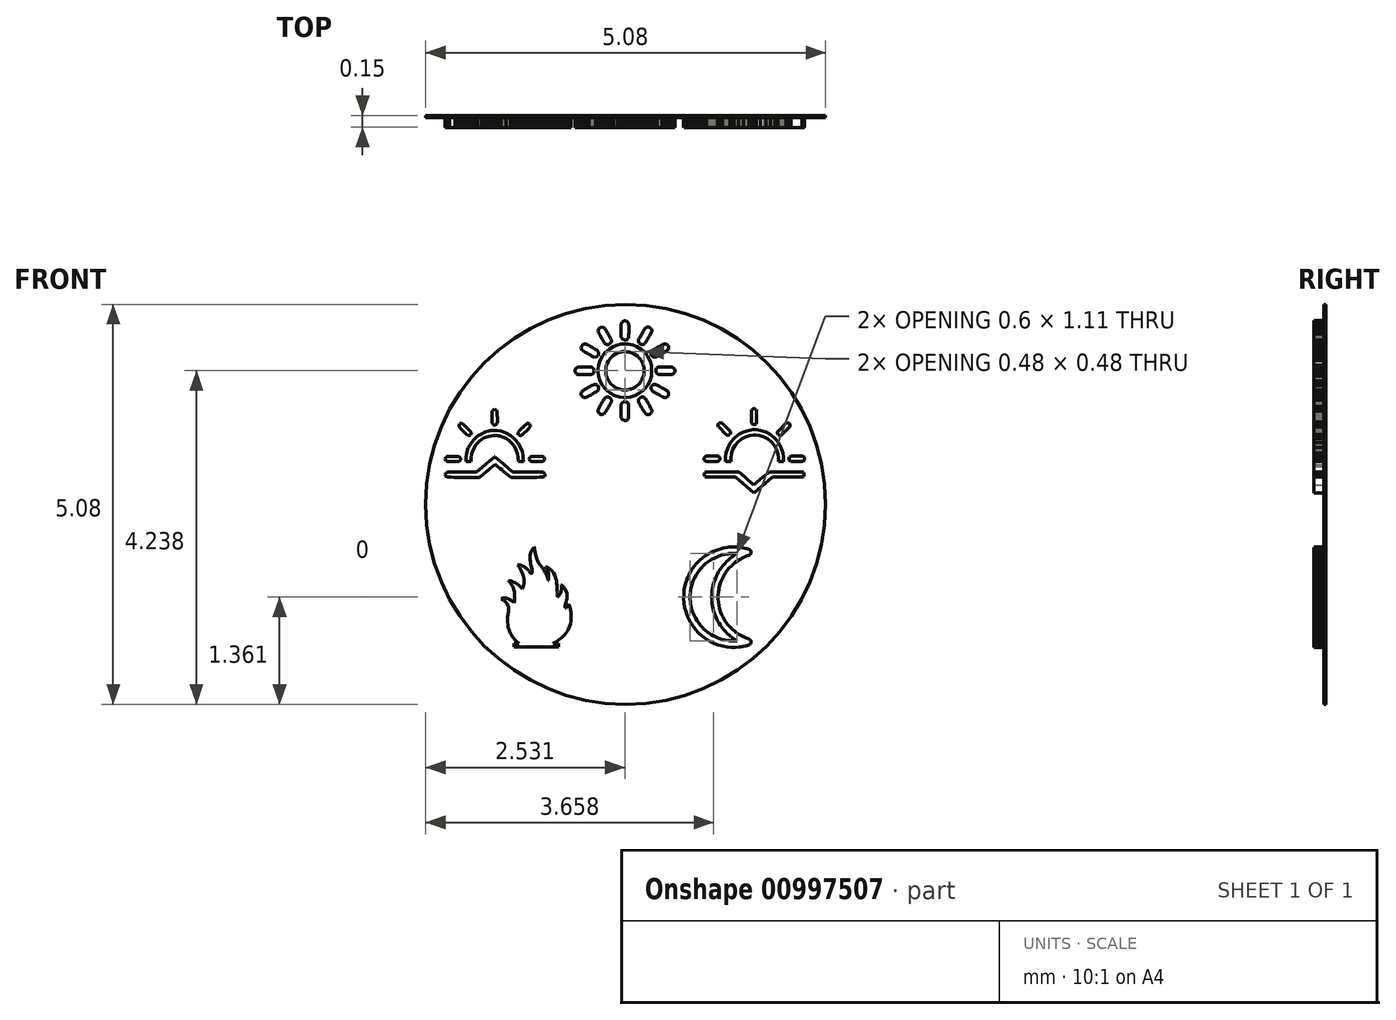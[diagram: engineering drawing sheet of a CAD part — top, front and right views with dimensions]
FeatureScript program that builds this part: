
annotation { "Feature Type Name" : "Feature", "Feature Type Description" : "" }
export const myFeature = defineFeature(function(context is Context, id is Id, definition is map)
    precondition{}
    {
        {
            var Q0;
            Q0=qCreatedBy(makeId("Front.planeOp"),FACE);
            var sketch = newSketch(context, id + "F0", { "sketchPlane" : qUnion([Q0])});
            skCircle(sketch, "E0", {"center": v(0, 0) * mm, "radius": 2.54 * mm});
            skSolve(sketch);
        }
        {
            var Q0;
            Q0=makeQuery(id+"F0.imprint","IMPRINT",FACE,{"disambiguationData":[TD([[makeQuery(id+"F0.imprint","IMPRINT",EDGE,{"derivedFrom":sQuery(id+"F0.wireOp",EDGE,"E0")}),1.0]])]});
            extrude(context, id + "F1", {"entities" : qUnion([Q0]), "depth" : 0.03 * mm, "offsetDistance" : 25.4 * mm});
        }
        {
            var Q0;
            Q0=makeQuery(id+"F1.opExtrude","CAP_FACE",FACE,{"disambiguationData":[OSD([sQuery(id+"F0.wireOp",EDGE,"E0"),sQuery(id+"F0.wireOp",EDGE,"ANRrlyus-TsXj-KHkA-7Rkr-odwGKdxKpd92")])],"isStart":false});
            var sketch = newSketch(context, id + "F2", { "sketchPlane" : qUnion([Q0])});
            skLineSegment(sketch, "E1", {"start": v(1.99, 0.89) * mm, "end": v(2.08, 0.98) * mm});
            skLineSegment(sketch, "E2", {"start": v(2.08, 0.98) * mm, "end": v(2.08, 0.98) * mm});
            skLineSegment(sketch, "E3", {"start": v(2.08, 0.98) * mm, "end": v(2.09, 1) * mm});
            skLineSegment(sketch, "E4", {"start": v(2.09, 1) * mm, "end": v(2.09, 1) * mm});
            skLineSegment(sketch, "E5", {"start": v(2.09, 1) * mm, "end": v(2.09, 1.02) * mm});
            skLineSegment(sketch, "E6", {"start": v(2.09, 1.02) * mm, "end": v(2.08, 1.03) * mm});
            skLineSegment(sketch, "E7", {"start": v(2.08, 1.03) * mm, "end": v(2.08, 1.03) * mm});
            skLineSegment(sketch, "E8", {"start": v(2.08, 1.03) * mm, "end": v(2.07, 1.04) * mm});
            skLineSegment(sketch, "E9", {"start": v(2.07, 1.04) * mm, "end": v(2.06, 1.04) * mm});
            skLineSegment(sketch, "E10", {"start": v(2.06, 1.04) * mm, "end": v(2.04, 1.04) * mm});
            skLineSegment(sketch, "E11", {"start": v(2.04, 1.04) * mm, "end": v(2.03, 1.03) * mm});
            skLineSegment(sketch, "E12", {"start": v(2.03, 1.03) * mm, "end": v(2.03, 1.03) * mm});
            skLineSegment(sketch, "E13", {"start": v(2.03, 1.03) * mm, "end": v(1.94, 0.93) * mm});
            skLineSegment(sketch, "E14", {"start": v(1.94, 0.93) * mm, "end": v(1.94, 0.93) * mm});
            skLineSegment(sketch, "E15", {"start": v(1.94, 0.93) * mm, "end": v(1.93, 0.92) * mm});
            skLineSegment(sketch, "E16", {"start": v(1.93, 0.92) * mm, "end": v(1.93, 0.91) * mm});
            skLineSegment(sketch, "E17", {"start": v(1.93, 0.91) * mm, "end": v(1.93, 0.9) * mm});
            skLineSegment(sketch, "E18", {"start": v(1.93, 0.9) * mm, "end": v(1.94, 0.9) * mm});
            skLineSegment(sketch, "E19", {"start": v(1.94, 0.9) * mm, "end": v(1.94, 0.89) * mm});
            skLineSegment(sketch, "E20", {"start": v(1.94, 0.89) * mm, "end": v(1.94, 0.89) * mm});
            skLineSegment(sketch, "E21", {"start": v(1.94, 0.89) * mm, "end": v(1.95, 0.88) * mm});
            skLineSegment(sketch, "E22", {"start": v(1.95, 0.88) * mm, "end": v(1.96, 0.88) * mm});
            skLineSegment(sketch, "E23", {"start": v(1.96, 0.88) * mm, "end": v(1.98, 0.88) * mm});
            skLineSegment(sketch, "E24", {"start": v(1.98, 0.88) * mm, "end": v(1.98, 0.89) * mm});
            skLineSegment(sketch, "E25", {"start": v(1.98, 0.89) * mm, "end": v(1.99, 0.89) * mm});
            skLineSegment(sketch, "E26", {"start": v(1.63, 1.01) * mm, "end": v(1.63, 1.01) * mm});
            skLineSegment(sketch, "E27", {"start": v(1.63, 1.01) * mm, "end": v(1.65, 1.02) * mm});
            skLineSegment(sketch, "E28", {"start": v(1.65, 1.02) * mm, "end": v(1.66, 1.02) * mm});
            skLineSegment(sketch, "E29", {"start": v(1.66, 1.02) * mm, "end": v(1.66, 1.03) * mm});
            skLineSegment(sketch, "E30", {"start": v(1.66, 1.03) * mm, "end": v(1.66, 1.04) * mm});
            skLineSegment(sketch, "E31", {"start": v(1.66, 1.04) * mm, "end": v(1.66, 1.05) * mm});
            skLineSegment(sketch, "E32", {"start": v(1.66, 1.05) * mm, "end": v(1.66, 1.18) * mm});
            skLineSegment(sketch, "E33", {"start": v(1.66, 1.18) * mm, "end": v(1.66, 1.19) * mm});
            skLineSegment(sketch, "E34", {"start": v(1.66, 1.19) * mm, "end": v(1.66, 1.2) * mm});
            skLineSegment(sketch, "E35", {"start": v(1.66, 1.2) * mm, "end": v(1.66, 1.2) * mm});
            skLineSegment(sketch, "E36", {"start": v(1.66, 1.2) * mm, "end": v(1.65, 1.21) * mm});
            skLineSegment(sketch, "E37", {"start": v(1.65, 1.21) * mm, "end": v(1.63, 1.22) * mm});
            skLineSegment(sketch, "E38", {"start": v(1.63, 1.22) * mm, "end": v(1.63, 1.22) * mm});
            skLineSegment(sketch, "E39", {"start": v(1.63, 1.22) * mm, "end": v(1.62, 1.21) * mm});
            skLineSegment(sketch, "E40", {"start": v(1.62, 1.21) * mm, "end": v(1.6, 1.2) * mm});
            skLineSegment(sketch, "E41", {"start": v(1.6, 1.2) * mm, "end": v(1.6, 1.2) * mm});
            skLineSegment(sketch, "E42", {"start": v(1.6, 1.2) * mm, "end": v(1.6, 1.19) * mm});
            skLineSegment(sketch, "E43", {"start": v(1.6, 1.19) * mm, "end": v(1.6, 1.18) * mm});
            skLineSegment(sketch, "E44", {"start": v(1.6, 1.18) * mm, "end": v(1.6, 1.05) * mm});
            skLineSegment(sketch, "E45", {"start": v(1.6, 1.05) * mm, "end": v(1.6, 1.04) * mm});
            skLineSegment(sketch, "E46", {"start": v(1.6, 1.04) * mm, "end": v(1.6, 1.03) * mm});
            skLineSegment(sketch, "E47", {"start": v(1.6, 1.03) * mm, "end": v(1.6, 1.02) * mm});
            skLineSegment(sketch, "E48", {"start": v(1.6, 1.02) * mm, "end": v(1.62, 1.02) * mm});
            skLineSegment(sketch, "E49", {"start": v(1.62, 1.02) * mm, "end": v(1.63, 1.01) * mm});
            skLineSegment(sketch, "E50", {"start": v(2.07, 0.58) * mm, "end": v(2.07, 0.58) * mm});
            skLineSegment(sketch, "E51", {"start": v(2.07, 0.58) * mm, "end": v(2.07, 0.57) * mm});
            skLineSegment(sketch, "E52", {"start": v(2.07, 0.57) * mm, "end": v(2.08, 0.56) * mm});
            skLineSegment(sketch, "E53", {"start": v(2.08, 0.56) * mm, "end": v(2.1, 0.55) * mm});
            skLineSegment(sketch, "E54", {"start": v(2.1, 0.55) * mm, "end": v(2.1, 0.55) * mm});
            skLineSegment(sketch, "E55", {"start": v(2.1, 0.55) * mm, "end": v(2.24, 0.55) * mm});
            skLineSegment(sketch, "E56", {"start": v(2.24, 0.55) * mm, "end": v(2.24, 0.55) * mm});
            skLineSegment(sketch, "E57", {"start": v(2.24, 0.55) * mm, "end": v(2.25, 0.55) * mm});
            skLineSegment(sketch, "E58", {"start": v(2.25, 0.55) * mm, "end": v(2.26, 0.56) * mm});
            skLineSegment(sketch, "E59", {"start": v(2.26, 0.56) * mm, "end": v(2.27, 0.57) * mm});
            skLineSegment(sketch, "E60", {"start": v(2.27, 0.57) * mm, "end": v(2.27, 0.58) * mm});
            skLineSegment(sketch, "E61", {"start": v(2.27, 0.58) * mm, "end": v(2.27, 0.58) * mm});
            skLineSegment(sketch, "E62", {"start": v(2.27, 0.58) * mm, "end": v(2.27, 0.6) * mm});
            skLineSegment(sketch, "E63", {"start": v(2.27, 0.6) * mm, "end": v(2.26, 0.6) * mm});
            skLineSegment(sketch, "E64", {"start": v(2.26, 0.6) * mm, "end": v(2.25, 0.61) * mm});
            skLineSegment(sketch, "E65", {"start": v(2.25, 0.61) * mm, "end": v(2.24, 0.61) * mm});
            skLineSegment(sketch, "E66", {"start": v(2.24, 0.61) * mm, "end": v(2.24, 0.61) * mm});
            skLineSegment(sketch, "E67", {"start": v(2.24, 0.61) * mm, "end": v(2.1, 0.61) * mm});
            skLineSegment(sketch, "E68", {"start": v(2.1, 0.61) * mm, "end": v(2.1, 0.61) * mm});
            skLineSegment(sketch, "E69", {"start": v(2.1, 0.61) * mm, "end": v(2.08, 0.6) * mm});
            skLineSegment(sketch, "E70", {"start": v(2.08, 0.6) * mm, "end": v(2.07, 0.6) * mm});
            skLineSegment(sketch, "E71", {"start": v(2.07, 0.6) * mm, "end": v(2.07, 0.58) * mm});
            skLineSegment(sketch, "E72", {"start": v(1.28, 0.89) * mm, "end": v(1.28, 0.89) * mm});
            skLineSegment(sketch, "E73", {"start": v(1.28, 0.89) * mm, "end": v(1.29, 0.88) * mm});
            skLineSegment(sketch, "E74", {"start": v(1.29, 0.88) * mm, "end": v(1.3, 0.88) * mm});
            skLineSegment(sketch, "E75", {"start": v(1.3, 0.88) * mm, "end": v(1.31, 0.88) * mm});
            skLineSegment(sketch, "E76", {"start": v(1.31, 0.88) * mm, "end": v(1.32, 0.89) * mm});
            skLineSegment(sketch, "E77", {"start": v(1.32, 0.89) * mm, "end": v(1.32, 0.89) * mm});
            skLineSegment(sketch, "E78", {"start": v(1.32, 0.89) * mm, "end": v(1.33, 0.9) * mm});
            skLineSegment(sketch, "E79", {"start": v(1.33, 0.9) * mm, "end": v(1.33, 0.9) * mm});
            skLineSegment(sketch, "E80", {"start": v(1.33, 0.9) * mm, "end": v(1.33, 0.91) * mm});
            skLineSegment(sketch, "E81", {"start": v(1.33, 0.91) * mm, "end": v(1.33, 0.92) * mm});
            skLineSegment(sketch, "E82", {"start": v(1.33, 0.92) * mm, "end": v(1.33, 0.93) * mm});
            skLineSegment(sketch, "E83", {"start": v(1.33, 0.93) * mm, "end": v(1.32, 0.93) * mm});
            skLineSegment(sketch, "E84", {"start": v(1.32, 0.93) * mm, "end": v(1.23, 1.03) * mm});
            skLineSegment(sketch, "E85", {"start": v(1.23, 1.03) * mm, "end": v(1.23, 1.03) * mm});
            skLineSegment(sketch, "E86", {"start": v(1.23, 1.03) * mm, "end": v(1.22, 1.04) * mm});
            skLineSegment(sketch, "E87", {"start": v(1.22, 1.04) * mm, "end": v(1.2, 1.04) * mm});
            skLineSegment(sketch, "E88", {"start": v(1.2, 1.04) * mm, "end": v(1.2, 1.04) * mm});
            skLineSegment(sketch, "E89", {"start": v(1.2, 1.04) * mm, "end": v(1.19, 1.03) * mm});
            skLineSegment(sketch, "E90", {"start": v(1.19, 1.03) * mm, "end": v(1.18, 1.03) * mm});
            skLineSegment(sketch, "E91", {"start": v(1.18, 1.03) * mm, "end": v(1.18, 1.03) * mm});
            skLineSegment(sketch, "E92", {"start": v(1.18, 1.03) * mm, "end": v(1.18, 1.02) * mm});
            skLineSegment(sketch, "E93", {"start": v(1.18, 1.02) * mm, "end": v(1.17, 1) * mm});
            skLineSegment(sketch, "E94", {"start": v(1.17, 1) * mm, "end": v(1.18, 1) * mm});
            skLineSegment(sketch, "E95", {"start": v(1.18, 1) * mm, "end": v(1.18, 0.98) * mm});
            skLineSegment(sketch, "E96", {"start": v(1.18, 0.98) * mm, "end": v(1.18, 0.98) * mm});
            skLineSegment(sketch, "E97", {"start": v(1.18, 0.98) * mm, "end": v(1.28, 0.89) * mm});
            skLineSegment(sketch, "E98", {"start": v(1.03, 0.55) * mm, "end": v(1.16, 0.55) * mm});
            skLineSegment(sketch, "E99", {"start": v(1.16, 0.55) * mm, "end": v(1.17, 0.55) * mm});
            skLineSegment(sketch, "E100", {"start": v(1.17, 0.55) * mm, "end": v(1.18, 0.55) * mm});
            skLineSegment(sketch, "E101", {"start": v(1.18, 0.55) * mm, "end": v(1.19, 0.56) * mm});
            skLineSegment(sketch, "E102", {"start": v(1.19, 0.56) * mm, "end": v(1.2, 0.57) * mm});
            skLineSegment(sketch, "E103", {"start": v(1.2, 0.57) * mm, "end": v(1.2, 0.58) * mm});
            skLineSegment(sketch, "E104", {"start": v(1.2, 0.58) * mm, "end": v(1.2, 0.58) * mm});
            skLineSegment(sketch, "E105", {"start": v(1.2, 0.58) * mm, "end": v(1.2, 0.6) * mm});
            skLineSegment(sketch, "E106", {"start": v(1.2, 0.6) * mm, "end": v(1.19, 0.6) * mm});
            skLineSegment(sketch, "E107", {"start": v(1.19, 0.6) * mm, "end": v(1.18, 0.61) * mm});
            skLineSegment(sketch, "E108", {"start": v(1.18, 0.61) * mm, "end": v(1.17, 0.61) * mm});
            skLineSegment(sketch, "E109", {"start": v(1.17, 0.61) * mm, "end": v(1.16, 0.61) * mm});
            skLineSegment(sketch, "E110", {"start": v(1.16, 0.61) * mm, "end": v(1.03, 0.61) * mm});
            skLineSegment(sketch, "E111", {"start": v(1.03, 0.61) * mm, "end": v(1.03, 0.61) * mm});
            skLineSegment(sketch, "E112", {"start": v(1.03, 0.61) * mm, "end": v(1.02, 0.61) * mm});
            skLineSegment(sketch, "E113", {"start": v(1.02, 0.61) * mm, "end": v(1, 0.6) * mm});
            skLineSegment(sketch, "E114", {"start": v(1, 0.6) * mm, "end": v(1, 0.6) * mm});
            skLineSegment(sketch, "E115", {"start": v(1, 0.6) * mm, "end": v(1, 0.58) * mm});
            skLineSegment(sketch, "E116", {"start": v(1, 0.58) * mm, "end": v(1, 0.58) * mm});
            skLineSegment(sketch, "E117", {"start": v(1, 0.58) * mm, "end": v(1, 0.57) * mm});
            skLineSegment(sketch, "E118", {"start": v(1, 0.57) * mm, "end": v(1, 0.56) * mm});
            skLineSegment(sketch, "E119", {"start": v(1, 0.56) * mm, "end": v(1.02, 0.55) * mm});
            skLineSegment(sketch, "E120", {"start": v(1.02, 0.55) * mm, "end": v(1.03, 0.55) * mm});
            skLineSegment(sketch, "E121", {"start": v(1.03, 0.55) * mm, "end": v(1.03, 0.55) * mm});
            skLineSegment(sketch, "E122", {"start": v(2.23, 0.41) * mm, "end": v(1.82, 0.41) * mm});
            skLineSegment(sketch, "E123", {"start": v(1.82, 0.41) * mm, "end": v(1.74, 0.35) * mm});
            skLineSegment(sketch, "E124", {"start": v(1.74, 0.35) * mm, "end": v(1.62, 0.25) * mm});
            skLineSegment(sketch, "E125", {"start": v(1.62, 0.25) * mm, "end": v(1.52, 0.35) * mm});
            skLineSegment(sketch, "E126", {"start": v(1.52, 0.35) * mm, "end": v(1.44, 0.41) * mm});
            skLineSegment(sketch, "E127", {"start": v(1.44, 0.41) * mm, "end": v(1.03, 0.41) * mm});
            skLineSegment(sketch, "E128", {"start": v(1.03, 0.41) * mm, "end": v(1.03, 0.41) * mm});
            skLineSegment(sketch, "E129", {"start": v(1.03, 0.41) * mm, "end": v(1.02, 0.41) * mm});
            skLineSegment(sketch, "E130", {"start": v(1.02, 0.41) * mm, "end": v(1, 0.4) * mm});
            skLineSegment(sketch, "E131", {"start": v(1, 0.4) * mm, "end": v(1, 0.4) * mm});
            skLineSegment(sketch, "E132", {"start": v(1, 0.4) * mm, "end": v(1, 0.38) * mm});
            skLineSegment(sketch, "E133", {"start": v(1, 0.38) * mm, "end": v(1, 0.38) * mm});
            skLineSegment(sketch, "E134", {"start": v(1, 0.38) * mm, "end": v(1, 0.37) * mm});
            skLineSegment(sketch, "E135", {"start": v(1, 0.37) * mm, "end": v(1, 0.36) * mm});
            skLineSegment(sketch, "E136", {"start": v(1, 0.36) * mm, "end": v(1.02, 0.35) * mm});
            skLineSegment(sketch, "E137", {"start": v(1.02, 0.35) * mm, "end": v(1.03, 0.35) * mm});
            skLineSegment(sketch, "E138", {"start": v(1.03, 0.35) * mm, "end": v(1.03, 0.35) * mm});
            skLineSegment(sketch, "E139", {"start": v(1.03, 0.35) * mm, "end": v(1.4, 0.35) * mm});
            skLineSegment(sketch, "E140", {"start": v(1.4, 0.35) * mm, "end": v(1.63, 0.15) * mm});
            skLineSegment(sketch, "E141", {"start": v(1.63, 0.15) * mm, "end": v(1.86, 0.35) * mm});
            skLineSegment(sketch, "E142", {"start": v(1.86, 0.35) * mm, "end": v(2.23, 0.35) * mm});
            skLineSegment(sketch, "E143", {"start": v(2.23, 0.35) * mm, "end": v(2.24, 0.35) * mm});
            skLineSegment(sketch, "E144", {"start": v(2.24, 0.35) * mm, "end": v(2.25, 0.35) * mm});
            skLineSegment(sketch, "E145", {"start": v(2.25, 0.35) * mm, "end": v(2.26, 0.36) * mm});
            skLineSegment(sketch, "E146", {"start": v(2.26, 0.36) * mm, "end": v(2.26, 0.37) * mm});
            skLineSegment(sketch, "E147", {"start": v(2.26, 0.37) * mm, "end": v(2.27, 0.38) * mm});
            skLineSegment(sketch, "E148", {"start": v(2.27, 0.38) * mm, "end": v(2.27, 0.38) * mm});
            skLineSegment(sketch, "E149", {"start": v(2.27, 0.38) * mm, "end": v(2.26, 0.4) * mm});
            skLineSegment(sketch, "E150", {"start": v(2.26, 0.4) * mm, "end": v(2.26, 0.4) * mm});
            skLineSegment(sketch, "E151", {"start": v(2.26, 0.4) * mm, "end": v(2.25, 0.41) * mm});
            skLineSegment(sketch, "E152", {"start": v(2.25, 0.41) * mm, "end": v(2.24, 0.41) * mm});
            skLineSegment(sketch, "E153", {"start": v(2.24, 0.41) * mm, "end": v(2.23, 0.41) * mm});
            skLineSegment(sketch, "E154", {"start": v(1.27, 0.55) * mm, "end": v(1.34, 0.55) * mm});
            skLineSegment(sketch, "E155", {"start": v(1.34, 0.55) * mm, "end": v(1.34, 0.55) * mm});
            skLineSegment(sketch, "E156", {"start": v(1.34, 0.55) * mm, "end": v(1.34, 0.56) * mm});
            skLineSegment(sketch, "E157", {"start": v(1.34, 0.56) * mm, "end": v(1.34, 0.58) * mm});
            skLineSegment(sketch, "E158", {"start": v(1.34, 0.58) * mm, "end": v(1.34, 0.58) * mm});
            skLineSegment(sketch, "E159", {"start": v(1.34, 0.58) * mm, "end": v(1.34, 0.6) * mm});
            skLineSegment(sketch, "E160", {"start": v(1.34, 0.6) * mm, "end": v(1.34, 0.64) * mm});
            skLineSegment(sketch, "E161", {"start": v(1.34, 0.64) * mm, "end": v(1.36, 0.7) * mm});
            skLineSegment(sketch, "E162", {"start": v(1.36, 0.7) * mm, "end": v(1.39, 0.75) * mm});
            skLineSegment(sketch, "E163", {"start": v(1.39, 0.75) * mm, "end": v(1.42, 0.8) * mm});
            skLineSegment(sketch, "E164", {"start": v(1.42, 0.8) * mm, "end": v(1.47, 0.83) * mm});
            skLineSegment(sketch, "E165", {"start": v(1.47, 0.83) * mm, "end": v(1.52, 0.86) * mm});
            skLineSegment(sketch, "E166", {"start": v(1.52, 0.86) * mm, "end": v(1.58, 0.88) * mm});
            skLineSegment(sketch, "E167", {"start": v(1.58, 0.88) * mm, "end": v(1.62, 0.88) * mm});
            skLineSegment(sketch, "E168", {"start": v(1.62, 0.88) * mm, "end": v(1.64, 0.88) * mm});
            skLineSegment(sketch, "E169", {"start": v(1.64, 0.88) * mm, "end": v(1.65, 0.88) * mm});
            skLineSegment(sketch, "E170", {"start": v(1.65, 0.88) * mm, "end": v(1.7, 0.88) * mm});
            skLineSegment(sketch, "E171", {"start": v(1.7, 0.88) * mm, "end": v(1.76, 0.86) * mm});
            skLineSegment(sketch, "E172", {"start": v(1.76, 0.86) * mm, "end": v(1.8, 0.83) * mm});
            skLineSegment(sketch, "E173", {"start": v(1.8, 0.83) * mm, "end": v(1.85, 0.8) * mm});
            skLineSegment(sketch, "E174", {"start": v(1.85, 0.8) * mm, "end": v(1.89, 0.75) * mm});
            skLineSegment(sketch, "E175", {"start": v(1.89, 0.75) * mm, "end": v(1.92, 0.7) * mm});
            skLineSegment(sketch, "E176", {"start": v(1.92, 0.7) * mm, "end": v(1.93, 0.64) * mm});
            skLineSegment(sketch, "E177", {"start": v(1.93, 0.64) * mm, "end": v(1.94, 0.6) * mm});
            skLineSegment(sketch, "E178", {"start": v(1.94, 0.6) * mm, "end": v(1.94, 0.58) * mm});
            skLineSegment(sketch, "E179", {"start": v(1.94, 0.58) * mm, "end": v(1.94, 0.58) * mm});
            skLineSegment(sketch, "E180", {"start": v(1.94, 0.58) * mm, "end": v(1.94, 0.56) * mm});
            skLineSegment(sketch, "E181", {"start": v(1.94, 0.56) * mm, "end": v(1.94, 0.55) * mm});
            skLineSegment(sketch, "E182", {"start": v(1.94, 0.55) * mm, "end": v(1.94, 0.55) * mm});
            skLineSegment(sketch, "E183", {"start": v(1.94, 0.55) * mm, "end": v(2, 0.55) * mm});
            skLineSegment(sketch, "E184", {"start": v(2, 0.55) * mm, "end": v(2, 0.55) * mm});
            skLineSegment(sketch, "E185", {"start": v(2, 0.55) * mm, "end": v(2, 0.56) * mm});
            skLineSegment(sketch, "E186", {"start": v(2, 0.56) * mm, "end": v(2, 0.58) * mm});
            skLineSegment(sketch, "E187", {"start": v(2, 0.58) * mm, "end": v(2, 0.58) * mm});
            skLineSegment(sketch, "E188", {"start": v(2, 0.58) * mm, "end": v(2, 0.6) * mm});
            skLineSegment(sketch, "E189", {"start": v(2, 0.6) * mm, "end": v(2, 0.65) * mm});
            skLineSegment(sketch, "E190", {"start": v(2, 0.65) * mm, "end": v(1.98, 0.72) * mm});
            skLineSegment(sketch, "E191", {"start": v(1.98, 0.72) * mm, "end": v(1.94, 0.79) * mm});
            skLineSegment(sketch, "E192", {"start": v(1.94, 0.79) * mm, "end": v(1.9, 0.84) * mm});
            skLineSegment(sketch, "E193", {"start": v(1.9, 0.84) * mm, "end": v(1.84, 0.88) * mm});
            skLineSegment(sketch, "E194", {"start": v(1.84, 0.88) * mm, "end": v(1.78, 0.92) * mm});
            skLineSegment(sketch, "E195", {"start": v(1.78, 0.92) * mm, "end": v(1.71, 0.94) * mm});
            skLineSegment(sketch, "E196", {"start": v(1.71, 0.94) * mm, "end": v(1.66, 0.95) * mm});
            skLineSegment(sketch, "E197", {"start": v(1.66, 0.95) * mm, "end": v(1.64, 0.95) * mm});
            skLineSegment(sketch, "E198", {"start": v(1.64, 0.95) * mm, "end": v(1.62, 0.95) * mm});
            skLineSegment(sketch, "E199", {"start": v(1.62, 0.95) * mm, "end": v(1.56, 0.94) * mm});
            skLineSegment(sketch, "E200", {"start": v(1.56, 0.94) * mm, "end": v(1.5, 0.92) * mm});
            skLineSegment(sketch, "E201", {"start": v(1.5, 0.92) * mm, "end": v(1.43, 0.88) * mm});
            skLineSegment(sketch, "E202", {"start": v(1.43, 0.88) * mm, "end": v(1.38, 0.84) * mm});
            skLineSegment(sketch, "E203", {"start": v(1.38, 0.84) * mm, "end": v(1.33, 0.79) * mm});
            skLineSegment(sketch, "E204", {"start": v(1.33, 0.79) * mm, "end": v(1.3, 0.72) * mm});
            skLineSegment(sketch, "E205", {"start": v(1.3, 0.72) * mm, "end": v(1.28, 0.65) * mm});
            skLineSegment(sketch, "E206", {"start": v(1.28, 0.65) * mm, "end": v(1.27, 0.6) * mm});
            skLineSegment(sketch, "E207", {"start": v(1.27, 0.6) * mm, "end": v(1.27, 0.58) * mm});
            skLineSegment(sketch, "E208", {"start": v(1.27, 0.58) * mm, "end": v(1.27, 0.58) * mm});
            skLineSegment(sketch, "E209", {"start": v(1.27, 0.58) * mm, "end": v(1.27, 0.57) * mm});
            skLineSegment(sketch, "E210", {"start": v(1.27, 0.57) * mm, "end": v(1.27, 0.56) * mm});
            skLineSegment(sketch, "E211", {"start": v(1.27, 0.56) * mm, "end": v(1.27, 0.56) * mm});
            skLineSegment(sketch, "E212", {"start": v(1.27, 0.56) * mm, "end": v(1.27, 0.55) * mm});
            skLineSegment(sketch, "E213", {"start": v(1.27, 0.55) * mm, "end": v(1.27, 0.55) * mm});
            skSolve(sketch);
        }
        {
            var Q0;
            Q0=makeQuery(id+"F1.opExtrude","CAP_FACE",FACE,{"disambiguationData":[OSD([sQuery(id+"F0.wireOp",EDGE,"E0"),sQuery(id+"F0.wireOp",EDGE,"ANRrlyus-TsXj-KHkA-7Rkr-odwGKdxKpd92")])],"isStart":false});
            var sketch = newSketch(context, id + "F3", { "sketchPlane" : qUnion([Q0])});
            skLineSegment(sketch, "E214", {"start": v(-1.69, 1.2) * mm, "end": v(-1.69, 1.2) * mm});
            skLineSegment(sketch, "E215", {"start": v(-1.69, 1.2) * mm, "end": v(-1.7, 1.19) * mm});
            skLineSegment(sketch, "E216", {"start": v(-1.7, 1.19) * mm, "end": v(-1.7, 1.18) * mm});
            skLineSegment(sketch, "E217", {"start": v(-1.7, 1.18) * mm, "end": v(-1.7, 1.17) * mm});
            skLineSegment(sketch, "E218", {"start": v(-1.7, 1.17) * mm, "end": v(-1.7, 1.16) * mm});
            skLineSegment(sketch, "E219", {"start": v(-1.7, 1.16) * mm, "end": v(-1.7, 1.15) * mm});
            skLineSegment(sketch, "E220", {"start": v(-1.7, 1.15) * mm, "end": v(-1.7, 1.13) * mm});
            skLineSegment(sketch, "E221", {"start": v(-1.7, 1.13) * mm, "end": v(-1.7, 1.11) * mm});
            skLineSegment(sketch, "E222", {"start": v(-1.7, 1.11) * mm, "end": v(-1.7, 1.1) * mm});
            skLineSegment(sketch, "E223", {"start": v(-1.7, 1.1) * mm, "end": v(-1.7, 1.1) * mm});
            skLineSegment(sketch, "E224", {"start": v(-1.7, 1.1) * mm, "end": v(-1.7, 1.08) * mm});
            skLineSegment(sketch, "E225", {"start": v(-1.7, 1.08) * mm, "end": v(-1.7, 1.07) * mm});
            skLineSegment(sketch, "E226", {"start": v(-1.7, 1.07) * mm, "end": v(-1.7, 1.05) * mm});
            skLineSegment(sketch, "E227", {"start": v(-1.7, 1.05) * mm, "end": v(-1.7, 1.04) * mm});
            skLineSegment(sketch, "E228", {"start": v(-1.7, 1.04) * mm, "end": v(-1.7, 1.03) * mm});
            skLineSegment(sketch, "E229", {"start": v(-1.7, 1.03) * mm, "end": v(-1.7, 1.03) * mm});
            skLineSegment(sketch, "E230", {"start": v(-1.7, 1.03) * mm, "end": v(-1.69, 1.02) * mm});
            skLineSegment(sketch, "E231", {"start": v(-1.69, 1.02) * mm, "end": v(-1.69, 1.02) * mm});
            skLineSegment(sketch, "E232", {"start": v(-1.69, 1.02) * mm, "end": v(-1.68, 1.02) * mm});
            skLineSegment(sketch, "E233", {"start": v(-1.68, 1.02) * mm, "end": v(-1.67, 1.01) * mm});
            skLineSegment(sketch, "E234", {"start": v(-1.67, 1.01) * mm, "end": v(-1.66, 1) * mm});
            skLineSegment(sketch, "E235", {"start": v(-1.66, 1) * mm, "end": v(-1.65, 1.01) * mm});
            skLineSegment(sketch, "E236", {"start": v(-1.65, 1.01) * mm, "end": v(-1.64, 1.02) * mm});
            skLineSegment(sketch, "E237", {"start": v(-1.64, 1.02) * mm, "end": v(-1.64, 1.02) * mm});
            skLineSegment(sketch, "E238", {"start": v(-1.64, 1.02) * mm, "end": v(-1.63, 1.03) * mm});
            skLineSegment(sketch, "E239", {"start": v(-1.63, 1.03) * mm, "end": v(-1.63, 1.05) * mm});
            skLineSegment(sketch, "E240", {"start": v(-1.63, 1.05) * mm, "end": v(-1.63, 1.07) * mm});
            skLineSegment(sketch, "E241", {"start": v(-1.63, 1.07) * mm, "end": v(-1.63, 1.1) * mm});
            skLineSegment(sketch, "E242", {"start": v(-1.63, 1.1) * mm, "end": v(-1.63, 1.11) * mm});
            skLineSegment(sketch, "E243", {"start": v(-1.63, 1.11) * mm, "end": v(-1.63, 1.12) * mm});
            skLineSegment(sketch, "E244", {"start": v(-1.63, 1.12) * mm, "end": v(-1.63, 1.14) * mm});
            skLineSegment(sketch, "E245", {"start": v(-1.63, 1.14) * mm, "end": v(-1.63, 1.15) * mm});
            skLineSegment(sketch, "E246", {"start": v(-1.63, 1.15) * mm, "end": v(-1.63, 1.17) * mm});
            skLineSegment(sketch, "E247", {"start": v(-1.63, 1.17) * mm, "end": v(-1.63, 1.18) * mm});
            skLineSegment(sketch, "E248", {"start": v(-1.63, 1.18) * mm, "end": v(-1.63, 1.19) * mm});
            skLineSegment(sketch, "E249", {"start": v(-1.63, 1.19) * mm, "end": v(-1.64, 1.2) * mm});
            skLineSegment(sketch, "E250", {"start": v(-1.64, 1.2) * mm, "end": v(-1.64, 1.2) * mm});
            skLineSegment(sketch, "E251", {"start": v(-1.64, 1.2) * mm, "end": v(-1.65, 1.2) * mm});
            skLineSegment(sketch, "E252", {"start": v(-1.65, 1.2) * mm, "end": v(-1.66, 1.2) * mm});
            skLineSegment(sketch, "E253", {"start": v(-1.66, 1.2) * mm, "end": v(-1.68, 1.2) * mm});
            skLineSegment(sketch, "E254", {"start": v(-1.68, 1.2) * mm, "end": v(-1.69, 1.2) * mm});
            skLineSegment(sketch, "E255", {"start": v(-2.1, 1.02) * mm, "end": v(-2.1, 1.02) * mm});
            skLineSegment(sketch, "E256", {"start": v(-2.1, 1.02) * mm, "end": v(-2.11, 1) * mm});
            skLineSegment(sketch, "E257", {"start": v(-2.11, 1) * mm, "end": v(-2.12, 1) * mm});
            skLineSegment(sketch, "E258", {"start": v(-2.12, 1) * mm, "end": v(-2.12, 1) * mm});
            skLineSegment(sketch, "E259", {"start": v(-2.12, 1) * mm, "end": v(-2.11, 0.99) * mm});
            skLineSegment(sketch, "E260", {"start": v(-2.11, 0.99) * mm, "end": v(-2.1, 0.97) * mm});
            skLineSegment(sketch, "E261", {"start": v(-2.1, 0.97) * mm, "end": v(-2.08, 0.95) * mm});
            skLineSegment(sketch, "E262", {"start": v(-2.08, 0.95) * mm, "end": v(-2.06, 0.93) * mm});
            skLineSegment(sketch, "E263", {"start": v(-2.06, 0.93) * mm, "end": v(-2.04, 0.9) * mm});
            skLineSegment(sketch, "E264", {"start": v(-2.04, 0.9) * mm, "end": v(-2.02, 0.89) * mm});
            skLineSegment(sketch, "E265", {"start": v(-2.02, 0.89) * mm, "end": v(-2, 0.88) * mm});
            skLineSegment(sketch, "E266", {"start": v(-2, 0.88) * mm, "end": v(-2, 0.87) * mm});
            skLineSegment(sketch, "E267", {"start": v(-2, 0.87) * mm, "end": v(-2, 0.87) * mm});
            skLineSegment(sketch, "E268", {"start": v(-2, 0.87) * mm, "end": v(-1.98, 0.88) * mm});
            skLineSegment(sketch, "E269", {"start": v(-1.98, 0.88) * mm, "end": v(-1.97, 0.88) * mm});
            skLineSegment(sketch, "E270", {"start": v(-1.97, 0.88) * mm, "end": v(-1.96, 0.9) * mm});
            skLineSegment(sketch, "E271", {"start": v(-1.96, 0.9) * mm, "end": v(-1.96, 0.9) * mm});
            skLineSegment(sketch, "E272", {"start": v(-1.96, 0.9) * mm, "end": v(-1.96, 0.91) * mm});
            skLineSegment(sketch, "E273", {"start": v(-1.96, 0.91) * mm, "end": v(-1.98, 0.93) * mm});
            skLineSegment(sketch, "E274", {"start": v(-1.98, 0.93) * mm, "end": v(-2, 0.95) * mm});
            skLineSegment(sketch, "E275", {"start": v(-2, 0.95) * mm, "end": v(-2.02, 0.97) * mm});
            skLineSegment(sketch, "E276", {"start": v(-2.02, 0.97) * mm, "end": v(-2.04, 1) * mm});
            skLineSegment(sketch, "E277", {"start": v(-2.04, 1) * mm, "end": v(-2.06, 1.01) * mm});
            skLineSegment(sketch, "E278", {"start": v(-2.06, 1.01) * mm, "end": v(-2.08, 1.03) * mm});
            skLineSegment(sketch, "E279", {"start": v(-2.08, 1.03) * mm, "end": v(-2.08, 1.03) * mm});
            skLineSegment(sketch, "E280", {"start": v(-2.08, 1.03) * mm, "end": v(-2.09, 1.03) * mm});
            skLineSegment(sketch, "E281", {"start": v(-2.09, 1.03) * mm, "end": v(-2.1, 1.03) * mm});
            skLineSegment(sketch, "E282", {"start": v(-2.1, 1.03) * mm, "end": v(-2.1, 1.02) * mm});
            skLineSegment(sketch, "E283", {"start": v(-1.31, 0.97) * mm, "end": v(-1.32, 0.96) * mm});
            skLineSegment(sketch, "E284", {"start": v(-1.32, 0.96) * mm, "end": v(-1.35, 0.94) * mm});
            skLineSegment(sketch, "E285", {"start": v(-1.35, 0.94) * mm, "end": v(-1.36, 0.91) * mm});
            skLineSegment(sketch, "E286", {"start": v(-1.36, 0.91) * mm, "end": v(-1.37, 0.9) * mm});
            skLineSegment(sketch, "E287", {"start": v(-1.37, 0.9) * mm, "end": v(-1.36, 0.88) * mm});
            skLineSegment(sketch, "E288", {"start": v(-1.36, 0.88) * mm, "end": v(-1.35, 0.88) * mm});
            skLineSegment(sketch, "E289", {"start": v(-1.35, 0.88) * mm, "end": v(-1.35, 0.88) * mm});
            skLineSegment(sketch, "E290", {"start": v(-1.35, 0.88) * mm, "end": v(-1.34, 0.87) * mm});
            skLineSegment(sketch, "E291", {"start": v(-1.34, 0.87) * mm, "end": v(-1.33, 0.87) * mm});
            skLineSegment(sketch, "E292", {"start": v(-1.33, 0.87) * mm, "end": v(-1.33, 0.87) * mm});
            skLineSegment(sketch, "E293", {"start": v(-1.33, 0.87) * mm, "end": v(-1.32, 0.88) * mm});
            skLineSegment(sketch, "E294", {"start": v(-1.32, 0.88) * mm, "end": v(-1.32, 0.88) * mm});
            skLineSegment(sketch, "E295", {"start": v(-1.32, 0.88) * mm, "end": v(-1.3, 0.9) * mm});
            skLineSegment(sketch, "E296", {"start": v(-1.3, 0.9) * mm, "end": v(-1.28, 0.91) * mm});
            skLineSegment(sketch, "E297", {"start": v(-1.28, 0.91) * mm, "end": v(-1.26, 0.93) * mm});
            skLineSegment(sketch, "E298", {"start": v(-1.26, 0.93) * mm, "end": v(-1.24, 0.95) * mm});
            skLineSegment(sketch, "E299", {"start": v(-1.24, 0.95) * mm, "end": v(-1.22, 0.97) * mm});
            skLineSegment(sketch, "E300", {"start": v(-1.22, 0.97) * mm, "end": v(-1.21, 0.99) * mm});
            skLineSegment(sketch, "E301", {"start": v(-1.21, 0.99) * mm, "end": v(-1.2, 1) * mm});
            skLineSegment(sketch, "E302", {"start": v(-1.2, 1) * mm, "end": v(-1.2, 1) * mm});
            skLineSegment(sketch, "E303", {"start": v(-1.2, 1) * mm, "end": v(-1.21, 1) * mm});
            skLineSegment(sketch, "E304", {"start": v(-1.21, 1) * mm, "end": v(-1.22, 1.02) * mm});
            skLineSegment(sketch, "E305", {"start": v(-1.22, 1.02) * mm, "end": v(-1.23, 1.03) * mm});
            skLineSegment(sketch, "E306", {"start": v(-1.23, 1.03) * mm, "end": v(-1.24, 1.03) * mm});
            skLineSegment(sketch, "E307", {"start": v(-1.24, 1.03) * mm, "end": v(-1.24, 1.03) * mm});
            skLineSegment(sketch, "E308", {"start": v(-1.24, 1.03) * mm, "end": v(-1.25, 1.03) * mm});
            skLineSegment(sketch, "E309", {"start": v(-1.25, 1.03) * mm, "end": v(-1.25, 1.03) * mm});
            skLineSegment(sketch, "E310", {"start": v(-1.25, 1.03) * mm, "end": v(-1.27, 1.01) * mm});
            skLineSegment(sketch, "E311", {"start": v(-1.27, 1.01) * mm, "end": v(-1.29, 1) * mm});
            skLineSegment(sketch, "E312", {"start": v(-1.29, 1) * mm, "end": v(-1.3, 0.98) * mm});
            skLineSegment(sketch, "E313", {"start": v(-1.3, 0.98) * mm, "end": v(-1.31, 0.97) * mm});
            skLineSegment(sketch, "E314", {"start": v(-1.73, 0.93) * mm, "end": v(-1.74, 0.93) * mm});
            skLineSegment(sketch, "E315", {"start": v(-1.74, 0.93) * mm, "end": v(-1.78, 0.92) * mm});
            skLineSegment(sketch, "E316", {"start": v(-1.78, 0.92) * mm, "end": v(-1.83, 0.9) * mm});
            skLineSegment(sketch, "E317", {"start": v(-1.83, 0.9) * mm, "end": v(-1.88, 0.87) * mm});
            skLineSegment(sketch, "E318", {"start": v(-1.88, 0.87) * mm, "end": v(-1.91, 0.84) * mm});
            skLineSegment(sketch, "E319", {"start": v(-1.91, 0.84) * mm, "end": v(-1.92, 0.83) * mm});
            skLineSegment(sketch, "E320", {"start": v(-1.92, 0.83) * mm, "end": v(-1.93, 0.82) * mm});
            skLineSegment(sketch, "E321", {"start": v(-1.93, 0.82) * mm, "end": v(-1.97, 0.77) * mm});
            skLineSegment(sketch, "E322", {"start": v(-1.97, 0.77) * mm, "end": v(-2, 0.71) * mm});
            skLineSegment(sketch, "E323", {"start": v(-2, 0.71) * mm, "end": v(-2.02, 0.65) * mm});
            skLineSegment(sketch, "E324", {"start": v(-2.02, 0.65) * mm, "end": v(-2.03, 0.6) * mm});
            skLineSegment(sketch, "E325", {"start": v(-2.03, 0.6) * mm, "end": v(-2.03, 0.58) * mm});
            skLineSegment(sketch, "E326", {"start": v(-2.03, 0.58) * mm, "end": v(-2.03, 0.54) * mm});
            skLineSegment(sketch, "E327", {"start": v(-2.03, 0.54) * mm, "end": v(-1.96, 0.54) * mm});
            skLineSegment(sketch, "E328", {"start": v(-1.96, 0.54) * mm, "end": v(-1.96, 0.57) * mm});
            skLineSegment(sketch, "E329", {"start": v(-1.96, 0.57) * mm, "end": v(-1.96, 0.59) * mm});
            skLineSegment(sketch, "E330", {"start": v(-1.96, 0.59) * mm, "end": v(-1.96, 0.64) * mm});
            skLineSegment(sketch, "E331", {"start": v(-1.96, 0.64) * mm, "end": v(-1.93, 0.7) * mm});
            skLineSegment(sketch, "E332", {"start": v(-1.93, 0.7) * mm, "end": v(-1.9, 0.76) * mm});
            skLineSegment(sketch, "E333", {"start": v(-1.9, 0.76) * mm, "end": v(-1.86, 0.8) * mm});
            skLineSegment(sketch, "E334", {"start": v(-1.86, 0.8) * mm, "end": v(-1.8, 0.84) * mm});
            skLineSegment(sketch, "E335", {"start": v(-1.8, 0.84) * mm, "end": v(-1.74, 0.86) * mm});
            skLineSegment(sketch, "E336", {"start": v(-1.74, 0.86) * mm, "end": v(-1.68, 0.87) * mm});
            skLineSegment(sketch, "E337", {"start": v(-1.68, 0.87) * mm, "end": v(-1.63, 0.87) * mm});
            skLineSegment(sketch, "E338", {"start": v(-1.63, 0.87) * mm, "end": v(-1.61, 0.87) * mm});
            skLineSegment(sketch, "E339", {"start": v(-1.61, 0.87) * mm, "end": v(-1.6, 0.87) * mm});
            skLineSegment(sketch, "E340", {"start": v(-1.6, 0.87) * mm, "end": v(-1.56, 0.86) * mm});
            skLineSegment(sketch, "E341", {"start": v(-1.56, 0.86) * mm, "end": v(-1.51, 0.84) * mm});
            skLineSegment(sketch, "E342", {"start": v(-1.51, 0.84) * mm, "end": v(-1.47, 0.8) * mm});
            skLineSegment(sketch, "E343", {"start": v(-1.47, 0.8) * mm, "end": v(-1.44, 0.77) * mm});
            skLineSegment(sketch, "E344", {"start": v(-1.44, 0.77) * mm, "end": v(-1.41, 0.74) * mm});
            skLineSegment(sketch, "E345", {"start": v(-1.41, 0.74) * mm, "end": v(-1.39, 0.7) * mm});
            skLineSegment(sketch, "E346", {"start": v(-1.39, 0.7) * mm, "end": v(-1.37, 0.64) * mm});
            skLineSegment(sketch, "E347", {"start": v(-1.37, 0.64) * mm, "end": v(-1.37, 0.6) * mm});
            skLineSegment(sketch, "E348", {"start": v(-1.37, 0.6) * mm, "end": v(-1.37, 0.6) * mm});
            skLineSegment(sketch, "E349", {"start": v(-1.37, 0.6) * mm, "end": v(-1.36, 0.54) * mm});
            skLineSegment(sketch, "E350", {"start": v(-1.36, 0.54) * mm, "end": v(-1.3, 0.54) * mm});
            skLineSegment(sketch, "E351", {"start": v(-1.3, 0.54) * mm, "end": v(-1.3, 0.6) * mm});
            skLineSegment(sketch, "E352", {"start": v(-1.3, 0.6) * mm, "end": v(-1.3, 0.61) * mm});
            skLineSegment(sketch, "E353", {"start": v(-1.3, 0.61) * mm, "end": v(-1.31, 0.66) * mm});
            skLineSegment(sketch, "E354", {"start": v(-1.31, 0.66) * mm, "end": v(-1.33, 0.72) * mm});
            skLineSegment(sketch, "E355", {"start": v(-1.33, 0.72) * mm, "end": v(-1.36, 0.78) * mm});
            skLineSegment(sketch, "E356", {"start": v(-1.36, 0.78) * mm, "end": v(-1.4, 0.82) * mm});
            skLineSegment(sketch, "E357", {"start": v(-1.4, 0.82) * mm, "end": v(-1.4, 0.83) * mm});
            skLineSegment(sketch, "E358", {"start": v(-1.4, 0.83) * mm, "end": v(-1.42, 0.84) * mm});
            skLineSegment(sketch, "E359", {"start": v(-1.42, 0.84) * mm, "end": v(-1.46, 0.88) * mm});
            skLineSegment(sketch, "E360", {"start": v(-1.46, 0.88) * mm, "end": v(-1.52, 0.9) * mm});
            skLineSegment(sketch, "E361", {"start": v(-1.52, 0.9) * mm, "end": v(-1.58, 0.93) * mm});
            skLineSegment(sketch, "E362", {"start": v(-1.58, 0.93) * mm, "end": v(-1.63, 0.94) * mm});
            skLineSegment(sketch, "E363", {"start": v(-1.63, 0.94) * mm, "end": v(-1.65, 0.94) * mm});
            skLineSegment(sketch, "E364", {"start": v(-1.65, 0.94) * mm, "end": v(-1.65, 0.94) * mm});
            skLineSegment(sketch, "E365", {"start": v(-1.65, 0.94) * mm, "end": v(-1.67, 0.94) * mm});
            skLineSegment(sketch, "E366", {"start": v(-1.67, 0.94) * mm, "end": v(-1.7, 0.94) * mm});
            skLineSegment(sketch, "E367", {"start": v(-1.7, 0.94) * mm, "end": v(-1.72, 0.94) * mm});
            skLineSegment(sketch, "E368", {"start": v(-1.72, 0.94) * mm, "end": v(-1.73, 0.94) * mm});
            skLineSegment(sketch, "E369", {"start": v(-1.73, 0.94) * mm, "end": v(-1.73, 0.93) * mm});
            skLineSegment(sketch, "E370", {"start": v(-2.28, 0.6) * mm, "end": v(-2.28, 0.6) * mm});
            skLineSegment(sketch, "E371", {"start": v(-2.28, 0.6) * mm, "end": v(-2.29, 0.59) * mm});
            skLineSegment(sketch, "E372", {"start": v(-2.29, 0.59) * mm, "end": v(-2.3, 0.58) * mm});
            skLineSegment(sketch, "E373", {"start": v(-2.3, 0.58) * mm, "end": v(-2.3, 0.57) * mm});
            skLineSegment(sketch, "E374", {"start": v(-2.3, 0.57) * mm, "end": v(-2.28, 0.56) * mm});
            skLineSegment(sketch, "E375", {"start": v(-2.28, 0.56) * mm, "end": v(-2.28, 0.55) * mm});
            skLineSegment(sketch, "E376", {"start": v(-2.28, 0.55) * mm, "end": v(-2.28, 0.55) * mm});
            skLineSegment(sketch, "E377", {"start": v(-2.28, 0.55) * mm, "end": v(-2.27, 0.55) * mm});
            skLineSegment(sketch, "E378", {"start": v(-2.27, 0.55) * mm, "end": v(-2.27, 0.55) * mm});
            skLineSegment(sketch, "E379", {"start": v(-2.27, 0.55) * mm, "end": v(-2.26, 0.54) * mm});
            skLineSegment(sketch, "E380", {"start": v(-2.26, 0.54) * mm, "end": v(-2.25, 0.54) * mm});
            skLineSegment(sketch, "E381", {"start": v(-2.25, 0.54) * mm, "end": v(-2.24, 0.54) * mm});
            skLineSegment(sketch, "E382", {"start": v(-2.24, 0.54) * mm, "end": v(-2.22, 0.54) * mm});
            skLineSegment(sketch, "E383", {"start": v(-2.22, 0.54) * mm, "end": v(-2.2, 0.54) * mm});
            skLineSegment(sketch, "E384", {"start": v(-2.2, 0.54) * mm, "end": v(-2.2, 0.54) * mm});
            skLineSegment(sketch, "E385", {"start": v(-2.2, 0.54) * mm, "end": v(-2.19, 0.54) * mm});
            skLineSegment(sketch, "E386", {"start": v(-2.19, 0.54) * mm, "end": v(-2.17, 0.54) * mm});
            skLineSegment(sketch, "E387", {"start": v(-2.17, 0.54) * mm, "end": v(-2.15, 0.54) * mm});
            skLineSegment(sketch, "E388", {"start": v(-2.15, 0.54) * mm, "end": v(-2.14, 0.54) * mm});
            skLineSegment(sketch, "E389", {"start": v(-2.14, 0.54) * mm, "end": v(-2.13, 0.54) * mm});
            skLineSegment(sketch, "E390", {"start": v(-2.13, 0.54) * mm, "end": v(-2.12, 0.55) * mm});
            skLineSegment(sketch, "E391", {"start": v(-2.12, 0.55) * mm, "end": v(-2.11, 0.55) * mm});
            skLineSegment(sketch, "E392", {"start": v(-2.11, 0.55) * mm, "end": v(-2.1, 0.55) * mm});
            skLineSegment(sketch, "E393", {"start": v(-2.1, 0.55) * mm, "end": v(-2.1, 0.55) * mm});
            skLineSegment(sketch, "E394", {"start": v(-2.1, 0.55) * mm, "end": v(-2.1, 0.56) * mm});
            skLineSegment(sketch, "E395", {"start": v(-2.1, 0.56) * mm, "end": v(-2.1, 0.57) * mm});
            skLineSegment(sketch, "E396", {"start": v(-2.1, 0.57) * mm, "end": v(-2.1, 0.58) * mm});
            skLineSegment(sketch, "E397", {"start": v(-2.1, 0.58) * mm, "end": v(-2.1, 0.59) * mm});
            skLineSegment(sketch, "E398", {"start": v(-2.1, 0.59) * mm, "end": v(-2.1, 0.6) * mm});
            skLineSegment(sketch, "E399", {"start": v(-2.1, 0.6) * mm, "end": v(-2.1, 0.6) * mm});
            skLineSegment(sketch, "E400", {"start": v(-2.1, 0.6) * mm, "end": v(-2.11, 0.6) * mm});
            skLineSegment(sketch, "E401", {"start": v(-2.11, 0.6) * mm, "end": v(-2.12, 0.6) * mm});
            skLineSegment(sketch, "E402", {"start": v(-2.12, 0.6) * mm, "end": v(-2.13, 0.6) * mm});
            skLineSegment(sketch, "E403", {"start": v(-2.13, 0.6) * mm, "end": v(-2.14, 0.61) * mm});
            skLineSegment(sketch, "E404", {"start": v(-2.14, 0.61) * mm, "end": v(-2.15, 0.61) * mm});
            skLineSegment(sketch, "E405", {"start": v(-2.15, 0.61) * mm, "end": v(-2.17, 0.61) * mm});
            skLineSegment(sketch, "E406", {"start": v(-2.17, 0.61) * mm, "end": v(-2.19, 0.61) * mm});
            skLineSegment(sketch, "E407", {"start": v(-2.19, 0.61) * mm, "end": v(-2.2, 0.61) * mm});
            skLineSegment(sketch, "E408", {"start": v(-2.2, 0.61) * mm, "end": v(-2.2, 0.61) * mm});
            skLineSegment(sketch, "E409", {"start": v(-2.2, 0.61) * mm, "end": v(-2.22, 0.61) * mm});
            skLineSegment(sketch, "E410", {"start": v(-2.22, 0.61) * mm, "end": v(-2.24, 0.61) * mm});
            skLineSegment(sketch, "E411", {"start": v(-2.24, 0.61) * mm, "end": v(-2.25, 0.61) * mm});
            skLineSegment(sketch, "E412", {"start": v(-2.25, 0.61) * mm, "end": v(-2.26, 0.6) * mm});
            skLineSegment(sketch, "E413", {"start": v(-2.26, 0.6) * mm, "end": v(-2.27, 0.6) * mm});
            skLineSegment(sketch, "E414", {"start": v(-2.27, 0.6) * mm, "end": v(-2.27, 0.6) * mm});
            skLineSegment(sketch, "E415", {"start": v(-2.27, 0.6) * mm, "end": v(-2.28, 0.6) * mm});
            skLineSegment(sketch, "E416", {"start": v(-1.21, 0.6) * mm, "end": v(-1.21, 0.6) * mm});
            skLineSegment(sketch, "E417", {"start": v(-1.21, 0.6) * mm, "end": v(-1.22, 0.59) * mm});
            skLineSegment(sketch, "E418", {"start": v(-1.22, 0.59) * mm, "end": v(-1.23, 0.58) * mm});
            skLineSegment(sketch, "E419", {"start": v(-1.23, 0.58) * mm, "end": v(-1.22, 0.57) * mm});
            skLineSegment(sketch, "E420", {"start": v(-1.22, 0.57) * mm, "end": v(-1.22, 0.56) * mm});
            skLineSegment(sketch, "E421", {"start": v(-1.22, 0.56) * mm, "end": v(-1.21, 0.55) * mm});
            skLineSegment(sketch, "E422", {"start": v(-1.21, 0.55) * mm, "end": v(-1.21, 0.55) * mm});
            skLineSegment(sketch, "E423", {"start": v(-1.21, 0.55) * mm, "end": v(-1.2, 0.55) * mm});
            skLineSegment(sketch, "E424", {"start": v(-1.2, 0.55) * mm, "end": v(-1.2, 0.55) * mm});
            skLineSegment(sketch, "E425", {"start": v(-1.2, 0.55) * mm, "end": v(-1.2, 0.54) * mm});
            skLineSegment(sketch, "E426", {"start": v(-1.2, 0.54) * mm, "end": v(-1.18, 0.54) * mm});
            skLineSegment(sketch, "E427", {"start": v(-1.18, 0.54) * mm, "end": v(-1.17, 0.54) * mm});
            skLineSegment(sketch, "E428", {"start": v(-1.17, 0.54) * mm, "end": v(-1.15, 0.54) * mm});
            skLineSegment(sketch, "E429", {"start": v(-1.15, 0.54) * mm, "end": v(-1.13, 0.54) * mm});
            skLineSegment(sketch, "E430", {"start": v(-1.13, 0.54) * mm, "end": v(-1.13, 0.54) * mm});
            skLineSegment(sketch, "E431", {"start": v(-1.13, 0.54) * mm, "end": v(-1.12, 0.54) * mm});
            skLineSegment(sketch, "E432", {"start": v(-1.12, 0.54) * mm, "end": v(-1.1, 0.54) * mm});
            skLineSegment(sketch, "E433", {"start": v(-1.1, 0.54) * mm, "end": v(-1.09, 0.54) * mm});
            skLineSegment(sketch, "E434", {"start": v(-1.09, 0.54) * mm, "end": v(-1.07, 0.54) * mm});
            skLineSegment(sketch, "E435", {"start": v(-1.07, 0.54) * mm, "end": v(-1.06, 0.54) * mm});
            skLineSegment(sketch, "E436", {"start": v(-1.06, 0.54) * mm, "end": v(-1.05, 0.55) * mm});
            skLineSegment(sketch, "E437", {"start": v(-1.05, 0.55) * mm, "end": v(-1.05, 0.55) * mm});
            skLineSegment(sketch, "E438", {"start": v(-1.05, 0.55) * mm, "end": v(-1.04, 0.55) * mm});
            skLineSegment(sketch, "E439", {"start": v(-1.04, 0.55) * mm, "end": v(-1.04, 0.55) * mm});
            skLineSegment(sketch, "E440", {"start": v(-1.04, 0.55) * mm, "end": v(-1.04, 0.56) * mm});
            skLineSegment(sketch, "E441", {"start": v(-1.04, 0.56) * mm, "end": v(-1.03, 0.57) * mm});
            skLineSegment(sketch, "E442", {"start": v(-1.03, 0.57) * mm, "end": v(-1.03, 0.57) * mm});
            skLineSegment(sketch, "E443", {"start": v(-1.03, 0.57) * mm, "end": v(-1.03, 0.58) * mm});
            skLineSegment(sketch, "E444", {"start": v(-1.03, 0.58) * mm, "end": v(-1.03, 0.58) * mm});
            skLineSegment(sketch, "E445", {"start": v(-1.03, 0.58) * mm, "end": v(-1.03, 0.59) * mm});
            skLineSegment(sketch, "E446", {"start": v(-1.03, 0.59) * mm, "end": v(-1.04, 0.6) * mm});
            skLineSegment(sketch, "E447", {"start": v(-1.04, 0.6) * mm, "end": v(-1.04, 0.6) * mm});
            skLineSegment(sketch, "E448", {"start": v(-1.04, 0.6) * mm, "end": v(-1.05, 0.6) * mm});
            skLineSegment(sketch, "E449", {"start": v(-1.05, 0.6) * mm, "end": v(-1.05, 0.6) * mm});
            skLineSegment(sketch, "E450", {"start": v(-1.05, 0.6) * mm, "end": v(-1.06, 0.6) * mm});
            skLineSegment(sketch, "E451", {"start": v(-1.06, 0.6) * mm, "end": v(-1.07, 0.61) * mm});
            skLineSegment(sketch, "E452", {"start": v(-1.07, 0.61) * mm, "end": v(-1.08, 0.61) * mm});
            skLineSegment(sketch, "E453", {"start": v(-1.08, 0.61) * mm, "end": v(-1.1, 0.61) * mm});
            skLineSegment(sketch, "E454", {"start": v(-1.1, 0.61) * mm, "end": v(-1.12, 0.61) * mm});
            skLineSegment(sketch, "E455", {"start": v(-1.12, 0.61) * mm, "end": v(-1.12, 0.61) * mm});
            skLineSegment(sketch, "E456", {"start": v(-1.12, 0.61) * mm, "end": v(-1.13, 0.61) * mm});
            skLineSegment(sketch, "E457", {"start": v(-1.13, 0.61) * mm, "end": v(-1.15, 0.61) * mm});
            skLineSegment(sketch, "E458", {"start": v(-1.15, 0.61) * mm, "end": v(-1.16, 0.61) * mm});
            skLineSegment(sketch, "E459", {"start": v(-1.16, 0.61) * mm, "end": v(-1.18, 0.61) * mm});
            skLineSegment(sketch, "E460", {"start": v(-1.18, 0.61) * mm, "end": v(-1.19, 0.6) * mm});
            skLineSegment(sketch, "E461", {"start": v(-1.19, 0.6) * mm, "end": v(-1.2, 0.6) * mm});
            skLineSegment(sketch, "E462", {"start": v(-1.2, 0.6) * mm, "end": v(-1.2, 0.6) * mm});
            skLineSegment(sketch, "E463", {"start": v(-1.2, 0.6) * mm, "end": v(-1.21, 0.6) * mm});
            skLineSegment(sketch, "E464", {"start": v(-1.78, 0.5) * mm, "end": v(-1.9, 0.41) * mm});
            skLineSegment(sketch, "E465", {"start": v(-1.9, 0.41) * mm, "end": v(-2.08, 0.41) * mm});
            skLineSegment(sketch, "E466", {"start": v(-2.08, 0.41) * mm, "end": v(-2.1, 0.41) * mm});
            skLineSegment(sketch, "E467", {"start": v(-2.1, 0.41) * mm, "end": v(-2.14, 0.41) * mm});
            skLineSegment(sketch, "E468", {"start": v(-2.14, 0.41) * mm, "end": v(-2.18, 0.41) * mm});
            skLineSegment(sketch, "E469", {"start": v(-2.18, 0.41) * mm, "end": v(-2.22, 0.41) * mm});
            skLineSegment(sketch, "E470", {"start": v(-2.22, 0.41) * mm, "end": v(-2.24, 0.41) * mm});
            skLineSegment(sketch, "E471", {"start": v(-2.24, 0.41) * mm, "end": v(-2.26, 0.4) * mm});
            skLineSegment(sketch, "E472", {"start": v(-2.26, 0.4) * mm, "end": v(-2.27, 0.4) * mm});
            skLineSegment(sketch, "E473", {"start": v(-2.27, 0.4) * mm, "end": v(-2.27, 0.4) * mm});
            skLineSegment(sketch, "E474", {"start": v(-2.27, 0.4) * mm, "end": v(-2.28, 0.4) * mm});
            skLineSegment(sketch, "E475", {"start": v(-2.28, 0.4) * mm, "end": v(-2.28, 0.4) * mm});
            skLineSegment(sketch, "E476", {"start": v(-2.28, 0.4) * mm, "end": v(-2.29, 0.39) * mm});
            skLineSegment(sketch, "E477", {"start": v(-2.29, 0.39) * mm, "end": v(-2.3, 0.38) * mm});
            skLineSegment(sketch, "E478", {"start": v(-2.3, 0.38) * mm, "end": v(-2.3, 0.37) * mm});
            skLineSegment(sketch, "E479", {"start": v(-2.3, 0.37) * mm, "end": v(-2.28, 0.36) * mm});
            skLineSegment(sketch, "E480", {"start": v(-2.28, 0.36) * mm, "end": v(-2.28, 0.36) * mm});
            skLineSegment(sketch, "E481", {"start": v(-2.28, 0.36) * mm, "end": v(-2.28, 0.35) * mm});
            skLineSegment(sketch, "E482", {"start": v(-2.28, 0.35) * mm, "end": v(-2.28, 0.35) * mm});
            skLineSegment(sketch, "E483", {"start": v(-2.28, 0.35) * mm, "end": v(-2.27, 0.35) * mm});
            skLineSegment(sketch, "E484", {"start": v(-2.27, 0.35) * mm, "end": v(-2.26, 0.35) * mm});
            skLineSegment(sketch, "E485", {"start": v(-2.26, 0.35) * mm, "end": v(-2.24, 0.35) * mm});
            skLineSegment(sketch, "E486", {"start": v(-2.24, 0.35) * mm, "end": v(-2.22, 0.35) * mm});
            skLineSegment(sketch, "E487", {"start": v(-2.22, 0.35) * mm, "end": v(-2.18, 0.34) * mm});
            skLineSegment(sketch, "E488", {"start": v(-2.18, 0.34) * mm, "end": v(-2.13, 0.34) * mm});
            skLineSegment(sketch, "E489", {"start": v(-2.13, 0.34) * mm, "end": v(-2.08, 0.34) * mm});
            skLineSegment(sketch, "E490", {"start": v(-2.08, 0.34) * mm, "end": v(-2.06, 0.34) * mm});
            skLineSegment(sketch, "E491", {"start": v(-2.06, 0.34) * mm, "end": v(-1.86, 0.34) * mm});
            skLineSegment(sketch, "E492", {"start": v(-1.86, 0.34) * mm, "end": v(-1.76, 0.43) * mm});
            skLineSegment(sketch, "E493", {"start": v(-1.76, 0.43) * mm, "end": v(-1.75, 0.43) * mm});
            skLineSegment(sketch, "E494", {"start": v(-1.75, 0.43) * mm, "end": v(-1.72, 0.46) * mm});
            skLineSegment(sketch, "E495", {"start": v(-1.72, 0.46) * mm, "end": v(-1.69, 0.48) * mm});
            skLineSegment(sketch, "E496", {"start": v(-1.69, 0.48) * mm, "end": v(-1.67, 0.5) * mm});
            skLineSegment(sketch, "E497", {"start": v(-1.67, 0.5) * mm, "end": v(-1.66, 0.5) * mm});
            skLineSegment(sketch, "E498", {"start": v(-1.66, 0.5) * mm, "end": v(-1.66, 0.5) * mm});
            skLineSegment(sketch, "E499", {"start": v(-1.66, 0.5) * mm, "end": v(-1.65, 0.5) * mm});
            skLineSegment(sketch, "E500", {"start": v(-1.65, 0.5) * mm, "end": v(-1.63, 0.48) * mm});
            skLineSegment(sketch, "E501", {"start": v(-1.63, 0.48) * mm, "end": v(-1.6, 0.46) * mm});
            skLineSegment(sketch, "E502", {"start": v(-1.6, 0.46) * mm, "end": v(-1.57, 0.43) * mm});
            skLineSegment(sketch, "E503", {"start": v(-1.57, 0.43) * mm, "end": v(-1.56, 0.43) * mm});
            skLineSegment(sketch, "E504", {"start": v(-1.56, 0.43) * mm, "end": v(-1.46, 0.34) * mm});
            skLineSegment(sketch, "E505", {"start": v(-1.46, 0.34) * mm, "end": v(-1.25, 0.34) * mm});
            skLineSegment(sketch, "E506", {"start": v(-1.25, 0.34) * mm, "end": v(-1.23, 0.34) * mm});
            skLineSegment(sketch, "E507", {"start": v(-1.23, 0.34) * mm, "end": v(-1.18, 0.34) * mm});
            skLineSegment(sketch, "E508", {"start": v(-1.18, 0.34) * mm, "end": v(-1.13, 0.34) * mm});
            skLineSegment(sketch, "E509", {"start": v(-1.13, 0.34) * mm, "end": v(-1.1, 0.34) * mm});
            skLineSegment(sketch, "E510", {"start": v(-1.1, 0.34) * mm, "end": v(-1.07, 0.35) * mm});
            skLineSegment(sketch, "E511", {"start": v(-1.07, 0.35) * mm, "end": v(-1.05, 0.35) * mm});
            skLineSegment(sketch, "E512", {"start": v(-1.05, 0.35) * mm, "end": v(-1.04, 0.35) * mm});
            skLineSegment(sketch, "E513", {"start": v(-1.04, 0.35) * mm, "end": v(-1.04, 0.35) * mm});
            skLineSegment(sketch, "E514", {"start": v(-1.04, 0.35) * mm, "end": v(-1.03, 0.35) * mm});
            skLineSegment(sketch, "E515", {"start": v(-1.03, 0.35) * mm, "end": v(-1.03, 0.35) * mm});
            skLineSegment(sketch, "E516", {"start": v(-1.03, 0.35) * mm, "end": v(-1.03, 0.36) * mm});
            skLineSegment(sketch, "E517", {"start": v(-1.03, 0.36) * mm, "end": v(-1.02, 0.36) * mm});
            skLineSegment(sketch, "E518", {"start": v(-1.02, 0.36) * mm, "end": v(-1.02, 0.37) * mm});
            skLineSegment(sketch, "E519", {"start": v(-1.02, 0.37) * mm, "end": v(-1.03, 0.38) * mm});
            skLineSegment(sketch, "E520", {"start": v(-1.03, 0.38) * mm, "end": v(-1.03, 0.4) * mm});
            skLineSegment(sketch, "E521", {"start": v(-1.03, 0.4) * mm, "end": v(-1.04, 0.4) * mm});
            skLineSegment(sketch, "E522", {"start": v(-1.04, 0.4) * mm, "end": v(-1.05, 0.4) * mm});
            skLineSegment(sketch, "E523", {"start": v(-1.05, 0.4) * mm, "end": v(-1.43, 0.41) * mm});
            skLineSegment(sketch, "E524", {"start": v(-1.43, 0.41) * mm, "end": v(-1.55, 0.5) * mm});
            skLineSegment(sketch, "E525", {"start": v(-1.55, 0.5) * mm, "end": v(-1.56, 0.52) * mm});
            skLineSegment(sketch, "E526", {"start": v(-1.56, 0.52) * mm, "end": v(-1.6, 0.55) * mm});
            skLineSegment(sketch, "E527", {"start": v(-1.6, 0.55) * mm, "end": v(-1.63, 0.58) * mm});
            skLineSegment(sketch, "E528", {"start": v(-1.63, 0.58) * mm, "end": v(-1.65, 0.6) * mm});
            skLineSegment(sketch, "E529", {"start": v(-1.65, 0.6) * mm, "end": v(-1.66, 0.6) * mm});
            skLineSegment(sketch, "E530", {"start": v(-1.66, 0.6) * mm, "end": v(-1.66, 0.6) * mm});
            skLineSegment(sketch, "E531", {"start": v(-1.66, 0.6) * mm, "end": v(-1.67, 0.6) * mm});
            skLineSegment(sketch, "E532", {"start": v(-1.67, 0.6) * mm, "end": v(-1.67, 0.6) * mm});
            skLineSegment(sketch, "E533", {"start": v(-1.67, 0.6) * mm, "end": v(-1.7, 0.58) * mm});
            skLineSegment(sketch, "E534", {"start": v(-1.7, 0.58) * mm, "end": v(-1.74, 0.55) * mm});
            skLineSegment(sketch, "E535", {"start": v(-1.74, 0.55) * mm, "end": v(-1.77, 0.52) * mm});
            skLineSegment(sketch, "E536", {"start": v(-1.77, 0.52) * mm, "end": v(-1.78, 0.5) * mm});
            skSolve(sketch);
        }
        {
            var Q0;
            Q0=makeQuery(id+"F2.imprint","IMPRINT",FACE,{"disambiguationData":[TD([[makeQuery(id+"F2.imprint","IMPRINT",EDGE,{"derivedFrom":sQuery(id+"F2.wireOp",EDGE,"E1")}),-1.0]])]});
            var sketch = newSketch(context, id + "F4", { "sketchPlane" : qUnion([Q0])});
            skLineSegment(sketch, "E537", {"start": v(-0.03, 2.33) * mm, "end": v(-0.03, 2.33) * mm});
            skLineSegment(sketch, "E538", {"start": v(-0.03, 2.33) * mm, "end": v(-0.04, 2.32) * mm});
            skLineSegment(sketch, "E539", {"start": v(-0.04, 2.32) * mm, "end": v(-0.04, 2.31) * mm});
            skLineSegment(sketch, "E540", {"start": v(-0.04, 2.31) * mm, "end": v(-0.05, 2.3) * mm});
            skLineSegment(sketch, "E541", {"start": v(-0.05, 2.3) * mm, "end": v(-0.05, 2.3) * mm});
            skLineSegment(sketch, "E542", {"start": v(-0.05, 2.3) * mm, "end": v(-0.06, 2.3) * mm});
            skLineSegment(sketch, "E543", {"start": v(-0.06, 2.3) * mm, "end": v(-0.06, 2.3) * mm});
            skLineSegment(sketch, "E544", {"start": v(-0.06, 2.3) * mm, "end": v(-0.06, 2.29) * mm});
            skLineSegment(sketch, "E545", {"start": v(-0.06, 2.29) * mm, "end": v(-0.06, 2.27) * mm});
            skLineSegment(sketch, "E546", {"start": v(-0.06, 2.27) * mm, "end": v(-0.06, 2.24) * mm});
            skLineSegment(sketch, "E547", {"start": v(-0.06, 2.24) * mm, "end": v(-0.06, 2.22) * mm});
            skLineSegment(sketch, "E548", {"start": v(-0.06, 2.22) * mm, "end": v(-0.06, 2.2) * mm});
            skLineSegment(sketch, "E549", {"start": v(-0.06, 2.2) * mm, "end": v(-0.06, 2.2) * mm});
            skLineSegment(sketch, "E550", {"start": v(-0.06, 2.2) * mm, "end": v(-0.06, 2.18) * mm});
            skLineSegment(sketch, "E551", {"start": v(-0.06, 2.18) * mm, "end": v(-0.06, 2.16) * mm});
            skLineSegment(sketch, "E552", {"start": v(-0.06, 2.16) * mm, "end": v(-0.06, 2.15) * mm});
            skLineSegment(sketch, "E553", {"start": v(-0.06, 2.15) * mm, "end": v(-0.06, 2.13) * mm});
            skLineSegment(sketch, "E554", {"start": v(-0.06, 2.13) * mm, "end": v(-0.06, 2.13) * mm});
            skLineSegment(sketch, "E555", {"start": v(-0.06, 2.13) * mm, "end": v(-0.05, 2.12) * mm});
            skLineSegment(sketch, "E556", {"start": v(-0.05, 2.12) * mm, "end": v(-0.05, 2.12) * mm});
            skLineSegment(sketch, "E557", {"start": v(-0.05, 2.12) * mm, "end": v(-0.05, 2.11) * mm});
            skLineSegment(sketch, "E558", {"start": v(-0.05, 2.11) * mm, "end": v(-0.05, 2.11) * mm});
            skLineSegment(sketch, "E559", {"start": v(-0.05, 2.11) * mm, "end": v(-0.04, 2.1) * mm});
            skLineSegment(sketch, "E560", {"start": v(-0.04, 2.1) * mm, "end": v(-0.02, 2.1) * mm});
            skLineSegment(sketch, "E561", {"start": v(-0.02, 2.1) * mm, "end": v(0, 2.1) * mm});
            skLineSegment(sketch, "E562", {"start": v(0, 2.1) * mm, "end": v(0.02, 2.1) * mm});
            skLineSegment(sketch, "E563", {"start": v(0.02, 2.1) * mm, "end": v(0.02, 2.1) * mm});
            skLineSegment(sketch, "E564", {"start": v(0.02, 2.1) * mm, "end": v(0.03, 2.1) * mm});
            skLineSegment(sketch, "E565", {"start": v(0.03, 2.1) * mm, "end": v(0.03, 2.1) * mm});
            skLineSegment(sketch, "E566", {"start": v(0.03, 2.1) * mm, "end": v(0.03, 2.11) * mm});
            skLineSegment(sketch, "E567", {"start": v(0.03, 2.11) * mm, "end": v(0.03, 2.11) * mm});
            skLineSegment(sketch, "E568", {"start": v(0.03, 2.11) * mm, "end": v(0.03, 2.12) * mm});
            skLineSegment(sketch, "E569", {"start": v(0.03, 2.12) * mm, "end": v(0.04, 2.12) * mm});
            skLineSegment(sketch, "E570", {"start": v(0.04, 2.12) * mm, "end": v(0.04, 2.12) * mm});
            skLineSegment(sketch, "E571", {"start": v(0.04, 2.12) * mm, "end": v(0.04, 2.13) * mm});
            skLineSegment(sketch, "E572", {"start": v(0.04, 2.13) * mm, "end": v(0.04, 2.13) * mm});
            skLineSegment(sketch, "E573", {"start": v(0.04, 2.13) * mm, "end": v(0.04, 2.14) * mm});
            skLineSegment(sketch, "E574", {"start": v(0.04, 2.14) * mm, "end": v(0.04, 2.16) * mm});
            skLineSegment(sketch, "E575", {"start": v(0.04, 2.16) * mm, "end": v(0.04, 2.17) * mm});
            skLineSegment(sketch, "E576", {"start": v(0.04, 2.17) * mm, "end": v(0.04, 2.2) * mm});
            skLineSegment(sketch, "E577", {"start": v(0.04, 2.2) * mm, "end": v(0.04, 2.2) * mm});
            skLineSegment(sketch, "E578", {"start": v(0.04, 2.2) * mm, "end": v(0.04, 2.23) * mm});
            skLineSegment(sketch, "E579", {"start": v(0.04, 2.23) * mm, "end": v(0.04, 2.25) * mm});
            skLineSegment(sketch, "E580", {"start": v(0.04, 2.25) * mm, "end": v(0.04, 2.27) * mm});
            skLineSegment(sketch, "E581", {"start": v(0.04, 2.27) * mm, "end": v(0.04, 2.28) * mm});
            skLineSegment(sketch, "E582", {"start": v(0.04, 2.28) * mm, "end": v(0.04, 2.3) * mm});
            skLineSegment(sketch, "E583", {"start": v(0.04, 2.3) * mm, "end": v(0.04, 2.3) * mm});
            skLineSegment(sketch, "E584", {"start": v(0.04, 2.3) * mm, "end": v(0.03, 2.3) * mm});
            skLineSegment(sketch, "E585", {"start": v(0.03, 2.3) * mm, "end": v(0.03, 2.3) * mm});
            skLineSegment(sketch, "E586", {"start": v(0.03, 2.3) * mm, "end": v(0.03, 2.31) * mm});
            skLineSegment(sketch, "E587", {"start": v(0.03, 2.31) * mm, "end": v(0.03, 2.31) * mm});
            skLineSegment(sketch, "E588", {"start": v(0.03, 2.31) * mm, "end": v(0.02, 2.32) * mm});
            skLineSegment(sketch, "E589", {"start": v(0.02, 2.32) * mm, "end": v(0.01, 2.33) * mm});
            skLineSegment(sketch, "E590", {"start": v(0.01, 2.33) * mm, "end": v(0, 2.33) * mm});
            skLineSegment(sketch, "E591", {"start": v(0, 2.33) * mm, "end": v(0, 2.33) * mm});
            skLineSegment(sketch, "E592", {"start": v(0, 2.33) * mm, "end": v(-0.01, 2.33) * mm});
            skLineSegment(sketch, "E593", {"start": v(-0.01, 2.33) * mm, "end": v(-0.02, 2.33) * mm});
            skLineSegment(sketch, "E594", {"start": v(-0.02, 2.33) * mm, "end": v(-0.03, 2.33) * mm});
            skLineSegment(sketch, "E595", {"start": v(-0.32, 2.25) * mm, "end": v(-0.33, 2.25) * mm});
            skLineSegment(sketch, "E596", {"start": v(-0.33, 2.25) * mm, "end": v(-0.34, 2.24) * mm});
            skLineSegment(sketch, "E597", {"start": v(-0.34, 2.24) * mm, "end": v(-0.35, 2.22) * mm});
            skLineSegment(sketch, "E598", {"start": v(-0.35, 2.22) * mm, "end": v(-0.35, 2.2) * mm});
            skLineSegment(sketch, "E599", {"start": v(-0.35, 2.2) * mm, "end": v(-0.35, 2.19) * mm});
            skLineSegment(sketch, "E600", {"start": v(-0.35, 2.19) * mm, "end": v(-0.34, 2.18) * mm});
            skLineSegment(sketch, "E601", {"start": v(-0.34, 2.18) * mm, "end": v(-0.34, 2.18) * mm});
            skLineSegment(sketch, "E602", {"start": v(-0.34, 2.18) * mm, "end": v(-0.34, 2.17) * mm});
            skLineSegment(sketch, "E603", {"start": v(-0.34, 2.17) * mm, "end": v(-0.33, 2.15) * mm});
            skLineSegment(sketch, "E604", {"start": v(-0.33, 2.15) * mm, "end": v(-0.31, 2.13) * mm});
            skLineSegment(sketch, "E605", {"start": v(-0.31, 2.13) * mm, "end": v(-0.3, 2.1) * mm});
            skLineSegment(sketch, "E606", {"start": v(-0.3, 2.1) * mm, "end": v(-0.29, 2.08) * mm});
            skLineSegment(sketch, "E607", {"start": v(-0.29, 2.08) * mm, "end": v(-0.27, 2.06) * mm});
            skLineSegment(sketch, "E608", {"start": v(-0.27, 2.06) * mm, "end": v(-0.27, 2.05) * mm});
            skLineSegment(sketch, "E609", {"start": v(-0.27, 2.05) * mm, "end": v(-0.26, 2.04) * mm});
            skLineSegment(sketch, "E610", {"start": v(-0.26, 2.04) * mm, "end": v(-0.26, 2.04) * mm});
            skLineSegment(sketch, "E611", {"start": v(-0.26, 2.04) * mm, "end": v(-0.25, 2.03) * mm});
            skLineSegment(sketch, "E612", {"start": v(-0.25, 2.03) * mm, "end": v(-0.23, 2.03) * mm});
            skLineSegment(sketch, "E613", {"start": v(-0.23, 2.03) * mm, "end": v(-0.22, 2.03) * mm});
            skLineSegment(sketch, "E614", {"start": v(-0.22, 2.03) * mm, "end": v(-0.2, 2.04) * mm});
            skLineSegment(sketch, "E615", {"start": v(-0.2, 2.04) * mm, "end": v(-0.2, 2.04) * mm});
            skLineSegment(sketch, "E616", {"start": v(-0.2, 2.04) * mm, "end": v(-0.19, 2.06) * mm});
            skLineSegment(sketch, "E617", {"start": v(-0.19, 2.06) * mm, "end": v(-0.18, 2.07) * mm});
            skLineSegment(sketch, "E618", {"start": v(-0.18, 2.07) * mm, "end": v(-0.18, 2.08) * mm});
            skLineSegment(sketch, "E619", {"start": v(-0.18, 2.08) * mm, "end": v(-0.18, 2.08) * mm});
            skLineSegment(sketch, "E620", {"start": v(-0.18, 2.08) * mm, "end": v(-0.18, 2.09) * mm});
            skLineSegment(sketch, "E621", {"start": v(-0.18, 2.09) * mm, "end": v(-0.18, 2.1) * mm});
            skLineSegment(sketch, "E622", {"start": v(-0.18, 2.1) * mm, "end": v(-0.19, 2.1) * mm});
            skLineSegment(sketch, "E623", {"start": v(-0.19, 2.1) * mm, "end": v(-0.19, 2.1) * mm});
            skLineSegment(sketch, "E624", {"start": v(-0.19, 2.1) * mm, "end": v(-0.2, 2.12) * mm});
            skLineSegment(sketch, "E625", {"start": v(-0.2, 2.12) * mm, "end": v(-0.2, 2.13) * mm});
            skLineSegment(sketch, "E626", {"start": v(-0.2, 2.13) * mm, "end": v(-0.21, 2.15) * mm});
            skLineSegment(sketch, "E627", {"start": v(-0.21, 2.15) * mm, "end": v(-0.21, 2.15) * mm});
            skLineSegment(sketch, "E628", {"start": v(-0.21, 2.15) * mm, "end": v(-0.22, 2.16) * mm});
            skLineSegment(sketch, "E629", {"start": v(-0.22, 2.16) * mm, "end": v(-0.23, 2.18) * mm});
            skLineSegment(sketch, "E630", {"start": v(-0.23, 2.18) * mm, "end": v(-0.24, 2.2) * mm});
            skLineSegment(sketch, "E631", {"start": v(-0.24, 2.2) * mm, "end": v(-0.25, 2.22) * mm});
            skLineSegment(sketch, "E632", {"start": v(-0.25, 2.22) * mm, "end": v(-0.26, 2.23) * mm});
            skLineSegment(sketch, "E633", {"start": v(-0.26, 2.23) * mm, "end": v(-0.27, 2.24) * mm});
            skLineSegment(sketch, "E634", {"start": v(-0.27, 2.24) * mm, "end": v(-0.27, 2.24) * mm});
            skLineSegment(sketch, "E635", {"start": v(-0.27, 2.24) * mm, "end": v(-0.28, 2.24) * mm});
            skLineSegment(sketch, "E636", {"start": v(-0.28, 2.24) * mm, "end": v(-0.28, 2.25) * mm});
            skLineSegment(sketch, "E637", {"start": v(-0.28, 2.25) * mm, "end": v(-0.28, 2.25) * mm});
            skLineSegment(sketch, "E638", {"start": v(-0.28, 2.25) * mm, "end": v(-0.3, 2.25) * mm});
            skLineSegment(sketch, "E639", {"start": v(-0.3, 2.25) * mm, "end": v(-0.32, 2.25) * mm});
            skLineSegment(sketch, "E640", {"start": v(-0.32, 2.25) * mm, "end": v(-0.32, 2.25) * mm});
            skLineSegment(sketch, "E641", {"start": v(0.27, 2.25) * mm, "end": v(0.27, 2.25) * mm});
            skLineSegment(sketch, "E642", {"start": v(0.27, 2.25) * mm, "end": v(0.26, 2.25) * mm});
            skLineSegment(sketch, "E643", {"start": v(0.26, 2.25) * mm, "end": v(0.26, 2.25) * mm});
            skLineSegment(sketch, "E644", {"start": v(0.26, 2.25) * mm, "end": v(0.25, 2.24) * mm});
            skLineSegment(sketch, "E645", {"start": v(0.25, 2.24) * mm, "end": v(0.25, 2.24) * mm});
            skLineSegment(sketch, "E646", {"start": v(0.25, 2.24) * mm, "end": v(0.25, 2.23) * mm});
            skLineSegment(sketch, "E647", {"start": v(0.25, 2.23) * mm, "end": v(0.24, 2.22) * mm});
            skLineSegment(sketch, "E648", {"start": v(0.24, 2.22) * mm, "end": v(0.22, 2.2) * mm});
            skLineSegment(sketch, "E649", {"start": v(0.22, 2.2) * mm, "end": v(0.2, 2.17) * mm});
            skLineSegment(sketch, "E650", {"start": v(0.2, 2.17) * mm, "end": v(0.2, 2.15) * mm});
            skLineSegment(sketch, "E651", {"start": v(0.2, 2.15) * mm, "end": v(0.18, 2.12) * mm});
            skLineSegment(sketch, "E652", {"start": v(0.18, 2.12) * mm, "end": v(0.17, 2.1) * mm});
            skLineSegment(sketch, "E653", {"start": v(0.17, 2.1) * mm, "end": v(0.17, 2.1) * mm});
            skLineSegment(sketch, "E654", {"start": v(0.17, 2.1) * mm, "end": v(0.16, 2.1) * mm});
            skLineSegment(sketch, "E655", {"start": v(0.16, 2.1) * mm, "end": v(0.16, 2.09) * mm});
            skLineSegment(sketch, "E656", {"start": v(0.16, 2.09) * mm, "end": v(0.16, 2.08) * mm});
            skLineSegment(sketch, "E657", {"start": v(0.16, 2.08) * mm, "end": v(0.16, 2.07) * mm});
            skLineSegment(sketch, "E658", {"start": v(0.16, 2.07) * mm, "end": v(0.17, 2.06) * mm});
            skLineSegment(sketch, "E659", {"start": v(0.17, 2.06) * mm, "end": v(0.17, 2.06) * mm});
            skLineSegment(sketch, "E660", {"start": v(0.17, 2.06) * mm, "end": v(0.17, 2.05) * mm});
            skLineSegment(sketch, "E661", {"start": v(0.17, 2.05) * mm, "end": v(0.18, 2.04) * mm});
            skLineSegment(sketch, "E662", {"start": v(0.18, 2.04) * mm, "end": v(0.2, 2.03) * mm});
            skLineSegment(sketch, "E663", {"start": v(0.2, 2.03) * mm, "end": v(0.2, 2.03) * mm});
            skLineSegment(sketch, "E664", {"start": v(0.2, 2.03) * mm, "end": v(0.21, 2.03) * mm});
            skLineSegment(sketch, "E665", {"start": v(0.21, 2.03) * mm, "end": v(0.22, 2.03) * mm});
            skLineSegment(sketch, "E666", {"start": v(0.22, 2.03) * mm, "end": v(0.23, 2.04) * mm});
            skLineSegment(sketch, "E667", {"start": v(0.23, 2.04) * mm, "end": v(0.24, 2.04) * mm});
            skLineSegment(sketch, "E668", {"start": v(0.24, 2.04) * mm, "end": v(0.24, 2.04) * mm});
            skLineSegment(sketch, "E669", {"start": v(0.24, 2.04) * mm, "end": v(0.25, 2.05) * mm});
            skLineSegment(sketch, "E670", {"start": v(0.25, 2.05) * mm, "end": v(0.26, 2.06) * mm});
            skLineSegment(sketch, "E671", {"start": v(0.26, 2.06) * mm, "end": v(0.27, 2.09) * mm});
            skLineSegment(sketch, "E672", {"start": v(0.27, 2.09) * mm, "end": v(0.28, 2.1) * mm});
            skLineSegment(sketch, "E673", {"start": v(0.28, 2.1) * mm, "end": v(0.29, 2.11) * mm});
            skLineSegment(sketch, "E674", {"start": v(0.29, 2.11) * mm, "end": v(0.3, 2.12) * mm});
            skLineSegment(sketch, "E675", {"start": v(0.3, 2.12) * mm, "end": v(0.3, 2.14) * mm});
            skLineSegment(sketch, "E676", {"start": v(0.3, 2.14) * mm, "end": v(0.32, 2.16) * mm});
            skLineSegment(sketch, "E677", {"start": v(0.32, 2.16) * mm, "end": v(0.32, 2.18) * mm});
            skLineSegment(sketch, "E678", {"start": v(0.32, 2.18) * mm, "end": v(0.33, 2.2) * mm});
            skLineSegment(sketch, "E679", {"start": v(0.33, 2.2) * mm, "end": v(0.33, 2.2) * mm});
            skLineSegment(sketch, "E680", {"start": v(0.33, 2.2) * mm, "end": v(0.33, 2.21) * mm});
            skLineSegment(sketch, "E681", {"start": v(0.33, 2.21) * mm, "end": v(0.33, 2.22) * mm});
            skLineSegment(sketch, "E682", {"start": v(0.33, 2.22) * mm, "end": v(0.33, 2.22) * mm});
            skLineSegment(sketch, "E683", {"start": v(0.33, 2.22) * mm, "end": v(0.32, 2.24) * mm});
            skLineSegment(sketch, "E684", {"start": v(0.32, 2.24) * mm, "end": v(0.3, 2.25) * mm});
            skLineSegment(sketch, "E685", {"start": v(0.3, 2.25) * mm, "end": v(0.29, 2.25) * mm});
            skLineSegment(sketch, "E686", {"start": v(0.29, 2.25) * mm, "end": v(0.27, 2.25) * mm});
            skLineSegment(sketch, "E687", {"start": v(-0.53, 2.04) * mm, "end": v(-0.54, 2.03) * mm});
            skLineSegment(sketch, "E688", {"start": v(-0.54, 2.03) * mm, "end": v(-0.55, 2.02) * mm});
            skLineSegment(sketch, "E689", {"start": v(-0.55, 2.02) * mm, "end": v(-0.56, 2) * mm});
            skLineSegment(sketch, "E690", {"start": v(-0.56, 2) * mm, "end": v(-0.56, 1.99) * mm});
            skLineSegment(sketch, "E691", {"start": v(-0.56, 1.99) * mm, "end": v(-0.56, 1.97) * mm});
            skLineSegment(sketch, "E692", {"start": v(-0.56, 1.97) * mm, "end": v(-0.56, 1.96) * mm});
            skLineSegment(sketch, "E693", {"start": v(-0.56, 1.96) * mm, "end": v(-0.56, 1.96) * mm});
            skLineSegment(sketch, "E694", {"start": v(-0.56, 1.96) * mm, "end": v(-0.55, 1.96) * mm});
            skLineSegment(sketch, "E695", {"start": v(-0.55, 1.96) * mm, "end": v(-0.55, 1.96) * mm});
            skLineSegment(sketch, "E696", {"start": v(-0.55, 1.96) * mm, "end": v(-0.55, 1.95) * mm});
            skLineSegment(sketch, "E697", {"start": v(-0.55, 1.95) * mm, "end": v(-0.54, 1.95) * mm});
            skLineSegment(sketch, "E698", {"start": v(-0.54, 1.95) * mm, "end": v(-0.53, 1.94) * mm});
            skLineSegment(sketch, "E699", {"start": v(-0.53, 1.94) * mm, "end": v(-0.51, 1.93) * mm});
            skLineSegment(sketch, "E700", {"start": v(-0.51, 1.93) * mm, "end": v(-0.5, 1.92) * mm});
            skLineSegment(sketch, "E701", {"start": v(-0.5, 1.92) * mm, "end": v(-0.47, 1.9) * mm});
            skLineSegment(sketch, "E702", {"start": v(-0.47, 1.9) * mm, "end": v(-0.47, 1.9) * mm});
            skLineSegment(sketch, "E703", {"start": v(-0.47, 1.9) * mm, "end": v(-0.46, 1.9) * mm});
            skLineSegment(sketch, "E704", {"start": v(-0.46, 1.9) * mm, "end": v(-0.45, 1.9) * mm});
            skLineSegment(sketch, "E705", {"start": v(-0.45, 1.9) * mm, "end": v(-0.43, 1.89) * mm});
            skLineSegment(sketch, "E706", {"start": v(-0.43, 1.89) * mm, "end": v(-0.42, 1.88) * mm});
            skLineSegment(sketch, "E707", {"start": v(-0.42, 1.88) * mm, "end": v(-0.41, 1.87) * mm});
            skLineSegment(sketch, "E708", {"start": v(-0.41, 1.87) * mm, "end": v(-0.4, 1.87) * mm});
            skLineSegment(sketch, "E709", {"start": v(-0.4, 1.87) * mm, "end": v(-0.4, 1.87) * mm});
            skLineSegment(sketch, "E710", {"start": v(-0.4, 1.87) * mm, "end": v(-0.39, 1.87) * mm});
            skLineSegment(sketch, "E711", {"start": v(-0.39, 1.87) * mm, "end": v(-0.39, 1.87) * mm});
            skLineSegment(sketch, "E712", {"start": v(-0.39, 1.87) * mm, "end": v(-0.38, 1.87) * mm});
            skLineSegment(sketch, "E713", {"start": v(-0.38, 1.87) * mm, "end": v(-0.37, 1.87) * mm});
            skLineSegment(sketch, "E714", {"start": v(-0.37, 1.87) * mm, "end": v(-0.36, 1.88) * mm});
            skLineSegment(sketch, "E715", {"start": v(-0.36, 1.88) * mm, "end": v(-0.36, 1.88) * mm});
            skLineSegment(sketch, "E716", {"start": v(-0.36, 1.88) * mm, "end": v(-0.35, 1.88) * mm});
            skLineSegment(sketch, "E717", {"start": v(-0.35, 1.88) * mm, "end": v(-0.35, 1.89) * mm});
            skLineSegment(sketch, "E718", {"start": v(-0.35, 1.89) * mm, "end": v(-0.34, 1.9) * mm});
            skLineSegment(sketch, "E719", {"start": v(-0.34, 1.9) * mm, "end": v(-0.34, 1.92) * mm});
            skLineSegment(sketch, "E720", {"start": v(-0.34, 1.92) * mm, "end": v(-0.35, 1.94) * mm});
            skLineSegment(sketch, "E721", {"start": v(-0.35, 1.94) * mm, "end": v(-0.35, 1.95) * mm});
            skLineSegment(sketch, "E722", {"start": v(-0.35, 1.95) * mm, "end": v(-0.36, 1.95) * mm});
            skLineSegment(sketch, "E723", {"start": v(-0.36, 1.95) * mm, "end": v(-0.36, 1.95) * mm});
            skLineSegment(sketch, "E724", {"start": v(-0.36, 1.95) * mm, "end": v(-0.36, 1.96) * mm});
            skLineSegment(sketch, "E725", {"start": v(-0.36, 1.96) * mm, "end": v(-0.38, 1.97) * mm});
            skLineSegment(sketch, "E726", {"start": v(-0.38, 1.97) * mm, "end": v(-0.4, 1.98) * mm});
            skLineSegment(sketch, "E727", {"start": v(-0.4, 1.98) * mm, "end": v(-0.42, 2) * mm});
            skLineSegment(sketch, "E728", {"start": v(-0.42, 2) * mm, "end": v(-0.45, 2) * mm});
            skLineSegment(sketch, "E729", {"start": v(-0.45, 2) * mm, "end": v(-0.47, 2.02) * mm});
            skLineSegment(sketch, "E730", {"start": v(-0.47, 2.02) * mm, "end": v(-0.48, 2.03) * mm});
            skLineSegment(sketch, "E731", {"start": v(-0.48, 2.03) * mm, "end": v(-0.5, 2.03) * mm});
            skLineSegment(sketch, "E732", {"start": v(-0.5, 2.03) * mm, "end": v(-0.5, 2.03) * mm});
            skLineSegment(sketch, "E733", {"start": v(-0.5, 2.03) * mm, "end": v(-0.5, 2.04) * mm});
            skLineSegment(sketch, "E734", {"start": v(-0.5, 2.04) * mm, "end": v(-0.51, 2.04) * mm});
            skLineSegment(sketch, "E735", {"start": v(-0.51, 2.04) * mm, "end": v(-0.52, 2.04) * mm});
            skLineSegment(sketch, "E736", {"start": v(-0.52, 2.04) * mm, "end": v(-0.53, 2.04) * mm});
            skLineSegment(sketch, "E737", {"start": v(-0.53, 2.04) * mm, "end": v(-0.53, 2.04) * mm});
            skLineSegment(sketch, "E738", {"start": v(-0.04, 2.04) * mm, "end": v(-0.06, 2.04) * mm});
            skLineSegment(sketch, "E739", {"start": v(-0.06, 2.04) * mm, "end": v(-0.1, 2.03) * mm});
            skLineSegment(sketch, "E740", {"start": v(-0.1, 2.03) * mm, "end": v(-0.16, 2) * mm});
            skLineSegment(sketch, "E741", {"start": v(-0.16, 2) * mm, "end": v(-0.2, 1.98) * mm});
            skLineSegment(sketch, "E742", {"start": v(-0.2, 1.98) * mm, "end": v(-0.24, 1.95) * mm});
            skLineSegment(sketch, "E743", {"start": v(-0.24, 1.95) * mm, "end": v(-0.25, 1.94) * mm});
            skLineSegment(sketch, "E744", {"start": v(-0.25, 1.94) * mm, "end": v(-0.26, 1.93) * mm});
            skLineSegment(sketch, "E745", {"start": v(-0.26, 1.93) * mm, "end": v(-0.3, 1.89) * mm});
            skLineSegment(sketch, "E746", {"start": v(-0.3, 1.89) * mm, "end": v(-0.32, 1.83) * mm});
            skLineSegment(sketch, "E747", {"start": v(-0.32, 1.83) * mm, "end": v(-0.34, 1.77) * mm});
            skLineSegment(sketch, "E748", {"start": v(-0.34, 1.77) * mm, "end": v(-0.35, 1.71) * mm});
            skLineSegment(sketch, "E749", {"start": v(-0.35, 1.71) * mm, "end": v(-0.35, 1.7) * mm});
            skLineSegment(sketch, "E750", {"start": v(-0.35, 1.7) * mm, "end": v(-0.35, 1.68) * mm});
            skLineSegment(sketch, "E751", {"start": v(-0.35, 1.68) * mm, "end": v(-0.34, 1.63) * mm});
            skLineSegment(sketch, "E752", {"start": v(-0.34, 1.63) * mm, "end": v(-0.32, 1.57) * mm});
            skLineSegment(sketch, "E753", {"start": v(-0.32, 1.57) * mm, "end": v(-0.3, 1.5) * mm});
            skLineSegment(sketch, "E754", {"start": v(-0.3, 1.5) * mm, "end": v(-0.26, 1.47) * mm});
            skLineSegment(sketch, "E755", {"start": v(-0.26, 1.47) * mm, "end": v(-0.25, 1.46) * mm});
            skLineSegment(sketch, "E756", {"start": v(-0.25, 1.46) * mm, "end": v(-0.24, 1.44) * mm});
            skLineSegment(sketch, "E757", {"start": v(-0.24, 1.44) * mm, "end": v(-0.2, 1.41) * mm});
            skLineSegment(sketch, "E758", {"start": v(-0.2, 1.41) * mm, "end": v(-0.14, 1.38) * mm});
            skLineSegment(sketch, "E759", {"start": v(-0.14, 1.38) * mm, "end": v(-0.08, 1.36) * mm});
            skLineSegment(sketch, "E760", {"start": v(-0.08, 1.36) * mm, "end": v(-0.03, 1.36) * mm});
            skLineSegment(sketch, "E761", {"start": v(-0.03, 1.36) * mm, "end": v(0, 1.36) * mm});
            skLineSegment(sketch, "E762", {"start": v(0, 1.36) * mm, "end": v(0, 1.36) * mm});
            skLineSegment(sketch, "E763", {"start": v(0, 1.36) * mm, "end": v(0.06, 1.36) * mm});
            skLineSegment(sketch, "E764", {"start": v(0.06, 1.36) * mm, "end": v(0.12, 1.38) * mm});
            skLineSegment(sketch, "E765", {"start": v(0.12, 1.38) * mm, "end": v(0.18, 1.41) * mm});
            skLineSegment(sketch, "E766", {"start": v(0.18, 1.41) * mm, "end": v(0.22, 1.44) * mm});
            skLineSegment(sketch, "E767", {"start": v(0.22, 1.44) * mm, "end": v(0.23, 1.46) * mm});
            skLineSegment(sketch, "E768", {"start": v(0.23, 1.46) * mm, "end": v(0.24, 1.47) * mm});
            skLineSegment(sketch, "E769", {"start": v(0.24, 1.47) * mm, "end": v(0.28, 1.5) * mm});
            skLineSegment(sketch, "E770", {"start": v(0.28, 1.5) * mm, "end": v(0.3, 1.57) * mm});
            skLineSegment(sketch, "E771", {"start": v(0.3, 1.57) * mm, "end": v(0.33, 1.63) * mm});
            skLineSegment(sketch, "E772", {"start": v(0.33, 1.63) * mm, "end": v(0.33, 1.68) * mm});
            skLineSegment(sketch, "E773", {"start": v(0.33, 1.68) * mm, "end": v(0.33, 1.7) * mm});
            skLineSegment(sketch, "E774", {"start": v(0.33, 1.7) * mm, "end": v(0.33, 1.71) * mm});
            skLineSegment(sketch, "E775", {"start": v(0.33, 1.71) * mm, "end": v(0.33, 1.77) * mm});
            skLineSegment(sketch, "E776", {"start": v(0.33, 1.77) * mm, "end": v(0.3, 1.83) * mm});
            skLineSegment(sketch, "E777", {"start": v(0.3, 1.83) * mm, "end": v(0.28, 1.89) * mm});
            skLineSegment(sketch, "E778", {"start": v(0.28, 1.89) * mm, "end": v(0.24, 1.93) * mm});
            skLineSegment(sketch, "E779", {"start": v(0.24, 1.93) * mm, "end": v(0.23, 1.94) * mm});
            skLineSegment(sketch, "E780", {"start": v(0.23, 1.94) * mm, "end": v(0.22, 1.95) * mm});
            skLineSegment(sketch, "E781", {"start": v(0.22, 1.95) * mm, "end": v(0.2, 1.97) * mm});
            skLineSegment(sketch, "E782", {"start": v(0.2, 1.97) * mm, "end": v(0.17, 1.99) * mm});
            skLineSegment(sketch, "E783", {"start": v(0.17, 1.99) * mm, "end": v(0.14, 2) * mm});
            skLineSegment(sketch, "E784", {"start": v(0.14, 2) * mm, "end": v(0.1, 2.02) * mm});
            skLineSegment(sketch, "E785", {"start": v(0.1, 2.02) * mm, "end": v(0.1, 2.02) * mm});
            skLineSegment(sketch, "E786", {"start": v(0.1, 2.02) * mm, "end": v(0.06, 2.03) * mm});
            skLineSegment(sketch, "E787", {"start": v(0.06, 2.03) * mm, "end": v(0.03, 2.04) * mm});
            skLineSegment(sketch, "E788", {"start": v(0.03, 2.04) * mm, "end": v(0, 2.04) * mm});
            skLineSegment(sketch, "E789", {"start": v(0, 2.04) * mm, "end": v(-0.04, 2.04) * mm});
            skLineSegment(sketch, "E790", {"start": v(-0.04, 2.04) * mm, "end": v(-0.04, 2.04) * mm});
            skLineSegment(sketch, "E791", {"start": v(0.05, 1.93) * mm, "end": v(0.06, 1.93) * mm});
            skLineSegment(sketch, "E792", {"start": v(0.06, 1.93) * mm, "end": v(0.09, 1.92) * mm});
            skLineSegment(sketch, "E793", {"start": v(0.09, 1.92) * mm, "end": v(0.12, 1.9) * mm});
            skLineSegment(sketch, "E794", {"start": v(0.12, 1.9) * mm, "end": v(0.15, 1.88) * mm});
            skLineSegment(sketch, "E795", {"start": v(0.15, 1.88) * mm, "end": v(0.17, 1.86) * mm});
            skLineSegment(sketch, "E796", {"start": v(0.17, 1.86) * mm, "end": v(0.18, 1.86) * mm});
            skLineSegment(sketch, "E797", {"start": v(0.18, 1.86) * mm, "end": v(0.18, 1.85) * mm});
            skLineSegment(sketch, "E798", {"start": v(0.18, 1.85) * mm, "end": v(0.2, 1.83) * mm});
            skLineSegment(sketch, "E799", {"start": v(0.2, 1.83) * mm, "end": v(0.2, 1.81) * mm});
            skLineSegment(sketch, "E800", {"start": v(0.2, 1.81) * mm, "end": v(0.22, 1.79) * mm});
            skLineSegment(sketch, "E801", {"start": v(0.22, 1.79) * mm, "end": v(0.23, 1.76) * mm});
            skLineSegment(sketch, "E802", {"start": v(0.23, 1.76) * mm, "end": v(0.23, 1.76) * mm});
            skLineSegment(sketch, "E803", {"start": v(0.23, 1.76) * mm, "end": v(0.23, 1.75) * mm});
            skLineSegment(sketch, "E804", {"start": v(0.23, 1.75) * mm, "end": v(0.23, 1.75) * mm});
            skLineSegment(sketch, "E805", {"start": v(0.23, 1.75) * mm, "end": v(0.23, 1.74) * mm});
            skLineSegment(sketch, "E806", {"start": v(0.23, 1.74) * mm, "end": v(0.23, 1.72) * mm});
            skLineSegment(sketch, "E807", {"start": v(0.23, 1.72) * mm, "end": v(0.23, 1.7) * mm});
            skLineSegment(sketch, "E808", {"start": v(0.23, 1.7) * mm, "end": v(0.23, 1.7) * mm});
            skLineSegment(sketch, "E809", {"start": v(0.23, 1.7) * mm, "end": v(0.23, 1.67) * mm});
            skLineSegment(sketch, "E810", {"start": v(0.23, 1.67) * mm, "end": v(0.23, 1.65) * mm});
            skLineSegment(sketch, "E811", {"start": v(0.23, 1.65) * mm, "end": v(0.23, 1.63) * mm});
            skLineSegment(sketch, "E812", {"start": v(0.23, 1.63) * mm, "end": v(0.22, 1.61) * mm});
            skLineSegment(sketch, "E813", {"start": v(0.22, 1.61) * mm, "end": v(0.22, 1.6) * mm});
            skLineSegment(sketch, "E814", {"start": v(0.22, 1.6) * mm, "end": v(0.22, 1.6) * mm});
            skLineSegment(sketch, "E815", {"start": v(0.22, 1.6) * mm, "end": v(0.2, 1.59) * mm});
            skLineSegment(sketch, "E816", {"start": v(0.2, 1.59) * mm, "end": v(0.2, 1.56) * mm});
            skLineSegment(sketch, "E817", {"start": v(0.2, 1.56) * mm, "end": v(0.18, 1.54) * mm});
            skLineSegment(sketch, "E818", {"start": v(0.18, 1.54) * mm, "end": v(0.16, 1.53) * mm});
            skLineSegment(sketch, "E819", {"start": v(0.16, 1.53) * mm, "end": v(0.14, 1.5) * mm});
            skLineSegment(sketch, "E820", {"start": v(0.14, 1.5) * mm, "end": v(0.12, 1.5) * mm});
            skLineSegment(sketch, "E821", {"start": v(0.12, 1.5) * mm, "end": v(0.1, 1.48) * mm});
            skLineSegment(sketch, "E822", {"start": v(0.1, 1.48) * mm, "end": v(0.09, 1.47) * mm});
            skLineSegment(sketch, "E823", {"start": v(0.09, 1.47) * mm, "end": v(0.08, 1.47) * mm});
            skLineSegment(sketch, "E824", {"start": v(0.08, 1.47) * mm, "end": v(0.07, 1.47) * mm});
            skLineSegment(sketch, "E825", {"start": v(0.07, 1.47) * mm, "end": v(0.06, 1.46) * mm});
            skLineSegment(sketch, "E826", {"start": v(0.06, 1.46) * mm, "end": v(0.04, 1.46) * mm});
            skLineSegment(sketch, "E827", {"start": v(0.04, 1.46) * mm, "end": v(0.02, 1.46) * mm});
            skLineSegment(sketch, "E828", {"start": v(0.02, 1.46) * mm, "end": v(0, 1.46) * mm});
            skLineSegment(sketch, "E829", {"start": v(0, 1.46) * mm, "end": v(0, 1.46) * mm});
            skLineSegment(sketch, "E830", {"start": v(0, 1.46) * mm, "end": v(-0.02, 1.46) * mm});
            skLineSegment(sketch, "E831", {"start": v(-0.02, 1.46) * mm, "end": v(-0.04, 1.46) * mm});
            skLineSegment(sketch, "E832", {"start": v(-0.04, 1.46) * mm, "end": v(-0.06, 1.46) * mm});
            skLineSegment(sketch, "E833", {"start": v(-0.06, 1.46) * mm, "end": v(-0.07, 1.46) * mm});
            skLineSegment(sketch, "E834", {"start": v(-0.07, 1.46) * mm, "end": v(-0.1, 1.47) * mm});
            skLineSegment(sketch, "E835", {"start": v(-0.1, 1.47) * mm, "end": v(-0.1, 1.47) * mm});
            skLineSegment(sketch, "E836", {"start": v(-0.1, 1.47) * mm, "end": v(-0.12, 1.48) * mm});
            skLineSegment(sketch, "E837", {"start": v(-0.12, 1.48) * mm, "end": v(-0.14, 1.5) * mm});
            skLineSegment(sketch, "E838", {"start": v(-0.14, 1.5) * mm, "end": v(-0.16, 1.5) * mm});
            skLineSegment(sketch, "E839", {"start": v(-0.16, 1.5) * mm, "end": v(-0.18, 1.53) * mm});
            skLineSegment(sketch, "E840", {"start": v(-0.18, 1.53) * mm, "end": v(-0.2, 1.54) * mm});
            skLineSegment(sketch, "E841", {"start": v(-0.2, 1.54) * mm, "end": v(-0.21, 1.56) * mm});
            skLineSegment(sketch, "E842", {"start": v(-0.21, 1.56) * mm, "end": v(-0.23, 1.59) * mm});
            skLineSegment(sketch, "E843", {"start": v(-0.23, 1.59) * mm, "end": v(-0.23, 1.6) * mm});
            skLineSegment(sketch, "E844", {"start": v(-0.23, 1.6) * mm, "end": v(-0.24, 1.6) * mm});
            skLineSegment(sketch, "E845", {"start": v(-0.24, 1.6) * mm, "end": v(-0.24, 1.61) * mm});
            skLineSegment(sketch, "E846", {"start": v(-0.24, 1.61) * mm, "end": v(-0.24, 1.63) * mm});
            skLineSegment(sketch, "E847", {"start": v(-0.24, 1.63) * mm, "end": v(-0.25, 1.65) * mm});
            skLineSegment(sketch, "E848", {"start": v(-0.25, 1.65) * mm, "end": v(-0.25, 1.66) * mm});
            skLineSegment(sketch, "E849", {"start": v(-0.25, 1.66) * mm, "end": v(-0.25, 1.68) * mm});
            skLineSegment(sketch, "E850", {"start": v(-0.25, 1.68) * mm, "end": v(-0.25, 1.68) * mm});
            skLineSegment(sketch, "E851", {"start": v(-0.25, 1.68) * mm, "end": v(-0.25, 1.7) * mm});
            skLineSegment(sketch, "E852", {"start": v(-0.25, 1.7) * mm, "end": v(-0.25, 1.71) * mm});
            skLineSegment(sketch, "E853", {"start": v(-0.25, 1.71) * mm, "end": v(-0.25, 1.73) * mm});
            skLineSegment(sketch, "E854", {"start": v(-0.25, 1.73) * mm, "end": v(-0.25, 1.75) * mm});
            skLineSegment(sketch, "E855", {"start": v(-0.25, 1.75) * mm, "end": v(-0.24, 1.77) * mm});
            skLineSegment(sketch, "E856", {"start": v(-0.24, 1.77) * mm, "end": v(-0.24, 1.78) * mm});
            skLineSegment(sketch, "E857", {"start": v(-0.24, 1.78) * mm, "end": v(-0.24, 1.79) * mm});
            skLineSegment(sketch, "E858", {"start": v(-0.24, 1.79) * mm, "end": v(-0.22, 1.82) * mm});
            skLineSegment(sketch, "E859", {"start": v(-0.22, 1.82) * mm, "end": v(-0.2, 1.86) * mm});
            skLineSegment(sketch, "E860", {"start": v(-0.2, 1.86) * mm, "end": v(-0.16, 1.9) * mm});
            skLineSegment(sketch, "E861", {"start": v(-0.16, 1.9) * mm, "end": v(-0.13, 1.91) * mm});
            skLineSegment(sketch, "E862", {"start": v(-0.13, 1.91) * mm, "end": v(-0.12, 1.92) * mm});
            skLineSegment(sketch, "E863", {"start": v(-0.12, 1.92) * mm, "end": v(-0.11, 1.92) * mm});
            skLineSegment(sketch, "E864", {"start": v(-0.11, 1.92) * mm, "end": v(-0.1, 1.92) * mm});
            skLineSegment(sketch, "E865", {"start": v(-0.1, 1.92) * mm, "end": v(-0.08, 1.93) * mm});
            skLineSegment(sketch, "E866", {"start": v(-0.08, 1.93) * mm, "end": v(-0.07, 1.93) * mm});
            skLineSegment(sketch, "E867", {"start": v(-0.07, 1.93) * mm, "end": v(-0.06, 1.94) * mm});
            skLineSegment(sketch, "E868", {"start": v(-0.06, 1.94) * mm, "end": v(-0.05, 1.94) * mm});
            skLineSegment(sketch, "E869", {"start": v(-0.05, 1.94) * mm, "end": v(-0.05, 1.94) * mm});
            skLineSegment(sketch, "E870", {"start": v(-0.05, 1.94) * mm, "end": v(-0.04, 1.94) * mm});
            skLineSegment(sketch, "E871", {"start": v(-0.04, 1.94) * mm, "end": v(-0.03, 1.94) * mm});
            skLineSegment(sketch, "E872", {"start": v(-0.03, 1.94) * mm, "end": v(-0.01, 1.94) * mm});
            skLineSegment(sketch, "E873", {"start": v(-0.01, 1.94) * mm, "end": v(0, 1.94) * mm});
            skLineSegment(sketch, "E874", {"start": v(0, 1.94) * mm, "end": v(0.02, 1.94) * mm});
            skLineSegment(sketch, "E875", {"start": v(0.02, 1.94) * mm, "end": v(0.03, 1.94) * mm});
            skLineSegment(sketch, "E876", {"start": v(0.03, 1.94) * mm, "end": v(0.04, 1.94) * mm});
            skLineSegment(sketch, "E877", {"start": v(0.04, 1.94) * mm, "end": v(0.05, 1.93) * mm});
            skLineSegment(sketch, "E878", {"start": v(0.05, 1.93) * mm, "end": v(0.05, 1.93) * mm});
            skLineSegment(sketch, "E879", {"start": v(0.49, 2.04) * mm, "end": v(0.49, 2.04) * mm});
            skLineSegment(sketch, "E880", {"start": v(0.49, 2.04) * mm, "end": v(0.48, 2.04) * mm});
            skLineSegment(sketch, "E881", {"start": v(0.48, 2.04) * mm, "end": v(0.48, 2.03) * mm});
            skLineSegment(sketch, "E882", {"start": v(0.48, 2.03) * mm, "end": v(0.47, 2.03) * mm});
            skLineSegment(sketch, "E883", {"start": v(0.47, 2.03) * mm, "end": v(0.46, 2.02) * mm});
            skLineSegment(sketch, "E884", {"start": v(0.46, 2.02) * mm, "end": v(0.45, 2.02) * mm});
            skLineSegment(sketch, "E885", {"start": v(0.45, 2.02) * mm, "end": v(0.43, 2) * mm});
            skLineSegment(sketch, "E886", {"start": v(0.43, 2) * mm, "end": v(0.41, 2) * mm});
            skLineSegment(sketch, "E887", {"start": v(0.41, 2) * mm, "end": v(0.4, 2) * mm});
            skLineSegment(sketch, "E888", {"start": v(0.4, 2) * mm, "end": v(0.4, 1.99) * mm});
            skLineSegment(sketch, "E889", {"start": v(0.4, 1.99) * mm, "end": v(0.38, 1.98) * mm});
            skLineSegment(sketch, "E890", {"start": v(0.38, 1.98) * mm, "end": v(0.36, 1.97) * mm});
            skLineSegment(sketch, "E891", {"start": v(0.36, 1.97) * mm, "end": v(0.35, 1.96) * mm});
            skLineSegment(sketch, "E892", {"start": v(0.35, 1.96) * mm, "end": v(0.34, 1.95) * mm});
            skLineSegment(sketch, "E893", {"start": v(0.34, 1.95) * mm, "end": v(0.34, 1.95) * mm});
            skLineSegment(sketch, "E894", {"start": v(0.34, 1.95) * mm, "end": v(0.33, 1.93) * mm});
            skLineSegment(sketch, "E895", {"start": v(0.33, 1.93) * mm, "end": v(0.32, 1.91) * mm});
            skLineSegment(sketch, "E896", {"start": v(0.32, 1.91) * mm, "end": v(0.33, 1.9) * mm});
            skLineSegment(sketch, "E897", {"start": v(0.33, 1.9) * mm, "end": v(0.34, 1.88) * mm});
            skLineSegment(sketch, "E898", {"start": v(0.34, 1.88) * mm, "end": v(0.35, 1.88) * mm});
            skLineSegment(sketch, "E899", {"start": v(0.35, 1.88) * mm, "end": v(0.35, 1.87) * mm});
            skLineSegment(sketch, "E900", {"start": v(0.35, 1.87) * mm, "end": v(0.35, 1.87) * mm});
            skLineSegment(sketch, "E901", {"start": v(0.35, 1.87) * mm, "end": v(0.36, 1.87) * mm});
            skLineSegment(sketch, "E902", {"start": v(0.36, 1.87) * mm, "end": v(0.36, 1.87) * mm});
            skLineSegment(sketch, "E903", {"start": v(0.36, 1.87) * mm, "end": v(0.37, 1.87) * mm});
            skLineSegment(sketch, "E904", {"start": v(0.37, 1.87) * mm, "end": v(0.37, 1.87) * mm});
            skLineSegment(sketch, "E905", {"start": v(0.37, 1.87) * mm, "end": v(0.38, 1.87) * mm});
            skLineSegment(sketch, "E906", {"start": v(0.38, 1.87) * mm, "end": v(0.38, 1.87) * mm});
            skLineSegment(sketch, "E907", {"start": v(0.38, 1.87) * mm, "end": v(0.39, 1.87) * mm});
            skLineSegment(sketch, "E908", {"start": v(0.39, 1.87) * mm, "end": v(0.4, 1.87) * mm});
            skLineSegment(sketch, "E909", {"start": v(0.4, 1.87) * mm, "end": v(0.4, 1.88) * mm});
            skLineSegment(sketch, "E910", {"start": v(0.4, 1.88) * mm, "end": v(0.41, 1.88) * mm});
            skLineSegment(sketch, "E911", {"start": v(0.41, 1.88) * mm, "end": v(0.43, 1.9) * mm});
            skLineSegment(sketch, "E912", {"start": v(0.43, 1.9) * mm, "end": v(0.44, 1.9) * mm});
            skLineSegment(sketch, "E913", {"start": v(0.44, 1.9) * mm, "end": v(0.45, 1.9) * mm});
            skLineSegment(sketch, "E914", {"start": v(0.45, 1.9) * mm, "end": v(0.45, 1.9) * mm});
            skLineSegment(sketch, "E915", {"start": v(0.45, 1.9) * mm, "end": v(0.47, 1.92) * mm});
            skLineSegment(sketch, "E916", {"start": v(0.47, 1.92) * mm, "end": v(0.5, 1.93) * mm});
            skLineSegment(sketch, "E917", {"start": v(0.5, 1.93) * mm, "end": v(0.5, 1.94) * mm});
            skLineSegment(sketch, "E918", {"start": v(0.5, 1.94) * mm, "end": v(0.52, 1.95) * mm});
            skLineSegment(sketch, "E919", {"start": v(0.52, 1.95) * mm, "end": v(0.53, 1.95) * mm});
            skLineSegment(sketch, "E920", {"start": v(0.53, 1.95) * mm, "end": v(0.54, 1.96) * mm});
            skLineSegment(sketch, "E921", {"start": v(0.54, 1.96) * mm, "end": v(0.54, 1.96) * mm});
            skLineSegment(sketch, "E922", {"start": v(0.54, 1.96) * mm, "end": v(0.54, 1.97) * mm});
            skLineSegment(sketch, "E923", {"start": v(0.54, 1.97) * mm, "end": v(0.54, 1.97) * mm});
            skLineSegment(sketch, "E924", {"start": v(0.54, 1.97) * mm, "end": v(0.55, 1.98) * mm});
            skLineSegment(sketch, "E925", {"start": v(0.55, 1.98) * mm, "end": v(0.55, 2) * mm});
            skLineSegment(sketch, "E926", {"start": v(0.55, 2) * mm, "end": v(0.54, 2) * mm});
            skLineSegment(sketch, "E927", {"start": v(0.54, 2) * mm, "end": v(0.54, 2.02) * mm});
            skLineSegment(sketch, "E928", {"start": v(0.54, 2.02) * mm, "end": v(0.53, 2.03) * mm});
            skLineSegment(sketch, "E929", {"start": v(0.53, 2.03) * mm, "end": v(0.52, 2.04) * mm});
            skLineSegment(sketch, "E930", {"start": v(0.52, 2.04) * mm, "end": v(0.5, 2.04) * mm});
            skLineSegment(sketch, "E931", {"start": v(0.5, 2.04) * mm, "end": v(0.5, 2.04) * mm});
            skLineSegment(sketch, "E932", {"start": v(0.5, 2.04) * mm, "end": v(0.49, 2.04) * mm});
            skLineSegment(sketch, "E933", {"start": v(-0.6, 1.74) * mm, "end": v(-0.6, 1.74) * mm});
            skLineSegment(sketch, "E934", {"start": v(-0.6, 1.74) * mm, "end": v(-0.62, 1.74) * mm});
            skLineSegment(sketch, "E935", {"start": v(-0.62, 1.74) * mm, "end": v(-0.63, 1.73) * mm});
            skLineSegment(sketch, "E936", {"start": v(-0.63, 1.73) * mm, "end": v(-0.64, 1.71) * mm});
            skLineSegment(sketch, "E937", {"start": v(-0.64, 1.71) * mm, "end": v(-0.64, 1.7) * mm});
            skLineSegment(sketch, "E938", {"start": v(-0.64, 1.7) * mm, "end": v(-0.64, 1.7) * mm});
            skLineSegment(sketch, "E939", {"start": v(-0.64, 1.7) * mm, "end": v(-0.64, 1.68) * mm});
            skLineSegment(sketch, "E940", {"start": v(-0.64, 1.68) * mm, "end": v(-0.63, 1.67) * mm});
            skLineSegment(sketch, "E941", {"start": v(-0.63, 1.67) * mm, "end": v(-0.62, 1.66) * mm});
            skLineSegment(sketch, "E942", {"start": v(-0.62, 1.66) * mm, "end": v(-0.61, 1.65) * mm});
            skLineSegment(sketch, "E943", {"start": v(-0.61, 1.65) * mm, "end": v(-0.6, 1.65) * mm});
            skLineSegment(sketch, "E944", {"start": v(-0.6, 1.65) * mm, "end": v(-0.6, 1.65) * mm});
            skLineSegment(sketch, "E945", {"start": v(-0.6, 1.65) * mm, "end": v(-0.58, 1.65) * mm});
            skLineSegment(sketch, "E946", {"start": v(-0.58, 1.65) * mm, "end": v(-0.55, 1.65) * mm});
            skLineSegment(sketch, "E947", {"start": v(-0.55, 1.65) * mm, "end": v(-0.53, 1.65) * mm});
            skLineSegment(sketch, "E948", {"start": v(-0.53, 1.65) * mm, "end": v(-0.52, 1.65) * mm});
            skLineSegment(sketch, "E949", {"start": v(-0.52, 1.65) * mm, "end": v(-0.51, 1.65) * mm});
            skLineSegment(sketch, "E950", {"start": v(-0.51, 1.65) * mm, "end": v(-0.5, 1.65) * mm});
            skLineSegment(sketch, "E951", {"start": v(-0.5, 1.65) * mm, "end": v(-0.47, 1.65) * mm});
            skLineSegment(sketch, "E952", {"start": v(-0.47, 1.65) * mm, "end": v(-0.46, 1.65) * mm});
            skLineSegment(sketch, "E953", {"start": v(-0.46, 1.65) * mm, "end": v(-0.45, 1.65) * mm});
            skLineSegment(sketch, "E954", {"start": v(-0.45, 1.65) * mm, "end": v(-0.44, 1.65) * mm});
            skLineSegment(sketch, "E955", {"start": v(-0.44, 1.65) * mm, "end": v(-0.43, 1.65) * mm});
            skLineSegment(sketch, "E956", {"start": v(-0.43, 1.65) * mm, "end": v(-0.43, 1.65) * mm});
            skLineSegment(sketch, "E957", {"start": v(-0.43, 1.65) * mm, "end": v(-0.42, 1.66) * mm});
            skLineSegment(sketch, "E958", {"start": v(-0.42, 1.66) * mm, "end": v(-0.41, 1.67) * mm});
            skLineSegment(sketch, "E959", {"start": v(-0.41, 1.67) * mm, "end": v(-0.4, 1.69) * mm});
            skLineSegment(sketch, "E960", {"start": v(-0.4, 1.69) * mm, "end": v(-0.4, 1.7) * mm});
            skLineSegment(sketch, "E961", {"start": v(-0.4, 1.7) * mm, "end": v(-0.4, 1.72) * mm});
            skLineSegment(sketch, "E962", {"start": v(-0.4, 1.72) * mm, "end": v(-0.41, 1.73) * mm});
            skLineSegment(sketch, "E963", {"start": v(-0.41, 1.73) * mm, "end": v(-0.41, 1.73) * mm});
            skLineSegment(sketch, "E964", {"start": v(-0.41, 1.73) * mm, "end": v(-0.42, 1.73) * mm});
            skLineSegment(sketch, "E965", {"start": v(-0.42, 1.73) * mm, "end": v(-0.42, 1.74) * mm});
            skLineSegment(sketch, "E966", {"start": v(-0.42, 1.74) * mm, "end": v(-0.43, 1.74) * mm});
            skLineSegment(sketch, "E967", {"start": v(-0.43, 1.74) * mm, "end": v(-0.43, 1.74) * mm});
            skLineSegment(sketch, "E968", {"start": v(-0.43, 1.74) * mm, "end": v(-0.44, 1.74) * mm});
            skLineSegment(sketch, "E969", {"start": v(-0.44, 1.74) * mm, "end": v(-0.45, 1.74) * mm});
            skLineSegment(sketch, "E970", {"start": v(-0.45, 1.74) * mm, "end": v(-0.46, 1.75) * mm});
            skLineSegment(sketch, "E971", {"start": v(-0.46, 1.75) * mm, "end": v(-0.47, 1.75) * mm});
            skLineSegment(sketch, "E972", {"start": v(-0.47, 1.75) * mm, "end": v(-0.5, 1.75) * mm});
            skLineSegment(sketch, "E973", {"start": v(-0.5, 1.75) * mm, "end": v(-0.5, 1.75) * mm});
            skLineSegment(sketch, "E974", {"start": v(-0.5, 1.75) * mm, "end": v(-0.52, 1.75) * mm});
            skLineSegment(sketch, "E975", {"start": v(-0.52, 1.75) * mm, "end": v(-0.52, 1.75) * mm});
            skLineSegment(sketch, "E976", {"start": v(-0.52, 1.75) * mm, "end": v(-0.55, 1.75) * mm});
            skLineSegment(sketch, "E977", {"start": v(-0.55, 1.75) * mm, "end": v(-0.57, 1.75) * mm});
            skLineSegment(sketch, "E978", {"start": v(-0.57, 1.75) * mm, "end": v(-0.6, 1.75) * mm});
            skLineSegment(sketch, "E979", {"start": v(-0.6, 1.75) * mm, "end": v(-0.6, 1.74) * mm});
            skLineSegment(sketch, "E980", {"start": v(0.42, 1.74) * mm, "end": v(0.42, 1.74) * mm});
            skLineSegment(sketch, "E981", {"start": v(0.42, 1.74) * mm, "end": v(0.4, 1.74) * mm});
            skLineSegment(sketch, "E982", {"start": v(0.4, 1.74) * mm, "end": v(0.4, 1.73) * mm});
            skLineSegment(sketch, "E983", {"start": v(0.4, 1.73) * mm, "end": v(0.39, 1.72) * mm});
            skLineSegment(sketch, "E984", {"start": v(0.39, 1.72) * mm, "end": v(0.38, 1.7) * mm});
            skLineSegment(sketch, "E985", {"start": v(0.38, 1.7) * mm, "end": v(0.38, 1.7) * mm});
            skLineSegment(sketch, "E986", {"start": v(0.38, 1.7) * mm, "end": v(0.38, 1.69) * mm});
            skLineSegment(sketch, "E987", {"start": v(0.38, 1.69) * mm, "end": v(0.39, 1.67) * mm});
            skLineSegment(sketch, "E988", {"start": v(0.39, 1.67) * mm, "end": v(0.4, 1.66) * mm});
            skLineSegment(sketch, "E989", {"start": v(0.4, 1.66) * mm, "end": v(0.4, 1.66) * mm});
            skLineSegment(sketch, "E990", {"start": v(0.4, 1.66) * mm, "end": v(0.4, 1.65) * mm});
            skLineSegment(sketch, "E991", {"start": v(0.4, 1.65) * mm, "end": v(0.4, 1.65) * mm});
            skLineSegment(sketch, "E992", {"start": v(0.4, 1.65) * mm, "end": v(0.41, 1.65) * mm});
            skLineSegment(sketch, "E993", {"start": v(0.41, 1.65) * mm, "end": v(0.42, 1.65) * mm});
            skLineSegment(sketch, "E994", {"start": v(0.42, 1.65) * mm, "end": v(0.42, 1.65) * mm});
            skLineSegment(sketch, "E995", {"start": v(0.42, 1.65) * mm, "end": v(0.43, 1.65) * mm});
            skLineSegment(sketch, "E996", {"start": v(0.43, 1.65) * mm, "end": v(0.44, 1.65) * mm});
            skLineSegment(sketch, "E997", {"start": v(0.44, 1.65) * mm, "end": v(0.45, 1.65) * mm});
            skLineSegment(sketch, "E998", {"start": v(0.45, 1.65) * mm, "end": v(0.47, 1.65) * mm});
            skLineSegment(sketch, "E999", {"start": v(0.47, 1.65) * mm, "end": v(0.49, 1.65) * mm});
            skLineSegment(sketch, "E1000", {"start": v(0.49, 1.65) * mm, "end": v(0.5, 1.65) * mm});
            skLineSegment(sketch, "E1001", {"start": v(0.5, 1.65) * mm, "end": v(0.5, 1.65) * mm});
            skLineSegment(sketch, "E1002", {"start": v(0.5, 1.65) * mm, "end": v(0.52, 1.65) * mm});
            skLineSegment(sketch, "E1003", {"start": v(0.52, 1.65) * mm, "end": v(0.54, 1.65) * mm});
            skLineSegment(sketch, "E1004", {"start": v(0.54, 1.65) * mm, "end": v(0.56, 1.65) * mm});
            skLineSegment(sketch, "E1005", {"start": v(0.56, 1.65) * mm, "end": v(0.58, 1.65) * mm});
            skLineSegment(sketch, "E1006", {"start": v(0.58, 1.65) * mm, "end": v(0.59, 1.65) * mm});
            skLineSegment(sketch, "E1007", {"start": v(0.59, 1.65) * mm, "end": v(0.6, 1.65) * mm});
            skLineSegment(sketch, "E1008", {"start": v(0.6, 1.65) * mm, "end": v(0.6, 1.65) * mm});
            skLineSegment(sketch, "E1009", {"start": v(0.6, 1.65) * mm, "end": v(0.6, 1.66) * mm});
            skLineSegment(sketch, "E1010", {"start": v(0.6, 1.66) * mm, "end": v(0.6, 1.66) * mm});
            skLineSegment(sketch, "E1011", {"start": v(0.6, 1.66) * mm, "end": v(0.61, 1.67) * mm});
            skLineSegment(sketch, "E1012", {"start": v(0.61, 1.67) * mm, "end": v(0.62, 1.68) * mm});
            skLineSegment(sketch, "E1013", {"start": v(0.62, 1.68) * mm, "end": v(0.62, 1.69) * mm});
            skLineSegment(sketch, "E1014", {"start": v(0.62, 1.69) * mm, "end": v(0.63, 1.7) * mm});
            skLineSegment(sketch, "E1015", {"start": v(0.63, 1.7) * mm, "end": v(0.63, 1.7) * mm});
            skLineSegment(sketch, "E1016", {"start": v(0.63, 1.7) * mm, "end": v(0.62, 1.7) * mm});
            skLineSegment(sketch, "E1017", {"start": v(0.62, 1.7) * mm, "end": v(0.62, 1.72) * mm});
            skLineSegment(sketch, "E1018", {"start": v(0.62, 1.72) * mm, "end": v(0.6, 1.73) * mm});
            skLineSegment(sketch, "E1019", {"start": v(0.6, 1.73) * mm, "end": v(0.6, 1.74) * mm});
            skLineSegment(sketch, "E1020", {"start": v(0.6, 1.74) * mm, "end": v(0.6, 1.74) * mm});
            skLineSegment(sketch, "E1021", {"start": v(0.6, 1.74) * mm, "end": v(0.59, 1.74) * mm});
            skLineSegment(sketch, "E1022", {"start": v(0.59, 1.74) * mm, "end": v(0.58, 1.75) * mm});
            skLineSegment(sketch, "E1023", {"start": v(0.58, 1.75) * mm, "end": v(0.57, 1.75) * mm});
            skLineSegment(sketch, "E1024", {"start": v(0.57, 1.75) * mm, "end": v(0.55, 1.75) * mm});
            skLineSegment(sketch, "E1025", {"start": v(0.55, 1.75) * mm, "end": v(0.53, 1.75) * mm});
            skLineSegment(sketch, "E1026", {"start": v(0.53, 1.75) * mm, "end": v(0.52, 1.75) * mm});
            skLineSegment(sketch, "E1027", {"start": v(0.52, 1.75) * mm, "end": v(0.5, 1.75) * mm});
            skLineSegment(sketch, "E1028", {"start": v(0.5, 1.75) * mm, "end": v(0.5, 1.75) * mm});
            skLineSegment(sketch, "E1029", {"start": v(0.5, 1.75) * mm, "end": v(0.48, 1.75) * mm});
            skLineSegment(sketch, "E1030", {"start": v(0.48, 1.75) * mm, "end": v(0.45, 1.75) * mm});
            skLineSegment(sketch, "E1031", {"start": v(0.45, 1.75) * mm, "end": v(0.43, 1.75) * mm});
            skLineSegment(sketch, "E1032", {"start": v(0.43, 1.75) * mm, "end": v(0.42, 1.74) * mm});
            skLineSegment(sketch, "E1033", {"start": v(-0.4, 1.52) * mm, "end": v(-0.4, 1.52) * mm});
            skLineSegment(sketch, "E1034", {"start": v(-0.4, 1.52) * mm, "end": v(-0.42, 1.52) * mm});
            skLineSegment(sketch, "E1035", {"start": v(-0.42, 1.52) * mm, "end": v(-0.43, 1.5) * mm});
            skLineSegment(sketch, "E1036", {"start": v(-0.43, 1.5) * mm, "end": v(-0.45, 1.5) * mm});
            skLineSegment(sketch, "E1037", {"start": v(-0.45, 1.5) * mm, "end": v(-0.48, 1.48) * mm});
            skLineSegment(sketch, "E1038", {"start": v(-0.48, 1.48) * mm, "end": v(-0.5, 1.47) * mm});
            skLineSegment(sketch, "E1039", {"start": v(-0.5, 1.47) * mm, "end": v(-0.52, 1.46) * mm});
            skLineSegment(sketch, "E1040", {"start": v(-0.52, 1.46) * mm, "end": v(-0.53, 1.45) * mm});
            skLineSegment(sketch, "E1041", {"start": v(-0.53, 1.45) * mm, "end": v(-0.54, 1.45) * mm});
            skLineSegment(sketch, "E1042", {"start": v(-0.54, 1.45) * mm, "end": v(-0.54, 1.44) * mm});
            skLineSegment(sketch, "E1043", {"start": v(-0.54, 1.44) * mm, "end": v(-0.55, 1.44) * mm});
            skLineSegment(sketch, "E1044", {"start": v(-0.55, 1.44) * mm, "end": v(-0.55, 1.43) * mm});
            skLineSegment(sketch, "E1045", {"start": v(-0.55, 1.43) * mm, "end": v(-0.56, 1.42) * mm});
            skLineSegment(sketch, "E1046", {"start": v(-0.56, 1.42) * mm, "end": v(-0.56, 1.4) * mm});
            skLineSegment(sketch, "E1047", {"start": v(-0.56, 1.4) * mm, "end": v(-0.56, 1.4) * mm});
            skLineSegment(sketch, "E1048", {"start": v(-0.56, 1.4) * mm, "end": v(-0.56, 1.38) * mm});
            skLineSegment(sketch, "E1049", {"start": v(-0.56, 1.38) * mm, "end": v(-0.55, 1.37) * mm});
            skLineSegment(sketch, "E1050", {"start": v(-0.55, 1.37) * mm, "end": v(-0.54, 1.36) * mm});
            skLineSegment(sketch, "E1051", {"start": v(-0.54, 1.36) * mm, "end": v(-0.53, 1.36) * mm});
            skLineSegment(sketch, "E1052", {"start": v(-0.53, 1.36) * mm, "end": v(-0.53, 1.36) * mm});
            skLineSegment(sketch, "E1053", {"start": v(-0.53, 1.36) * mm, "end": v(-0.52, 1.36) * mm});
            skLineSegment(sketch, "E1054", {"start": v(-0.52, 1.36) * mm, "end": v(-0.51, 1.36) * mm});
            skLineSegment(sketch, "E1055", {"start": v(-0.51, 1.36) * mm, "end": v(-0.5, 1.36) * mm});
            skLineSegment(sketch, "E1056", {"start": v(-0.5, 1.36) * mm, "end": v(-0.5, 1.36) * mm});
            skLineSegment(sketch, "E1057", {"start": v(-0.5, 1.36) * mm, "end": v(-0.49, 1.36) * mm});
            skLineSegment(sketch, "E1058", {"start": v(-0.49, 1.36) * mm, "end": v(-0.48, 1.37) * mm});
            skLineSegment(sketch, "E1059", {"start": v(-0.48, 1.37) * mm, "end": v(-0.46, 1.38) * mm});
            skLineSegment(sketch, "E1060", {"start": v(-0.46, 1.38) * mm, "end": v(-0.44, 1.4) * mm});
            skLineSegment(sketch, "E1061", {"start": v(-0.44, 1.4) * mm, "end": v(-0.42, 1.4) * mm});
            skLineSegment(sketch, "E1062", {"start": v(-0.42, 1.4) * mm, "end": v(-0.4, 1.42) * mm});
            skLineSegment(sketch, "E1063", {"start": v(-0.4, 1.42) * mm, "end": v(-0.38, 1.43) * mm});
            skLineSegment(sketch, "E1064", {"start": v(-0.38, 1.43) * mm, "end": v(-0.36, 1.44) * mm});
            skLineSegment(sketch, "E1065", {"start": v(-0.36, 1.44) * mm, "end": v(-0.36, 1.44) * mm});
            skLineSegment(sketch, "E1066", {"start": v(-0.36, 1.44) * mm, "end": v(-0.35, 1.45) * mm});
            skLineSegment(sketch, "E1067", {"start": v(-0.35, 1.45) * mm, "end": v(-0.34, 1.46) * mm});
            skLineSegment(sketch, "E1068", {"start": v(-0.34, 1.46) * mm, "end": v(-0.34, 1.48) * mm});
            skLineSegment(sketch, "E1069", {"start": v(-0.34, 1.48) * mm, "end": v(-0.35, 1.5) * mm});
            skLineSegment(sketch, "E1070", {"start": v(-0.35, 1.5) * mm, "end": v(-0.36, 1.51) * mm});
            skLineSegment(sketch, "E1071", {"start": v(-0.36, 1.51) * mm, "end": v(-0.36, 1.52) * mm});
            skLineSegment(sketch, "E1072", {"start": v(-0.36, 1.52) * mm, "end": v(-0.37, 1.52) * mm});
            skLineSegment(sketch, "E1073", {"start": v(-0.37, 1.52) * mm, "end": v(-0.37, 1.52) * mm});
            skLineSegment(sketch, "E1074", {"start": v(-0.37, 1.52) * mm, "end": v(-0.39, 1.53) * mm});
            skLineSegment(sketch, "E1075", {"start": v(-0.39, 1.53) * mm, "end": v(-0.4, 1.53) * mm});
            skLineSegment(sketch, "E1076", {"start": v(-0.4, 1.53) * mm, "end": v(-0.4, 1.52) * mm});
            skLineSegment(sketch, "E1077", {"start": v(0.35, 1.52) * mm, "end": v(0.35, 1.52) * mm});
            skLineSegment(sketch, "E1078", {"start": v(0.35, 1.52) * mm, "end": v(0.34, 1.51) * mm});
            skLineSegment(sketch, "E1079", {"start": v(0.34, 1.51) * mm, "end": v(0.33, 1.5) * mm});
            skLineSegment(sketch, "E1080", {"start": v(0.33, 1.5) * mm, "end": v(0.33, 1.5) * mm});
            skLineSegment(sketch, "E1081", {"start": v(0.33, 1.5) * mm, "end": v(0.32, 1.48) * mm});
            skLineSegment(sketch, "E1082", {"start": v(0.32, 1.48) * mm, "end": v(0.32, 1.47) * mm});
            skLineSegment(sketch, "E1083", {"start": v(0.32, 1.47) * mm, "end": v(0.33, 1.46) * mm});
            skLineSegment(sketch, "E1084", {"start": v(0.33, 1.46) * mm, "end": v(0.33, 1.45) * mm});
            skLineSegment(sketch, "E1085", {"start": v(0.33, 1.45) * mm, "end": v(0.34, 1.44) * mm});
            skLineSegment(sketch, "E1086", {"start": v(0.34, 1.44) * mm, "end": v(0.34, 1.44) * mm});
            skLineSegment(sketch, "E1087", {"start": v(0.34, 1.44) * mm, "end": v(0.35, 1.44) * mm});
            skLineSegment(sketch, "E1088", {"start": v(0.35, 1.44) * mm, "end": v(0.36, 1.43) * mm});
            skLineSegment(sketch, "E1089", {"start": v(0.36, 1.43) * mm, "end": v(0.38, 1.42) * mm});
            skLineSegment(sketch, "E1090", {"start": v(0.38, 1.42) * mm, "end": v(0.4, 1.4) * mm});
            skLineSegment(sketch, "E1091", {"start": v(0.4, 1.4) * mm, "end": v(0.43, 1.39) * mm});
            skLineSegment(sketch, "E1092", {"start": v(0.43, 1.39) * mm, "end": v(0.45, 1.38) * mm});
            skLineSegment(sketch, "E1093", {"start": v(0.45, 1.38) * mm, "end": v(0.47, 1.37) * mm});
            skLineSegment(sketch, "E1094", {"start": v(0.47, 1.37) * mm, "end": v(0.48, 1.36) * mm});
            skLineSegment(sketch, "E1095", {"start": v(0.48, 1.36) * mm, "end": v(0.48, 1.36) * mm});
            skLineSegment(sketch, "E1096", {"start": v(0.48, 1.36) * mm, "end": v(0.49, 1.36) * mm});
            skLineSegment(sketch, "E1097", {"start": v(0.49, 1.36) * mm, "end": v(0.5, 1.36) * mm});
            skLineSegment(sketch, "E1098", {"start": v(0.5, 1.36) * mm, "end": v(0.5, 1.36) * mm});
            skLineSegment(sketch, "E1099", {"start": v(0.5, 1.36) * mm, "end": v(0.51, 1.36) * mm});
            skLineSegment(sketch, "E1100", {"start": v(0.51, 1.36) * mm, "end": v(0.51, 1.36) * mm});
            skLineSegment(sketch, "E1101", {"start": v(0.51, 1.36) * mm, "end": v(0.52, 1.36) * mm});
            skLineSegment(sketch, "E1102", {"start": v(0.52, 1.36) * mm, "end": v(0.53, 1.37) * mm});
            skLineSegment(sketch, "E1103", {"start": v(0.53, 1.37) * mm, "end": v(0.54, 1.38) * mm});
            skLineSegment(sketch, "E1104", {"start": v(0.54, 1.38) * mm, "end": v(0.55, 1.4) * mm});
            skLineSegment(sketch, "E1105", {"start": v(0.55, 1.4) * mm, "end": v(0.55, 1.4) * mm});
            skLineSegment(sketch, "E1106", {"start": v(0.55, 1.4) * mm, "end": v(0.55, 1.41) * mm});
            skLineSegment(sketch, "E1107", {"start": v(0.55, 1.41) * mm, "end": v(0.54, 1.42) * mm});
            skLineSegment(sketch, "E1108", {"start": v(0.54, 1.42) * mm, "end": v(0.54, 1.43) * mm});
            skLineSegment(sketch, "E1109", {"start": v(0.54, 1.43) * mm, "end": v(0.53, 1.44) * mm});
            skLineSegment(sketch, "E1110", {"start": v(0.53, 1.44) * mm, "end": v(0.52, 1.45) * mm});
            skLineSegment(sketch, "E1111", {"start": v(0.52, 1.45) * mm, "end": v(0.52, 1.45) * mm});
            skLineSegment(sketch, "E1112", {"start": v(0.52, 1.45) * mm, "end": v(0.51, 1.45) * mm});
            skLineSegment(sketch, "E1113", {"start": v(0.51, 1.45) * mm, "end": v(0.5, 1.46) * mm});
            skLineSegment(sketch, "E1114", {"start": v(0.5, 1.46) * mm, "end": v(0.48, 1.47) * mm});
            skLineSegment(sketch, "E1115", {"start": v(0.48, 1.47) * mm, "end": v(0.46, 1.48) * mm});
            skLineSegment(sketch, "E1116", {"start": v(0.46, 1.48) * mm, "end": v(0.44, 1.5) * mm});
            skLineSegment(sketch, "E1117", {"start": v(0.44, 1.5) * mm, "end": v(0.43, 1.5) * mm});
            skLineSegment(sketch, "E1118", {"start": v(0.43, 1.5) * mm, "end": v(0.4, 1.51) * mm});
            skLineSegment(sketch, "E1119", {"start": v(0.4, 1.51) * mm, "end": v(0.4, 1.52) * mm});
            skLineSegment(sketch, "E1120", {"start": v(0.4, 1.52) * mm, "end": v(0.4, 1.52) * mm});
            skLineSegment(sketch, "E1121", {"start": v(0.4, 1.52) * mm, "end": v(0.39, 1.52) * mm});
            skLineSegment(sketch, "E1122", {"start": v(0.39, 1.52) * mm, "end": v(0.39, 1.52) * mm});
            skLineSegment(sketch, "E1123", {"start": v(0.39, 1.52) * mm, "end": v(0.37, 1.53) * mm});
            skLineSegment(sketch, "E1124", {"start": v(0.37, 1.53) * mm, "end": v(0.36, 1.52) * mm});
            skLineSegment(sketch, "E1125", {"start": v(0.36, 1.52) * mm, "end": v(0.35, 1.52) * mm});
            skLineSegment(sketch, "E1126", {"start": v(-0.25, 1.36) * mm, "end": v(-0.25, 1.36) * mm});
            skLineSegment(sketch, "E1127", {"start": v(-0.25, 1.36) * mm, "end": v(-0.26, 1.35) * mm});
            skLineSegment(sketch, "E1128", {"start": v(-0.26, 1.35) * mm, "end": v(-0.26, 1.35) * mm});
            skLineSegment(sketch, "E1129", {"start": v(-0.26, 1.35) * mm, "end": v(-0.27, 1.35) * mm});
            skLineSegment(sketch, "E1130", {"start": v(-0.27, 1.35) * mm, "end": v(-0.27, 1.34) * mm});
            skLineSegment(sketch, "E1131", {"start": v(-0.27, 1.34) * mm, "end": v(-0.28, 1.33) * mm});
            skLineSegment(sketch, "E1132", {"start": v(-0.28, 1.33) * mm, "end": v(-0.3, 1.3) * mm});
            skLineSegment(sketch, "E1133", {"start": v(-0.3, 1.3) * mm, "end": v(-0.3, 1.28) * mm});
            skLineSegment(sketch, "E1134", {"start": v(-0.3, 1.28) * mm, "end": v(-0.32, 1.26) * mm});
            skLineSegment(sketch, "E1135", {"start": v(-0.32, 1.26) * mm, "end": v(-0.33, 1.24) * mm});
            skLineSegment(sketch, "E1136", {"start": v(-0.33, 1.24) * mm, "end": v(-0.34, 1.22) * mm});
            skLineSegment(sketch, "E1137", {"start": v(-0.34, 1.22) * mm, "end": v(-0.34, 1.21) * mm});
            skLineSegment(sketch, "E1138", {"start": v(-0.34, 1.21) * mm, "end": v(-0.35, 1.2) * mm});
            skLineSegment(sketch, "E1139", {"start": v(-0.35, 1.2) * mm, "end": v(-0.35, 1.2) * mm});
            skLineSegment(sketch, "E1140", {"start": v(-0.35, 1.2) * mm, "end": v(-0.35, 1.18) * mm});
            skLineSegment(sketch, "E1141", {"start": v(-0.35, 1.18) * mm, "end": v(-0.35, 1.18) * mm});
            skLineSegment(sketch, "E1142", {"start": v(-0.35, 1.18) * mm, "end": v(-0.35, 1.17) * mm});
            skLineSegment(sketch, "E1143", {"start": v(-0.35, 1.17) * mm, "end": v(-0.34, 1.16) * mm});
            skLineSegment(sketch, "E1144", {"start": v(-0.34, 1.16) * mm, "end": v(-0.33, 1.15) * mm});
            skLineSegment(sketch, "E1145", {"start": v(-0.33, 1.15) * mm, "end": v(-0.31, 1.14) * mm});
            skLineSegment(sketch, "E1146", {"start": v(-0.31, 1.14) * mm, "end": v(-0.3, 1.14) * mm});
            skLineSegment(sketch, "E1147", {"start": v(-0.3, 1.14) * mm, "end": v(-0.3, 1.14) * mm});
            skLineSegment(sketch, "E1148", {"start": v(-0.3, 1.14) * mm, "end": v(-0.28, 1.14) * mm});
            skLineSegment(sketch, "E1149", {"start": v(-0.28, 1.14) * mm, "end": v(-0.27, 1.15) * mm});
            skLineSegment(sketch, "E1150", {"start": v(-0.27, 1.15) * mm, "end": v(-0.27, 1.16) * mm});
            skLineSegment(sketch, "E1151", {"start": v(-0.27, 1.16) * mm, "end": v(-0.26, 1.17) * mm});
            skLineSegment(sketch, "E1152", {"start": v(-0.26, 1.17) * mm, "end": v(-0.26, 1.17) * mm});
            skLineSegment(sketch, "E1153", {"start": v(-0.26, 1.17) * mm, "end": v(-0.25, 1.18) * mm});
            skLineSegment(sketch, "E1154", {"start": v(-0.25, 1.18) * mm, "end": v(-0.25, 1.19) * mm});
            skLineSegment(sketch, "E1155", {"start": v(-0.25, 1.19) * mm, "end": v(-0.24, 1.2) * mm});
            skLineSegment(sketch, "E1156", {"start": v(-0.24, 1.2) * mm, "end": v(-0.23, 1.22) * mm});
            skLineSegment(sketch, "E1157", {"start": v(-0.23, 1.22) * mm, "end": v(-0.21, 1.24) * mm});
            skLineSegment(sketch, "E1158", {"start": v(-0.21, 1.24) * mm, "end": v(-0.2, 1.26) * mm});
            skLineSegment(sketch, "E1159", {"start": v(-0.2, 1.26) * mm, "end": v(-0.2, 1.28) * mm});
            skLineSegment(sketch, "E1160", {"start": v(-0.2, 1.28) * mm, "end": v(-0.19, 1.3) * mm});
            skLineSegment(sketch, "E1161", {"start": v(-0.19, 1.3) * mm, "end": v(-0.18, 1.3) * mm});
            skLineSegment(sketch, "E1162", {"start": v(-0.18, 1.3) * mm, "end": v(-0.18, 1.3) * mm});
            skLineSegment(sketch, "E1163", {"start": v(-0.18, 1.3) * mm, "end": v(-0.18, 1.32) * mm});
            skLineSegment(sketch, "E1164", {"start": v(-0.18, 1.32) * mm, "end": v(-0.18, 1.33) * mm});
            skLineSegment(sketch, "E1165", {"start": v(-0.18, 1.33) * mm, "end": v(-0.18, 1.33) * mm});
            skLineSegment(sketch, "E1166", {"start": v(-0.18, 1.33) * mm, "end": v(-0.18, 1.34) * mm});
            skLineSegment(sketch, "E1167", {"start": v(-0.18, 1.34) * mm, "end": v(-0.19, 1.34) * mm});
            skLineSegment(sketch, "E1168", {"start": v(-0.19, 1.34) * mm, "end": v(-0.2, 1.35) * mm});
            skLineSegment(sketch, "E1169", {"start": v(-0.2, 1.35) * mm, "end": v(-0.21, 1.36) * mm});
            skLineSegment(sketch, "E1170", {"start": v(-0.21, 1.36) * mm, "end": v(-0.23, 1.36) * mm});
            skLineSegment(sketch, "E1171", {"start": v(-0.23, 1.36) * mm, "end": v(-0.24, 1.36) * mm});
            skLineSegment(sketch, "E1172", {"start": v(-0.24, 1.36) * mm, "end": v(-0.25, 1.36) * mm});
            skLineSegment(sketch, "E1173", {"start": v(0.2, 1.36) * mm, "end": v(0.2, 1.36) * mm});
            skLineSegment(sketch, "E1174", {"start": v(0.2, 1.36) * mm, "end": v(0.19, 1.36) * mm});
            skLineSegment(sketch, "E1175", {"start": v(0.19, 1.36) * mm, "end": v(0.18, 1.35) * mm});
            skLineSegment(sketch, "E1176", {"start": v(0.18, 1.35) * mm, "end": v(0.18, 1.35) * mm});
            skLineSegment(sketch, "E1177", {"start": v(0.18, 1.35) * mm, "end": v(0.17, 1.35) * mm});
            skLineSegment(sketch, "E1178", {"start": v(0.17, 1.35) * mm, "end": v(0.17, 1.34) * mm});
            skLineSegment(sketch, "E1179", {"start": v(0.17, 1.34) * mm, "end": v(0.16, 1.33) * mm});
            skLineSegment(sketch, "E1180", {"start": v(0.16, 1.33) * mm, "end": v(0.16, 1.31) * mm});
            skLineSegment(sketch, "E1181", {"start": v(0.16, 1.31) * mm, "end": v(0.16, 1.3) * mm});
            skLineSegment(sketch, "E1182", {"start": v(0.16, 1.3) * mm, "end": v(0.17, 1.3) * mm});
            skLineSegment(sketch, "E1183", {"start": v(0.17, 1.3) * mm, "end": v(0.17, 1.3) * mm});
            skLineSegment(sketch, "E1184", {"start": v(0.17, 1.3) * mm, "end": v(0.18, 1.28) * mm});
            skLineSegment(sketch, "E1185", {"start": v(0.18, 1.28) * mm, "end": v(0.2, 1.25) * mm});
            skLineSegment(sketch, "E1186", {"start": v(0.2, 1.25) * mm, "end": v(0.2, 1.23) * mm});
            skLineSegment(sketch, "E1187", {"start": v(0.2, 1.23) * mm, "end": v(0.22, 1.2) * mm});
            skLineSegment(sketch, "E1188", {"start": v(0.22, 1.2) * mm, "end": v(0.23, 1.19) * mm});
            skLineSegment(sketch, "E1189", {"start": v(0.23, 1.19) * mm, "end": v(0.24, 1.17) * mm});
            skLineSegment(sketch, "E1190", {"start": v(0.24, 1.17) * mm, "end": v(0.24, 1.16) * mm});
            skLineSegment(sketch, "E1191", {"start": v(0.24, 1.16) * mm, "end": v(0.24, 1.16) * mm});
            skLineSegment(sketch, "E1192", {"start": v(0.24, 1.16) * mm, "end": v(0.25, 1.16) * mm});
            skLineSegment(sketch, "E1193", {"start": v(0.25, 1.16) * mm, "end": v(0.26, 1.15) * mm});
            skLineSegment(sketch, "E1194", {"start": v(0.26, 1.15) * mm, "end": v(0.27, 1.14) * mm});
            skLineSegment(sketch, "E1195", {"start": v(0.27, 1.14) * mm, "end": v(0.28, 1.14) * mm});
            skLineSegment(sketch, "E1196", {"start": v(0.28, 1.14) * mm, "end": v(0.3, 1.14) * mm});
            skLineSegment(sketch, "E1197", {"start": v(0.3, 1.14) * mm, "end": v(0.31, 1.15) * mm});
            skLineSegment(sketch, "E1198", {"start": v(0.31, 1.15) * mm, "end": v(0.32, 1.16) * mm});
            skLineSegment(sketch, "E1199", {"start": v(0.32, 1.16) * mm, "end": v(0.33, 1.17) * mm});
            skLineSegment(sketch, "E1200", {"start": v(0.33, 1.17) * mm, "end": v(0.33, 1.19) * mm});
            skLineSegment(sketch, "E1201", {"start": v(0.33, 1.19) * mm, "end": v(0.33, 1.2) * mm});
            skLineSegment(sketch, "E1202", {"start": v(0.33, 1.2) * mm, "end": v(0.33, 1.2) * mm});
            skLineSegment(sketch, "E1203", {"start": v(0.33, 1.2) * mm, "end": v(0.33, 1.21) * mm});
            skLineSegment(sketch, "E1204", {"start": v(0.33, 1.21) * mm, "end": v(0.33, 1.21) * mm});
            skLineSegment(sketch, "E1205", {"start": v(0.33, 1.21) * mm, "end": v(0.32, 1.22) * mm});
            skLineSegment(sketch, "E1206", {"start": v(0.32, 1.22) * mm, "end": v(0.32, 1.23) * mm});
            skLineSegment(sketch, "E1207", {"start": v(0.32, 1.23) * mm, "end": v(0.3, 1.24) * mm});
            skLineSegment(sketch, "E1208", {"start": v(0.3, 1.24) * mm, "end": v(0.3, 1.27) * mm});
            skLineSegment(sketch, "E1209", {"start": v(0.3, 1.27) * mm, "end": v(0.28, 1.29) * mm});
            skLineSegment(sketch, "E1210", {"start": v(0.28, 1.29) * mm, "end": v(0.27, 1.3) * mm});
            skLineSegment(sketch, "E1211", {"start": v(0.27, 1.3) * mm, "end": v(0.26, 1.33) * mm});
            skLineSegment(sketch, "E1212", {"start": v(0.26, 1.33) * mm, "end": v(0.25, 1.34) * mm});
            skLineSegment(sketch, "E1213", {"start": v(0.25, 1.34) * mm, "end": v(0.25, 1.35) * mm});
            skLineSegment(sketch, "E1214", {"start": v(0.25, 1.35) * mm, "end": v(0.25, 1.35) * mm});
            skLineSegment(sketch, "E1215", {"start": v(0.25, 1.35) * mm, "end": v(0.24, 1.35) * mm});
            skLineSegment(sketch, "E1216", {"start": v(0.24, 1.35) * mm, "end": v(0.24, 1.36) * mm});
            skLineSegment(sketch, "E1217", {"start": v(0.24, 1.36) * mm, "end": v(0.22, 1.36) * mm});
            skLineSegment(sketch, "E1218", {"start": v(0.22, 1.36) * mm, "end": v(0.2, 1.36) * mm});
            skLineSegment(sketch, "E1219", {"start": v(-0.03, 1.3) * mm, "end": v(-0.03, 1.3) * mm});
            skLineSegment(sketch, "E1220", {"start": v(-0.03, 1.3) * mm, "end": v(-0.04, 1.3) * mm});
            skLineSegment(sketch, "E1221", {"start": v(-0.04, 1.3) * mm, "end": v(-0.04, 1.3) * mm});
            skLineSegment(sketch, "E1222", {"start": v(-0.04, 1.3) * mm, "end": v(-0.05, 1.29) * mm});
            skLineSegment(sketch, "E1223", {"start": v(-0.05, 1.29) * mm, "end": v(-0.05, 1.28) * mm});
            skLineSegment(sketch, "E1224", {"start": v(-0.05, 1.28) * mm, "end": v(-0.05, 1.28) * mm});
            skLineSegment(sketch, "E1225", {"start": v(-0.05, 1.28) * mm, "end": v(-0.05, 1.27) * mm});
            skLineSegment(sketch, "E1226", {"start": v(-0.05, 1.27) * mm, "end": v(-0.06, 1.27) * mm});
            skLineSegment(sketch, "E1227", {"start": v(-0.06, 1.27) * mm, "end": v(-0.06, 1.26) * mm});
            skLineSegment(sketch, "E1228", {"start": v(-0.06, 1.26) * mm, "end": v(-0.06, 1.25) * mm});
            skLineSegment(sketch, "E1229", {"start": v(-0.06, 1.25) * mm, "end": v(-0.06, 1.24) * mm});
            skLineSegment(sketch, "E1230", {"start": v(-0.06, 1.24) * mm, "end": v(-0.06, 1.22) * mm});
            skLineSegment(sketch, "E1231", {"start": v(-0.06, 1.22) * mm, "end": v(-0.06, 1.2) * mm});
            skLineSegment(sketch, "E1232", {"start": v(-0.06, 1.2) * mm, "end": v(-0.06, 1.2) * mm});
            skLineSegment(sketch, "E1233", {"start": v(-0.06, 1.2) * mm, "end": v(-0.06, 1.17) * mm});
            skLineSegment(sketch, "E1234", {"start": v(-0.06, 1.17) * mm, "end": v(-0.06, 1.14) * mm});
            skLineSegment(sketch, "E1235", {"start": v(-0.06, 1.14) * mm, "end": v(-0.06, 1.13) * mm});
            skLineSegment(sketch, "E1236", {"start": v(-0.06, 1.13) * mm, "end": v(-0.06, 1.11) * mm});
            skLineSegment(sketch, "E1237", {"start": v(-0.06, 1.11) * mm, "end": v(-0.06, 1.1) * mm});
            skLineSegment(sketch, "E1238", {"start": v(-0.06, 1.1) * mm, "end": v(-0.05, 1.1) * mm});
            skLineSegment(sketch, "E1239", {"start": v(-0.05, 1.1) * mm, "end": v(-0.05, 1.09) * mm});
            skLineSegment(sketch, "E1240", {"start": v(-0.05, 1.09) * mm, "end": v(-0.05, 1.09) * mm});
            skLineSegment(sketch, "E1241", {"start": v(-0.05, 1.09) * mm, "end": v(-0.05, 1.08) * mm});
            skLineSegment(sketch, "E1242", {"start": v(-0.05, 1.08) * mm, "end": v(-0.05, 1.08) * mm});
            skLineSegment(sketch, "E1243", {"start": v(-0.05, 1.08) * mm, "end": v(-0.04, 1.08) * mm});
            skLineSegment(sketch, "E1244", {"start": v(-0.04, 1.08) * mm, "end": v(-0.03, 1.07) * mm});
            skLineSegment(sketch, "E1245", {"start": v(-0.03, 1.07) * mm, "end": v(-0.02, 1.06) * mm});
            skLineSegment(sketch, "E1246", {"start": v(-0.02, 1.06) * mm, "end": v(-0.01, 1.06) * mm});
            skLineSegment(sketch, "E1247", {"start": v(-0.01, 1.06) * mm, "end": v(0, 1.06) * mm});
            skLineSegment(sketch, "E1248", {"start": v(0, 1.06) * mm, "end": v(0, 1.06) * mm});
            skLineSegment(sketch, "E1249", {"start": v(0, 1.06) * mm, "end": v(0, 1.07) * mm});
            skLineSegment(sketch, "E1250", {"start": v(0, 1.07) * mm, "end": v(0.02, 1.07) * mm});
            skLineSegment(sketch, "E1251", {"start": v(0.02, 1.07) * mm, "end": v(0.03, 1.08) * mm});
            skLineSegment(sketch, "E1252", {"start": v(0.03, 1.08) * mm, "end": v(0.04, 1.1) * mm});
            skLineSegment(sketch, "E1253", {"start": v(0.04, 1.1) * mm, "end": v(0.04, 1.1) * mm});
            skLineSegment(sketch, "E1254", {"start": v(0.04, 1.1) * mm, "end": v(0.04, 1.13) * mm});
            skLineSegment(sketch, "E1255", {"start": v(0.04, 1.13) * mm, "end": v(0.04, 1.15) * mm});
            skLineSegment(sketch, "E1256", {"start": v(0.04, 1.15) * mm, "end": v(0.04, 1.18) * mm});
            skLineSegment(sketch, "E1257", {"start": v(0.04, 1.18) * mm, "end": v(0.04, 1.19) * mm});
            skLineSegment(sketch, "E1258", {"start": v(0.04, 1.19) * mm, "end": v(0.04, 1.2) * mm});
            skLineSegment(sketch, "E1259", {"start": v(0.04, 1.2) * mm, "end": v(0.04, 1.21) * mm});
            skLineSegment(sketch, "E1260", {"start": v(0.04, 1.21) * mm, "end": v(0.04, 1.23) * mm});
            skLineSegment(sketch, "E1261", {"start": v(0.04, 1.23) * mm, "end": v(0.04, 1.25) * mm});
            skLineSegment(sketch, "E1262", {"start": v(0.04, 1.25) * mm, "end": v(0.04, 1.26) * mm});
            skLineSegment(sketch, "E1263", {"start": v(0.04, 1.26) * mm, "end": v(0.04, 1.27) * mm});
            skLineSegment(sketch, "E1264", {"start": v(0.04, 1.27) * mm, "end": v(0.04, 1.27) * mm});
            skLineSegment(sketch, "E1265", {"start": v(0.04, 1.27) * mm, "end": v(0.04, 1.28) * mm});
            skLineSegment(sketch, "E1266", {"start": v(0.04, 1.28) * mm, "end": v(0.03, 1.28) * mm});
            skLineSegment(sketch, "E1267", {"start": v(0.03, 1.28) * mm, "end": v(0.03, 1.28) * mm});
            skLineSegment(sketch, "E1268", {"start": v(0.03, 1.28) * mm, "end": v(0.02, 1.3) * mm});
            skLineSegment(sketch, "E1269", {"start": v(0.02, 1.3) * mm, "end": v(0, 1.3) * mm});
            skLineSegment(sketch, "E1270", {"start": v(0, 1.3) * mm, "end": v(-0.01, 1.3) * mm});
            skLineSegment(sketch, "E1271", {"start": v(-0.01, 1.3) * mm, "end": v(-0.02, 1.3) * mm});
            skLineSegment(sketch, "E1272", {"start": v(-0.02, 1.3) * mm, "end": v(-0.03, 1.3) * mm});
            skSolve(sketch);
        }
        {
            var Q0;
            Q0=makeQuery(id+"F2.imprint","IMPRINT",FACE,{"disambiguationData":[TD([[makeQuery(id+"F2.imprint","IMPRINT",EDGE,{"derivedFrom":sQuery(id+"F2.wireOp",EDGE,"E1")}),-1.0]])]});
            var sketch = newSketch(context, id + "F5", { "sketchPlane" : qUnion([Q0])});
            skLineSegment(sketch, "E1273", {"start": v(1.33, -0.54) * mm, "end": v(1.32, -0.54) * mm});
            skLineSegment(sketch, "E1274", {"start": v(1.32, -0.54) * mm, "end": v(1.28, -0.55) * mm});
            skLineSegment(sketch, "E1275", {"start": v(1.28, -0.55) * mm, "end": v(1.24, -0.55) * mm});
            skLineSegment(sketch, "E1276", {"start": v(1.24, -0.55) * mm, "end": v(1.2, -0.56) * mm});
            skLineSegment(sketch, "E1277", {"start": v(1.2, -0.56) * mm, "end": v(1.17, -0.58) * mm});
            skLineSegment(sketch, "E1278", {"start": v(1.17, -0.58) * mm, "end": v(1.13, -0.6) * mm});
            skLineSegment(sketch, "E1279", {"start": v(1.13, -0.6) * mm, "end": v(1.1, -0.6) * mm});
            skLineSegment(sketch, "E1280", {"start": v(1.1, -0.6) * mm, "end": v(1.06, -0.63) * mm});
            skLineSegment(sketch, "E1281", {"start": v(1.06, -0.63) * mm, "end": v(1.03, -0.64) * mm});
            skLineSegment(sketch, "E1282", {"start": v(1.03, -0.64) * mm, "end": v(1.02, -0.65) * mm});
            skLineSegment(sketch, "E1283", {"start": v(1.02, -0.65) * mm, "end": v(1, -0.66) * mm});
            skLineSegment(sketch, "E1284", {"start": v(1, -0.66) * mm, "end": v(0.98, -0.68) * mm});
            skLineSegment(sketch, "E1285", {"start": v(0.98, -0.68) * mm, "end": v(0.94, -0.71) * mm});
            skLineSegment(sketch, "E1286", {"start": v(0.94, -0.71) * mm, "end": v(0.9, -0.75) * mm});
            skLineSegment(sketch, "E1287", {"start": v(0.9, -0.75) * mm, "end": v(0.87, -0.8) * mm});
            skLineSegment(sketch, "E1288", {"start": v(0.87, -0.8) * mm, "end": v(0.84, -0.83) * mm});
            skLineSegment(sketch, "E1289", {"start": v(0.84, -0.83) * mm, "end": v(0.81, -0.88) * mm});
            skLineSegment(sketch, "E1290", {"start": v(0.81, -0.88) * mm, "end": v(0.79, -0.93) * mm});
            skLineSegment(sketch, "E1291", {"start": v(0.79, -0.93) * mm, "end": v(0.78, -0.96) * mm});
            skLineSegment(sketch, "E1292", {"start": v(0.78, -0.96) * mm, "end": v(0.77, -0.98) * mm});
            skLineSegment(sketch, "E1293", {"start": v(0.77, -0.98) * mm, "end": v(0.77, -0.99) * mm});
            skLineSegment(sketch, "E1294", {"start": v(0.77, -0.99) * mm, "end": v(0.76, -1.03) * mm});
            skLineSegment(sketch, "E1295", {"start": v(0.76, -1.03) * mm, "end": v(0.74, -1.08) * mm});
            skLineSegment(sketch, "E1296", {"start": v(0.74, -1.08) * mm, "end": v(0.74, -1.14) * mm});
            skLineSegment(sketch, "E1297", {"start": v(0.74, -1.14) * mm, "end": v(0.74, -1.2) * mm});
            skLineSegment(sketch, "E1298", {"start": v(0.74, -1.2) * mm, "end": v(0.74, -1.25) * mm});
            skLineSegment(sketch, "E1299", {"start": v(0.74, -1.25) * mm, "end": v(0.75, -1.3) * mm});
            skLineSegment(sketch, "E1300", {"start": v(0.75, -1.3) * mm, "end": v(0.76, -1.36) * mm});
            skLineSegment(sketch, "E1301", {"start": v(0.76, -1.36) * mm, "end": v(0.78, -1.4) * mm});
            skLineSegment(sketch, "E1302", {"start": v(0.78, -1.4) * mm, "end": v(0.78, -1.42) * mm});
            skLineSegment(sketch, "E1303", {"start": v(0.78, -1.42) * mm, "end": v(0.78, -1.42) * mm});
            skLineSegment(sketch, "E1304", {"start": v(0.78, -1.42) * mm, "end": v(0.79, -1.43) * mm});
            skLineSegment(sketch, "E1305", {"start": v(0.79, -1.43) * mm, "end": v(0.8, -1.44) * mm});
            skLineSegment(sketch, "E1306", {"start": v(0.8, -1.44) * mm, "end": v(0.8, -1.45) * mm});
            skLineSegment(sketch, "E1307", {"start": v(0.8, -1.45) * mm, "end": v(0.8, -1.46) * mm});
            skLineSegment(sketch, "E1308", {"start": v(0.8, -1.46) * mm, "end": v(0.81, -1.47) * mm});
            skLineSegment(sketch, "E1309", {"start": v(0.81, -1.47) * mm, "end": v(0.82, -1.49) * mm});
            skLineSegment(sketch, "E1310", {"start": v(0.82, -1.49) * mm, "end": v(0.82, -1.5) * mm});
            skLineSegment(sketch, "E1311", {"start": v(0.82, -1.5) * mm, "end": v(0.83, -1.5) * mm});
            skLineSegment(sketch, "E1312", {"start": v(0.83, -1.5) * mm, "end": v(0.83, -1.5) * mm});
            skLineSegment(sketch, "E1313", {"start": v(0.83, -1.5) * mm, "end": v(0.83, -1.52) * mm});
            skLineSegment(sketch, "E1314", {"start": v(0.83, -1.52) * mm, "end": v(0.85, -1.54) * mm});
            skLineSegment(sketch, "E1315", {"start": v(0.85, -1.54) * mm, "end": v(0.87, -1.57) * mm});
            skLineSegment(sketch, "E1316", {"start": v(0.87, -1.57) * mm, "end": v(0.9, -1.6) * mm});
            skLineSegment(sketch, "E1317", {"start": v(0.9, -1.6) * mm, "end": v(0.91, -1.62) * mm});
            skLineSegment(sketch, "E1318", {"start": v(0.91, -1.62) * mm, "end": v(0.94, -1.64) * mm});
            skLineSegment(sketch, "E1319", {"start": v(0.94, -1.64) * mm, "end": v(0.97, -1.67) * mm});
            skLineSegment(sketch, "E1320", {"start": v(0.97, -1.67) * mm, "end": v(1, -1.69) * mm});
            skLineSegment(sketch, "E1321", {"start": v(1, -1.69) * mm, "end": v(1.01, -1.7) * mm});
            skLineSegment(sketch, "E1322", {"start": v(1.01, -1.7) * mm, "end": v(1.02, -1.7) * mm});
            skLineSegment(sketch, "E1323", {"start": v(1.02, -1.7) * mm, "end": v(1.03, -1.72) * mm});
            skLineSegment(sketch, "E1324", {"start": v(1.03, -1.72) * mm, "end": v(1.07, -1.74) * mm});
            skLineSegment(sketch, "E1325", {"start": v(1.07, -1.74) * mm, "end": v(1.12, -1.76) * mm});
            skLineSegment(sketch, "E1326", {"start": v(1.12, -1.76) * mm, "end": v(1.17, -1.78) * mm});
            skLineSegment(sketch, "E1327", {"start": v(1.17, -1.78) * mm, "end": v(1.23, -1.8) * mm});
            skLineSegment(sketch, "E1328", {"start": v(1.23, -1.8) * mm, "end": v(1.28, -1.8) * mm});
            skLineSegment(sketch, "E1329", {"start": v(1.28, -1.8) * mm, "end": v(1.34, -1.82) * mm});
            skLineSegment(sketch, "E1330", {"start": v(1.34, -1.82) * mm, "end": v(1.4, -1.82) * mm});
            skLineSegment(sketch, "E1331", {"start": v(1.4, -1.82) * mm, "end": v(1.44, -1.81) * mm});
            skLineSegment(sketch, "E1332", {"start": v(1.44, -1.81) * mm, "end": v(1.46, -1.81) * mm});
            skLineSegment(sketch, "E1333", {"start": v(1.46, -1.81) * mm, "end": v(1.46, -1.81) * mm});
            skLineSegment(sketch, "E1334", {"start": v(1.46, -1.81) * mm, "end": v(1.5, -1.8) * mm});
            skLineSegment(sketch, "E1335", {"start": v(1.5, -1.8) * mm, "end": v(1.52, -1.8) * mm});
            skLineSegment(sketch, "E1336", {"start": v(1.52, -1.8) * mm, "end": v(1.53, -1.8) * mm});
            skLineSegment(sketch, "E1337", {"start": v(1.53, -1.8) * mm, "end": v(1.53, -1.8) * mm});
            skLineSegment(sketch, "E1338", {"start": v(1.53, -1.8) * mm, "end": v(1.54, -1.8) * mm});
            skLineSegment(sketch, "E1339", {"start": v(1.54, -1.8) * mm, "end": v(1.55, -1.8) * mm});
            skLineSegment(sketch, "E1340", {"start": v(1.55, -1.8) * mm, "end": v(1.56, -1.79) * mm});
            skLineSegment(sketch, "E1341", {"start": v(1.56, -1.79) * mm, "end": v(1.57, -1.79) * mm});
            skLineSegment(sketch, "E1342", {"start": v(1.57, -1.79) * mm, "end": v(1.58, -1.78) * mm});
            skLineSegment(sketch, "E1343", {"start": v(1.58, -1.78) * mm, "end": v(1.58, -1.78) * mm});
            skLineSegment(sketch, "E1344", {"start": v(1.58, -1.78) * mm, "end": v(1.59, -1.77) * mm});
            skLineSegment(sketch, "E1345", {"start": v(1.59, -1.77) * mm, "end": v(1.59, -1.77) * mm});
            skLineSegment(sketch, "E1346", {"start": v(1.59, -1.77) * mm, "end": v(1.6, -1.77) * mm});
            skLineSegment(sketch, "E1347", {"start": v(1.6, -1.77) * mm, "end": v(1.6, -1.76) * mm});
            skLineSegment(sketch, "E1348", {"start": v(1.6, -1.76) * mm, "end": v(1.6, -1.75) * mm});
            skLineSegment(sketch, "E1349", {"start": v(1.6, -1.75) * mm, "end": v(1.6, -1.75) * mm});
            skLineSegment(sketch, "E1350", {"start": v(1.6, -1.75) * mm, "end": v(1.6, -1.74) * mm});
            skLineSegment(sketch, "E1351", {"start": v(1.6, -1.74) * mm, "end": v(1.6, -1.74) * mm});
            skLineSegment(sketch, "E1352", {"start": v(1.6, -1.74) * mm, "end": v(1.6, -1.73) * mm});
            skLineSegment(sketch, "E1353", {"start": v(1.6, -1.73) * mm, "end": v(1.59, -1.73) * mm});
            skLineSegment(sketch, "E1354", {"start": v(1.59, -1.73) * mm, "end": v(1.58, -1.72) * mm});
            skLineSegment(sketch, "E1355", {"start": v(1.58, -1.72) * mm, "end": v(1.58, -1.72) * mm});
            skLineSegment(sketch, "E1356", {"start": v(1.58, -1.72) * mm, "end": v(1.57, -1.71) * mm});
            skLineSegment(sketch, "E1357", {"start": v(1.57, -1.71) * mm, "end": v(1.57, -1.7) * mm});
            skLineSegment(sketch, "E1358", {"start": v(1.57, -1.7) * mm, "end": v(1.56, -1.7) * mm});
            skLineSegment(sketch, "E1359", {"start": v(1.56, -1.7) * mm, "end": v(1.56, -1.7) * mm});
            skLineSegment(sketch, "E1360", {"start": v(1.56, -1.7) * mm, "end": v(1.55, -1.7) * mm});
            skLineSegment(sketch, "E1361", {"start": v(1.55, -1.7) * mm, "end": v(1.53, -1.7) * mm});
            skLineSegment(sketch, "E1362", {"start": v(1.53, -1.7) * mm, "end": v(1.5, -1.69) * mm});
            skLineSegment(sketch, "E1363", {"start": v(1.5, -1.69) * mm, "end": v(1.48, -1.67) * mm});
            skLineSegment(sketch, "E1364", {"start": v(1.48, -1.67) * mm, "end": v(1.45, -1.66) * mm});
            skLineSegment(sketch, "E1365", {"start": v(1.45, -1.66) * mm, "end": v(1.43, -1.64) * mm});
            skLineSegment(sketch, "E1366", {"start": v(1.43, -1.64) * mm, "end": v(1.4, -1.63) * mm});
            skLineSegment(sketch, "E1367", {"start": v(1.4, -1.63) * mm, "end": v(1.38, -1.61) * mm});
            skLineSegment(sketch, "E1368", {"start": v(1.38, -1.61) * mm, "end": v(1.36, -1.6) * mm});
            skLineSegment(sketch, "E1369", {"start": v(1.36, -1.6) * mm, "end": v(1.34, -1.57) * mm});
            skLineSegment(sketch, "E1370", {"start": v(1.34, -1.57) * mm, "end": v(1.32, -1.55) * mm});
            skLineSegment(sketch, "E1371", {"start": v(1.32, -1.55) * mm, "end": v(1.3, -1.53) * mm});
            skLineSegment(sketch, "E1372", {"start": v(1.3, -1.53) * mm, "end": v(1.28, -1.5) * mm});
            skLineSegment(sketch, "E1373", {"start": v(1.28, -1.5) * mm, "end": v(1.27, -1.48) * mm});
            skLineSegment(sketch, "E1374", {"start": v(1.27, -1.48) * mm, "end": v(1.25, -1.46) * mm});
            skLineSegment(sketch, "E1375", {"start": v(1.25, -1.46) * mm, "end": v(1.24, -1.43) * mm});
            skLineSegment(sketch, "E1376", {"start": v(1.24, -1.43) * mm, "end": v(1.23, -1.41) * mm});
            skLineSegment(sketch, "E1377", {"start": v(1.23, -1.41) * mm, "end": v(1.22, -1.4) * mm});
            skLineSegment(sketch, "E1378", {"start": v(1.22, -1.4) * mm, "end": v(1.22, -1.4) * mm});
            skLineSegment(sketch, "E1379", {"start": v(1.22, -1.4) * mm, "end": v(1.2, -1.37) * mm});
            skLineSegment(sketch, "E1380", {"start": v(1.2, -1.37) * mm, "end": v(1.2, -1.33) * mm});
            skLineSegment(sketch, "E1381", {"start": v(1.2, -1.33) * mm, "end": v(1.19, -1.28) * mm});
            skLineSegment(sketch, "E1382", {"start": v(1.19, -1.28) * mm, "end": v(1.18, -1.24) * mm});
            skLineSegment(sketch, "E1383", {"start": v(1.18, -1.24) * mm, "end": v(1.18, -1.2) * mm});
            skLineSegment(sketch, "E1384", {"start": v(1.18, -1.2) * mm, "end": v(1.18, -1.16) * mm});
            skLineSegment(sketch, "E1385", {"start": v(1.18, -1.16) * mm, "end": v(1.18, -1.12) * mm});
            skLineSegment(sketch, "E1386", {"start": v(1.18, -1.12) * mm, "end": v(1.18, -1.08) * mm});
            skLineSegment(sketch, "E1387", {"start": v(1.18, -1.08) * mm, "end": v(1.19, -1.07) * mm});
            skLineSegment(sketch, "E1388", {"start": v(1.19, -1.07) * mm, "end": v(1.19, -1.06) * mm});
            skLineSegment(sketch, "E1389", {"start": v(1.19, -1.06) * mm, "end": v(1.2, -1.03) * mm});
            skLineSegment(sketch, "E1390", {"start": v(1.2, -1.03) * mm, "end": v(1.2, -1) * mm});
            skLineSegment(sketch, "E1391", {"start": v(1.2, -1) * mm, "end": v(1.22, -0.95) * mm});
            skLineSegment(sketch, "E1392", {"start": v(1.22, -0.95) * mm, "end": v(1.24, -0.91) * mm});
            skLineSegment(sketch, "E1393", {"start": v(1.24, -0.91) * mm, "end": v(1.26, -0.88) * mm});
            skLineSegment(sketch, "E1394", {"start": v(1.26, -0.88) * mm, "end": v(1.29, -0.84) * mm});
            skLineSegment(sketch, "E1395", {"start": v(1.29, -0.84) * mm, "end": v(1.31, -0.8) * mm});
            skLineSegment(sketch, "E1396", {"start": v(1.31, -0.8) * mm, "end": v(1.34, -0.79) * mm});
            skLineSegment(sketch, "E1397", {"start": v(1.34, -0.79) * mm, "end": v(1.34, -0.78) * mm});
            skLineSegment(sketch, "E1398", {"start": v(1.34, -0.78) * mm, "end": v(1.36, -0.77) * mm});
            skLineSegment(sketch, "E1399", {"start": v(1.36, -0.77) * mm, "end": v(1.4, -0.74) * mm});
            skLineSegment(sketch, "E1400", {"start": v(1.4, -0.74) * mm, "end": v(1.44, -0.7) * mm});
            skLineSegment(sketch, "E1401", {"start": v(1.44, -0.7) * mm, "end": v(1.5, -0.67) * mm});
            skLineSegment(sketch, "E1402", {"start": v(1.5, -0.67) * mm, "end": v(1.54, -0.66) * mm});
            skLineSegment(sketch, "E1403", {"start": v(1.54, -0.66) * mm, "end": v(1.55, -0.65) * mm});
            skLineSegment(sketch, "E1404", {"start": v(1.55, -0.65) * mm, "end": v(1.56, -0.65) * mm});
            skLineSegment(sketch, "E1405", {"start": v(1.56, -0.65) * mm, "end": v(1.56, -0.65) * mm});
            skLineSegment(sketch, "E1406", {"start": v(1.56, -0.65) * mm, "end": v(1.57, -0.64) * mm});
            skLineSegment(sketch, "E1407", {"start": v(1.57, -0.64) * mm, "end": v(1.58, -0.64) * mm});
            skLineSegment(sketch, "E1408", {"start": v(1.58, -0.64) * mm, "end": v(1.58, -0.64) * mm});
            skLineSegment(sketch, "E1409", {"start": v(1.58, -0.64) * mm, "end": v(1.59, -0.63) * mm});
            skLineSegment(sketch, "E1410", {"start": v(1.59, -0.63) * mm, "end": v(1.6, -0.62) * mm});
            skLineSegment(sketch, "E1411", {"start": v(1.6, -0.62) * mm, "end": v(1.6, -0.62) * mm});
            skLineSegment(sketch, "E1412", {"start": v(1.6, -0.62) * mm, "end": v(1.6, -0.61) * mm});
            skLineSegment(sketch, "E1413", {"start": v(1.6, -0.61) * mm, "end": v(1.6, -0.6) * mm});
            skLineSegment(sketch, "E1414", {"start": v(1.6, -0.6) * mm, "end": v(1.6, -0.6) * mm});
            skLineSegment(sketch, "E1415", {"start": v(1.6, -0.6) * mm, "end": v(1.59, -0.59) * mm});
            skLineSegment(sketch, "E1416", {"start": v(1.59, -0.59) * mm, "end": v(1.58, -0.58) * mm});
            skLineSegment(sketch, "E1417", {"start": v(1.58, -0.58) * mm, "end": v(1.58, -0.58) * mm});
            skLineSegment(sketch, "E1418", {"start": v(1.58, -0.58) * mm, "end": v(1.57, -0.57) * mm});
            skLineSegment(sketch, "E1419", {"start": v(1.57, -0.57) * mm, "end": v(1.56, -0.57) * mm});
            skLineSegment(sketch, "E1420", {"start": v(1.56, -0.57) * mm, "end": v(1.55, -0.56) * mm});
            skLineSegment(sketch, "E1421", {"start": v(1.55, -0.56) * mm, "end": v(1.55, -0.56) * mm});
            skLineSegment(sketch, "E1422", {"start": v(1.55, -0.56) * mm, "end": v(1.54, -0.56) * mm});
            skLineSegment(sketch, "E1423", {"start": v(1.54, -0.56) * mm, "end": v(1.52, -0.56) * mm});
            skLineSegment(sketch, "E1424", {"start": v(1.52, -0.56) * mm, "end": v(1.5, -0.55) * mm});
            skLineSegment(sketch, "E1425", {"start": v(1.5, -0.55) * mm, "end": v(1.47, -0.55) * mm});
            skLineSegment(sketch, "E1426", {"start": v(1.47, -0.55) * mm, "end": v(1.45, -0.54) * mm});
            skLineSegment(sketch, "E1427", {"start": v(1.45, -0.54) * mm, "end": v(1.44, -0.54) * mm});
            skLineSegment(sketch, "E1428", {"start": v(1.44, -0.54) * mm, "end": v(1.44, -0.54) * mm});
            skLineSegment(sketch, "E1429", {"start": v(1.44, -0.54) * mm, "end": v(1.43, -0.54) * mm});
            skLineSegment(sketch, "E1430", {"start": v(1.43, -0.54) * mm, "end": v(1.42, -0.54) * mm});
            skLineSegment(sketch, "E1431", {"start": v(1.42, -0.54) * mm, "end": v(1.4, -0.54) * mm});
            skLineSegment(sketch, "E1432", {"start": v(1.4, -0.54) * mm, "end": v(1.39, -0.54) * mm});
            skLineSegment(sketch, "E1433", {"start": v(1.39, -0.54) * mm, "end": v(1.37, -0.54) * mm});
            skLineSegment(sketch, "E1434", {"start": v(1.37, -0.54) * mm, "end": v(1.35, -0.54) * mm});
            skLineSegment(sketch, "E1435", {"start": v(1.35, -0.54) * mm, "end": v(1.34, -0.54) * mm});
            skLineSegment(sketch, "E1436", {"start": v(1.34, -0.54) * mm, "end": v(1.33, -0.54) * mm});
            skLineSegment(sketch, "E1437", {"start": v(1.33, -0.54) * mm, "end": v(1.33, -0.54) * mm});
            skLineSegment(sketch, "E1438", {"start": v(1.4, -0.62) * mm, "end": v(1.42, -0.62) * mm});
            skLineSegment(sketch, "E1439", {"start": v(1.42, -0.62) * mm, "end": v(1.4, -0.63) * mm});
            skLineSegment(sketch, "E1440", {"start": v(1.4, -0.63) * mm, "end": v(1.4, -0.63) * mm});
            skLineSegment(sketch, "E1441", {"start": v(1.4, -0.63) * mm, "end": v(1.4, -0.64) * mm});
            skLineSegment(sketch, "E1442", {"start": v(1.4, -0.64) * mm, "end": v(1.38, -0.65) * mm});
            skLineSegment(sketch, "E1443", {"start": v(1.38, -0.65) * mm, "end": v(1.37, -0.65) * mm});
            skLineSegment(sketch, "E1444", {"start": v(1.37, -0.65) * mm, "end": v(1.36, -0.66) * mm});
            skLineSegment(sketch, "E1445", {"start": v(1.36, -0.66) * mm, "end": v(1.35, -0.67) * mm});
            skLineSegment(sketch, "E1446", {"start": v(1.35, -0.67) * mm, "end": v(1.34, -0.67) * mm});
            skLineSegment(sketch, "E1447", {"start": v(1.34, -0.67) * mm, "end": v(1.33, -0.68) * mm});
            skLineSegment(sketch, "E1448", {"start": v(1.33, -0.68) * mm, "end": v(1.33, -0.68) * mm});
            skLineSegment(sketch, "E1449", {"start": v(1.33, -0.68) * mm, "end": v(1.32, -0.69) * mm});
            skLineSegment(sketch, "E1450", {"start": v(1.32, -0.69) * mm, "end": v(1.3, -0.7) * mm});
            skLineSegment(sketch, "E1451", {"start": v(1.3, -0.7) * mm, "end": v(1.28, -0.73) * mm});
            skLineSegment(sketch, "E1452", {"start": v(1.28, -0.73) * mm, "end": v(1.26, -0.75) * mm});
            skLineSegment(sketch, "E1453", {"start": v(1.26, -0.75) * mm, "end": v(1.24, -0.77) * mm});
            skLineSegment(sketch, "E1454", {"start": v(1.24, -0.77) * mm, "end": v(1.22, -0.8) * mm});
            skLineSegment(sketch, "E1455", {"start": v(1.22, -0.8) * mm, "end": v(1.2, -0.83) * mm});
            skLineSegment(sketch, "E1456", {"start": v(1.2, -0.83) * mm, "end": v(1.18, -0.85) * mm});
            skLineSegment(sketch, "E1457", {"start": v(1.18, -0.85) * mm, "end": v(1.17, -0.88) * mm});
            skLineSegment(sketch, "E1458", {"start": v(1.17, -0.88) * mm, "end": v(1.15, -0.91) * mm});
            skLineSegment(sketch, "E1459", {"start": v(1.15, -0.91) * mm, "end": v(1.14, -0.94) * mm});
            skLineSegment(sketch, "E1460", {"start": v(1.14, -0.94) * mm, "end": v(1.13, -0.97) * mm});
            skLineSegment(sketch, "E1461", {"start": v(1.13, -0.97) * mm, "end": v(1.12, -1) * mm});
            skLineSegment(sketch, "E1462", {"start": v(1.12, -1) * mm, "end": v(1.11, -1.04) * mm});
            skLineSegment(sketch, "E1463", {"start": v(1.11, -1.04) * mm, "end": v(1.1, -1.07) * mm});
            skLineSegment(sketch, "E1464", {"start": v(1.1, -1.07) * mm, "end": v(1.1, -1.1) * mm});
            skLineSegment(sketch, "E1465", {"start": v(1.1, -1.1) * mm, "end": v(1.1, -1.13) * mm});
            skLineSegment(sketch, "E1466", {"start": v(1.1, -1.13) * mm, "end": v(1.1, -1.13) * mm});
            skLineSegment(sketch, "E1467", {"start": v(1.1, -1.13) * mm, "end": v(1.1, -1.14) * mm});
            skLineSegment(sketch, "E1468", {"start": v(1.1, -1.14) * mm, "end": v(1.1, -1.15) * mm});
            skLineSegment(sketch, "E1469", {"start": v(1.1, -1.15) * mm, "end": v(1.1, -1.18) * mm});
            skLineSegment(sketch, "E1470", {"start": v(1.1, -1.18) * mm, "end": v(1.1, -1.2) * mm});
            skLineSegment(sketch, "E1471", {"start": v(1.1, -1.2) * mm, "end": v(1.1, -1.22) * mm});
            skLineSegment(sketch, "E1472", {"start": v(1.1, -1.22) * mm, "end": v(1.1, -1.22) * mm});
            skLineSegment(sketch, "E1473", {"start": v(1.1, -1.22) * mm, "end": v(1.1, -1.23) * mm});
            skLineSegment(sketch, "E1474", {"start": v(1.1, -1.23) * mm, "end": v(1.1, -1.26) * mm});
            skLineSegment(sketch, "E1475", {"start": v(1.1, -1.26) * mm, "end": v(1.1, -1.3) * mm});
            skLineSegment(sketch, "E1476", {"start": v(1.1, -1.3) * mm, "end": v(1.11, -1.32) * mm});
            skLineSegment(sketch, "E1477", {"start": v(1.11, -1.32) * mm, "end": v(1.12, -1.36) * mm});
            skLineSegment(sketch, "E1478", {"start": v(1.12, -1.36) * mm, "end": v(1.13, -1.39) * mm});
            skLineSegment(sketch, "E1479", {"start": v(1.13, -1.39) * mm, "end": v(1.14, -1.42) * mm});
            skLineSegment(sketch, "E1480", {"start": v(1.14, -1.42) * mm, "end": v(1.15, -1.45) * mm});
            skLineSegment(sketch, "E1481", {"start": v(1.15, -1.45) * mm, "end": v(1.17, -1.48) * mm});
            skLineSegment(sketch, "E1482", {"start": v(1.17, -1.48) * mm, "end": v(1.19, -1.5) * mm});
            skLineSegment(sketch, "E1483", {"start": v(1.19, -1.5) * mm, "end": v(1.2, -1.54) * mm});
            skLineSegment(sketch, "E1484", {"start": v(1.2, -1.54) * mm, "end": v(1.22, -1.56) * mm});
            skLineSegment(sketch, "E1485", {"start": v(1.22, -1.56) * mm, "end": v(1.24, -1.59) * mm});
            skLineSegment(sketch, "E1486", {"start": v(1.24, -1.59) * mm, "end": v(1.27, -1.61) * mm});
            skLineSegment(sketch, "E1487", {"start": v(1.27, -1.61) * mm, "end": v(1.29, -1.64) * mm});
            skLineSegment(sketch, "E1488", {"start": v(1.29, -1.64) * mm, "end": v(1.31, -1.66) * mm});
            skLineSegment(sketch, "E1489", {"start": v(1.31, -1.66) * mm, "end": v(1.33, -1.68) * mm});
            skLineSegment(sketch, "E1490", {"start": v(1.33, -1.68) * mm, "end": v(1.34, -1.68) * mm});
            skLineSegment(sketch, "E1491", {"start": v(1.34, -1.68) * mm, "end": v(1.34, -1.68) * mm});
            skLineSegment(sketch, "E1492", {"start": v(1.34, -1.68) * mm, "end": v(1.35, -1.69) * mm});
            skLineSegment(sketch, "E1493", {"start": v(1.35, -1.69) * mm, "end": v(1.36, -1.7) * mm});
            skLineSegment(sketch, "E1494", {"start": v(1.36, -1.7) * mm, "end": v(1.37, -1.7) * mm});
            skLineSegment(sketch, "E1495", {"start": v(1.37, -1.7) * mm, "end": v(1.38, -1.7) * mm});
            skLineSegment(sketch, "E1496", {"start": v(1.38, -1.7) * mm, "end": v(1.39, -1.71) * mm});
            skLineSegment(sketch, "E1497", {"start": v(1.39, -1.71) * mm, "end": v(1.4, -1.72) * mm});
            skLineSegment(sketch, "E1498", {"start": v(1.4, -1.72) * mm, "end": v(1.4, -1.73) * mm});
            skLineSegment(sketch, "E1499", {"start": v(1.4, -1.73) * mm, "end": v(1.4, -1.73) * mm});
            skLineSegment(sketch, "E1500", {"start": v(1.4, -1.73) * mm, "end": v(1.42, -1.73) * mm});
            skLineSegment(sketch, "E1501", {"start": v(1.42, -1.73) * mm, "end": v(1.4, -1.73) * mm});
            skLineSegment(sketch, "E1502", {"start": v(1.4, -1.73) * mm, "end": v(1.39, -1.73) * mm});
            skLineSegment(sketch, "E1503", {"start": v(1.39, -1.73) * mm, "end": v(1.38, -1.73) * mm});
            skLineSegment(sketch, "E1504", {"start": v(1.38, -1.73) * mm, "end": v(1.37, -1.73) * mm});
            skLineSegment(sketch, "E1505", {"start": v(1.37, -1.73) * mm, "end": v(1.35, -1.73) * mm});
            skLineSegment(sketch, "E1506", {"start": v(1.35, -1.73) * mm, "end": v(1.34, -1.73) * mm});
            skLineSegment(sketch, "E1507", {"start": v(1.34, -1.73) * mm, "end": v(1.33, -1.73) * mm});
            skLineSegment(sketch, "E1508", {"start": v(1.33, -1.73) * mm, "end": v(1.33, -1.73) * mm});
            skLineSegment(sketch, "E1509", {"start": v(1.33, -1.73) * mm, "end": v(1.32, -1.73) * mm});
            skLineSegment(sketch, "E1510", {"start": v(1.32, -1.73) * mm, "end": v(1.3, -1.73) * mm});
            skLineSegment(sketch, "E1511", {"start": v(1.3, -1.73) * mm, "end": v(1.27, -1.72) * mm});
            skLineSegment(sketch, "E1512", {"start": v(1.27, -1.72) * mm, "end": v(1.22, -1.71) * mm});
            skLineSegment(sketch, "E1513", {"start": v(1.22, -1.71) * mm, "end": v(1.17, -1.7) * mm});
            skLineSegment(sketch, "E1514", {"start": v(1.17, -1.7) * mm, "end": v(1.14, -1.68) * mm});
            skLineSegment(sketch, "E1515", {"start": v(1.14, -1.68) * mm, "end": v(1.12, -1.68) * mm});
            skLineSegment(sketch, "E1516", {"start": v(1.12, -1.68) * mm, "end": v(1.11, -1.67) * mm});
            skLineSegment(sketch, "E1517", {"start": v(1.11, -1.67) * mm, "end": v(1.09, -1.65) * mm});
            skLineSegment(sketch, "E1518", {"start": v(1.09, -1.65) * mm, "end": v(1.05, -1.63) * mm});
            skLineSegment(sketch, "E1519", {"start": v(1.05, -1.63) * mm, "end": v(1.02, -1.6) * mm});
            skLineSegment(sketch, "E1520", {"start": v(1.02, -1.6) * mm, "end": v(1, -1.58) * mm});
            skLineSegment(sketch, "E1521", {"start": v(1, -1.58) * mm, "end": v(0.98, -1.57) * mm});
            skLineSegment(sketch, "E1522", {"start": v(0.98, -1.57) * mm, "end": v(0.98, -1.56) * mm});
            skLineSegment(sketch, "E1523", {"start": v(0.98, -1.56) * mm, "end": v(0.95, -1.54) * mm});
            skLineSegment(sketch, "E1524", {"start": v(0.95, -1.54) * mm, "end": v(0.93, -1.51) * mm});
            skLineSegment(sketch, "E1525", {"start": v(0.93, -1.51) * mm, "end": v(0.9, -1.48) * mm});
            skLineSegment(sketch, "E1526", {"start": v(0.9, -1.48) * mm, "end": v(0.89, -1.44) * mm});
            skLineSegment(sketch, "E1527", {"start": v(0.89, -1.44) * mm, "end": v(0.87, -1.4) * mm});
            skLineSegment(sketch, "E1528", {"start": v(0.87, -1.4) * mm, "end": v(0.85, -1.37) * mm});
            skLineSegment(sketch, "E1529", {"start": v(0.85, -1.37) * mm, "end": v(0.84, -1.33) * mm});
            skLineSegment(sketch, "E1530", {"start": v(0.84, -1.33) * mm, "end": v(0.83, -1.3) * mm});
            skLineSegment(sketch, "E1531", {"start": v(0.83, -1.3) * mm, "end": v(0.83, -1.29) * mm});
            skLineSegment(sketch, "E1532", {"start": v(0.83, -1.29) * mm, "end": v(0.83, -1.28) * mm});
            skLineSegment(sketch, "E1533", {"start": v(0.83, -1.28) * mm, "end": v(0.83, -1.27) * mm});
            skLineSegment(sketch, "E1534", {"start": v(0.83, -1.27) * mm, "end": v(0.82, -1.26) * mm});
            skLineSegment(sketch, "E1535", {"start": v(0.82, -1.26) * mm, "end": v(0.82, -1.25) * mm});
            skLineSegment(sketch, "E1536", {"start": v(0.82, -1.25) * mm, "end": v(0.82, -1.24) * mm});
            skLineSegment(sketch, "E1537", {"start": v(0.82, -1.24) * mm, "end": v(0.82, -1.23) * mm});
            skLineSegment(sketch, "E1538", {"start": v(0.82, -1.23) * mm, "end": v(0.82, -1.21) * mm});
            skLineSegment(sketch, "E1539", {"start": v(0.82, -1.21) * mm, "end": v(0.82, -1.2) * mm});
            skLineSegment(sketch, "E1540", {"start": v(0.82, -1.2) * mm, "end": v(0.82, -1.18) * mm});
            skLineSegment(sketch, "E1541", {"start": v(0.82, -1.18) * mm, "end": v(0.82, -1.18) * mm});
            skLineSegment(sketch, "E1542", {"start": v(0.82, -1.18) * mm, "end": v(0.82, -1.17) * mm});
            skLineSegment(sketch, "E1543", {"start": v(0.82, -1.17) * mm, "end": v(0.82, -1.16) * mm});
            skLineSegment(sketch, "E1544", {"start": v(0.82, -1.16) * mm, "end": v(0.82, -1.15) * mm});
            skLineSegment(sketch, "E1545", {"start": v(0.82, -1.15) * mm, "end": v(0.82, -1.14) * mm});
            skLineSegment(sketch, "E1546", {"start": v(0.82, -1.14) * mm, "end": v(0.82, -1.14) * mm});
            skLineSegment(sketch, "E1547", {"start": v(0.82, -1.14) * mm, "end": v(0.82, -1.13) * mm});
            skLineSegment(sketch, "E1548", {"start": v(0.82, -1.13) * mm, "end": v(0.82, -1.12) * mm});
            skLineSegment(sketch, "E1549", {"start": v(0.82, -1.12) * mm, "end": v(0.82, -1.12) * mm});
            skLineSegment(sketch, "E1550", {"start": v(0.82, -1.12) * mm, "end": v(0.82, -1.11) * mm});
            skLineSegment(sketch, "E1551", {"start": v(0.82, -1.11) * mm, "end": v(0.82, -1.1) * mm});
            skLineSegment(sketch, "E1552", {"start": v(0.82, -1.1) * mm, "end": v(0.82, -1.1) * mm});
            skLineSegment(sketch, "E1553", {"start": v(0.82, -1.1) * mm, "end": v(0.83, -1.06) * mm});
            skLineSegment(sketch, "E1554", {"start": v(0.83, -1.06) * mm, "end": v(0.84, -1.02) * mm});
            skLineSegment(sketch, "E1555", {"start": v(0.84, -1.02) * mm, "end": v(0.86, -0.97) * mm});
            skLineSegment(sketch, "E1556", {"start": v(0.86, -0.97) * mm, "end": v(0.88, -0.93) * mm});
            skLineSegment(sketch, "E1557", {"start": v(0.88, -0.93) * mm, "end": v(0.9, -0.9) * mm});
            skLineSegment(sketch, "E1558", {"start": v(0.9, -0.9) * mm, "end": v(0.92, -0.85) * mm});
            skLineSegment(sketch, "E1559", {"start": v(0.92, -0.85) * mm, "end": v(0.95, -0.82) * mm});
            skLineSegment(sketch, "E1560", {"start": v(0.95, -0.82) * mm, "end": v(0.97, -0.8) * mm});
            skLineSegment(sketch, "E1561", {"start": v(0.97, -0.8) * mm, "end": v(0.98, -0.78) * mm});
            skLineSegment(sketch, "E1562", {"start": v(0.98, -0.78) * mm, "end": v(1, -0.78) * mm});
            skLineSegment(sketch, "E1563", {"start": v(1, -0.78) * mm, "end": v(1.02, -0.75) * mm});
            skLineSegment(sketch, "E1564", {"start": v(1.02, -0.75) * mm, "end": v(1.05, -0.72) * mm});
            skLineSegment(sketch, "E1565", {"start": v(1.05, -0.72) * mm, "end": v(1.1, -0.7) * mm});
            skLineSegment(sketch, "E1566", {"start": v(1.1, -0.7) * mm, "end": v(1.13, -0.68) * mm});
            skLineSegment(sketch, "E1567", {"start": v(1.13, -0.68) * mm, "end": v(1.17, -0.66) * mm});
            skLineSegment(sketch, "E1568", {"start": v(1.17, -0.66) * mm, "end": v(1.22, -0.64) * mm});
            skLineSegment(sketch, "E1569", {"start": v(1.22, -0.64) * mm, "end": v(1.26, -0.63) * mm});
            skLineSegment(sketch, "E1570", {"start": v(1.26, -0.63) * mm, "end": v(1.3, -0.63) * mm});
            skLineSegment(sketch, "E1571", {"start": v(1.3, -0.63) * mm, "end": v(1.31, -0.63) * mm});
            skLineSegment(sketch, "E1572", {"start": v(1.31, -0.63) * mm, "end": v(1.32, -0.63) * mm});
            skLineSegment(sketch, "E1573", {"start": v(1.32, -0.63) * mm, "end": v(1.33, -0.62) * mm});
            skLineSegment(sketch, "E1574", {"start": v(1.33, -0.62) * mm, "end": v(1.36, -0.62) * mm});
            skLineSegment(sketch, "E1575", {"start": v(1.36, -0.62) * mm, "end": v(1.39, -0.62) * mm});
            skLineSegment(sketch, "E1576", {"start": v(1.39, -0.62) * mm, "end": v(1.4, -0.62) * mm});
            skLineSegment(sketch, "E1577", {"start": v(1.4, -0.62) * mm, "end": v(1.4, -0.62) * mm});
            skSolve(sketch);
        }
        {
            var Q0;
            Q0=makeQuery(id+"F2.imprint","IMPRINT",FACE,{"disambiguationData":[TD([[makeQuery(id+"F2.imprint","IMPRINT",EDGE,{"derivedFrom":sQuery(id+"F2.wireOp",EDGE,"E1")}),-1.0]])]});
            var sketch = newSketch(context, id + "F6", { "sketchPlane" : qUnion([Q0])});
            skLineSegment(sketch, "E1578", {"start": v(-1.16, -0.54) * mm, "end": v(-1.17, -0.55) * mm});
            skLineSegment(sketch, "E1579", {"start": v(-1.17, -0.55) * mm, "end": v(-1.18, -0.57) * mm});
            skLineSegment(sketch, "E1580", {"start": v(-1.18, -0.57) * mm, "end": v(-1.2, -0.6) * mm});
            skLineSegment(sketch, "E1581", {"start": v(-1.2, -0.6) * mm, "end": v(-1.2, -0.62) * mm});
            skLineSegment(sketch, "E1582", {"start": v(-1.2, -0.62) * mm, "end": v(-1.21, -0.65) * mm});
            skLineSegment(sketch, "E1583", {"start": v(-1.21, -0.65) * mm, "end": v(-1.21, -0.67) * mm});
            skLineSegment(sketch, "E1584", {"start": v(-1.21, -0.67) * mm, "end": v(-1.21, -0.7) * mm});
            skLineSegment(sketch, "E1585", {"start": v(-1.21, -0.7) * mm, "end": v(-1.21, -0.73) * mm});
            skLineSegment(sketch, "E1586", {"start": v(-1.21, -0.73) * mm, "end": v(-1.2, -0.75) * mm});
            skLineSegment(sketch, "E1587", {"start": v(-1.2, -0.75) * mm, "end": v(-1.2, -0.78) * mm});
            skLineSegment(sketch, "E1588", {"start": v(-1.2, -0.78) * mm, "end": v(-1.2, -0.8) * mm});
            skLineSegment(sketch, "E1589", {"start": v(-1.2, -0.8) * mm, "end": v(-1.2, -0.82) * mm});
            skLineSegment(sketch, "E1590", {"start": v(-1.2, -0.82) * mm, "end": v(-1.19, -0.84) * mm});
            skLineSegment(sketch, "E1591", {"start": v(-1.19, -0.84) * mm, "end": v(-1.19, -0.86) * mm});
            skLineSegment(sketch, "E1592", {"start": v(-1.19, -0.86) * mm, "end": v(-1.19, -0.87) * mm});
            skLineSegment(sketch, "E1593", {"start": v(-1.19, -0.87) * mm, "end": v(-1.2, -0.88) * mm});
            skLineSegment(sketch, "E1594", {"start": v(-1.2, -0.88) * mm, "end": v(-1.2, -0.88) * mm});
            skLineSegment(sketch, "E1595", {"start": v(-1.2, -0.88) * mm, "end": v(-1.21, -0.87) * mm});
            skLineSegment(sketch, "E1596", {"start": v(-1.21, -0.87) * mm, "end": v(-1.22, -0.86) * mm});
            skLineSegment(sketch, "E1597", {"start": v(-1.22, -0.86) * mm, "end": v(-1.22, -0.85) * mm});
            skLineSegment(sketch, "E1598", {"start": v(-1.22, -0.85) * mm, "end": v(-1.23, -0.84) * mm});
            skLineSegment(sketch, "E1599", {"start": v(-1.23, -0.84) * mm, "end": v(-1.24, -0.83) * mm});
            skLineSegment(sketch, "E1600", {"start": v(-1.24, -0.83) * mm, "end": v(-1.25, -0.82) * mm});
            skLineSegment(sketch, "E1601", {"start": v(-1.25, -0.82) * mm, "end": v(-1.27, -0.8) * mm});
            skLineSegment(sketch, "E1602", {"start": v(-1.27, -0.8) * mm, "end": v(-1.28, -0.8) * mm});
            skLineSegment(sketch, "E1603", {"start": v(-1.28, -0.8) * mm, "end": v(-1.3, -0.8) * mm});
            skLineSegment(sketch, "E1604", {"start": v(-1.3, -0.8) * mm, "end": v(-1.3, -0.78) * mm});
            skLineSegment(sketch, "E1605", {"start": v(-1.3, -0.78) * mm, "end": v(-1.32, -0.78) * mm});
            skLineSegment(sketch, "E1606", {"start": v(-1.32, -0.78) * mm, "end": v(-1.34, -0.77) * mm});
            skLineSegment(sketch, "E1607", {"start": v(-1.34, -0.77) * mm, "end": v(-1.35, -0.77) * mm});
            skLineSegment(sketch, "E1608", {"start": v(-1.35, -0.77) * mm, "end": v(-1.37, -0.77) * mm});
            skLineSegment(sketch, "E1609", {"start": v(-1.37, -0.77) * mm, "end": v(-1.37, -0.77) * mm});
            skLineSegment(sketch, "E1610", {"start": v(-1.37, -0.77) * mm, "end": v(-1.36, -0.78) * mm});
            skLineSegment(sketch, "E1611", {"start": v(-1.36, -0.78) * mm, "end": v(-1.35, -0.8) * mm});
            skLineSegment(sketch, "E1612", {"start": v(-1.35, -0.8) * mm, "end": v(-1.33, -0.84) * mm});
            skLineSegment(sketch, "E1613", {"start": v(-1.33, -0.84) * mm, "end": v(-1.31, -0.87) * mm});
            skLineSegment(sketch, "E1614", {"start": v(-1.31, -0.87) * mm, "end": v(-1.3, -0.9) * mm});
            skLineSegment(sketch, "E1615", {"start": v(-1.3, -0.9) * mm, "end": v(-1.3, -0.92) * mm});
            skLineSegment(sketch, "E1616", {"start": v(-1.3, -0.92) * mm, "end": v(-1.3, -0.95) * mm});
            skLineSegment(sketch, "E1617", {"start": v(-1.3, -0.95) * mm, "end": v(-1.29, -0.97) * mm});
            skLineSegment(sketch, "E1618", {"start": v(-1.29, -0.97) * mm, "end": v(-1.29, -1) * mm});
            skLineSegment(sketch, "E1619", {"start": v(-1.29, -1) * mm, "end": v(-1.3, -1.01) * mm});
            skLineSegment(sketch, "E1620", {"start": v(-1.3, -1.01) * mm, "end": v(-1.3, -1.03) * mm});
            skLineSegment(sketch, "E1621", {"start": v(-1.3, -1.03) * mm, "end": v(-1.3, -1.04) * mm});
            skLineSegment(sketch, "E1622", {"start": v(-1.3, -1.04) * mm, "end": v(-1.3, -1.05) * mm});
            skLineSegment(sketch, "E1623", {"start": v(-1.3, -1.05) * mm, "end": v(-1.3, -1.06) * mm});
            skLineSegment(sketch, "E1624", {"start": v(-1.3, -1.06) * mm, "end": v(-1.3, -1.07) * mm});
            skLineSegment(sketch, "E1625", {"start": v(-1.3, -1.07) * mm, "end": v(-1.31, -1.07) * mm});
            skLineSegment(sketch, "E1626", {"start": v(-1.31, -1.07) * mm, "end": v(-1.31, -1.07) * mm});
            skLineSegment(sketch, "E1627", {"start": v(-1.31, -1.07) * mm, "end": v(-1.32, -1.07) * mm});
            skLineSegment(sketch, "E1628", {"start": v(-1.32, -1.07) * mm, "end": v(-1.33, -1.05) * mm});
            skLineSegment(sketch, "E1629", {"start": v(-1.33, -1.05) * mm, "end": v(-1.35, -1.04) * mm});
            skLineSegment(sketch, "E1630", {"start": v(-1.35, -1.04) * mm, "end": v(-1.36, -1.02) * mm});
            skLineSegment(sketch, "E1631", {"start": v(-1.36, -1.02) * mm, "end": v(-1.38, -1) * mm});
            skLineSegment(sketch, "E1632", {"start": v(-1.38, -1) * mm, "end": v(-1.4, -1) * mm});
            skLineSegment(sketch, "E1633", {"start": v(-1.4, -1) * mm, "end": v(-1.41, -0.99) * mm});
            skLineSegment(sketch, "E1634", {"start": v(-1.41, -0.99) * mm, "end": v(-1.43, -0.98) * mm});
            skLineSegment(sketch, "E1635", {"start": v(-1.43, -0.98) * mm, "end": v(-1.44, -0.98) * mm});
            skLineSegment(sketch, "E1636", {"start": v(-1.44, -0.98) * mm, "end": v(-1.45, -0.97) * mm});
            skLineSegment(sketch, "E1637", {"start": v(-1.45, -0.97) * mm, "end": v(-1.47, -0.97) * mm});
            skLineSegment(sketch, "E1638", {"start": v(-1.47, -0.97) * mm, "end": v(-1.48, -0.97) * mm});
            skLineSegment(sketch, "E1639", {"start": v(-1.48, -0.97) * mm, "end": v(-1.48, -0.97) * mm});
            skLineSegment(sketch, "E1640", {"start": v(-1.48, -0.97) * mm, "end": v(-1.49, -0.97) * mm});
            skLineSegment(sketch, "E1641", {"start": v(-1.49, -0.97) * mm, "end": v(-1.5, -0.97) * mm});
            skLineSegment(sketch, "E1642", {"start": v(-1.5, -0.97) * mm, "end": v(-1.5, -0.97) * mm});
            skLineSegment(sketch, "E1643", {"start": v(-1.5, -0.97) * mm, "end": v(-1.49, -0.98) * mm});
            skLineSegment(sketch, "E1644", {"start": v(-1.49, -0.98) * mm, "end": v(-1.49, -0.98) * mm});
            skLineSegment(sketch, "E1645", {"start": v(-1.49, -0.98) * mm, "end": v(-1.48, -0.98) * mm});
            skLineSegment(sketch, "E1646", {"start": v(-1.48, -0.98) * mm, "end": v(-1.47, -1) * mm});
            skLineSegment(sketch, "E1647", {"start": v(-1.47, -1) * mm, "end": v(-1.45, -1.01) * mm});
            skLineSegment(sketch, "E1648", {"start": v(-1.45, -1.01) * mm, "end": v(-1.44, -1.03) * mm});
            skLineSegment(sketch, "E1649", {"start": v(-1.44, -1.03) * mm, "end": v(-1.43, -1.05) * mm});
            skLineSegment(sketch, "E1650", {"start": v(-1.43, -1.05) * mm, "end": v(-1.42, -1.07) * mm});
            skLineSegment(sketch, "E1651", {"start": v(-1.42, -1.07) * mm, "end": v(-1.42, -1.1) * mm});
            skLineSegment(sketch, "E1652", {"start": v(-1.42, -1.1) * mm, "end": v(-1.41, -1.12) * mm});
            skLineSegment(sketch, "E1653", {"start": v(-1.41, -1.12) * mm, "end": v(-1.41, -1.14) * mm});
            skLineSegment(sketch, "E1654", {"start": v(-1.41, -1.14) * mm, "end": v(-1.41, -1.16) * mm});
            skLineSegment(sketch, "E1655", {"start": v(-1.41, -1.16) * mm, "end": v(-1.4, -1.18) * mm});
            skLineSegment(sketch, "E1656", {"start": v(-1.4, -1.18) * mm, "end": v(-1.41, -1.2) * mm});
            skLineSegment(sketch, "E1657", {"start": v(-1.41, -1.2) * mm, "end": v(-1.41, -1.22) * mm});
            skLineSegment(sketch, "E1658", {"start": v(-1.41, -1.22) * mm, "end": v(-1.41, -1.23) * mm});
            skLineSegment(sketch, "E1659", {"start": v(-1.41, -1.23) * mm, "end": v(-1.41, -1.24) * mm});
            skLineSegment(sketch, "E1660", {"start": v(-1.41, -1.24) * mm, "end": v(-1.41, -1.25) * mm});
            skLineSegment(sketch, "E1661", {"start": v(-1.41, -1.25) * mm, "end": v(-1.41, -1.25) * mm});
            skLineSegment(sketch, "E1662", {"start": v(-1.41, -1.25) * mm, "end": v(-1.42, -1.25) * mm});
            skLineSegment(sketch, "E1663", {"start": v(-1.42, -1.25) * mm, "end": v(-1.42, -1.25) * mm});
            skLineSegment(sketch, "E1664", {"start": v(-1.42, -1.25) * mm, "end": v(-1.43, -1.24) * mm});
            skLineSegment(sketch, "E1665", {"start": v(-1.43, -1.24) * mm, "end": v(-1.43, -1.24) * mm});
            skLineSegment(sketch, "E1666", {"start": v(-1.43, -1.24) * mm, "end": v(-1.44, -1.23) * mm});
            skLineSegment(sketch, "E1667", {"start": v(-1.44, -1.23) * mm, "end": v(-1.45, -1.22) * mm});
            skLineSegment(sketch, "E1668", {"start": v(-1.45, -1.22) * mm, "end": v(-1.46, -1.21) * mm});
            skLineSegment(sketch, "E1669", {"start": v(-1.46, -1.21) * mm, "end": v(-1.48, -1.2) * mm});
            skLineSegment(sketch, "E1670", {"start": v(-1.48, -1.2) * mm, "end": v(-1.5, -1.2) * mm});
            skLineSegment(sketch, "E1671", {"start": v(-1.5, -1.2) * mm, "end": v(-1.5, -1.2) * mm});
            skLineSegment(sketch, "E1672", {"start": v(-1.5, -1.2) * mm, "end": v(-1.52, -1.2) * mm});
            skLineSegment(sketch, "E1673", {"start": v(-1.52, -1.2) * mm, "end": v(-1.53, -1.19) * mm});
            skLineSegment(sketch, "E1674", {"start": v(-1.53, -1.19) * mm, "end": v(-1.54, -1.19) * mm});
            skLineSegment(sketch, "E1675", {"start": v(-1.54, -1.19) * mm, "end": v(-1.56, -1.2) * mm});
            skLineSegment(sketch, "E1676", {"start": v(-1.56, -1.2) * mm, "end": v(-1.57, -1.2) * mm});
            skLineSegment(sketch, "E1677", {"start": v(-1.57, -1.2) * mm, "end": v(-1.58, -1.2) * mm});
            skLineSegment(sketch, "E1678", {"start": v(-1.58, -1.2) * mm, "end": v(-1.58, -1.2) * mm});
            skLineSegment(sketch, "E1679", {"start": v(-1.58, -1.2) * mm, "end": v(-1.57, -1.2) * mm});
            skLineSegment(sketch, "E1680", {"start": v(-1.57, -1.2) * mm, "end": v(-1.55, -1.22) * mm});
            skLineSegment(sketch, "E1681", {"start": v(-1.55, -1.22) * mm, "end": v(-1.53, -1.23) * mm});
            skLineSegment(sketch, "E1682", {"start": v(-1.53, -1.23) * mm, "end": v(-1.52, -1.25) * mm});
            skLineSegment(sketch, "E1683", {"start": v(-1.52, -1.25) * mm, "end": v(-1.5, -1.26) * mm});
            skLineSegment(sketch, "E1684", {"start": v(-1.5, -1.26) * mm, "end": v(-1.5, -1.27) * mm});
            skLineSegment(sketch, "E1685", {"start": v(-1.5, -1.27) * mm, "end": v(-1.5, -1.29) * mm});
            skLineSegment(sketch, "E1686", {"start": v(-1.5, -1.29) * mm, "end": v(-1.49, -1.3) * mm});
            skLineSegment(sketch, "E1687", {"start": v(-1.49, -1.3) * mm, "end": v(-1.49, -1.32) * mm});
            skLineSegment(sketch, "E1688", {"start": v(-1.49, -1.32) * mm, "end": v(-1.49, -1.34) * mm});
            skLineSegment(sketch, "E1689", {"start": v(-1.49, -1.34) * mm, "end": v(-1.49, -1.35) * mm});
            skLineSegment(sketch, "E1690", {"start": v(-1.49, -1.35) * mm, "end": v(-1.49, -1.37) * mm});
            skLineSegment(sketch, "E1691", {"start": v(-1.49, -1.37) * mm, "end": v(-1.5, -1.39) * mm});
            skLineSegment(sketch, "E1692", {"start": v(-1.5, -1.39) * mm, "end": v(-1.5, -1.4) * mm});
            skLineSegment(sketch, "E1693", {"start": v(-1.5, -1.4) * mm, "end": v(-1.5, -1.42) * mm});
            skLineSegment(sketch, "E1694", {"start": v(-1.5, -1.42) * mm, "end": v(-1.5, -1.44) * mm});
            skLineSegment(sketch, "E1695", {"start": v(-1.5, -1.44) * mm, "end": v(-1.5, -1.46) * mm});
            skLineSegment(sketch, "E1696", {"start": v(-1.5, -1.46) * mm, "end": v(-1.5, -1.46) * mm});
            skLineSegment(sketch, "E1697", {"start": v(-1.5, -1.46) * mm, "end": v(-1.5, -1.47) * mm});
            skLineSegment(sketch, "E1698", {"start": v(-1.5, -1.47) * mm, "end": v(-1.5, -1.5) * mm});
            skLineSegment(sketch, "E1699", {"start": v(-1.5, -1.5) * mm, "end": v(-1.5, -1.53) * mm});
            skLineSegment(sketch, "E1700", {"start": v(-1.5, -1.53) * mm, "end": v(-1.5, -1.56) * mm});
            skLineSegment(sketch, "E1701", {"start": v(-1.5, -1.56) * mm, "end": v(-1.48, -1.59) * mm});
            skLineSegment(sketch, "E1702", {"start": v(-1.48, -1.59) * mm, "end": v(-1.47, -1.62) * mm});
            skLineSegment(sketch, "E1703", {"start": v(-1.47, -1.62) * mm, "end": v(-1.46, -1.64) * mm});
            skLineSegment(sketch, "E1704", {"start": v(-1.46, -1.64) * mm, "end": v(-1.45, -1.66) * mm});
            skLineSegment(sketch, "E1705", {"start": v(-1.45, -1.66) * mm, "end": v(-1.44, -1.68) * mm});
            skLineSegment(sketch, "E1706", {"start": v(-1.44, -1.68) * mm, "end": v(-1.43, -1.7) * mm});
            skLineSegment(sketch, "E1707", {"start": v(-1.43, -1.7) * mm, "end": v(-1.41, -1.71) * mm});
            skLineSegment(sketch, "E1708", {"start": v(-1.41, -1.71) * mm, "end": v(-1.4, -1.73) * mm});
            skLineSegment(sketch, "E1709", {"start": v(-1.4, -1.73) * mm, "end": v(-1.39, -1.74) * mm});
            skLineSegment(sketch, "E1710", {"start": v(-1.39, -1.74) * mm, "end": v(-1.38, -1.75) * mm});
            skLineSegment(sketch, "E1711", {"start": v(-1.38, -1.75) * mm, "end": v(-1.37, -1.76) * mm});
            skLineSegment(sketch, "E1712", {"start": v(-1.37, -1.76) * mm, "end": v(-1.36, -1.76) * mm});
            skLineSegment(sketch, "E1713", {"start": v(-1.36, -1.76) * mm, "end": v(-1.36, -1.76) * mm});
            skLineSegment(sketch, "E1714", {"start": v(-1.36, -1.76) * mm, "end": v(-1.42, -1.76) * mm});
            skLineSegment(sketch, "E1715", {"start": v(-1.42, -1.76) * mm, "end": v(-1.42, -1.81) * mm});
            skLineSegment(sketch, "E1716", {"start": v(-1.42, -1.81) * mm, "end": v(-0.85, -1.81) * mm});
            skLineSegment(sketch, "E1717", {"start": v(-0.85, -1.81) * mm, "end": v(-0.85, -1.76) * mm});
            skLineSegment(sketch, "E1718", {"start": v(-0.85, -1.76) * mm, "end": v(-0.92, -1.76) * mm});
            skLineSegment(sketch, "E1719", {"start": v(-0.92, -1.76) * mm, "end": v(-0.92, -1.76) * mm});
            skLineSegment(sketch, "E1720", {"start": v(-0.92, -1.76) * mm, "end": v(-0.91, -1.76) * mm});
            skLineSegment(sketch, "E1721", {"start": v(-0.91, -1.76) * mm, "end": v(-0.9, -1.75) * mm});
            skLineSegment(sketch, "E1722", {"start": v(-0.9, -1.75) * mm, "end": v(-0.88, -1.75) * mm});
            skLineSegment(sketch, "E1723", {"start": v(-0.88, -1.75) * mm, "end": v(-0.87, -1.74) * mm});
            skLineSegment(sketch, "E1724", {"start": v(-0.87, -1.74) * mm, "end": v(-0.85, -1.72) * mm});
            skLineSegment(sketch, "E1725", {"start": v(-0.85, -1.72) * mm, "end": v(-0.83, -1.71) * mm});
            skLineSegment(sketch, "E1726", {"start": v(-0.83, -1.71) * mm, "end": v(-0.81, -1.7) * mm});
            skLineSegment(sketch, "E1727", {"start": v(-0.81, -1.7) * mm, "end": v(-0.8, -1.68) * mm});
            skLineSegment(sketch, "E1728", {"start": v(-0.8, -1.68) * mm, "end": v(-0.78, -1.66) * mm});
            skLineSegment(sketch, "E1729", {"start": v(-0.78, -1.66) * mm, "end": v(-0.76, -1.63) * mm});
            skLineSegment(sketch, "E1730", {"start": v(-0.76, -1.63) * mm, "end": v(-0.74, -1.6) * mm});
            skLineSegment(sketch, "E1731", {"start": v(-0.74, -1.6) * mm, "end": v(-0.73, -1.58) * mm});
            skLineSegment(sketch, "E1732", {"start": v(-0.73, -1.58) * mm, "end": v(-0.71, -1.55) * mm});
            skLineSegment(sketch, "E1733", {"start": v(-0.71, -1.55) * mm, "end": v(-0.7, -1.52) * mm});
            skLineSegment(sketch, "E1734", {"start": v(-0.7, -1.52) * mm, "end": v(-0.7, -1.48) * mm});
            skLineSegment(sketch, "E1735", {"start": v(-0.7, -1.48) * mm, "end": v(-0.7, -1.45) * mm});
            skLineSegment(sketch, "E1736", {"start": v(-0.7, -1.45) * mm, "end": v(-0.7, -1.44) * mm});
            skLineSegment(sketch, "E1737", {"start": v(-0.7, -1.44) * mm, "end": v(-0.7, -1.44) * mm});
            skLineSegment(sketch, "E1738", {"start": v(-0.7, -1.44) * mm, "end": v(-0.7, -1.43) * mm});
            skLineSegment(sketch, "E1739", {"start": v(-0.7, -1.43) * mm, "end": v(-0.7, -1.42) * mm});
            skLineSegment(sketch, "E1740", {"start": v(-0.7, -1.42) * mm, "end": v(-0.7, -1.41) * mm});
            skLineSegment(sketch, "E1741", {"start": v(-0.7, -1.41) * mm, "end": v(-0.7, -1.4) * mm});
            skLineSegment(sketch, "E1742", {"start": v(-0.7, -1.4) * mm, "end": v(-0.7, -1.39) * mm});
            skLineSegment(sketch, "E1743", {"start": v(-0.7, -1.39) * mm, "end": v(-0.7, -1.37) * mm});
            skLineSegment(sketch, "E1744", {"start": v(-0.7, -1.37) * mm, "end": v(-0.7, -1.36) * mm});
            skLineSegment(sketch, "E1745", {"start": v(-0.7, -1.36) * mm, "end": v(-0.7, -1.34) * mm});
            skLineSegment(sketch, "E1746", {"start": v(-0.7, -1.34) * mm, "end": v(-0.7, -1.33) * mm});
            skLineSegment(sketch, "E1747", {"start": v(-0.7, -1.33) * mm, "end": v(-0.7, -1.32) * mm});
            skLineSegment(sketch, "E1748", {"start": v(-0.7, -1.32) * mm, "end": v(-0.7, -1.3) * mm});
            skLineSegment(sketch, "E1749", {"start": v(-0.7, -1.3) * mm, "end": v(-0.71, -1.29) * mm});
            skLineSegment(sketch, "E1750", {"start": v(-0.71, -1.29) * mm, "end": v(-0.72, -1.28) * mm});
            skLineSegment(sketch, "E1751", {"start": v(-0.72, -1.28) * mm, "end": v(-0.73, -1.27) * mm});
            skLineSegment(sketch, "E1752", {"start": v(-0.73, -1.27) * mm, "end": v(-0.73, -1.27) * mm});
            skLineSegment(sketch, "E1753", {"start": v(-0.73, -1.27) * mm, "end": v(-0.73, -1.28) * mm});
            skLineSegment(sketch, "E1754", {"start": v(-0.73, -1.28) * mm, "end": v(-0.74, -1.3) * mm});
            skLineSegment(sketch, "E1755", {"start": v(-0.74, -1.3) * mm, "end": v(-0.75, -1.3) * mm});
            skLineSegment(sketch, "E1756", {"start": v(-0.75, -1.3) * mm, "end": v(-0.75, -1.3) * mm});
            skLineSegment(sketch, "E1757", {"start": v(-0.75, -1.3) * mm, "end": v(-0.76, -1.31) * mm});
            skLineSegment(sketch, "E1758", {"start": v(-0.76, -1.31) * mm, "end": v(-0.76, -1.32) * mm});
            skLineSegment(sketch, "E1759", {"start": v(-0.76, -1.32) * mm, "end": v(-0.77, -1.32) * mm});
            skLineSegment(sketch, "E1760", {"start": v(-0.77, -1.32) * mm, "end": v(-0.77, -1.32) * mm});
            skLineSegment(sketch, "E1761", {"start": v(-0.77, -1.32) * mm, "end": v(-0.77, -1.31) * mm});
            skLineSegment(sketch, "E1762", {"start": v(-0.77, -1.31) * mm, "end": v(-0.77, -1.3) * mm});
            skLineSegment(sketch, "E1763", {"start": v(-0.77, -1.3) * mm, "end": v(-0.77, -1.3) * mm});
            skLineSegment(sketch, "E1764", {"start": v(-0.77, -1.3) * mm, "end": v(-0.77, -1.28) * mm});
            skLineSegment(sketch, "E1765", {"start": v(-0.77, -1.28) * mm, "end": v(-0.76, -1.27) * mm});
            skLineSegment(sketch, "E1766", {"start": v(-0.76, -1.27) * mm, "end": v(-0.76, -1.26) * mm});
            skLineSegment(sketch, "E1767", {"start": v(-0.76, -1.26) * mm, "end": v(-0.76, -1.25) * mm});
            skLineSegment(sketch, "E1768", {"start": v(-0.76, -1.25) * mm, "end": v(-0.76, -1.24) * mm});
            skLineSegment(sketch, "E1769", {"start": v(-0.76, -1.24) * mm, "end": v(-0.75, -1.22) * mm});
            skLineSegment(sketch, "E1770", {"start": v(-0.75, -1.22) * mm, "end": v(-0.75, -1.21) * mm});
            skLineSegment(sketch, "E1771", {"start": v(-0.75, -1.21) * mm, "end": v(-0.75, -1.2) * mm});
            skLineSegment(sketch, "E1772", {"start": v(-0.75, -1.2) * mm, "end": v(-0.74, -1.19) * mm});
            skLineSegment(sketch, "E1773", {"start": v(-0.74, -1.19) * mm, "end": v(-0.74, -1.18) * mm});
            skLineSegment(sketch, "E1774", {"start": v(-0.74, -1.18) * mm, "end": v(-0.74, -1.17) * mm});
            skLineSegment(sketch, "E1775", {"start": v(-0.74, -1.17) * mm, "end": v(-0.74, -1.17) * mm});
            skLineSegment(sketch, "E1776", {"start": v(-0.74, -1.17) * mm, "end": v(-0.74, -1.16) * mm});
            skLineSegment(sketch, "E1777", {"start": v(-0.74, -1.16) * mm, "end": v(-0.75, -1.13) * mm});
            skLineSegment(sketch, "E1778", {"start": v(-0.75, -1.13) * mm, "end": v(-0.75, -1.1) * mm});
            skLineSegment(sketch, "E1779", {"start": v(-0.75, -1.1) * mm, "end": v(-0.77, -1.08) * mm});
            skLineSegment(sketch, "E1780", {"start": v(-0.77, -1.08) * mm, "end": v(-0.78, -1.06) * mm});
            skLineSegment(sketch, "E1781", {"start": v(-0.78, -1.06) * mm, "end": v(-0.8, -1.04) * mm});
            skLineSegment(sketch, "E1782", {"start": v(-0.8, -1.04) * mm, "end": v(-0.8, -1.03) * mm});
            skLineSegment(sketch, "E1783", {"start": v(-0.8, -1.03) * mm, "end": v(-0.81, -1.03) * mm});
            skLineSegment(sketch, "E1784", {"start": v(-0.81, -1.03) * mm, "end": v(-0.82, -1.02) * mm});
            skLineSegment(sketch, "E1785", {"start": v(-0.82, -1.02) * mm, "end": v(-0.82, -1.03) * mm});
            skLineSegment(sketch, "E1786", {"start": v(-0.82, -1.03) * mm, "end": v(-0.82, -1.03) * mm});
            skLineSegment(sketch, "E1787", {"start": v(-0.82, -1.03) * mm, "end": v(-0.82, -1.04) * mm});
            skLineSegment(sketch, "E1788", {"start": v(-0.82, -1.04) * mm, "end": v(-0.82, -1.05) * mm});
            skLineSegment(sketch, "E1789", {"start": v(-0.82, -1.05) * mm, "end": v(-0.82, -1.06) * mm});
            skLineSegment(sketch, "E1790", {"start": v(-0.82, -1.06) * mm, "end": v(-0.82, -1.07) * mm});
            skLineSegment(sketch, "E1791", {"start": v(-0.82, -1.07) * mm, "end": v(-0.82, -1.09) * mm});
            skLineSegment(sketch, "E1792", {"start": v(-0.82, -1.09) * mm, "end": v(-0.82, -1.1) * mm});
            skLineSegment(sketch, "E1793", {"start": v(-0.82, -1.1) * mm, "end": v(-0.82, -1.11) * mm});
            skLineSegment(sketch, "E1794", {"start": v(-0.82, -1.11) * mm, "end": v(-0.83, -1.13) * mm});
            skLineSegment(sketch, "E1795", {"start": v(-0.83, -1.13) * mm, "end": v(-0.83, -1.14) * mm});
            skLineSegment(sketch, "E1796", {"start": v(-0.83, -1.14) * mm, "end": v(-0.84, -1.15) * mm});
            skLineSegment(sketch, "E1797", {"start": v(-0.84, -1.15) * mm, "end": v(-0.84, -1.16) * mm});
            skLineSegment(sketch, "E1798", {"start": v(-0.84, -1.16) * mm, "end": v(-0.85, -1.17) * mm});
            skLineSegment(sketch, "E1799", {"start": v(-0.85, -1.17) * mm, "end": v(-0.86, -1.18) * mm});
            skLineSegment(sketch, "E1800", {"start": v(-0.86, -1.18) * mm, "end": v(-0.87, -1.18) * mm});
            skLineSegment(sketch, "E1801", {"start": v(-0.87, -1.18) * mm, "end": v(-0.87, -1.18) * mm});
            skLineSegment(sketch, "E1802", {"start": v(-0.87, -1.18) * mm, "end": v(-0.87, -1.17) * mm});
            skLineSegment(sketch, "E1803", {"start": v(-0.87, -1.17) * mm, "end": v(-0.87, -1.16) * mm});
            skLineSegment(sketch, "E1804", {"start": v(-0.87, -1.16) * mm, "end": v(-0.87, -1.14) * mm});
            skLineSegment(sketch, "E1805", {"start": v(-0.87, -1.14) * mm, "end": v(-0.87, -1.11) * mm});
            skLineSegment(sketch, "E1806", {"start": v(-0.87, -1.11) * mm, "end": v(-0.87, -1.09) * mm});
            skLineSegment(sketch, "E1807", {"start": v(-0.87, -1.09) * mm, "end": v(-0.87, -1.06) * mm});
            skLineSegment(sketch, "E1808", {"start": v(-0.87, -1.06) * mm, "end": v(-0.87, -1.03) * mm});
            skLineSegment(sketch, "E1809", {"start": v(-0.87, -1.03) * mm, "end": v(-0.87, -1) * mm});
            skLineSegment(sketch, "E1810", {"start": v(-0.87, -1) * mm, "end": v(-0.88, -0.96) * mm});
            skLineSegment(sketch, "E1811", {"start": v(-0.88, -0.96) * mm, "end": v(-0.89, -0.93) * mm});
            skLineSegment(sketch, "E1812", {"start": v(-0.89, -0.93) * mm, "end": v(-0.9, -0.9) * mm});
            skLineSegment(sketch, "E1813", {"start": v(-0.9, -0.9) * mm, "end": v(-0.91, -0.87) * mm});
            skLineSegment(sketch, "E1814", {"start": v(-0.91, -0.87) * mm, "end": v(-0.93, -0.85) * mm});
            skLineSegment(sketch, "E1815", {"start": v(-0.93, -0.85) * mm, "end": v(-0.95, -0.82) * mm});
            skLineSegment(sketch, "E1816", {"start": v(-0.95, -0.82) * mm, "end": v(-0.98, -0.8) * mm});
            skLineSegment(sketch, "E1817", {"start": v(-0.98, -0.8) * mm, "end": v(-1, -0.8) * mm});
            skLineSegment(sketch, "E1818", {"start": v(-1, -0.8) * mm, "end": v(-1.01, -0.8) * mm});
            skLineSegment(sketch, "E1819", {"start": v(-1.01, -0.8) * mm, "end": v(-1.01, -0.8) * mm});
            skLineSegment(sketch, "E1820", {"start": v(-1.01, -0.8) * mm, "end": v(-1, -0.83) * mm});
            skLineSegment(sketch, "E1821", {"start": v(-1, -0.83) * mm, "end": v(-0.99, -0.85) * mm});
            skLineSegment(sketch, "E1822", {"start": v(-0.99, -0.85) * mm, "end": v(-0.98, -0.88) * mm});
            skLineSegment(sketch, "E1823", {"start": v(-0.98, -0.88) * mm, "end": v(-0.98, -0.9) * mm});
            skLineSegment(sketch, "E1824", {"start": v(-0.98, -0.9) * mm, "end": v(-0.98, -0.91) * mm});
            skLineSegment(sketch, "E1825", {"start": v(-0.98, -0.91) * mm, "end": v(-0.98, -0.92) * mm});
            skLineSegment(sketch, "E1826", {"start": v(-0.98, -0.92) * mm, "end": v(-0.98, -0.93) * mm});
            skLineSegment(sketch, "E1827", {"start": v(-0.98, -0.93) * mm, "end": v(-0.98, -0.93) * mm});
            skLineSegment(sketch, "E1828", {"start": v(-0.98, -0.93) * mm, "end": v(-0.98, -0.94) * mm});
            skLineSegment(sketch, "E1829", {"start": v(-0.98, -0.94) * mm, "end": v(-0.98, -0.94) * mm});
            skLineSegment(sketch, "E1830", {"start": v(-0.98, -0.94) * mm, "end": v(-0.98, -0.95) * mm});
            skLineSegment(sketch, "E1831", {"start": v(-0.98, -0.95) * mm, "end": v(-0.98, -0.96) * mm});
            skLineSegment(sketch, "E1832", {"start": v(-0.98, -0.96) * mm, "end": v(-0.98, -0.96) * mm});
            skLineSegment(sketch, "E1833", {"start": v(-0.98, -0.96) * mm, "end": v(-0.98, -0.97) * mm});
            skLineSegment(sketch, "E1834", {"start": v(-0.98, -0.97) * mm, "end": v(-0.98, -0.97) * mm});
            skLineSegment(sketch, "E1835", {"start": v(-0.98, -0.97) * mm, "end": v(-0.98, -0.96) * mm});
            skLineSegment(sketch, "E1836", {"start": v(-0.98, -0.96) * mm, "end": v(-0.99, -0.95) * mm});
            skLineSegment(sketch, "E1837", {"start": v(-0.99, -0.95) * mm, "end": v(-1, -0.93) * mm});
            skLineSegment(sketch, "E1838", {"start": v(-1, -0.93) * mm, "end": v(-1, -0.91) * mm});
            skLineSegment(sketch, "E1839", {"start": v(-1, -0.91) * mm, "end": v(-1, -0.9) * mm});
            skLineSegment(sketch, "E1840", {"start": v(-1, -0.9) * mm, "end": v(-1.01, -0.88) * mm});
            skLineSegment(sketch, "E1841", {"start": v(-1.01, -0.88) * mm, "end": v(-1.02, -0.86) * mm});
            skLineSegment(sketch, "E1842", {"start": v(-1.02, -0.86) * mm, "end": v(-1.03, -0.85) * mm});
            skLineSegment(sketch, "E1843", {"start": v(-1.03, -0.85) * mm, "end": v(-1.04, -0.83) * mm});
            skLineSegment(sketch, "E1844", {"start": v(-1.04, -0.83) * mm, "end": v(-1.05, -0.82) * mm});
            skLineSegment(sketch, "E1845", {"start": v(-1.05, -0.82) * mm, "end": v(-1.06, -0.8) * mm});
            skLineSegment(sketch, "E1846", {"start": v(-1.06, -0.8) * mm, "end": v(-1.06, -0.8) * mm});
            skLineSegment(sketch, "E1847", {"start": v(-1.06, -0.8) * mm, "end": v(-1.07, -0.8) * mm});
            skLineSegment(sketch, "E1848", {"start": v(-1.07, -0.8) * mm, "end": v(-1.08, -0.78) * mm});
            skLineSegment(sketch, "E1849", {"start": v(-1.08, -0.78) * mm, "end": v(-1.08, -0.78) * mm});
            skLineSegment(sketch, "E1850", {"start": v(-1.08, -0.78) * mm, "end": v(-1.08, -0.77) * mm});
            skLineSegment(sketch, "E1851", {"start": v(-1.08, -0.77) * mm, "end": v(-1.08, -0.77) * mm});
            skLineSegment(sketch, "E1852", {"start": v(-1.08, -0.77) * mm, "end": v(-1.09, -0.77) * mm});
            skLineSegment(sketch, "E1853", {"start": v(-1.09, -0.77) * mm, "end": v(-1.09, -0.77) * mm});
            skLineSegment(sketch, "E1854", {"start": v(-1.09, -0.77) * mm, "end": v(-1.1, -0.76) * mm});
            skLineSegment(sketch, "E1855", {"start": v(-1.1, -0.76) * mm, "end": v(-1.1, -0.76) * mm});
            skLineSegment(sketch, "E1856", {"start": v(-1.1, -0.76) * mm, "end": v(-1.1, -0.75) * mm});
            skLineSegment(sketch, "E1857", {"start": v(-1.1, -0.75) * mm, "end": v(-1.1, -0.74) * mm});
            skLineSegment(sketch, "E1858", {"start": v(-1.1, -0.74) * mm, "end": v(-1.11, -0.73) * mm});
            skLineSegment(sketch, "E1859", {"start": v(-1.11, -0.73) * mm, "end": v(-1.12, -0.72) * mm});
            skLineSegment(sketch, "E1860", {"start": v(-1.12, -0.72) * mm, "end": v(-1.12, -0.7) * mm});
            skLineSegment(sketch, "E1861", {"start": v(-1.12, -0.7) * mm, "end": v(-1.13, -0.68) * mm});
            skLineSegment(sketch, "E1862", {"start": v(-1.13, -0.68) * mm, "end": v(-1.14, -0.66) * mm});
            skLineSegment(sketch, "E1863", {"start": v(-1.14, -0.66) * mm, "end": v(-1.14, -0.63) * mm});
            skLineSegment(sketch, "E1864", {"start": v(-1.14, -0.63) * mm, "end": v(-1.15, -0.6) * mm});
            skLineSegment(sketch, "E1865", {"start": v(-1.15, -0.6) * mm, "end": v(-1.16, -0.57) * mm});
            skLineSegment(sketch, "E1866", {"start": v(-1.16, -0.57) * mm, "end": v(-1.16, -0.55) * mm});
            skLineSegment(sketch, "E1867", {"start": v(-1.16, -0.55) * mm, "end": v(-1.16, -0.54) * mm});
            skSolve(sketch);
        }
        {
            var Q0;
            Q0=makeQuery(id+"F2.imprint","IMPRINT",FACE,{"disambiguationData":[TD([[makeQuery(id+"F2.imprint","IMPRINT",EDGE,{"derivedFrom":sQuery(id+"F2.wireOp",EDGE,"E154")}),1.0]])]});
            var Q1;
            Q1=makeQuery(id+"F2.imprint","IMPRINT",FACE,{"disambiguationData":[TD([[makeQuery(id+"F2.imprint","IMPRINT",EDGE,{"derivedFrom":sQuery(id+"F2.wireOp",EDGE,"E72")}),1.0]])]});
            var Q2;
            Q2=makeQuery(id+"F2.imprint","IMPRINT",FACE,{"disambiguationData":[TD([[makeQuery(id+"F2.imprint","IMPRINT",EDGE,{"derivedFrom":sQuery(id+"F2.wireOp",EDGE,"E98")}),1.0]])]});
            var Q3;
            Q3=makeQuery(id+"F2.imprint","IMPRINT",FACE,{"disambiguationData":[TD([[makeQuery(id+"F2.imprint","IMPRINT",EDGE,{"derivedFrom":sQuery(id+"F2.wireOp",EDGE,"E122")}),1.0]])]});
            var Q4;
            Q4=makeQuery(id+"F2.imprint","IMPRINT",FACE,{"disambiguationData":[TD([[makeQuery(id+"F2.imprint","IMPRINT",EDGE,{"derivedFrom":sQuery(id+"F2.wireOp",EDGE,"E50")}),1.0]])]});
            var Q5;
            Q5=makeQuery(id+"F2.imprint","IMPRINT",FACE,{"disambiguationData":[TD([[makeQuery(id+"F2.imprint","IMPRINT",EDGE,{"derivedFrom":sQuery(id+"F2.wireOp",EDGE,"E1")}),1.0]])]});
            var Q6;
            Q6=makeQuery(id+"F2.imprint","IMPRINT",FACE,{"disambiguationData":[TD([[makeQuery(id+"F2.imprint","IMPRINT",EDGE,{"derivedFrom":sQuery(id+"F2.wireOp",EDGE,"E26")}),1.0]])]});
            extrude(context, id + "F7", {"entities" : qUnion([Q0, Q1, Q2, Q3, Q4, Q5, Q6]), "depth" : 0.13 * mm, "offsetDistance" : 25.4 * mm});
        }
        {
            var Q0;
            Q0=makeQuery(id+"F3.imprint","IMPRINT",FACE,{"disambiguationData":[TD([[makeQuery(id+"F3.imprint","IMPRINT",EDGE,{"derivedFrom":sQuery(id+"F3.wireOp",EDGE,"E464")}),1.0]])]});
            var Q1;
            Q1=makeQuery(id+"F3.imprint","IMPRINT",FACE,{"disambiguationData":[TD([[makeQuery(id+"F3.imprint","IMPRINT",EDGE,{"derivedFrom":sQuery(id+"F3.wireOp",EDGE,"E416")}),1.0]])]});
            var Q2;
            Q2=makeQuery(id+"F3.imprint","IMPRINT",FACE,{"disambiguationData":[TD([[makeQuery(id+"F3.imprint","IMPRINT",EDGE,{"derivedFrom":sQuery(id+"F3.wireOp",EDGE,"E283")}),1.0]])]});
            var Q3;
            Q3=makeQuery(id+"F3.imprint","IMPRINT",FACE,{"disambiguationData":[TD([[makeQuery(id+"F3.imprint","IMPRINT",EDGE,{"derivedFrom":sQuery(id+"F3.wireOp",EDGE,"E214")}),1.0]])]});
            var Q4;
            Q4=makeQuery(id+"F3.imprint","IMPRINT",FACE,{"disambiguationData":[TD([[makeQuery(id+"F3.imprint","IMPRINT",EDGE,{"derivedFrom":sQuery(id+"F3.wireOp",EDGE,"E255")}),1.0]])]});
            var Q5;
            Q5=makeQuery(id+"F3.imprint","IMPRINT",FACE,{"disambiguationData":[TD([[makeQuery(id+"F3.imprint","IMPRINT",EDGE,{"derivedFrom":sQuery(id+"F3.wireOp",EDGE,"E370")}),1.0]])]});
            var Q6;
            Q6=makeQuery(id+"F3.imprint","IMPRINT",FACE,{"disambiguationData":[TD([[makeQuery(id+"F3.imprint","IMPRINT",EDGE,{"derivedFrom":sQuery(id+"F3.wireOp",EDGE,"E314")}),1.0]])]});
            extrude(context, id + "F8", {"entities" : qUnion([Q0, Q1, Q2, Q3, Q4, Q5, Q6]), "depth" : 0.13 * mm, "offsetDistance" : 25.4 * mm});
        }
        {
            var Q0;
            Q0=makeQuery(id+"F4.imprint","IMPRINT",FACE,{"disambiguationData":[TD([[makeQuery(id+"F4.imprint","IMPRINT",EDGE,{"derivedFrom":sQuery(id+"F4.wireOp",EDGE,"E1033")}),1.0]])]});
            var Q1;
            Q1=makeQuery(id+"F4.imprint","IMPRINT",FACE,{"disambiguationData":[TD([[makeQuery(id+"F4.imprint","IMPRINT",EDGE,{"derivedFrom":sQuery(id+"F4.wireOp",EDGE,"E933")}),1.0]])]});
            var Q2;
            Q2=makeQuery(id+"F4.imprint","IMPRINT",FACE,{"disambiguationData":[TD([[makeQuery(id+"F4.imprint","IMPRINT",EDGE,{"derivedFrom":sQuery(id+"F4.wireOp",EDGE,"E687")}),1.0]])]});
            var Q3;
            Q3=makeQuery(id+"F4.imprint","IMPRINT",FACE,{"disambiguationData":[TD([[makeQuery(id+"F4.imprint","IMPRINT",EDGE,{"derivedFrom":sQuery(id+"F4.wireOp",EDGE,"E595")}),1.0]])]});
            var Q4;
            Q4=makeQuery(id+"F4.imprint","IMPRINT",FACE,{"disambiguationData":[TD([[makeQuery(id+"F4.imprint","IMPRINT",EDGE,{"derivedFrom":sQuery(id+"F4.wireOp",EDGE,"E738")}),1.0]])]});
            var Q5;
            Q5=makeQuery(id+"F4.imprint","IMPRINT",FACE,{"disambiguationData":[TD([[makeQuery(id+"F4.imprint","IMPRINT",EDGE,{"derivedFrom":sQuery(id+"F4.wireOp",EDGE,"E1077")}),1.0]])]});
            var Q6;
            Q6=makeQuery(id+"F4.imprint","IMPRINT",FACE,{"disambiguationData":[TD([[makeQuery(id+"F4.imprint","IMPRINT",EDGE,{"derivedFrom":sQuery(id+"F4.wireOp",EDGE,"E641")}),1.0]])]});
            var Q7;
            Q7=makeQuery(id+"F4.imprint","IMPRINT",FACE,{"disambiguationData":[TD([[makeQuery(id+"F4.imprint","IMPRINT",EDGE,{"derivedFrom":sQuery(id+"F4.wireOp",EDGE,"E537")}),1.0]])]});
            var Q8;
            Q8=makeQuery(id+"F4.imprint","IMPRINT",FACE,{"disambiguationData":[TD([[makeQuery(id+"F4.imprint","IMPRINT",EDGE,{"derivedFrom":sQuery(id+"F4.wireOp",EDGE,"E879")}),1.0]])]});
            var Q9;
            Q9=makeQuery(id+"F4.imprint","IMPRINT",FACE,{"disambiguationData":[TD([[makeQuery(id+"F4.imprint","IMPRINT",EDGE,{"derivedFrom":sQuery(id+"F4.wireOp",EDGE,"E980")}),1.0]])]});
            var Q10;
            Q10=makeQuery(id+"F4.imprint","IMPRINT",FACE,{"disambiguationData":[TD([[makeQuery(id+"F4.imprint","IMPRINT",EDGE,{"derivedFrom":sQuery(id+"F4.wireOp",EDGE,"E1219")}),1.0]])]});
            var Q11;
            Q11=makeQuery(id+"F4.imprint","IMPRINT",FACE,{"disambiguationData":[TD([[makeQuery(id+"F4.imprint","IMPRINT",EDGE,{"derivedFrom":sQuery(id+"F4.wireOp",EDGE,"E1173")}),1.0]])]});
            var Q12;
            Q12=makeQuery(id+"F4.imprint","IMPRINT",FACE,{"disambiguationData":[TD([[makeQuery(id+"F4.imprint","IMPRINT",EDGE,{"derivedFrom":sQuery(id+"F4.wireOp",EDGE,"E1126")}),1.0]])]});
            extrude(context, id + "F9", {"entities" : qUnion([Q0, Q1, Q2, Q3, Q4, Q5, Q6, Q7, Q8, Q9, Q10, Q11, Q12]), "depth" : 0.13 * mm, "offsetDistance" : 25.4 * mm});
        }
        {
            var Q0;
            Q0 = qSketchRegion(id + "F5", true);
            extrude(context, id + "F10", {"entities" : qUnion([Q0]), "depth" : 0.13 * mm, "offsetDistance" : 25.4 * mm});
        }
        {
            var Q0;
            Q0 = qSketchRegion(id + "F6", true);
            extrude(context, id + "F11", {"entities" : qUnion([Q0]), "depth" : 0.13 * mm, "offsetDistance" : 25.4 * mm});
        }
        {
            var Q0;
            Q0=makeQuery(id+"F1.opExtrude","SWEPT_BODY",BODY,{"disambiguationData":[OSD([sQuery(id+"F0.wireOp",EDGE,"E0"),sQuery(id+"F0.wireOp",EDGE,"ANRrlyus-TsXj-KHkA-7Rkr-odwGKdxKpd92")])]});
            var Q1;
            Q1=makeQuery(id+"FiHdyjKTytLpfGa_1.opExtrude","SWEPT_BODY",BODY,{"disambiguationData":[OSD([sQuery(id+"F0.wireOp",EDGE,"ANRrlyus-TsXj-KHkA-7Rkr-odwGKdxKpd92")])]});
            var Q2;
            Q2=makeQuery(id+"F7.opExtrude","SWEPT_BODY",BODY,{"disambiguationData":[OSD([sQuery(id+"F2.wireOp",EDGE,"E1"),sQuery(id+"F2.wireOp",EDGE,"E2"),sQuery(id+"F2.wireOp",EDGE,"E3"),sQuery(id+"F2.wireOp",EDGE,"E4"),sQuery(id+"F2.wireOp",EDGE,"E5"),sQuery(id+"F2.wireOp",EDGE,"E6"),sQuery(id+"F2.wireOp",EDGE,"E7"),sQuery(id+"F2.wireOp",EDGE,"E7"),sQuery(id+"F2.wireOp",EDGE,"E8"),sQuery(id+"F2.wireOp",EDGE,"E9"),sQuery(id+"F2.wireOp",EDGE,"E10"),sQuery(id+"F2.wireOp",EDGE,"E11"),sQuery(id+"F2.wireOp",EDGE,"E12"),sQuery(id+"F2.wireOp",EDGE,"E13"),sQuery(id+"F2.wireOp",EDGE,"E14"),sQuery(id+"F2.wireOp",EDGE,"E15"),sQuery(id+"F2.wireOp",EDGE,"E16"),sQuery(id+"F2.wireOp",EDGE,"E17"),sQuery(id+"F2.wireOp",EDGE,"E18"),sQuery(id+"F2.wireOp",EDGE,"E19"),sQuery(id+"F2.wireOp",EDGE,"E20"),sQuery(id+"F2.wireOp",EDGE,"E21"),sQuery(id+"F2.wireOp",EDGE,"E22"),sQuery(id+"F2.wireOp",EDGE,"E23"),sQuery(id+"F2.wireOp",EDGE,"E24"),sQuery(id+"F2.wireOp",EDGE,"E25")])]});
            var Q3;
            Q3=makeQuery(id+"F7.opExtrude","SWEPT_BODY",BODY,{"disambiguationData":[OSD([sQuery(id+"F2.wireOp",EDGE,"E26"),sQuery(id+"F2.wireOp",EDGE,"E27"),sQuery(id+"F2.wireOp",EDGE,"E28"),sQuery(id+"F2.wireOp",EDGE,"E29"),sQuery(id+"F2.wireOp",EDGE,"E30"),sQuery(id+"F2.wireOp",EDGE,"E31"),sQuery(id+"F2.wireOp",EDGE,"E32"),sQuery(id+"F2.wireOp",EDGE,"E33"),sQuery(id+"F2.wireOp",EDGE,"E34"),sQuery(id+"F2.wireOp",EDGE,"E35"),sQuery(id+"F2.wireOp",EDGE,"E36"),sQuery(id+"F2.wireOp",EDGE,"E37"),sQuery(id+"F2.wireOp",EDGE,"E38"),sQuery(id+"F2.wireOp",EDGE,"E38"),sQuery(id+"F2.wireOp",EDGE,"E39"),sQuery(id+"F2.wireOp",EDGE,"E40"),sQuery(id+"F2.wireOp",EDGE,"E41"),sQuery(id+"F2.wireOp",EDGE,"E42"),sQuery(id+"F2.wireOp",EDGE,"E43"),sQuery(id+"F2.wireOp",EDGE,"E44"),sQuery(id+"F2.wireOp",EDGE,"E45"),sQuery(id+"F2.wireOp",EDGE,"E46"),sQuery(id+"F2.wireOp",EDGE,"E47"),sQuery(id+"F2.wireOp",EDGE,"E48"),sQuery(id+"F2.wireOp",EDGE,"E49"),sQuery(id+"F2.wireOp",EDGE,"E26")])]});
            var Q4;
            Q4=makeQuery(id+"F7.opExtrude","SWEPT_BODY",BODY,{"disambiguationData":[OSD([sQuery(id+"F2.wireOp",EDGE,"E50"),sQuery(id+"F2.wireOp",EDGE,"E51"),sQuery(id+"F2.wireOp",EDGE,"E52"),sQuery(id+"F2.wireOp",EDGE,"E53"),sQuery(id+"F2.wireOp",EDGE,"E54"),sQuery(id+"F2.wireOp",EDGE,"E54"),sQuery(id+"F2.wireOp",EDGE,"E55"),sQuery(id+"F2.wireOp",EDGE,"E56"),sQuery(id+"F2.wireOp",EDGE,"E57"),sQuery(id+"F2.wireOp",EDGE,"E58"),sQuery(id+"F2.wireOp",EDGE,"E59"),sQuery(id+"F2.wireOp",EDGE,"E60"),sQuery(id+"F2.wireOp",EDGE,"E61"),sQuery(id+"F2.wireOp",EDGE,"E61"),sQuery(id+"F2.wireOp",EDGE,"E62"),sQuery(id+"F2.wireOp",EDGE,"E63"),sQuery(id+"F2.wireOp",EDGE,"E64"),sQuery(id+"F2.wireOp",EDGE,"E65"),sQuery(id+"F2.wireOp",EDGE,"E66"),sQuery(id+"F2.wireOp",EDGE,"E67"),sQuery(id+"F2.wireOp",EDGE,"E68"),sQuery(id+"F2.wireOp",EDGE,"E68"),sQuery(id+"F2.wireOp",EDGE,"E69"),sQuery(id+"F2.wireOp",EDGE,"E70"),sQuery(id+"F2.wireOp",EDGE,"E71"),sQuery(id+"F2.wireOp",EDGE,"E50")])]});
            var Q5;
            Q5=makeQuery(id+"F7.opExtrude","SWEPT_BODY",BODY,{"disambiguationData":[OSD([sQuery(id+"F2.wireOp",EDGE,"E72"),sQuery(id+"F2.wireOp",EDGE,"E73"),sQuery(id+"F2.wireOp",EDGE,"E74"),sQuery(id+"F2.wireOp",EDGE,"E75"),sQuery(id+"F2.wireOp",EDGE,"E76"),sQuery(id+"F2.wireOp",EDGE,"E77"),sQuery(id+"F2.wireOp",EDGE,"E78"),sQuery(id+"F2.wireOp",EDGE,"E79"),sQuery(id+"F2.wireOp",EDGE,"E80"),sQuery(id+"F2.wireOp",EDGE,"E81"),sQuery(id+"F2.wireOp",EDGE,"E82"),sQuery(id+"F2.wireOp",EDGE,"E83"),sQuery(id+"F2.wireOp",EDGE,"E84"),sQuery(id+"F2.wireOp",EDGE,"E85"),sQuery(id+"F2.wireOp",EDGE,"E86"),sQuery(id+"F2.wireOp",EDGE,"E87"),sQuery(id+"F2.wireOp",EDGE,"E88"),sQuery(id+"F2.wireOp",EDGE,"E89"),sQuery(id+"F2.wireOp",EDGE,"E90"),sQuery(id+"F2.wireOp",EDGE,"E91"),sQuery(id+"F2.wireOp",EDGE,"E92"),sQuery(id+"F2.wireOp",EDGE,"E93"),sQuery(id+"F2.wireOp",EDGE,"E94"),sQuery(id+"F2.wireOp",EDGE,"E95"),sQuery(id+"F2.wireOp",EDGE,"E96"),sQuery(id+"F2.wireOp",EDGE,"E97")])]});
            var Q6;
            Q6=makeQuery(id+"F7.opExtrude","SWEPT_BODY",BODY,{"disambiguationData":[OSD([sQuery(id+"F2.wireOp",EDGE,"E98"),sQuery(id+"F2.wireOp",EDGE,"E99"),sQuery(id+"F2.wireOp",EDGE,"E100"),sQuery(id+"F2.wireOp",EDGE,"E101"),sQuery(id+"F2.wireOp",EDGE,"E102"),sQuery(id+"F2.wireOp",EDGE,"E103"),sQuery(id+"F2.wireOp",EDGE,"E104"),sQuery(id+"F2.wireOp",EDGE,"E104"),sQuery(id+"F2.wireOp",EDGE,"E105"),sQuery(id+"F2.wireOp",EDGE,"E106"),sQuery(id+"F2.wireOp",EDGE,"E107"),sQuery(id+"F2.wireOp",EDGE,"E108"),sQuery(id+"F2.wireOp",EDGE,"E109"),sQuery(id+"F2.wireOp",EDGE,"E110"),sQuery(id+"F2.wireOp",EDGE,"E111"),sQuery(id+"F2.wireOp",EDGE,"E112"),sQuery(id+"F2.wireOp",EDGE,"E113"),sQuery(id+"F2.wireOp",EDGE,"E114"),sQuery(id+"F2.wireOp",EDGE,"E115"),sQuery(id+"F2.wireOp",EDGE,"E116"),sQuery(id+"F2.wireOp",EDGE,"E116"),sQuery(id+"F2.wireOp",EDGE,"E117"),sQuery(id+"F2.wireOp",EDGE,"E118"),sQuery(id+"F2.wireOp",EDGE,"E119"),sQuery(id+"F2.wireOp",EDGE,"E120"),sQuery(id+"F2.wireOp",EDGE,"E121")])]});
            var Q7;
            Q7=makeQuery(id+"F7.opExtrude","SWEPT_BODY",BODY,{"disambiguationData":[OSD([sQuery(id+"F2.wireOp",EDGE,"E122"),sQuery(id+"F2.wireOp",EDGE,"E123"),sQuery(id+"F2.wireOp",EDGE,"E124"),sQuery(id+"F2.wireOp",EDGE,"E125"),sQuery(id+"F2.wireOp",EDGE,"E126"),sQuery(id+"F2.wireOp",EDGE,"E127"),sQuery(id+"F2.wireOp",EDGE,"E128"),sQuery(id+"F2.wireOp",EDGE,"E129"),sQuery(id+"F2.wireOp",EDGE,"E130"),sQuery(id+"F2.wireOp",EDGE,"E131"),sQuery(id+"F2.wireOp",EDGE,"E132"),sQuery(id+"F2.wireOp",EDGE,"E133"),sQuery(id+"F2.wireOp",EDGE,"E133"),sQuery(id+"F2.wireOp",EDGE,"E134"),sQuery(id+"F2.wireOp",EDGE,"E135"),sQuery(id+"F2.wireOp",EDGE,"E136"),sQuery(id+"F2.wireOp",EDGE,"E137"),sQuery(id+"F2.wireOp",EDGE,"E138"),sQuery(id+"F2.wireOp",EDGE,"E139"),sQuery(id+"F2.wireOp",EDGE,"E140"),sQuery(id+"F2.wireOp",EDGE,"E141"),sQuery(id+"F2.wireOp",EDGE,"E142"),sQuery(id+"F2.wireOp",EDGE,"E143"),sQuery(id+"F2.wireOp",EDGE,"E144"),sQuery(id+"F2.wireOp",EDGE,"E145"),sQuery(id+"F2.wireOp",EDGE,"E146"),sQuery(id+"F2.wireOp",EDGE,"E147"),sQuery(id+"F2.wireOp",EDGE,"E148"),sQuery(id+"F2.wireOp",EDGE,"E148"),sQuery(id+"F2.wireOp",EDGE,"E149"),sQuery(id+"F2.wireOp",EDGE,"E150"),sQuery(id+"F2.wireOp",EDGE,"E151"),sQuery(id+"F2.wireOp",EDGE,"E152"),sQuery(id+"F2.wireOp",EDGE,"E153")])]});
            var Q8;
            Q8=makeQuery(id+"F7.opExtrude","SWEPT_BODY",BODY,{"disambiguationData":[OSD([sQuery(id+"F2.wireOp",EDGE,"E154"),sQuery(id+"F2.wireOp",EDGE,"E155"),sQuery(id+"F2.wireOp",EDGE,"E156"),sQuery(id+"F2.wireOp",EDGE,"E157"),sQuery(id+"F2.wireOp",EDGE,"E158"),sQuery(id+"F2.wireOp",EDGE,"E159"),sQuery(id+"F2.wireOp",EDGE,"E160"),sQuery(id+"F2.wireOp",EDGE,"E161"),sQuery(id+"F2.wireOp",EDGE,"E162"),sQuery(id+"F2.wireOp",EDGE,"E163"),sQuery(id+"F2.wireOp",EDGE,"E164"),sQuery(id+"F2.wireOp",EDGE,"E165"),sQuery(id+"F2.wireOp",EDGE,"E166"),sQuery(id+"F2.wireOp",EDGE,"E167"),sQuery(id+"F2.wireOp",EDGE,"E168"),sQuery(id+"F2.wireOp",EDGE,"E169"),sQuery(id+"F2.wireOp",EDGE,"E170"),sQuery(id+"F2.wireOp",EDGE,"E171"),sQuery(id+"F2.wireOp",EDGE,"E172"),sQuery(id+"F2.wireOp",EDGE,"E173"),sQuery(id+"F2.wireOp",EDGE,"E174"),sQuery(id+"F2.wireOp",EDGE,"E175"),sQuery(id+"F2.wireOp",EDGE,"E176"),sQuery(id+"F2.wireOp",EDGE,"E177"),sQuery(id+"F2.wireOp",EDGE,"E178"),sQuery(id+"F2.wireOp",EDGE,"E179"),sQuery(id+"F2.wireOp",EDGE,"E180"),sQuery(id+"F2.wireOp",EDGE,"E181"),sQuery(id+"F2.wireOp",EDGE,"E182"),sQuery(id+"F2.wireOp",EDGE,"E183"),sQuery(id+"F2.wireOp",EDGE,"E184"),sQuery(id+"F2.wireOp",EDGE,"E185"),sQuery(id+"F2.wireOp",EDGE,"E186"),sQuery(id+"F2.wireOp",EDGE,"E187"),sQuery(id+"F2.wireOp",EDGE,"E188"),sQuery(id+"F2.wireOp",EDGE,"E189"),sQuery(id+"F2.wireOp",EDGE,"E190"),sQuery(id+"F2.wireOp",EDGE,"E191"),sQuery(id+"F2.wireOp",EDGE,"E192"),sQuery(id+"F2.wireOp",EDGE,"E193"),sQuery(id+"F2.wireOp",EDGE,"E194"),sQuery(id+"F2.wireOp",EDGE,"E195"),sQuery(id+"F2.wireOp",EDGE,"E196"),sQuery(id+"F2.wireOp",EDGE,"E197"),sQuery(id+"F2.wireOp",EDGE,"E198"),sQuery(id+"F2.wireOp",EDGE,"E199"),sQuery(id+"F2.wireOp",EDGE,"E200"),sQuery(id+"F2.wireOp",EDGE,"E201"),sQuery(id+"F2.wireOp",EDGE,"E202"),sQuery(id+"F2.wireOp",EDGE,"E203"),sQuery(id+"F2.wireOp",EDGE,"E204"),sQuery(id+"F2.wireOp",EDGE,"E205"),sQuery(id+"F2.wireOp",EDGE,"E206"),sQuery(id+"F2.wireOp",EDGE,"E207"),sQuery(id+"F2.wireOp",EDGE,"E208"),sQuery(id+"F2.wireOp",EDGE,"E209"),sQuery(id+"F2.wireOp",EDGE,"E210"),sQuery(id+"F2.wireOp",EDGE,"E211"),sQuery(id+"F2.wireOp",EDGE,"E212"),sQuery(id+"F2.wireOp",EDGE,"E213")])]});
            var Q9;
            Q9=makeQuery(id+"F8.opExtrude","SWEPT_BODY",BODY,{"disambiguationData":[OSD([sQuery(id+"F3.wireOp",EDGE,"E214"),sQuery(id+"F3.wireOp",EDGE,"E214"),sQuery(id+"F3.wireOp",EDGE,"E215"),sQuery(id+"F3.wireOp",EDGE,"E216"),sQuery(id+"F3.wireOp",EDGE,"E217"),sQuery(id+"F3.wireOp",EDGE,"E218"),sQuery(id+"F3.wireOp",EDGE,"E219"),sQuery(id+"F3.wireOp",EDGE,"E220"),sQuery(id+"F3.wireOp",EDGE,"E221"),sQuery(id+"F3.wireOp",EDGE,"E222"),sQuery(id+"F3.wireOp",EDGE,"E223"),sQuery(id+"F3.wireOp",EDGE,"E224"),sQuery(id+"F3.wireOp",EDGE,"E225"),sQuery(id+"F3.wireOp",EDGE,"E226"),sQuery(id+"F3.wireOp",EDGE,"E227"),sQuery(id+"F3.wireOp",EDGE,"E228"),sQuery(id+"F3.wireOp",EDGE,"E229"),sQuery(id+"F3.wireOp",EDGE,"E230"),sQuery(id+"F3.wireOp",EDGE,"E231"),sQuery(id+"F3.wireOp",EDGE,"E231"),sQuery(id+"F3.wireOp",EDGE,"E232"),sQuery(id+"F3.wireOp",EDGE,"E233"),sQuery(id+"F3.wireOp",EDGE,"E234"),sQuery(id+"F3.wireOp",EDGE,"E235"),sQuery(id+"F3.wireOp",EDGE,"E236"),sQuery(id+"F3.wireOp",EDGE,"E237"),sQuery(id+"F3.wireOp",EDGE,"E237"),sQuery(id+"F3.wireOp",EDGE,"E238"),sQuery(id+"F3.wireOp",EDGE,"E239"),sQuery(id+"F3.wireOp",EDGE,"E240"),sQuery(id+"F3.wireOp",EDGE,"E241"),sQuery(id+"F3.wireOp",EDGE,"E242"),sQuery(id+"F3.wireOp",EDGE,"E243"),sQuery(id+"F3.wireOp",EDGE,"E244"),sQuery(id+"F3.wireOp",EDGE,"E245"),sQuery(id+"F3.wireOp",EDGE,"E246"),sQuery(id+"F3.wireOp",EDGE,"E247"),sQuery(id+"F3.wireOp",EDGE,"E248"),sQuery(id+"F3.wireOp",EDGE,"E249"),sQuery(id+"F3.wireOp",EDGE,"E250"),sQuery(id+"F3.wireOp",EDGE,"E250"),sQuery(id+"F3.wireOp",EDGE,"E250"),sQuery(id+"F3.wireOp",EDGE,"E251"),sQuery(id+"F3.wireOp",EDGE,"E252"),sQuery(id+"F3.wireOp",EDGE,"E253"),sQuery(id+"F3.wireOp",EDGE,"E254")])]});
            var Q10;
            Q10=makeQuery(id+"F8.opExtrude","SWEPT_BODY",BODY,{"disambiguationData":[OSD([sQuery(id+"F3.wireOp",EDGE,"E255"),sQuery(id+"F3.wireOp",EDGE,"E256"),sQuery(id+"F3.wireOp",EDGE,"E257"),sQuery(id+"F3.wireOp",EDGE,"E258"),sQuery(id+"F3.wireOp",EDGE,"E258"),sQuery(id+"F3.wireOp",EDGE,"E259"),sQuery(id+"F3.wireOp",EDGE,"E260"),sQuery(id+"F3.wireOp",EDGE,"E261"),sQuery(id+"F3.wireOp",EDGE,"E262"),sQuery(id+"F3.wireOp",EDGE,"E263"),sQuery(id+"F3.wireOp",EDGE,"E264"),sQuery(id+"F3.wireOp",EDGE,"E265"),sQuery(id+"F3.wireOp",EDGE,"E266"),sQuery(id+"F3.wireOp",EDGE,"E267"),sQuery(id+"F3.wireOp",EDGE,"E267"),sQuery(id+"F3.wireOp",EDGE,"E268"),sQuery(id+"F3.wireOp",EDGE,"E269"),sQuery(id+"F3.wireOp",EDGE,"E270"),sQuery(id+"F3.wireOp",EDGE,"E271"),sQuery(id+"F3.wireOp",EDGE,"E271"),sQuery(id+"F3.wireOp",EDGE,"E271"),sQuery(id+"F3.wireOp",EDGE,"E272"),sQuery(id+"F3.wireOp",EDGE,"E273"),sQuery(id+"F3.wireOp",EDGE,"E274"),sQuery(id+"F3.wireOp",EDGE,"E275"),sQuery(id+"F3.wireOp",EDGE,"E276"),sQuery(id+"F3.wireOp",EDGE,"E277"),sQuery(id+"F3.wireOp",EDGE,"E278"),sQuery(id+"F3.wireOp",EDGE,"E279"),sQuery(id+"F3.wireOp",EDGE,"E279"),sQuery(id+"F3.wireOp",EDGE,"E280"),sQuery(id+"F3.wireOp",EDGE,"E281"),sQuery(id+"F3.wireOp",EDGE,"E282"),sQuery(id+"F3.wireOp",EDGE,"E255")])]});
            var Q11;
            Q11=makeQuery(id+"F8.opExtrude","SWEPT_BODY",BODY,{"disambiguationData":[OSD([sQuery(id+"F3.wireOp",EDGE,"E283"),sQuery(id+"F3.wireOp",EDGE,"E284"),sQuery(id+"F3.wireOp",EDGE,"E285"),sQuery(id+"F3.wireOp",EDGE,"E286"),sQuery(id+"F3.wireOp",EDGE,"E287"),sQuery(id+"F3.wireOp",EDGE,"E288"),sQuery(id+"F3.wireOp",EDGE,"E289"),sQuery(id+"F3.wireOp",EDGE,"E290"),sQuery(id+"F3.wireOp",EDGE,"E291"),sQuery(id+"F3.wireOp",EDGE,"E292"),sQuery(id+"F3.wireOp",EDGE,"E293"),sQuery(id+"F3.wireOp",EDGE,"E294"),sQuery(id+"F3.wireOp",EDGE,"E295"),sQuery(id+"F3.wireOp",EDGE,"E296"),sQuery(id+"F3.wireOp",EDGE,"E297"),sQuery(id+"F3.wireOp",EDGE,"E298"),sQuery(id+"F3.wireOp",EDGE,"E299"),sQuery(id+"F3.wireOp",EDGE,"E300"),sQuery(id+"F3.wireOp",EDGE,"E301"),sQuery(id+"F3.wireOp",EDGE,"E302"),sQuery(id+"F3.wireOp",EDGE,"E302"),sQuery(id+"F3.wireOp",EDGE,"E303"),sQuery(id+"F3.wireOp",EDGE,"E304"),sQuery(id+"F3.wireOp",EDGE,"E305"),sQuery(id+"F3.wireOp",EDGE,"E306"),sQuery(id+"F3.wireOp",EDGE,"E307"),sQuery(id+"F3.wireOp",EDGE,"E308"),sQuery(id+"F3.wireOp",EDGE,"E309"),sQuery(id+"F3.wireOp",EDGE,"E310"),sQuery(id+"F3.wireOp",EDGE,"E311"),sQuery(id+"F3.wireOp",EDGE,"E312"),sQuery(id+"F3.wireOp",EDGE,"E313")])]});
            var Q12;
            Q12=makeQuery(id+"F8.opExtrude","SWEPT_BODY",BODY,{"disambiguationData":[OSD([sQuery(id+"F3.wireOp",EDGE,"E314"),sQuery(id+"F3.wireOp",EDGE,"E315"),sQuery(id+"F3.wireOp",EDGE,"E316"),sQuery(id+"F3.wireOp",EDGE,"E317"),sQuery(id+"F3.wireOp",EDGE,"E318"),sQuery(id+"F3.wireOp",EDGE,"E319"),sQuery(id+"F3.wireOp",EDGE,"E320"),sQuery(id+"F3.wireOp",EDGE,"E321"),sQuery(id+"F3.wireOp",EDGE,"E322"),sQuery(id+"F3.wireOp",EDGE,"E323"),sQuery(id+"F3.wireOp",EDGE,"E324"),sQuery(id+"F3.wireOp",EDGE,"E325"),sQuery(id+"F3.wireOp",EDGE,"E326"),sQuery(id+"F3.wireOp",EDGE,"E327"),sQuery(id+"F3.wireOp",EDGE,"E328"),sQuery(id+"F3.wireOp",EDGE,"E329"),sQuery(id+"F3.wireOp",EDGE,"E330"),sQuery(id+"F3.wireOp",EDGE,"E331"),sQuery(id+"F3.wireOp",EDGE,"E332"),sQuery(id+"F3.wireOp",EDGE,"E333"),sQuery(id+"F3.wireOp",EDGE,"E334"),sQuery(id+"F3.wireOp",EDGE,"E335"),sQuery(id+"F3.wireOp",EDGE,"E336"),sQuery(id+"F3.wireOp",EDGE,"E337"),sQuery(id+"F3.wireOp",EDGE,"E338"),sQuery(id+"F3.wireOp",EDGE,"E339"),sQuery(id+"F3.wireOp",EDGE,"E340"),sQuery(id+"F3.wireOp",EDGE,"E341"),sQuery(id+"F3.wireOp",EDGE,"E342"),sQuery(id+"F3.wireOp",EDGE,"E343"),sQuery(id+"F3.wireOp",EDGE,"E344"),sQuery(id+"F3.wireOp",EDGE,"E345"),sQuery(id+"F3.wireOp",EDGE,"E346"),sQuery(id+"F3.wireOp",EDGE,"E347"),sQuery(id+"F3.wireOp",EDGE,"E348"),sQuery(id+"F3.wireOp",EDGE,"E349"),sQuery(id+"F3.wireOp",EDGE,"E350"),sQuery(id+"F3.wireOp",EDGE,"E351"),sQuery(id+"F3.wireOp",EDGE,"E352"),sQuery(id+"F3.wireOp",EDGE,"E353"),sQuery(id+"F3.wireOp",EDGE,"E354"),sQuery(id+"F3.wireOp",EDGE,"E355"),sQuery(id+"F3.wireOp",EDGE,"E356"),sQuery(id+"F3.wireOp",EDGE,"E357"),sQuery(id+"F3.wireOp",EDGE,"E358"),sQuery(id+"F3.wireOp",EDGE,"E359"),sQuery(id+"F3.wireOp",EDGE,"E360"),sQuery(id+"F3.wireOp",EDGE,"E361"),sQuery(id+"F3.wireOp",EDGE,"E362"),sQuery(id+"F3.wireOp",EDGE,"E363"),sQuery(id+"F3.wireOp",EDGE,"E364"),sQuery(id+"F3.wireOp",EDGE,"E365"),sQuery(id+"F3.wireOp",EDGE,"E366"),sQuery(id+"F3.wireOp",EDGE,"E367"),sQuery(id+"F3.wireOp",EDGE,"E368"),sQuery(id+"F3.wireOp",EDGE,"E369")])]});
            var Q13;
            Q13=makeQuery(id+"F8.opExtrude","SWEPT_BODY",BODY,{"disambiguationData":[OSD([sQuery(id+"F3.wireOp",EDGE,"E370"),sQuery(id+"F3.wireOp",EDGE,"E371"),sQuery(id+"F3.wireOp",EDGE,"E372"),sQuery(id+"F3.wireOp",EDGE,"E373"),sQuery(id+"F3.wireOp",EDGE,"E374"),sQuery(id+"F3.wireOp",EDGE,"E375"),sQuery(id+"F3.wireOp",EDGE,"E376"),sQuery(id+"F3.wireOp",EDGE,"E376"),sQuery(id+"F3.wireOp",EDGE,"E377"),sQuery(id+"F3.wireOp",EDGE,"E378"),sQuery(id+"F3.wireOp",EDGE,"E379"),sQuery(id+"F3.wireOp",EDGE,"E380"),sQuery(id+"F3.wireOp",EDGE,"E381"),sQuery(id+"F3.wireOp",EDGE,"E382"),sQuery(id+"F3.wireOp",EDGE,"E383"),sQuery(id+"F3.wireOp",EDGE,"E384"),sQuery(id+"F3.wireOp",EDGE,"E385"),sQuery(id+"F3.wireOp",EDGE,"E386"),sQuery(id+"F3.wireOp",EDGE,"E387"),sQuery(id+"F3.wireOp",EDGE,"E388"),sQuery(id+"F3.wireOp",EDGE,"E389"),sQuery(id+"F3.wireOp",EDGE,"E390"),sQuery(id+"F3.wireOp",EDGE,"E391"),sQuery(id+"F3.wireOp",EDGE,"E392"),sQuery(id+"F3.wireOp",EDGE,"E393"),sQuery(id+"F3.wireOp",EDGE,"E393"),sQuery(id+"F3.wireOp",EDGE,"E394"),sQuery(id+"F3.wireOp",EDGE,"E395"),sQuery(id+"F3.wireOp",EDGE,"E396"),sQuery(id+"F3.wireOp",EDGE,"E397"),sQuery(id+"F3.wireOp",EDGE,"E398"),sQuery(id+"F3.wireOp",EDGE,"E399"),sQuery(id+"F3.wireOp",EDGE,"E399"),sQuery(id+"F3.wireOp",EDGE,"E399"),sQuery(id+"F3.wireOp",EDGE,"E400"),sQuery(id+"F3.wireOp",EDGE,"E401"),sQuery(id+"F3.wireOp",EDGE,"E402"),sQuery(id+"F3.wireOp",EDGE,"E403"),sQuery(id+"F3.wireOp",EDGE,"E404"),sQuery(id+"F3.wireOp",EDGE,"E405"),sQuery(id+"F3.wireOp",EDGE,"E406"),sQuery(id+"F3.wireOp",EDGE,"E407"),sQuery(id+"F3.wireOp",EDGE,"E408"),sQuery(id+"F3.wireOp",EDGE,"E409"),sQuery(id+"F3.wireOp",EDGE,"E410"),sQuery(id+"F3.wireOp",EDGE,"E411"),sQuery(id+"F3.wireOp",EDGE,"E412"),sQuery(id+"F3.wireOp",EDGE,"E413"),sQuery(id+"F3.wireOp",EDGE,"E414"),sQuery(id+"F3.wireOp",EDGE,"E415"),sQuery(id+"F3.wireOp",EDGE,"E370"),sQuery(id+"F3.wireOp",EDGE,"E370")])]});
            var Q14;
            Q14=makeQuery(id+"F8.opExtrude","SWEPT_BODY",BODY,{"disambiguationData":[OSD([sQuery(id+"F3.wireOp",EDGE,"E416"),sQuery(id+"F3.wireOp",EDGE,"E417"),sQuery(id+"F3.wireOp",EDGE,"E418"),sQuery(id+"F3.wireOp",EDGE,"E419"),sQuery(id+"F3.wireOp",EDGE,"E420"),sQuery(id+"F3.wireOp",EDGE,"E421"),sQuery(id+"F3.wireOp",EDGE,"E422"),sQuery(id+"F3.wireOp",EDGE,"E422"),sQuery(id+"F3.wireOp",EDGE,"E423"),sQuery(id+"F3.wireOp",EDGE,"E424"),sQuery(id+"F3.wireOp",EDGE,"E425"),sQuery(id+"F3.wireOp",EDGE,"E426"),sQuery(id+"F3.wireOp",EDGE,"E427"),sQuery(id+"F3.wireOp",EDGE,"E428"),sQuery(id+"F3.wireOp",EDGE,"E429"),sQuery(id+"F3.wireOp",EDGE,"E430"),sQuery(id+"F3.wireOp",EDGE,"E431"),sQuery(id+"F3.wireOp",EDGE,"E432"),sQuery(id+"F3.wireOp",EDGE,"E433"),sQuery(id+"F3.wireOp",EDGE,"E434"),sQuery(id+"F3.wireOp",EDGE,"E435"),sQuery(id+"F3.wireOp",EDGE,"E436"),sQuery(id+"F3.wireOp",EDGE,"E437"),sQuery(id+"F3.wireOp",EDGE,"E438"),sQuery(id+"F3.wireOp",EDGE,"E439"),sQuery(id+"F3.wireOp",EDGE,"E439"),sQuery(id+"F3.wireOp",EDGE,"E440"),sQuery(id+"F3.wireOp",EDGE,"E441"),sQuery(id+"F3.wireOp",EDGE,"E442"),sQuery(id+"F3.wireOp",EDGE,"E443"),sQuery(id+"F3.wireOp",EDGE,"E444"),sQuery(id+"F3.wireOp",EDGE,"E445"),sQuery(id+"F3.wireOp",EDGE,"E446"),sQuery(id+"F3.wireOp",EDGE,"E447"),sQuery(id+"F3.wireOp",EDGE,"E447"),sQuery(id+"F3.wireOp",EDGE,"E447"),sQuery(id+"F3.wireOp",EDGE,"E448"),sQuery(id+"F3.wireOp",EDGE,"E449"),sQuery(id+"F3.wireOp",EDGE,"E450"),sQuery(id+"F3.wireOp",EDGE,"E451"),sQuery(id+"F3.wireOp",EDGE,"E452"),sQuery(id+"F3.wireOp",EDGE,"E453"),sQuery(id+"F3.wireOp",EDGE,"E454"),sQuery(id+"F3.wireOp",EDGE,"E455"),sQuery(id+"F3.wireOp",EDGE,"E456"),sQuery(id+"F3.wireOp",EDGE,"E457"),sQuery(id+"F3.wireOp",EDGE,"E458"),sQuery(id+"F3.wireOp",EDGE,"E459"),sQuery(id+"F3.wireOp",EDGE,"E460"),sQuery(id+"F3.wireOp",EDGE,"E461"),sQuery(id+"F3.wireOp",EDGE,"E462"),sQuery(id+"F3.wireOp",EDGE,"E462"),sQuery(id+"F3.wireOp",EDGE,"E463"),sQuery(id+"F3.wireOp",EDGE,"E416")])]});
            var Q15;
            Q15=makeQuery(id+"F8.opExtrude","SWEPT_BODY",BODY,{"disambiguationData":[OSD([sQuery(id+"F3.wireOp",EDGE,"E464"),sQuery(id+"F3.wireOp",EDGE,"E465"),sQuery(id+"F3.wireOp",EDGE,"E466"),sQuery(id+"F3.wireOp",EDGE,"E467"),sQuery(id+"F3.wireOp",EDGE,"E468"),sQuery(id+"F3.wireOp",EDGE,"E469"),sQuery(id+"F3.wireOp",EDGE,"E470"),sQuery(id+"F3.wireOp",EDGE,"E471"),sQuery(id+"F3.wireOp",EDGE,"E472"),sQuery(id+"F3.wireOp",EDGE,"E473"),sQuery(id+"F3.wireOp",EDGE,"E474"),sQuery(id+"F3.wireOp",EDGE,"E475"),sQuery(id+"F3.wireOp",EDGE,"E475"),sQuery(id+"F3.wireOp",EDGE,"E476"),sQuery(id+"F3.wireOp",EDGE,"E477"),sQuery(id+"F3.wireOp",EDGE,"E478"),sQuery(id+"F3.wireOp",EDGE,"E479"),sQuery(id+"F3.wireOp",EDGE,"E480"),sQuery(id+"F3.wireOp",EDGE,"E481"),sQuery(id+"F3.wireOp",EDGE,"E482"),sQuery(id+"F3.wireOp",EDGE,"E483"),sQuery(id+"F3.wireOp",EDGE,"E484"),sQuery(id+"F3.wireOp",EDGE,"E485"),sQuery(id+"F3.wireOp",EDGE,"E486"),sQuery(id+"F3.wireOp",EDGE,"E487"),sQuery(id+"F3.wireOp",EDGE,"E488"),sQuery(id+"F3.wireOp",EDGE,"E489"),sQuery(id+"F3.wireOp",EDGE,"E490"),sQuery(id+"F3.wireOp",EDGE,"E491"),sQuery(id+"F3.wireOp",EDGE,"E492"),sQuery(id+"F3.wireOp",EDGE,"E493"),sQuery(id+"F3.wireOp",EDGE,"E494"),sQuery(id+"F3.wireOp",EDGE,"E495"),sQuery(id+"F3.wireOp",EDGE,"E496"),sQuery(id+"F3.wireOp",EDGE,"E497"),sQuery(id+"F3.wireOp",EDGE,"E498"),sQuery(id+"F3.wireOp",EDGE,"E498"),sQuery(id+"F3.wireOp",EDGE,"E499"),sQuery(id+"F3.wireOp",EDGE,"E500"),sQuery(id+"F3.wireOp",EDGE,"E501"),sQuery(id+"F3.wireOp",EDGE,"E502"),sQuery(id+"F3.wireOp",EDGE,"E503"),sQuery(id+"F3.wireOp",EDGE,"E504"),sQuery(id+"F3.wireOp",EDGE,"E505"),sQuery(id+"F3.wireOp",EDGE,"E506"),sQuery(id+"F3.wireOp",EDGE,"E507"),sQuery(id+"F3.wireOp",EDGE,"E508"),sQuery(id+"F3.wireOp",EDGE,"E509"),sQuery(id+"F3.wireOp",EDGE,"E510"),sQuery(id+"F3.wireOp",EDGE,"E511"),sQuery(id+"F3.wireOp",EDGE,"E512"),sQuery(id+"F3.wireOp",EDGE,"E513"),sQuery(id+"F3.wireOp",EDGE,"E514"),sQuery(id+"F3.wireOp",EDGE,"E515"),sQuery(id+"F3.wireOp",EDGE,"E516"),sQuery(id+"F3.wireOp",EDGE,"E517"),sQuery(id+"F3.wireOp",EDGE,"E518"),sQuery(id+"F3.wireOp",EDGE,"E519"),sQuery(id+"F3.wireOp",EDGE,"E520"),sQuery(id+"F3.wireOp",EDGE,"E521"),sQuery(id+"F3.wireOp",EDGE,"E522"),sQuery(id+"F3.wireOp",EDGE,"E523"),sQuery(id+"F3.wireOp",EDGE,"E524"),sQuery(id+"F3.wireOp",EDGE,"E525"),sQuery(id+"F3.wireOp",EDGE,"E526"),sQuery(id+"F3.wireOp",EDGE,"E527"),sQuery(id+"F3.wireOp",EDGE,"E528"),sQuery(id+"F3.wireOp",EDGE,"E529"),sQuery(id+"F3.wireOp",EDGE,"E530"),sQuery(id+"F3.wireOp",EDGE,"E531"),sQuery(id+"F3.wireOp",EDGE,"E532"),sQuery(id+"F3.wireOp",EDGE,"E533"),sQuery(id+"F3.wireOp",EDGE,"E534"),sQuery(id+"F3.wireOp",EDGE,"E535"),sQuery(id+"F3.wireOp",EDGE,"E536")])]});
            var Q16;
            Q16=makeQuery(id+"F9.opExtrude","SWEPT_BODY",BODY,{"disambiguationData":[OSD([sQuery(id+"F4.wireOp",EDGE,"E537"),sQuery(id+"F4.wireOp",EDGE,"E538"),sQuery(id+"F4.wireOp",EDGE,"E539"),sQuery(id+"F4.wireOp",EDGE,"E540"),sQuery(id+"F4.wireOp",EDGE,"E541"),sQuery(id+"F4.wireOp",EDGE,"E542"),sQuery(id+"F4.wireOp",EDGE,"E543"),sQuery(id+"F4.wireOp",EDGE,"E544"),sQuery(id+"F4.wireOp",EDGE,"E545"),sQuery(id+"F4.wireOp",EDGE,"E546"),sQuery(id+"F4.wireOp",EDGE,"E547"),sQuery(id+"F4.wireOp",EDGE,"E548"),sQuery(id+"F4.wireOp",EDGE,"E549"),sQuery(id+"F4.wireOp",EDGE,"E550"),sQuery(id+"F4.wireOp",EDGE,"E551"),sQuery(id+"F4.wireOp",EDGE,"E552"),sQuery(id+"F4.wireOp",EDGE,"E553"),sQuery(id+"F4.wireOp",EDGE,"E554"),sQuery(id+"F4.wireOp",EDGE,"E555"),sQuery(id+"F4.wireOp",EDGE,"E556"),sQuery(id+"F4.wireOp",EDGE,"E556"),sQuery(id+"F4.wireOp",EDGE,"E557"),sQuery(id+"F4.wireOp",EDGE,"E558"),sQuery(id+"F4.wireOp",EDGE,"E559"),sQuery(id+"F4.wireOp",EDGE,"E560"),sQuery(id+"F4.wireOp",EDGE,"E561"),sQuery(id+"F4.wireOp",EDGE,"E562"),sQuery(id+"F4.wireOp",EDGE,"E563"),sQuery(id+"F4.wireOp",EDGE,"E563"),sQuery(id+"F4.wireOp",EDGE,"E564"),sQuery(id+"F4.wireOp",EDGE,"E565"),sQuery(id+"F4.wireOp",EDGE,"E566"),sQuery(id+"F4.wireOp",EDGE,"E567"),sQuery(id+"F4.wireOp",EDGE,"E567"),sQuery(id+"F4.wireOp",EDGE,"E568"),sQuery(id+"F4.wireOp",EDGE,"E569"),sQuery(id+"F4.wireOp",EDGE,"E570"),sQuery(id+"F4.wireOp",EDGE,"E571"),sQuery(id+"F4.wireOp",EDGE,"E572"),sQuery(id+"F4.wireOp",EDGE,"E573"),sQuery(id+"F4.wireOp",EDGE,"E574"),sQuery(id+"F4.wireOp",EDGE,"E575"),sQuery(id+"F4.wireOp",EDGE,"E576"),sQuery(id+"F4.wireOp",EDGE,"E577"),sQuery(id+"F4.wireOp",EDGE,"E577"),sQuery(id+"F4.wireOp",EDGE,"E578"),sQuery(id+"F4.wireOp",EDGE,"E579"),sQuery(id+"F4.wireOp",EDGE,"E580"),sQuery(id+"F4.wireOp",EDGE,"E581"),sQuery(id+"F4.wireOp",EDGE,"E582"),sQuery(id+"F4.wireOp",EDGE,"E583"),sQuery(id+"F4.wireOp",EDGE,"E584"),sQuery(id+"F4.wireOp",EDGE,"E585"),sQuery(id+"F4.wireOp",EDGE,"E586"),sQuery(id+"F4.wireOp",EDGE,"E587"),sQuery(id+"F4.wireOp",EDGE,"E588"),sQuery(id+"F4.wireOp",EDGE,"E589"),sQuery(id+"F4.wireOp",EDGE,"E590"),sQuery(id+"F4.wireOp",EDGE,"E591"),sQuery(id+"F4.wireOp",EDGE,"E591"),sQuery(id+"F4.wireOp",EDGE,"E592"),sQuery(id+"F4.wireOp",EDGE,"E593"),sQuery(id+"F4.wireOp",EDGE,"E594"),sQuery(id+"F4.wireOp",EDGE,"E537")])]});
            var Q17;
            Q17=makeQuery(id+"F9.opExtrude","SWEPT_BODY",BODY,{"disambiguationData":[OSD([sQuery(id+"F4.wireOp",EDGE,"E595"),sQuery(id+"F4.wireOp",EDGE,"E596"),sQuery(id+"F4.wireOp",EDGE,"E597"),sQuery(id+"F4.wireOp",EDGE,"E598"),sQuery(id+"F4.wireOp",EDGE,"E599"),sQuery(id+"F4.wireOp",EDGE,"E600"),sQuery(id+"F4.wireOp",EDGE,"E601"),sQuery(id+"F4.wireOp",EDGE,"E602"),sQuery(id+"F4.wireOp",EDGE,"E603"),sQuery(id+"F4.wireOp",EDGE,"E604"),sQuery(id+"F4.wireOp",EDGE,"E605"),sQuery(id+"F4.wireOp",EDGE,"E606"),sQuery(id+"F4.wireOp",EDGE,"E607"),sQuery(id+"F4.wireOp",EDGE,"E608"),sQuery(id+"F4.wireOp",EDGE,"E609"),sQuery(id+"F4.wireOp",EDGE,"E610"),sQuery(id+"F4.wireOp",EDGE,"E610"),sQuery(id+"F4.wireOp",EDGE,"E611"),sQuery(id+"F4.wireOp",EDGE,"E612"),sQuery(id+"F4.wireOp",EDGE,"E613"),sQuery(id+"F4.wireOp",EDGE,"E614"),sQuery(id+"F4.wireOp",EDGE,"E615"),sQuery(id+"F4.wireOp",EDGE,"E615"),sQuery(id+"F4.wireOp",EDGE,"E616"),sQuery(id+"F4.wireOp",EDGE,"E617"),sQuery(id+"F4.wireOp",EDGE,"E618"),sQuery(id+"F4.wireOp",EDGE,"E619"),sQuery(id+"F4.wireOp",EDGE,"E619"),sQuery(id+"F4.wireOp",EDGE,"E620"),sQuery(id+"F4.wireOp",EDGE,"E621"),sQuery(id+"F4.wireOp",EDGE,"E622"),sQuery(id+"F4.wireOp",EDGE,"E623"),sQuery(id+"F4.wireOp",EDGE,"E624"),sQuery(id+"F4.wireOp",EDGE,"E625"),sQuery(id+"F4.wireOp",EDGE,"E626"),sQuery(id+"F4.wireOp",EDGE,"E627"),sQuery(id+"F4.wireOp",EDGE,"E628"),sQuery(id+"F4.wireOp",EDGE,"E629"),sQuery(id+"F4.wireOp",EDGE,"E630"),sQuery(id+"F4.wireOp",EDGE,"E631"),sQuery(id+"F4.wireOp",EDGE,"E632"),sQuery(id+"F4.wireOp",EDGE,"E633"),sQuery(id+"F4.wireOp",EDGE,"E634"),sQuery(id+"F4.wireOp",EDGE,"E635"),sQuery(id+"F4.wireOp",EDGE,"E636"),sQuery(id+"F4.wireOp",EDGE,"E637"),sQuery(id+"F4.wireOp",EDGE,"E637"),sQuery(id+"F4.wireOp",EDGE,"E638"),sQuery(id+"F4.wireOp",EDGE,"E639"),sQuery(id+"F4.wireOp",EDGE,"E640")])]});
            var Q18;
            Q18=makeQuery(id+"F9.opExtrude","SWEPT_BODY",BODY,{"disambiguationData":[OSD([sQuery(id+"F4.wireOp",EDGE,"E641"),sQuery(id+"F4.wireOp",EDGE,"E642"),sQuery(id+"F4.wireOp",EDGE,"E643"),sQuery(id+"F4.wireOp",EDGE,"E644"),sQuery(id+"F4.wireOp",EDGE,"E645"),sQuery(id+"F4.wireOp",EDGE,"E645"),sQuery(id+"F4.wireOp",EDGE,"E645"),sQuery(id+"F4.wireOp",EDGE,"E646"),sQuery(id+"F4.wireOp",EDGE,"E647"),sQuery(id+"F4.wireOp",EDGE,"E648"),sQuery(id+"F4.wireOp",EDGE,"E649"),sQuery(id+"F4.wireOp",EDGE,"E650"),sQuery(id+"F4.wireOp",EDGE,"E651"),sQuery(id+"F4.wireOp",EDGE,"E652"),sQuery(id+"F4.wireOp",EDGE,"E653"),sQuery(id+"F4.wireOp",EDGE,"E653"),sQuery(id+"F4.wireOp",EDGE,"E654"),sQuery(id+"F4.wireOp",EDGE,"E655"),sQuery(id+"F4.wireOp",EDGE,"E656"),sQuery(id+"F4.wireOp",EDGE,"E657"),sQuery(id+"F4.wireOp",EDGE,"E658"),sQuery(id+"F4.wireOp",EDGE,"E659"),sQuery(id+"F4.wireOp",EDGE,"E659"),sQuery(id+"F4.wireOp",EDGE,"E660"),sQuery(id+"F4.wireOp",EDGE,"E661"),sQuery(id+"F4.wireOp",EDGE,"E662"),sQuery(id+"F4.wireOp",EDGE,"E663"),sQuery(id+"F4.wireOp",EDGE,"E664"),sQuery(id+"F4.wireOp",EDGE,"E665"),sQuery(id+"F4.wireOp",EDGE,"E666"),sQuery(id+"F4.wireOp",EDGE,"E667"),sQuery(id+"F4.wireOp",EDGE,"E668"),sQuery(id+"F4.wireOp",EDGE,"E668"),sQuery(id+"F4.wireOp",EDGE,"E669"),sQuery(id+"F4.wireOp",EDGE,"E670"),sQuery(id+"F4.wireOp",EDGE,"E671"),sQuery(id+"F4.wireOp",EDGE,"E672"),sQuery(id+"F4.wireOp",EDGE,"E673"),sQuery(id+"F4.wireOp",EDGE,"E674"),sQuery(id+"F4.wireOp",EDGE,"E675"),sQuery(id+"F4.wireOp",EDGE,"E676"),sQuery(id+"F4.wireOp",EDGE,"E677"),sQuery(id+"F4.wireOp",EDGE,"E678"),sQuery(id+"F4.wireOp",EDGE,"E679"),sQuery(id+"F4.wireOp",EDGE,"E679"),sQuery(id+"F4.wireOp",EDGE,"E680"),sQuery(id+"F4.wireOp",EDGE,"E681"),sQuery(id+"F4.wireOp",EDGE,"E682"),sQuery(id+"F4.wireOp",EDGE,"E682"),sQuery(id+"F4.wireOp",EDGE,"E683"),sQuery(id+"F4.wireOp",EDGE,"E684"),sQuery(id+"F4.wireOp",EDGE,"E685"),sQuery(id+"F4.wireOp",EDGE,"E686"),sQuery(id+"F4.wireOp",EDGE,"E641")])]});
            var Q19;
            Q19=makeQuery(id+"F9.opExtrude","SWEPT_BODY",BODY,{"disambiguationData":[OSD([sQuery(id+"F4.wireOp",EDGE,"E687"),sQuery(id+"F4.wireOp",EDGE,"E688"),sQuery(id+"F4.wireOp",EDGE,"E689"),sQuery(id+"F4.wireOp",EDGE,"E690"),sQuery(id+"F4.wireOp",EDGE,"E691"),sQuery(id+"F4.wireOp",EDGE,"E692"),sQuery(id+"F4.wireOp",EDGE,"E693"),sQuery(id+"F4.wireOp",EDGE,"E694"),sQuery(id+"F4.wireOp",EDGE,"E695"),sQuery(id+"F4.wireOp",EDGE,"E696"),sQuery(id+"F4.wireOp",EDGE,"E697"),sQuery(id+"F4.wireOp",EDGE,"E698"),sQuery(id+"F4.wireOp",EDGE,"E699"),sQuery(id+"F4.wireOp",EDGE,"E700"),sQuery(id+"F4.wireOp",EDGE,"E701"),sQuery(id+"F4.wireOp",EDGE,"E702"),sQuery(id+"F4.wireOp",EDGE,"E703"),sQuery(id+"F4.wireOp",EDGE,"E704"),sQuery(id+"F4.wireOp",EDGE,"E705"),sQuery(id+"F4.wireOp",EDGE,"E706"),sQuery(id+"F4.wireOp",EDGE,"E707"),sQuery(id+"F4.wireOp",EDGE,"E708"),sQuery(id+"F4.wireOp",EDGE,"E709"),sQuery(id+"F4.wireOp",EDGE,"E709"),sQuery(id+"F4.wireOp",EDGE,"E709"),sQuery(id+"F4.wireOp",EDGE,"E710"),sQuery(id+"F4.wireOp",EDGE,"E711"),sQuery(id+"F4.wireOp",EDGE,"E712"),sQuery(id+"F4.wireOp",EDGE,"E713"),sQuery(id+"F4.wireOp",EDGE,"E714"),sQuery(id+"F4.wireOp",EDGE,"E715"),sQuery(id+"F4.wireOp",EDGE,"E716"),sQuery(id+"F4.wireOp",EDGE,"E717"),sQuery(id+"F4.wireOp",EDGE,"E718"),sQuery(id+"F4.wireOp",EDGE,"E719"),sQuery(id+"F4.wireOp",EDGE,"E720"),sQuery(id+"F4.wireOp",EDGE,"E721"),sQuery(id+"F4.wireOp",EDGE,"E722"),sQuery(id+"F4.wireOp",EDGE,"E723"),sQuery(id+"F4.wireOp",EDGE,"E724"),sQuery(id+"F4.wireOp",EDGE,"E725"),sQuery(id+"F4.wireOp",EDGE,"E726"),sQuery(id+"F4.wireOp",EDGE,"E727"),sQuery(id+"F4.wireOp",EDGE,"E728"),sQuery(id+"F4.wireOp",EDGE,"E729"),sQuery(id+"F4.wireOp",EDGE,"E730"),sQuery(id+"F4.wireOp",EDGE,"E731"),sQuery(id+"F4.wireOp",EDGE,"E732"),sQuery(id+"F4.wireOp",EDGE,"E732"),sQuery(id+"F4.wireOp",EDGE,"E733"),sQuery(id+"F4.wireOp",EDGE,"E734"),sQuery(id+"F4.wireOp",EDGE,"E735"),sQuery(id+"F4.wireOp",EDGE,"E736"),sQuery(id+"F4.wireOp",EDGE,"E737")])]});
            var Q20;
            Q20=makeQuery(id+"F9.opExtrude","SWEPT_BODY",BODY,{"disambiguationData":[OSD([sQuery(id+"F4.wireOp",EDGE,"E738"),sQuery(id+"F4.wireOp",EDGE,"E739"),sQuery(id+"F4.wireOp",EDGE,"E740"),sQuery(id+"F4.wireOp",EDGE,"E741"),sQuery(id+"F4.wireOp",EDGE,"E742"),sQuery(id+"F4.wireOp",EDGE,"E743"),sQuery(id+"F4.wireOp",EDGE,"E744"),sQuery(id+"F4.wireOp",EDGE,"E745"),sQuery(id+"F4.wireOp",EDGE,"E746"),sQuery(id+"F4.wireOp",EDGE,"E747"),sQuery(id+"F4.wireOp",EDGE,"E748"),sQuery(id+"F4.wireOp",EDGE,"E749"),sQuery(id+"F4.wireOp",EDGE,"E750"),sQuery(id+"F4.wireOp",EDGE,"E751"),sQuery(id+"F4.wireOp",EDGE,"E752"),sQuery(id+"F4.wireOp",EDGE,"E753"),sQuery(id+"F4.wireOp",EDGE,"E754"),sQuery(id+"F4.wireOp",EDGE,"E755"),sQuery(id+"F4.wireOp",EDGE,"E756"),sQuery(id+"F4.wireOp",EDGE,"E757"),sQuery(id+"F4.wireOp",EDGE,"E758"),sQuery(id+"F4.wireOp",EDGE,"E759"),sQuery(id+"F4.wireOp",EDGE,"E760"),sQuery(id+"F4.wireOp",EDGE,"E761"),sQuery(id+"F4.wireOp",EDGE,"E762"),sQuery(id+"F4.wireOp",EDGE,"E763"),sQuery(id+"F4.wireOp",EDGE,"E764"),sQuery(id+"F4.wireOp",EDGE,"E765"),sQuery(id+"F4.wireOp",EDGE,"E766"),sQuery(id+"F4.wireOp",EDGE,"E767"),sQuery(id+"F4.wireOp",EDGE,"E768"),sQuery(id+"F4.wireOp",EDGE,"E769"),sQuery(id+"F4.wireOp",EDGE,"E770"),sQuery(id+"F4.wireOp",EDGE,"E771"),sQuery(id+"F4.wireOp",EDGE,"E772"),sQuery(id+"F4.wireOp",EDGE,"E773"),sQuery(id+"F4.wireOp",EDGE,"E774"),sQuery(id+"F4.wireOp",EDGE,"E775"),sQuery(id+"F4.wireOp",EDGE,"E776"),sQuery(id+"F4.wireOp",EDGE,"E777"),sQuery(id+"F4.wireOp",EDGE,"E778"),sQuery(id+"F4.wireOp",EDGE,"E779"),sQuery(id+"F4.wireOp",EDGE,"E780"),sQuery(id+"F4.wireOp",EDGE,"E781"),sQuery(id+"F4.wireOp",EDGE,"E782"),sQuery(id+"F4.wireOp",EDGE,"E783"),sQuery(id+"F4.wireOp",EDGE,"E784"),sQuery(id+"F4.wireOp",EDGE,"E785"),sQuery(id+"F4.wireOp",EDGE,"E785"),sQuery(id+"F4.wireOp",EDGE,"E786"),sQuery(id+"F4.wireOp",EDGE,"E787"),sQuery(id+"F4.wireOp",EDGE,"E788"),sQuery(id+"F4.wireOp",EDGE,"E789"),sQuery(id+"F4.wireOp",EDGE,"E790"),sQuery(id+"F4.wireOp",EDGE,"E791"),sQuery(id+"F4.wireOp",EDGE,"E792"),sQuery(id+"F4.wireOp",EDGE,"E793"),sQuery(id+"F4.wireOp",EDGE,"E794"),sQuery(id+"F4.wireOp",EDGE,"E795"),sQuery(id+"F4.wireOp",EDGE,"E796"),sQuery(id+"F4.wireOp",EDGE,"E797"),sQuery(id+"F4.wireOp",EDGE,"E798"),sQuery(id+"F4.wireOp",EDGE,"E799"),sQuery(id+"F4.wireOp",EDGE,"E800"),sQuery(id+"F4.wireOp",EDGE,"E801"),sQuery(id+"F4.wireOp",EDGE,"E802"),sQuery(id+"F4.wireOp",EDGE,"E803"),sQuery(id+"F4.wireOp",EDGE,"E804"),sQuery(id+"F4.wireOp",EDGE,"E805"),sQuery(id+"F4.wireOp",EDGE,"E806"),sQuery(id+"F4.wireOp",EDGE,"E807"),sQuery(id+"F4.wireOp",EDGE,"E808"),sQuery(id+"F4.wireOp",EDGE,"E808"),sQuery(id+"F4.wireOp",EDGE,"E809"),sQuery(id+"F4.wireOp",EDGE,"E810"),sQuery(id+"F4.wireOp",EDGE,"E811"),sQuery(id+"F4.wireOp",EDGE,"E812"),sQuery(id+"F4.wireOp",EDGE,"E813"),sQuery(id+"F4.wireOp",EDGE,"E814"),sQuery(id+"F4.wireOp",EDGE,"E815"),sQuery(id+"F4.wireOp",EDGE,"E816"),sQuery(id+"F4.wireOp",EDGE,"E817"),sQuery(id+"F4.wireOp",EDGE,"E818"),sQuery(id+"F4.wireOp",EDGE,"E819"),sQuery(id+"F4.wireOp",EDGE,"E820"),sQuery(id+"F4.wireOp",EDGE,"E821"),sQuery(id+"F4.wireOp",EDGE,"E822"),sQuery(id+"F4.wireOp",EDGE,"E823"),sQuery(id+"F4.wireOp",EDGE,"E824"),sQuery(id+"F4.wireOp",EDGE,"E825"),sQuery(id+"F4.wireOp",EDGE,"E826"),sQuery(id+"F4.wireOp",EDGE,"E827"),sQuery(id+"F4.wireOp",EDGE,"E828"),sQuery(id+"F4.wireOp",EDGE,"E829"),sQuery(id+"F4.wireOp",EDGE,"E830"),sQuery(id+"F4.wireOp",EDGE,"E831"),sQuery(id+"F4.wireOp",EDGE,"E832"),sQuery(id+"F4.wireOp",EDGE,"E833"),sQuery(id+"F4.wireOp",EDGE,"E834"),sQuery(id+"F4.wireOp",EDGE,"E835"),sQuery(id+"F4.wireOp",EDGE,"E835"),sQuery(id+"F4.wireOp",EDGE,"E836"),sQuery(id+"F4.wireOp",EDGE,"E837"),sQuery(id+"F4.wireOp",EDGE,"E838"),sQuery(id+"F4.wireOp",EDGE,"E839"),sQuery(id+"F4.wireOp",EDGE,"E840"),sQuery(id+"F4.wireOp",EDGE,"E841"),sQuery(id+"F4.wireOp",EDGE,"E842"),sQuery(id+"F4.wireOp",EDGE,"E843"),sQuery(id+"F4.wireOp",EDGE,"E844"),sQuery(id+"F4.wireOp",EDGE,"E845"),sQuery(id+"F4.wireOp",EDGE,"E846"),sQuery(id+"F4.wireOp",EDGE,"E847"),sQuery(id+"F4.wireOp",EDGE,"E848"),sQuery(id+"F4.wireOp",EDGE,"E849"),sQuery(id+"F4.wireOp",EDGE,"E850"),sQuery(id+"F4.wireOp",EDGE,"E851"),sQuery(id+"F4.wireOp",EDGE,"E852"),sQuery(id+"F4.wireOp",EDGE,"E853"),sQuery(id+"F4.wireOp",EDGE,"E854"),sQuery(id+"F4.wireOp",EDGE,"E855"),sQuery(id+"F4.wireOp",EDGE,"E856"),sQuery(id+"F4.wireOp",EDGE,"E857"),sQuery(id+"F4.wireOp",EDGE,"E858"),sQuery(id+"F4.wireOp",EDGE,"E859"),sQuery(id+"F4.wireOp",EDGE,"E860"),sQuery(id+"F4.wireOp",EDGE,"E861"),sQuery(id+"F4.wireOp",EDGE,"E862"),sQuery(id+"F4.wireOp",EDGE,"E863"),sQuery(id+"F4.wireOp",EDGE,"E864"),sQuery(id+"F4.wireOp",EDGE,"E865"),sQuery(id+"F4.wireOp",EDGE,"E866"),sQuery(id+"F4.wireOp",EDGE,"E867"),sQuery(id+"F4.wireOp",EDGE,"E868"),sQuery(id+"F4.wireOp",EDGE,"E869"),sQuery(id+"F4.wireOp",EDGE,"E870"),sQuery(id+"F4.wireOp",EDGE,"E871"),sQuery(id+"F4.wireOp",EDGE,"E872"),sQuery(id+"F4.wireOp",EDGE,"E873"),sQuery(id+"F4.wireOp",EDGE,"E874"),sQuery(id+"F4.wireOp",EDGE,"E875"),sQuery(id+"F4.wireOp",EDGE,"E876"),sQuery(id+"F4.wireOp",EDGE,"E877"),sQuery(id+"F4.wireOp",EDGE,"E878")])]});
            var Q21;
            Q21=makeQuery(id+"F9.opExtrude","SWEPT_BODY",BODY,{"disambiguationData":[OSD([sQuery(id+"F4.wireOp",EDGE,"E879"),sQuery(id+"F4.wireOp",EDGE,"E879"),sQuery(id+"F4.wireOp",EDGE,"E880"),sQuery(id+"F4.wireOp",EDGE,"E881"),sQuery(id+"F4.wireOp",EDGE,"E882"),sQuery(id+"F4.wireOp",EDGE,"E883"),sQuery(id+"F4.wireOp",EDGE,"E884"),sQuery(id+"F4.wireOp",EDGE,"E885"),sQuery(id+"F4.wireOp",EDGE,"E886"),sQuery(id+"F4.wireOp",EDGE,"E887"),sQuery(id+"F4.wireOp",EDGE,"E888"),sQuery(id+"F4.wireOp",EDGE,"E889"),sQuery(id+"F4.wireOp",EDGE,"E890"),sQuery(id+"F4.wireOp",EDGE,"E891"),sQuery(id+"F4.wireOp",EDGE,"E892"),sQuery(id+"F4.wireOp",EDGE,"E893"),sQuery(id+"F4.wireOp",EDGE,"E893"),sQuery(id+"F4.wireOp",EDGE,"E894"),sQuery(id+"F4.wireOp",EDGE,"E895"),sQuery(id+"F4.wireOp",EDGE,"E896"),sQuery(id+"F4.wireOp",EDGE,"E897"),sQuery(id+"F4.wireOp",EDGE,"E898"),sQuery(id+"F4.wireOp",EDGE,"E899"),sQuery(id+"F4.wireOp",EDGE,"E900"),sQuery(id+"F4.wireOp",EDGE,"E901"),sQuery(id+"F4.wireOp",EDGE,"E902"),sQuery(id+"F4.wireOp",EDGE,"E903"),sQuery(id+"F4.wireOp",EDGE,"E904"),sQuery(id+"F4.wireOp",EDGE,"E904"),sQuery(id+"F4.wireOp",EDGE,"E905"),sQuery(id+"F4.wireOp",EDGE,"E906"),sQuery(id+"F4.wireOp",EDGE,"E907"),sQuery(id+"F4.wireOp",EDGE,"E908"),sQuery(id+"F4.wireOp",EDGE,"E909"),sQuery(id+"F4.wireOp",EDGE,"E910"),sQuery(id+"F4.wireOp",EDGE,"E911"),sQuery(id+"F4.wireOp",EDGE,"E912"),sQuery(id+"F4.wireOp",EDGE,"E913"),sQuery(id+"F4.wireOp",EDGE,"E914"),sQuery(id+"F4.wireOp",EDGE,"E915"),sQuery(id+"F4.wireOp",EDGE,"E916"),sQuery(id+"F4.wireOp",EDGE,"E917"),sQuery(id+"F4.wireOp",EDGE,"E918"),sQuery(id+"F4.wireOp",EDGE,"E919"),sQuery(id+"F4.wireOp",EDGE,"E920"),sQuery(id+"F4.wireOp",EDGE,"E921"),sQuery(id+"F4.wireOp",EDGE,"E922"),sQuery(id+"F4.wireOp",EDGE,"E923"),sQuery(id+"F4.wireOp",EDGE,"E923"),sQuery(id+"F4.wireOp",EDGE,"E924"),sQuery(id+"F4.wireOp",EDGE,"E925"),sQuery(id+"F4.wireOp",EDGE,"E926"),sQuery(id+"F4.wireOp",EDGE,"E927"),sQuery(id+"F4.wireOp",EDGE,"E928"),sQuery(id+"F4.wireOp",EDGE,"E929"),sQuery(id+"F4.wireOp",EDGE,"E930"),sQuery(id+"F4.wireOp",EDGE,"E931"),sQuery(id+"F4.wireOp",EDGE,"E932")])]});
            var Q22;
            Q22=makeQuery(id+"F9.opExtrude","SWEPT_BODY",BODY,{"disambiguationData":[OSD([sQuery(id+"F4.wireOp",EDGE,"E933"),sQuery(id+"F4.wireOp",EDGE,"E934"),sQuery(id+"F4.wireOp",EDGE,"E935"),sQuery(id+"F4.wireOp",EDGE,"E936"),sQuery(id+"F4.wireOp",EDGE,"E937"),sQuery(id+"F4.wireOp",EDGE,"E938"),sQuery(id+"F4.wireOp",EDGE,"E938"),sQuery(id+"F4.wireOp",EDGE,"E939"),sQuery(id+"F4.wireOp",EDGE,"E940"),sQuery(id+"F4.wireOp",EDGE,"E941"),sQuery(id+"F4.wireOp",EDGE,"E942"),sQuery(id+"F4.wireOp",EDGE,"E943"),sQuery(id+"F4.wireOp",EDGE,"E944"),sQuery(id+"F4.wireOp",EDGE,"E944"),sQuery(id+"F4.wireOp",EDGE,"E945"),sQuery(id+"F4.wireOp",EDGE,"E946"),sQuery(id+"F4.wireOp",EDGE,"E947"),sQuery(id+"F4.wireOp",EDGE,"E948"),sQuery(id+"F4.wireOp",EDGE,"E949"),sQuery(id+"F4.wireOp",EDGE,"E950"),sQuery(id+"F4.wireOp",EDGE,"E951"),sQuery(id+"F4.wireOp",EDGE,"E952"),sQuery(id+"F4.wireOp",EDGE,"E953"),sQuery(id+"F4.wireOp",EDGE,"E954"),sQuery(id+"F4.wireOp",EDGE,"E955"),sQuery(id+"F4.wireOp",EDGE,"E956"),sQuery(id+"F4.wireOp",EDGE,"E956"),sQuery(id+"F4.wireOp",EDGE,"E956"),sQuery(id+"F4.wireOp",EDGE,"E957"),sQuery(id+"F4.wireOp",EDGE,"E958"),sQuery(id+"F4.wireOp",EDGE,"E959"),sQuery(id+"F4.wireOp",EDGE,"E960"),sQuery(id+"F4.wireOp",EDGE,"E961"),sQuery(id+"F4.wireOp",EDGE,"E962"),sQuery(id+"F4.wireOp",EDGE,"E963"),sQuery(id+"F4.wireOp",EDGE,"E963"),sQuery(id+"F4.wireOp",EDGE,"E964"),sQuery(id+"F4.wireOp",EDGE,"E965"),sQuery(id+"F4.wireOp",EDGE,"E966"),sQuery(id+"F4.wireOp",EDGE,"E967"),sQuery(id+"F4.wireOp",EDGE,"E967"),sQuery(id+"F4.wireOp",EDGE,"E967"),sQuery(id+"F4.wireOp",EDGE,"E967"),sQuery(id+"F4.wireOp",EDGE,"E968"),sQuery(id+"F4.wireOp",EDGE,"E969"),sQuery(id+"F4.wireOp",EDGE,"E970"),sQuery(id+"F4.wireOp",EDGE,"E971"),sQuery(id+"F4.wireOp",EDGE,"E972"),sQuery(id+"F4.wireOp",EDGE,"E973"),sQuery(id+"F4.wireOp",EDGE,"E974"),sQuery(id+"F4.wireOp",EDGE,"E975"),sQuery(id+"F4.wireOp",EDGE,"E976"),sQuery(id+"F4.wireOp",EDGE,"E977"),sQuery(id+"F4.wireOp",EDGE,"E978"),sQuery(id+"F4.wireOp",EDGE,"E979"),sQuery(id+"F4.wireOp",EDGE,"E933")])]});
            var Q23;
            Q23=makeQuery(id+"F9.opExtrude","SWEPT_BODY",BODY,{"disambiguationData":[OSD([sQuery(id+"F4.wireOp",EDGE,"E980"),sQuery(id+"F4.wireOp",EDGE,"E981"),sQuery(id+"F4.wireOp",EDGE,"E982"),sQuery(id+"F4.wireOp",EDGE,"E983"),sQuery(id+"F4.wireOp",EDGE,"E984"),sQuery(id+"F4.wireOp",EDGE,"E985"),sQuery(id+"F4.wireOp",EDGE,"E985"),sQuery(id+"F4.wireOp",EDGE,"E986"),sQuery(id+"F4.wireOp",EDGE,"E987"),sQuery(id+"F4.wireOp",EDGE,"E988"),sQuery(id+"F4.wireOp",EDGE,"E989"),sQuery(id+"F4.wireOp",EDGE,"E990"),sQuery(id+"F4.wireOp",EDGE,"E991"),sQuery(id+"F4.wireOp",EDGE,"E992"),sQuery(id+"F4.wireOp",EDGE,"E993"),sQuery(id+"F4.wireOp",EDGE,"E994"),sQuery(id+"F4.wireOp",EDGE,"E995"),sQuery(id+"F4.wireOp",EDGE,"E996"),sQuery(id+"F4.wireOp",EDGE,"E997"),sQuery(id+"F4.wireOp",EDGE,"E998"),sQuery(id+"F4.wireOp",EDGE,"E999"),sQuery(id+"F4.wireOp",EDGE,"E1000"),sQuery(id+"F4.wireOp",EDGE,"E1001"),sQuery(id+"F4.wireOp",EDGE,"E1002"),sQuery(id+"F4.wireOp",EDGE,"E1003"),sQuery(id+"F4.wireOp",EDGE,"E1004"),sQuery(id+"F4.wireOp",EDGE,"E1005"),sQuery(id+"F4.wireOp",EDGE,"E1006"),sQuery(id+"F4.wireOp",EDGE,"E1007"),sQuery(id+"F4.wireOp",EDGE,"E1008"),sQuery(id+"F4.wireOp",EDGE,"E1009"),sQuery(id+"F4.wireOp",EDGE,"E1010"),sQuery(id+"F4.wireOp",EDGE,"E1010"),sQuery(id+"F4.wireOp",EDGE,"E1011"),sQuery(id+"F4.wireOp",EDGE,"E1012"),sQuery(id+"F4.wireOp",EDGE,"E1013"),sQuery(id+"F4.wireOp",EDGE,"E1014"),sQuery(id+"F4.wireOp",EDGE,"E1015"),sQuery(id+"F4.wireOp",EDGE,"E1015"),sQuery(id+"F4.wireOp",EDGE,"E1016"),sQuery(id+"F4.wireOp",EDGE,"E1017"),sQuery(id+"F4.wireOp",EDGE,"E1018"),sQuery(id+"F4.wireOp",EDGE,"E1019"),sQuery(id+"F4.wireOp",EDGE,"E1020"),sQuery(id+"F4.wireOp",EDGE,"E1020"),sQuery(id+"F4.wireOp",EDGE,"E1020"),sQuery(id+"F4.wireOp",EDGE,"E1020"),sQuery(id+"F4.wireOp",EDGE,"E1021"),sQuery(id+"F4.wireOp",EDGE,"E1022"),sQuery(id+"F4.wireOp",EDGE,"E1023"),sQuery(id+"F4.wireOp",EDGE,"E1024"),sQuery(id+"F4.wireOp",EDGE,"E1025"),sQuery(id+"F4.wireOp",EDGE,"E1026"),sQuery(id+"F4.wireOp",EDGE,"E1027"),sQuery(id+"F4.wireOp",EDGE,"E1028"),sQuery(id+"F4.wireOp",EDGE,"E1029"),sQuery(id+"F4.wireOp",EDGE,"E1030"),sQuery(id+"F4.wireOp",EDGE,"E1031"),sQuery(id+"F4.wireOp",EDGE,"E1032"),sQuery(id+"F4.wireOp",EDGE,"E980")])]});
            var Q24;
            Q24=makeQuery(id+"F9.opExtrude","SWEPT_BODY",BODY,{"disambiguationData":[OSD([sQuery(id+"F4.wireOp",EDGE,"E1033"),sQuery(id+"F4.wireOp",EDGE,"E1034"),sQuery(id+"F4.wireOp",EDGE,"E1035"),sQuery(id+"F4.wireOp",EDGE,"E1036"),sQuery(id+"F4.wireOp",EDGE,"E1037"),sQuery(id+"F4.wireOp",EDGE,"E1038"),sQuery(id+"F4.wireOp",EDGE,"E1039"),sQuery(id+"F4.wireOp",EDGE,"E1040"),sQuery(id+"F4.wireOp",EDGE,"E1041"),sQuery(id+"F4.wireOp",EDGE,"E1042"),sQuery(id+"F4.wireOp",EDGE,"E1043"),sQuery(id+"F4.wireOp",EDGE,"E1044"),sQuery(id+"F4.wireOp",EDGE,"E1045"),sQuery(id+"F4.wireOp",EDGE,"E1046"),sQuery(id+"F4.wireOp",EDGE,"E1047"),sQuery(id+"F4.wireOp",EDGE,"E1048"),sQuery(id+"F4.wireOp",EDGE,"E1049"),sQuery(id+"F4.wireOp",EDGE,"E1050"),sQuery(id+"F4.wireOp",EDGE,"E1051"),sQuery(id+"F4.wireOp",EDGE,"E1052"),sQuery(id+"F4.wireOp",EDGE,"E1052"),sQuery(id+"F4.wireOp",EDGE,"E1053"),sQuery(id+"F4.wireOp",EDGE,"E1054"),sQuery(id+"F4.wireOp",EDGE,"E1055"),sQuery(id+"F4.wireOp",EDGE,"E1056"),sQuery(id+"F4.wireOp",EDGE,"E1056"),sQuery(id+"F4.wireOp",EDGE,"E1057"),sQuery(id+"F4.wireOp",EDGE,"E1058"),sQuery(id+"F4.wireOp",EDGE,"E1059"),sQuery(id+"F4.wireOp",EDGE,"E1060"),sQuery(id+"F4.wireOp",EDGE,"E1061"),sQuery(id+"F4.wireOp",EDGE,"E1062"),sQuery(id+"F4.wireOp",EDGE,"E1063"),sQuery(id+"F4.wireOp",EDGE,"E1064"),sQuery(id+"F4.wireOp",EDGE,"E1065"),sQuery(id+"F4.wireOp",EDGE,"E1065"),sQuery(id+"F4.wireOp",EDGE,"E1066"),sQuery(id+"F4.wireOp",EDGE,"E1067"),sQuery(id+"F4.wireOp",EDGE,"E1068"),sQuery(id+"F4.wireOp",EDGE,"E1069"),sQuery(id+"F4.wireOp",EDGE,"E1070"),sQuery(id+"F4.wireOp",EDGE,"E1071"),sQuery(id+"F4.wireOp",EDGE,"E1072"),sQuery(id+"F4.wireOp",EDGE,"E1073"),sQuery(id+"F4.wireOp",EDGE,"E1074"),sQuery(id+"F4.wireOp",EDGE,"E1075"),sQuery(id+"F4.wireOp",EDGE,"E1076"),sQuery(id+"F4.wireOp",EDGE,"E1033")])]});
            var Q25;
            Q25=makeQuery(id+"F9.opExtrude","SWEPT_BODY",BODY,{"disambiguationData":[OSD([sQuery(id+"F4.wireOp",EDGE,"E1077"),sQuery(id+"F4.wireOp",EDGE,"E1078"),sQuery(id+"F4.wireOp",EDGE,"E1079"),sQuery(id+"F4.wireOp",EDGE,"E1080"),sQuery(id+"F4.wireOp",EDGE,"E1081"),sQuery(id+"F4.wireOp",EDGE,"E1082"),sQuery(id+"F4.wireOp",EDGE,"E1083"),sQuery(id+"F4.wireOp",EDGE,"E1084"),sQuery(id+"F4.wireOp",EDGE,"E1085"),sQuery(id+"F4.wireOp",EDGE,"E1086"),sQuery(id+"F4.wireOp",EDGE,"E1086"),sQuery(id+"F4.wireOp",EDGE,"E1087"),sQuery(id+"F4.wireOp",EDGE,"E1088"),sQuery(id+"F4.wireOp",EDGE,"E1089"),sQuery(id+"F4.wireOp",EDGE,"E1090"),sQuery(id+"F4.wireOp",EDGE,"E1091"),sQuery(id+"F4.wireOp",EDGE,"E1092"),sQuery(id+"F4.wireOp",EDGE,"E1093"),sQuery(id+"F4.wireOp",EDGE,"E1094"),sQuery(id+"F4.wireOp",EDGE,"E1095"),sQuery(id+"F4.wireOp",EDGE,"E1095"),sQuery(id+"F4.wireOp",EDGE,"E1096"),sQuery(id+"F4.wireOp",EDGE,"E1097"),sQuery(id+"F4.wireOp",EDGE,"E1098"),sQuery(id+"F4.wireOp",EDGE,"E1099"),sQuery(id+"F4.wireOp",EDGE,"E1100"),sQuery(id+"F4.wireOp",EDGE,"E1101"),sQuery(id+"F4.wireOp",EDGE,"E1102"),sQuery(id+"F4.wireOp",EDGE,"E1103"),sQuery(id+"F4.wireOp",EDGE,"E1104"),sQuery(id+"F4.wireOp",EDGE,"E1105"),sQuery(id+"F4.wireOp",EDGE,"E1105"),sQuery(id+"F4.wireOp",EDGE,"E1106"),sQuery(id+"F4.wireOp",EDGE,"E1107"),sQuery(id+"F4.wireOp",EDGE,"E1108"),sQuery(id+"F4.wireOp",EDGE,"E1109"),sQuery(id+"F4.wireOp",EDGE,"E1110"),sQuery(id+"F4.wireOp",EDGE,"E1111"),sQuery(id+"F4.wireOp",EDGE,"E1112"),sQuery(id+"F4.wireOp",EDGE,"E1113"),sQuery(id+"F4.wireOp",EDGE,"E1114"),sQuery(id+"F4.wireOp",EDGE,"E1115"),sQuery(id+"F4.wireOp",EDGE,"E1116"),sQuery(id+"F4.wireOp",EDGE,"E1117"),sQuery(id+"F4.wireOp",EDGE,"E1118"),sQuery(id+"F4.wireOp",EDGE,"E1119"),sQuery(id+"F4.wireOp",EDGE,"E1120"),sQuery(id+"F4.wireOp",EDGE,"E1121"),sQuery(id+"F4.wireOp",EDGE,"E1122"),sQuery(id+"F4.wireOp",EDGE,"E1123"),sQuery(id+"F4.wireOp",EDGE,"E1124"),sQuery(id+"F4.wireOp",EDGE,"E1125")])]});
            var Q26;
            Q26=makeQuery(id+"F9.opExtrude","SWEPT_BODY",BODY,{"disambiguationData":[OSD([sQuery(id+"F4.wireOp",EDGE,"E1126"),sQuery(id+"F4.wireOp",EDGE,"E1126"),sQuery(id+"F4.wireOp",EDGE,"E1127"),sQuery(id+"F4.wireOp",EDGE,"E1128"),sQuery(id+"F4.wireOp",EDGE,"E1128"),sQuery(id+"F4.wireOp",EDGE,"E1128"),sQuery(id+"F4.wireOp",EDGE,"E1129"),sQuery(id+"F4.wireOp",EDGE,"E1130"),sQuery(id+"F4.wireOp",EDGE,"E1131"),sQuery(id+"F4.wireOp",EDGE,"E1132"),sQuery(id+"F4.wireOp",EDGE,"E1133"),sQuery(id+"F4.wireOp",EDGE,"E1134"),sQuery(id+"F4.wireOp",EDGE,"E1135"),sQuery(id+"F4.wireOp",EDGE,"E1136"),sQuery(id+"F4.wireOp",EDGE,"E1137"),sQuery(id+"F4.wireOp",EDGE,"E1138"),sQuery(id+"F4.wireOp",EDGE,"E1139"),sQuery(id+"F4.wireOp",EDGE,"E1139"),sQuery(id+"F4.wireOp",EDGE,"E1139"),sQuery(id+"F4.wireOp",EDGE,"E1140"),sQuery(id+"F4.wireOp",EDGE,"E1141"),sQuery(id+"F4.wireOp",EDGE,"E1141"),sQuery(id+"F4.wireOp",EDGE,"E1142"),sQuery(id+"F4.wireOp",EDGE,"E1143"),sQuery(id+"F4.wireOp",EDGE,"E1144"),sQuery(id+"F4.wireOp",EDGE,"E1145"),sQuery(id+"F4.wireOp",EDGE,"E1146"),sQuery(id+"F4.wireOp",EDGE,"E1147"),sQuery(id+"F4.wireOp",EDGE,"E1147"),sQuery(id+"F4.wireOp",EDGE,"E1148"),sQuery(id+"F4.wireOp",EDGE,"E1149"),sQuery(id+"F4.wireOp",EDGE,"E1150"),sQuery(id+"F4.wireOp",EDGE,"E1151"),sQuery(id+"F4.wireOp",EDGE,"E1152"),sQuery(id+"F4.wireOp",EDGE,"E1153"),sQuery(id+"F4.wireOp",EDGE,"E1154"),sQuery(id+"F4.wireOp",EDGE,"E1155"),sQuery(id+"F4.wireOp",EDGE,"E1156"),sQuery(id+"F4.wireOp",EDGE,"E1157"),sQuery(id+"F4.wireOp",EDGE,"E1158"),sQuery(id+"F4.wireOp",EDGE,"E1159"),sQuery(id+"F4.wireOp",EDGE,"E1160"),sQuery(id+"F4.wireOp",EDGE,"E1161"),sQuery(id+"F4.wireOp",EDGE,"E1162"),sQuery(id+"F4.wireOp",EDGE,"E1162"),sQuery(id+"F4.wireOp",EDGE,"E1162"),sQuery(id+"F4.wireOp",EDGE,"E1163"),sQuery(id+"F4.wireOp",EDGE,"E1164"),sQuery(id+"F4.wireOp",EDGE,"E1165"),sQuery(id+"F4.wireOp",EDGE,"E1166"),sQuery(id+"F4.wireOp",EDGE,"E1167"),sQuery(id+"F4.wireOp",EDGE,"E1168"),sQuery(id+"F4.wireOp",EDGE,"E1169"),sQuery(id+"F4.wireOp",EDGE,"E1170"),sQuery(id+"F4.wireOp",EDGE,"E1171"),sQuery(id+"F4.wireOp",EDGE,"E1172")])]});
            var Q27;
            Q27=makeQuery(id+"F9.opExtrude","SWEPT_BODY",BODY,{"disambiguationData":[OSD([sQuery(id+"F4.wireOp",EDGE,"E1173"),sQuery(id+"F4.wireOp",EDGE,"E1173"),sQuery(id+"F4.wireOp",EDGE,"E1174"),sQuery(id+"F4.wireOp",EDGE,"E1175"),sQuery(id+"F4.wireOp",EDGE,"E1176"),sQuery(id+"F4.wireOp",EDGE,"E1176"),sQuery(id+"F4.wireOp",EDGE,"E1177"),sQuery(id+"F4.wireOp",EDGE,"E1178"),sQuery(id+"F4.wireOp",EDGE,"E1179"),sQuery(id+"F4.wireOp",EDGE,"E1180"),sQuery(id+"F4.wireOp",EDGE,"E1181"),sQuery(id+"F4.wireOp",EDGE,"E1182"),sQuery(id+"F4.wireOp",EDGE,"E1183"),sQuery(id+"F4.wireOp",EDGE,"E1183"),sQuery(id+"F4.wireOp",EDGE,"E1184"),sQuery(id+"F4.wireOp",EDGE,"E1185"),sQuery(id+"F4.wireOp",EDGE,"E1186"),sQuery(id+"F4.wireOp",EDGE,"E1187"),sQuery(id+"F4.wireOp",EDGE,"E1188"),sQuery(id+"F4.wireOp",EDGE,"E1189"),sQuery(id+"F4.wireOp",EDGE,"E1190"),sQuery(id+"F4.wireOp",EDGE,"E1191"),sQuery(id+"F4.wireOp",EDGE,"E1192"),sQuery(id+"F4.wireOp",EDGE,"E1193"),sQuery(id+"F4.wireOp",EDGE,"E1194"),sQuery(id+"F4.wireOp",EDGE,"E1195"),sQuery(id+"F4.wireOp",EDGE,"E1196"),sQuery(id+"F4.wireOp",EDGE,"E1197"),sQuery(id+"F4.wireOp",EDGE,"E1198"),sQuery(id+"F4.wireOp",EDGE,"E1199"),sQuery(id+"F4.wireOp",EDGE,"E1200"),sQuery(id+"F4.wireOp",EDGE,"E1201"),sQuery(id+"F4.wireOp",EDGE,"E1202"),sQuery(id+"F4.wireOp",EDGE,"E1202"),sQuery(id+"F4.wireOp",EDGE,"E1203"),sQuery(id+"F4.wireOp",EDGE,"E1204"),sQuery(id+"F4.wireOp",EDGE,"E1205"),sQuery(id+"F4.wireOp",EDGE,"E1206"),sQuery(id+"F4.wireOp",EDGE,"E1207"),sQuery(id+"F4.wireOp",EDGE,"E1208"),sQuery(id+"F4.wireOp",EDGE,"E1209"),sQuery(id+"F4.wireOp",EDGE,"E1210"),sQuery(id+"F4.wireOp",EDGE,"E1211"),sQuery(id+"F4.wireOp",EDGE,"E1212"),sQuery(id+"F4.wireOp",EDGE,"E1213"),sQuery(id+"F4.wireOp",EDGE,"E1214"),sQuery(id+"F4.wireOp",EDGE,"E1215"),sQuery(id+"F4.wireOp",EDGE,"E1216"),sQuery(id+"F4.wireOp",EDGE,"E1217"),sQuery(id+"F4.wireOp",EDGE,"E1218"),sQuery(id+"F4.wireOp",EDGE,"E1173"),sQuery(id+"F4.wireOp",EDGE,"E1173")])]});
            var Q28;
            Q28=makeQuery(id+"F9.opExtrude","SWEPT_BODY",BODY,{"disambiguationData":[OSD([sQuery(id+"F4.wireOp",EDGE,"E1219"),sQuery(id+"F4.wireOp",EDGE,"E1220"),sQuery(id+"F4.wireOp",EDGE,"E1221"),sQuery(id+"F4.wireOp",EDGE,"E1222"),sQuery(id+"F4.wireOp",EDGE,"E1223"),sQuery(id+"F4.wireOp",EDGE,"E1224"),sQuery(id+"F4.wireOp",EDGE,"E1224"),sQuery(id+"F4.wireOp",EDGE,"E1224"),sQuery(id+"F4.wireOp",EDGE,"E1225"),sQuery(id+"F4.wireOp",EDGE,"E1226"),sQuery(id+"F4.wireOp",EDGE,"E1227"),sQuery(id+"F4.wireOp",EDGE,"E1228"),sQuery(id+"F4.wireOp",EDGE,"E1229"),sQuery(id+"F4.wireOp",EDGE,"E1230"),sQuery(id+"F4.wireOp",EDGE,"E1231"),sQuery(id+"F4.wireOp",EDGE,"E1232"),sQuery(id+"F4.wireOp",EDGE,"E1232"),sQuery(id+"F4.wireOp",EDGE,"E1233"),sQuery(id+"F4.wireOp",EDGE,"E1234"),sQuery(id+"F4.wireOp",EDGE,"E1235"),sQuery(id+"F4.wireOp",EDGE,"E1236"),sQuery(id+"F4.wireOp",EDGE,"E1237"),sQuery(id+"F4.wireOp",EDGE,"E1238"),sQuery(id+"F4.wireOp",EDGE,"E1239"),sQuery(id+"F4.wireOp",EDGE,"E1240"),sQuery(id+"F4.wireOp",EDGE,"E1241"),sQuery(id+"F4.wireOp",EDGE,"E1242"),sQuery(id+"F4.wireOp",EDGE,"E1243"),sQuery(id+"F4.wireOp",EDGE,"E1244"),sQuery(id+"F4.wireOp",EDGE,"E1245"),sQuery(id+"F4.wireOp",EDGE,"E1246"),sQuery(id+"F4.wireOp",EDGE,"E1247"),sQuery(id+"F4.wireOp",EDGE,"E1248"),sQuery(id+"F4.wireOp",EDGE,"E1249"),sQuery(id+"F4.wireOp",EDGE,"E1250"),sQuery(id+"F4.wireOp",EDGE,"E1251"),sQuery(id+"F4.wireOp",EDGE,"E1252"),sQuery(id+"F4.wireOp",EDGE,"E1253"),sQuery(id+"F4.wireOp",EDGE,"E1253"),sQuery(id+"F4.wireOp",EDGE,"E1253"),sQuery(id+"F4.wireOp",EDGE,"E1254"),sQuery(id+"F4.wireOp",EDGE,"E1255"),sQuery(id+"F4.wireOp",EDGE,"E1256"),sQuery(id+"F4.wireOp",EDGE,"E1257"),sQuery(id+"F4.wireOp",EDGE,"E1258"),sQuery(id+"F4.wireOp",EDGE,"E1259"),sQuery(id+"F4.wireOp",EDGE,"E1260"),sQuery(id+"F4.wireOp",EDGE,"E1261"),sQuery(id+"F4.wireOp",EDGE,"E1262"),sQuery(id+"F4.wireOp",EDGE,"E1263"),sQuery(id+"F4.wireOp",EDGE,"E1264"),sQuery(id+"F4.wireOp",EDGE,"E1265"),sQuery(id+"F4.wireOp",EDGE,"E1266"),sQuery(id+"F4.wireOp",EDGE,"E1267"),sQuery(id+"F4.wireOp",EDGE,"E1267"),sQuery(id+"F4.wireOp",EDGE,"E1268"),sQuery(id+"F4.wireOp",EDGE,"E1269"),sQuery(id+"F4.wireOp",EDGE,"E1270"),sQuery(id+"F4.wireOp",EDGE,"E1271"),sQuery(id+"F4.wireOp",EDGE,"E1272")])]});
            var Q29;
            Q29=makeQuery(id+"F10.opExtrude","SWEPT_BODY",BODY,{"disambiguationData":[OSD([sQuery(id+"F5.wireOp",EDGE,"E1273"),sQuery(id+"F5.wireOp",EDGE,"E1274"),sQuery(id+"F5.wireOp",EDGE,"E1275"),sQuery(id+"F5.wireOp",EDGE,"E1276"),sQuery(id+"F5.wireOp",EDGE,"E1277"),sQuery(id+"F5.wireOp",EDGE,"E1278"),sQuery(id+"F5.wireOp",EDGE,"E1279"),sQuery(id+"F5.wireOp",EDGE,"E1280"),sQuery(id+"F5.wireOp",EDGE,"E1281"),sQuery(id+"F5.wireOp",EDGE,"E1282"),sQuery(id+"F5.wireOp",EDGE,"E1283"),sQuery(id+"F5.wireOp",EDGE,"E1284"),sQuery(id+"F5.wireOp",EDGE,"E1285"),sQuery(id+"F5.wireOp",EDGE,"E1286"),sQuery(id+"F5.wireOp",EDGE,"E1287"),sQuery(id+"F5.wireOp",EDGE,"E1288"),sQuery(id+"F5.wireOp",EDGE,"E1289"),sQuery(id+"F5.wireOp",EDGE,"E1290"),sQuery(id+"F5.wireOp",EDGE,"E1291"),sQuery(id+"F5.wireOp",EDGE,"E1292"),sQuery(id+"F5.wireOp",EDGE,"E1293"),sQuery(id+"F5.wireOp",EDGE,"E1294"),sQuery(id+"F5.wireOp",EDGE,"E1295"),sQuery(id+"F5.wireOp",EDGE,"E1296"),sQuery(id+"F5.wireOp",EDGE,"E1297"),sQuery(id+"F5.wireOp",EDGE,"E1298"),sQuery(id+"F5.wireOp",EDGE,"E1299"),sQuery(id+"F5.wireOp",EDGE,"E1300"),sQuery(id+"F5.wireOp",EDGE,"E1301"),sQuery(id+"F5.wireOp",EDGE,"E1302"),sQuery(id+"F5.wireOp",EDGE,"E1303"),sQuery(id+"F5.wireOp",EDGE,"E1304"),sQuery(id+"F5.wireOp",EDGE,"E1305"),sQuery(id+"F5.wireOp",EDGE,"E1306"),sQuery(id+"F5.wireOp",EDGE,"E1307"),sQuery(id+"F5.wireOp",EDGE,"E1308"),sQuery(id+"F5.wireOp",EDGE,"E1309"),sQuery(id+"F5.wireOp",EDGE,"E1310"),sQuery(id+"F5.wireOp",EDGE,"E1311"),sQuery(id+"F5.wireOp",EDGE,"E1312"),sQuery(id+"F5.wireOp",EDGE,"E1313"),sQuery(id+"F5.wireOp",EDGE,"E1314"),sQuery(id+"F5.wireOp",EDGE,"E1315"),sQuery(id+"F5.wireOp",EDGE,"E1316"),sQuery(id+"F5.wireOp",EDGE,"E1317"),sQuery(id+"F5.wireOp",EDGE,"E1318"),sQuery(id+"F5.wireOp",EDGE,"E1319"),sQuery(id+"F5.wireOp",EDGE,"E1320"),sQuery(id+"F5.wireOp",EDGE,"E1321"),sQuery(id+"F5.wireOp",EDGE,"E1322"),sQuery(id+"F5.wireOp",EDGE,"E1323"),sQuery(id+"F5.wireOp",EDGE,"E1324"),sQuery(id+"F5.wireOp",EDGE,"E1325"),sQuery(id+"F5.wireOp",EDGE,"E1326"),sQuery(id+"F5.wireOp",EDGE,"E1327"),sQuery(id+"F5.wireOp",EDGE,"E1328"),sQuery(id+"F5.wireOp",EDGE,"E1329"),sQuery(id+"F5.wireOp",EDGE,"E1330"),sQuery(id+"F5.wireOp",EDGE,"E1331"),sQuery(id+"F5.wireOp",EDGE,"E1332"),sQuery(id+"F5.wireOp",EDGE,"E1333"),sQuery(id+"F5.wireOp",EDGE,"E1334"),sQuery(id+"F5.wireOp",EDGE,"E1335"),sQuery(id+"F5.wireOp",EDGE,"E1336"),sQuery(id+"F5.wireOp",EDGE,"E1337"),sQuery(id+"F5.wireOp",EDGE,"E1338"),sQuery(id+"F5.wireOp",EDGE,"E1339"),sQuery(id+"F5.wireOp",EDGE,"E1340"),sQuery(id+"F5.wireOp",EDGE,"E1341"),sQuery(id+"F5.wireOp",EDGE,"E1342"),sQuery(id+"F5.wireOp",EDGE,"E1343"),sQuery(id+"F5.wireOp",EDGE,"E1343"),sQuery(id+"F5.wireOp",EDGE,"E1344"),sQuery(id+"F5.wireOp",EDGE,"E1345"),sQuery(id+"F5.wireOp",EDGE,"E1345"),sQuery(id+"F5.wireOp",EDGE,"E1346"),sQuery(id+"F5.wireOp",EDGE,"E1347"),sQuery(id+"F5.wireOp",EDGE,"E1348"),sQuery(id+"F5.wireOp",EDGE,"E1349"),sQuery(id+"F5.wireOp",EDGE,"E1349"),sQuery(id+"F5.wireOp",EDGE,"E1350"),sQuery(id+"F5.wireOp",EDGE,"E1351"),sQuery(id+"F5.wireOp",EDGE,"E1352"),sQuery(id+"F5.wireOp",EDGE,"E1353"),sQuery(id+"F5.wireOp",EDGE,"E1354"),sQuery(id+"F5.wireOp",EDGE,"E1355"),sQuery(id+"F5.wireOp",EDGE,"E1355"),sQuery(id+"F5.wireOp",EDGE,"E1355"),sQuery(id+"F5.wireOp",EDGE,"E1356"),sQuery(id+"F5.wireOp",EDGE,"E1357"),sQuery(id+"F5.wireOp",EDGE,"E1358"),sQuery(id+"F5.wireOp",EDGE,"E1359"),sQuery(id+"F5.wireOp",EDGE,"E1360"),sQuery(id+"F5.wireOp",EDGE,"E1361"),sQuery(id+"F5.wireOp",EDGE,"E1362"),sQuery(id+"F5.wireOp",EDGE,"E1363"),sQuery(id+"F5.wireOp",EDGE,"E1364"),sQuery(id+"F5.wireOp",EDGE,"E1365"),sQuery(id+"F5.wireOp",EDGE,"E1366"),sQuery(id+"F5.wireOp",EDGE,"E1367"),sQuery(id+"F5.wireOp",EDGE,"E1368"),sQuery(id+"F5.wireOp",EDGE,"E1369"),sQuery(id+"F5.wireOp",EDGE,"E1370"),sQuery(id+"F5.wireOp",EDGE,"E1371"),sQuery(id+"F5.wireOp",EDGE,"E1372"),sQuery(id+"F5.wireOp",EDGE,"E1373"),sQuery(id+"F5.wireOp",EDGE,"E1374"),sQuery(id+"F5.wireOp",EDGE,"E1375"),sQuery(id+"F5.wireOp",EDGE,"E1376"),sQuery(id+"F5.wireOp",EDGE,"E1377"),sQuery(id+"F5.wireOp",EDGE,"E1378"),sQuery(id+"F5.wireOp",EDGE,"E1379"),sQuery(id+"F5.wireOp",EDGE,"E1380"),sQuery(id+"F5.wireOp",EDGE,"E1381"),sQuery(id+"F5.wireOp",EDGE,"E1382"),sQuery(id+"F5.wireOp",EDGE,"E1383"),sQuery(id+"F5.wireOp",EDGE,"E1384"),sQuery(id+"F5.wireOp",EDGE,"E1385"),sQuery(id+"F5.wireOp",EDGE,"E1386"),sQuery(id+"F5.wireOp",EDGE,"E1387"),sQuery(id+"F5.wireOp",EDGE,"E1388"),sQuery(id+"F5.wireOp",EDGE,"E1389"),sQuery(id+"F5.wireOp",EDGE,"E1390"),sQuery(id+"F5.wireOp",EDGE,"E1391"),sQuery(id+"F5.wireOp",EDGE,"E1392"),sQuery(id+"F5.wireOp",EDGE,"E1393"),sQuery(id+"F5.wireOp",EDGE,"E1394"),sQuery(id+"F5.wireOp",EDGE,"E1395"),sQuery(id+"F5.wireOp",EDGE,"E1396"),sQuery(id+"F5.wireOp",EDGE,"E1397"),sQuery(id+"F5.wireOp",EDGE,"E1398"),sQuery(id+"F5.wireOp",EDGE,"E1399"),sQuery(id+"F5.wireOp",EDGE,"E1400"),sQuery(id+"F5.wireOp",EDGE,"E1401"),sQuery(id+"F5.wireOp",EDGE,"E1402"),sQuery(id+"F5.wireOp",EDGE,"E1403"),sQuery(id+"F5.wireOp",EDGE,"E1404"),sQuery(id+"F5.wireOp",EDGE,"E1405"),sQuery(id+"F5.wireOp",EDGE,"E1406"),sQuery(id+"F5.wireOp",EDGE,"E1407"),sQuery(id+"F5.wireOp",EDGE,"E1408"),sQuery(id+"F5.wireOp",EDGE,"E1408"),sQuery(id+"F5.wireOp",EDGE,"E1408"),sQuery(id+"F5.wireOp",EDGE,"E1409"),sQuery(id+"F5.wireOp",EDGE,"E1410"),sQuery(id+"F5.wireOp",EDGE,"E1411"),sQuery(id+"F5.wireOp",EDGE,"E1412"),sQuery(id+"F5.wireOp",EDGE,"E1413"),sQuery(id+"F5.wireOp",EDGE,"E1414"),sQuery(id+"F5.wireOp",EDGE,"E1414"),sQuery(id+"F5.wireOp",EDGE,"E1414"),sQuery(id+"F5.wireOp",EDGE,"E1415"),sQuery(id+"F5.wireOp",EDGE,"E1416"),sQuery(id+"F5.wireOp",EDGE,"E1417"),sQuery(id+"F5.wireOp",EDGE,"E1417"),sQuery(id+"F5.wireOp",EDGE,"E1417"),sQuery(id+"F5.wireOp",EDGE,"E1418"),sQuery(id+"F5.wireOp",EDGE,"E1419"),sQuery(id+"F5.wireOp",EDGE,"E1420"),sQuery(id+"F5.wireOp",EDGE,"E1421"),sQuery(id+"F5.wireOp",EDGE,"E1422"),sQuery(id+"F5.wireOp",EDGE,"E1423"),sQuery(id+"F5.wireOp",EDGE,"E1424"),sQuery(id+"F5.wireOp",EDGE,"E1425"),sQuery(id+"F5.wireOp",EDGE,"E1426"),sQuery(id+"F5.wireOp",EDGE,"E1427"),sQuery(id+"F5.wireOp",EDGE,"E1428"),sQuery(id+"F5.wireOp",EDGE,"E1429"),sQuery(id+"F5.wireOp",EDGE,"E1430"),sQuery(id+"F5.wireOp",EDGE,"E1431"),sQuery(id+"F5.wireOp",EDGE,"E1432"),sQuery(id+"F5.wireOp",EDGE,"E1433"),sQuery(id+"F5.wireOp",EDGE,"E1434"),sQuery(id+"F5.wireOp",EDGE,"E1435"),sQuery(id+"F5.wireOp",EDGE,"E1436"),sQuery(id+"F5.wireOp",EDGE,"E1437"),sQuery(id+"F5.wireOp",EDGE,"E1438"),sQuery(id+"F5.wireOp",EDGE,"E1439"),sQuery(id+"F5.wireOp",EDGE,"E1440"),sQuery(id+"F5.wireOp",EDGE,"E1440"),sQuery(id+"F5.wireOp",EDGE,"E1441"),sQuery(id+"F5.wireOp",EDGE,"E1442"),sQuery(id+"F5.wireOp",EDGE,"E1443"),sQuery(id+"F5.wireOp",EDGE,"E1444"),sQuery(id+"F5.wireOp",EDGE,"E1445"),sQuery(id+"F5.wireOp",EDGE,"E1446"),sQuery(id+"F5.wireOp",EDGE,"E1447"),sQuery(id+"F5.wireOp",EDGE,"E1448"),sQuery(id+"F5.wireOp",EDGE,"E1449"),sQuery(id+"F5.wireOp",EDGE,"E1450"),sQuery(id+"F5.wireOp",EDGE,"E1451"),sQuery(id+"F5.wireOp",EDGE,"E1452"),sQuery(id+"F5.wireOp",EDGE,"E1453"),sQuery(id+"F5.wireOp",EDGE,"E1454"),sQuery(id+"F5.wireOp",EDGE,"E1455"),sQuery(id+"F5.wireOp",EDGE,"E1456"),sQuery(id+"F5.wireOp",EDGE,"E1457"),sQuery(id+"F5.wireOp",EDGE,"E1458"),sQuery(id+"F5.wireOp",EDGE,"E1459"),sQuery(id+"F5.wireOp",EDGE,"E1460"),sQuery(id+"F5.wireOp",EDGE,"E1461"),sQuery(id+"F5.wireOp",EDGE,"E1462"),sQuery(id+"F5.wireOp",EDGE,"E1463"),sQuery(id+"F5.wireOp",EDGE,"E1464"),sQuery(id+"F5.wireOp",EDGE,"E1465"),sQuery(id+"F5.wireOp",EDGE,"E1466"),sQuery(id+"F5.wireOp",EDGE,"E1467"),sQuery(id+"F5.wireOp",EDGE,"E1468"),sQuery(id+"F5.wireOp",EDGE,"E1469"),sQuery(id+"F5.wireOp",EDGE,"E1470"),sQuery(id+"F5.wireOp",EDGE,"E1471"),sQuery(id+"F5.wireOp",EDGE,"E1472"),sQuery(id+"F5.wireOp",EDGE,"E1473"),sQuery(id+"F5.wireOp",EDGE,"E1474"),sQuery(id+"F5.wireOp",EDGE,"E1475"),sQuery(id+"F5.wireOp",EDGE,"E1476"),sQuery(id+"F5.wireOp",EDGE,"E1477"),sQuery(id+"F5.wireOp",EDGE,"E1478"),sQuery(id+"F5.wireOp",EDGE,"E1479"),sQuery(id+"F5.wireOp",EDGE,"E1480"),sQuery(id+"F5.wireOp",EDGE,"E1481"),sQuery(id+"F5.wireOp",EDGE,"E1482"),sQuery(id+"F5.wireOp",EDGE,"E1483"),sQuery(id+"F5.wireOp",EDGE,"E1484"),sQuery(id+"F5.wireOp",EDGE,"E1485"),sQuery(id+"F5.wireOp",EDGE,"E1486"),sQuery(id+"F5.wireOp",EDGE,"E1487"),sQuery(id+"F5.wireOp",EDGE,"E1488"),sQuery(id+"F5.wireOp",EDGE,"E1489"),sQuery(id+"F5.wireOp",EDGE,"E1490"),sQuery(id+"F5.wireOp",EDGE,"E1491"),sQuery(id+"F5.wireOp",EDGE,"E1492"),sQuery(id+"F5.wireOp",EDGE,"E1493"),sQuery(id+"F5.wireOp",EDGE,"E1494"),sQuery(id+"F5.wireOp",EDGE,"E1495"),sQuery(id+"F5.wireOp",EDGE,"E1496"),sQuery(id+"F5.wireOp",EDGE,"E1497"),sQuery(id+"F5.wireOp",EDGE,"E1498"),sQuery(id+"F5.wireOp",EDGE,"E1499"),sQuery(id+"F5.wireOp",EDGE,"E1499"),sQuery(id+"F5.wireOp",EDGE,"E1500"),sQuery(id+"F5.wireOp",EDGE,"E1501"),sQuery(id+"F5.wireOp",EDGE,"E1499"),sQuery(id+"F5.wireOp",EDGE,"E1499"),sQuery(id+"F5.wireOp",EDGE,"E1502"),sQuery(id+"F5.wireOp",EDGE,"E1503"),sQuery(id+"F5.wireOp",EDGE,"E1504"),sQuery(id+"F5.wireOp",EDGE,"E1505"),sQuery(id+"F5.wireOp",EDGE,"E1506"),sQuery(id+"F5.wireOp",EDGE,"E1507"),sQuery(id+"F5.wireOp",EDGE,"E1508"),sQuery(id+"F5.wireOp",EDGE,"E1509"),sQuery(id+"F5.wireOp",EDGE,"E1510"),sQuery(id+"F5.wireOp",EDGE,"E1511"),sQuery(id+"F5.wireOp",EDGE,"E1512"),sQuery(id+"F5.wireOp",EDGE,"E1513"),sQuery(id+"F5.wireOp",EDGE,"E1514"),sQuery(id+"F5.wireOp",EDGE,"E1515"),sQuery(id+"F5.wireOp",EDGE,"E1516"),sQuery(id+"F5.wireOp",EDGE,"E1517"),sQuery(id+"F5.wireOp",EDGE,"E1518"),sQuery(id+"F5.wireOp",EDGE,"E1519"),sQuery(id+"F5.wireOp",EDGE,"E1520"),sQuery(id+"F5.wireOp",EDGE,"E1521"),sQuery(id+"F5.wireOp",EDGE,"E1522"),sQuery(id+"F5.wireOp",EDGE,"E1523"),sQuery(id+"F5.wireOp",EDGE,"E1524"),sQuery(id+"F5.wireOp",EDGE,"E1525"),sQuery(id+"F5.wireOp",EDGE,"E1526"),sQuery(id+"F5.wireOp",EDGE,"E1527"),sQuery(id+"F5.wireOp",EDGE,"E1528"),sQuery(id+"F5.wireOp",EDGE,"E1529"),sQuery(id+"F5.wireOp",EDGE,"E1530"),sQuery(id+"F5.wireOp",EDGE,"E1531"),sQuery(id+"F5.wireOp",EDGE,"E1532"),sQuery(id+"F5.wireOp",EDGE,"E1533"),sQuery(id+"F5.wireOp",EDGE,"E1534"),sQuery(id+"F5.wireOp",EDGE,"E1535"),sQuery(id+"F5.wireOp",EDGE,"E1536"),sQuery(id+"F5.wireOp",EDGE,"E1537"),sQuery(id+"F5.wireOp",EDGE,"E1538"),sQuery(id+"F5.wireOp",EDGE,"E1539"),sQuery(id+"F5.wireOp",EDGE,"E1540"),sQuery(id+"F5.wireOp",EDGE,"E1541"),sQuery(id+"F5.wireOp",EDGE,"E1542"),sQuery(id+"F5.wireOp",EDGE,"E1543"),sQuery(id+"F5.wireOp",EDGE,"E1544"),sQuery(id+"F5.wireOp",EDGE,"E1545"),sQuery(id+"F5.wireOp",EDGE,"E1546"),sQuery(id+"F5.wireOp",EDGE,"E1547"),sQuery(id+"F5.wireOp",EDGE,"E1548"),sQuery(id+"F5.wireOp",EDGE,"E1549"),sQuery(id+"F5.wireOp",EDGE,"E1550"),sQuery(id+"F5.wireOp",EDGE,"E1551"),sQuery(id+"F5.wireOp",EDGE,"E1552"),sQuery(id+"F5.wireOp",EDGE,"E1553"),sQuery(id+"F5.wireOp",EDGE,"E1554"),sQuery(id+"F5.wireOp",EDGE,"E1555"),sQuery(id+"F5.wireOp",EDGE,"E1556"),sQuery(id+"F5.wireOp",EDGE,"E1557"),sQuery(id+"F5.wireOp",EDGE,"E1558"),sQuery(id+"F5.wireOp",EDGE,"E1559"),sQuery(id+"F5.wireOp",EDGE,"E1560"),sQuery(id+"F5.wireOp",EDGE,"E1561"),sQuery(id+"F5.wireOp",EDGE,"E1562"),sQuery(id+"F5.wireOp",EDGE,"E1563"),sQuery(id+"F5.wireOp",EDGE,"E1564"),sQuery(id+"F5.wireOp",EDGE,"E1565"),sQuery(id+"F5.wireOp",EDGE,"E1566"),sQuery(id+"F5.wireOp",EDGE,"E1567"),sQuery(id+"F5.wireOp",EDGE,"E1568"),sQuery(id+"F5.wireOp",EDGE,"E1569"),sQuery(id+"F5.wireOp",EDGE,"E1570"),sQuery(id+"F5.wireOp",EDGE,"E1571"),sQuery(id+"F5.wireOp",EDGE,"E1572"),sQuery(id+"F5.wireOp",EDGE,"E1573"),sQuery(id+"F5.wireOp",EDGE,"E1574"),sQuery(id+"F5.wireOp",EDGE,"E1575"),sQuery(id+"F5.wireOp",EDGE,"E1576"),sQuery(id+"F5.wireOp",EDGE,"E1577")])]});
            var Q30;
            Q30=makeQuery(id+"F11.opExtrude","SWEPT_BODY",BODY,{"disambiguationData":[OSD([sQuery(id+"F6.wireOp",EDGE,"E1578"),sQuery(id+"F6.wireOp",EDGE,"E1579"),sQuery(id+"F6.wireOp",EDGE,"E1580"),sQuery(id+"F6.wireOp",EDGE,"E1581"),sQuery(id+"F6.wireOp",EDGE,"E1582"),sQuery(id+"F6.wireOp",EDGE,"E1583"),sQuery(id+"F6.wireOp",EDGE,"E1584"),sQuery(id+"F6.wireOp",EDGE,"E1585"),sQuery(id+"F6.wireOp",EDGE,"E1586"),sQuery(id+"F6.wireOp",EDGE,"E1587"),sQuery(id+"F6.wireOp",EDGE,"E1588"),sQuery(id+"F6.wireOp",EDGE,"E1589"),sQuery(id+"F6.wireOp",EDGE,"E1590"),sQuery(id+"F6.wireOp",EDGE,"E1591"),sQuery(id+"F6.wireOp",EDGE,"E1592"),sQuery(id+"F6.wireOp",EDGE,"E1593"),sQuery(id+"F6.wireOp",EDGE,"E1594"),sQuery(id+"F6.wireOp",EDGE,"E1594"),sQuery(id+"F6.wireOp",EDGE,"E1594"),sQuery(id+"F6.wireOp",EDGE,"E1594"),sQuery(id+"F6.wireOp",EDGE,"E1595"),sQuery(id+"F6.wireOp",EDGE,"E1596"),sQuery(id+"F6.wireOp",EDGE,"E1597"),sQuery(id+"F6.wireOp",EDGE,"E1598"),sQuery(id+"F6.wireOp",EDGE,"E1599"),sQuery(id+"F6.wireOp",EDGE,"E1600"),sQuery(id+"F6.wireOp",EDGE,"E1601"),sQuery(id+"F6.wireOp",EDGE,"E1602"),sQuery(id+"F6.wireOp",EDGE,"E1603"),sQuery(id+"F6.wireOp",EDGE,"E1604"),sQuery(id+"F6.wireOp",EDGE,"E1605"),sQuery(id+"F6.wireOp",EDGE,"E1606"),sQuery(id+"F6.wireOp",EDGE,"E1607"),sQuery(id+"F6.wireOp",EDGE,"E1608"),sQuery(id+"F6.wireOp",EDGE,"E1609"),sQuery(id+"F6.wireOp",EDGE,"E1610"),sQuery(id+"F6.wireOp",EDGE,"E1611"),sQuery(id+"F6.wireOp",EDGE,"E1612"),sQuery(id+"F6.wireOp",EDGE,"E1613"),sQuery(id+"F6.wireOp",EDGE,"E1614"),sQuery(id+"F6.wireOp",EDGE,"E1615"),sQuery(id+"F6.wireOp",EDGE,"E1616"),sQuery(id+"F6.wireOp",EDGE,"E1617"),sQuery(id+"F6.wireOp",EDGE,"E1618"),sQuery(id+"F6.wireOp",EDGE,"E1619"),sQuery(id+"F6.wireOp",EDGE,"E1620"),sQuery(id+"F6.wireOp",EDGE,"E1621"),sQuery(id+"F6.wireOp",EDGE,"E1622"),sQuery(id+"F6.wireOp",EDGE,"E1623"),sQuery(id+"F6.wireOp",EDGE,"E1624"),sQuery(id+"F6.wireOp",EDGE,"E1625"),sQuery(id+"F6.wireOp",EDGE,"E1626"),sQuery(id+"F6.wireOp",EDGE,"E1627"),sQuery(id+"F6.wireOp",EDGE,"E1628"),sQuery(id+"F6.wireOp",EDGE,"E1629"),sQuery(id+"F6.wireOp",EDGE,"E1630"),sQuery(id+"F6.wireOp",EDGE,"E1631"),sQuery(id+"F6.wireOp",EDGE,"E1632"),sQuery(id+"F6.wireOp",EDGE,"E1633"),sQuery(id+"F6.wireOp",EDGE,"E1634"),sQuery(id+"F6.wireOp",EDGE,"E1635"),sQuery(id+"F6.wireOp",EDGE,"E1636"),sQuery(id+"F6.wireOp",EDGE,"E1637"),sQuery(id+"F6.wireOp",EDGE,"E1638"),sQuery(id+"F6.wireOp",EDGE,"E1639"),sQuery(id+"F6.wireOp",EDGE,"E1640"),sQuery(id+"F6.wireOp",EDGE,"E1641"),sQuery(id+"F6.wireOp",EDGE,"E1642"),sQuery(id+"F6.wireOp",EDGE,"E1643"),sQuery(id+"F6.wireOp",EDGE,"E1644"),sQuery(id+"F6.wireOp",EDGE,"E1645"),sQuery(id+"F6.wireOp",EDGE,"E1646"),sQuery(id+"F6.wireOp",EDGE,"E1647"),sQuery(id+"F6.wireOp",EDGE,"E1648"),sQuery(id+"F6.wireOp",EDGE,"E1649"),sQuery(id+"F6.wireOp",EDGE,"E1650"),sQuery(id+"F6.wireOp",EDGE,"E1651"),sQuery(id+"F6.wireOp",EDGE,"E1652"),sQuery(id+"F6.wireOp",EDGE,"E1653"),sQuery(id+"F6.wireOp",EDGE,"E1654"),sQuery(id+"F6.wireOp",EDGE,"E1655"),sQuery(id+"F6.wireOp",EDGE,"E1656"),sQuery(id+"F6.wireOp",EDGE,"E1657"),sQuery(id+"F6.wireOp",EDGE,"E1658"),sQuery(id+"F6.wireOp",EDGE,"E1659"),sQuery(id+"F6.wireOp",EDGE,"E1660"),sQuery(id+"F6.wireOp",EDGE,"E1661"),sQuery(id+"F6.wireOp",EDGE,"E1662"),sQuery(id+"F6.wireOp",EDGE,"E1663"),sQuery(id+"F6.wireOp",EDGE,"E1664"),sQuery(id+"F6.wireOp",EDGE,"E1665"),sQuery(id+"F6.wireOp",EDGE,"E1666"),sQuery(id+"F6.wireOp",EDGE,"E1667"),sQuery(id+"F6.wireOp",EDGE,"E1668"),sQuery(id+"F6.wireOp",EDGE,"E1669"),sQuery(id+"F6.wireOp",EDGE,"E1670"),sQuery(id+"F6.wireOp",EDGE,"E1671"),sQuery(id+"F6.wireOp",EDGE,"E1672"),sQuery(id+"F6.wireOp",EDGE,"E1673"),sQuery(id+"F6.wireOp",EDGE,"E1674"),sQuery(id+"F6.wireOp",EDGE,"E1675"),sQuery(id+"F6.wireOp",EDGE,"E1676"),sQuery(id+"F6.wireOp",EDGE,"E1677"),sQuery(id+"F6.wireOp",EDGE,"E1678"),sQuery(id+"F6.wireOp",EDGE,"E1679"),sQuery(id+"F6.wireOp",EDGE,"E1680"),sQuery(id+"F6.wireOp",EDGE,"E1681"),sQuery(id+"F6.wireOp",EDGE,"E1682"),sQuery(id+"F6.wireOp",EDGE,"E1683"),sQuery(id+"F6.wireOp",EDGE,"E1684"),sQuery(id+"F6.wireOp",EDGE,"E1685"),sQuery(id+"F6.wireOp",EDGE,"E1686"),sQuery(id+"F6.wireOp",EDGE,"E1687"),sQuery(id+"F6.wireOp",EDGE,"E1688"),sQuery(id+"F6.wireOp",EDGE,"E1689"),sQuery(id+"F6.wireOp",EDGE,"E1690"),sQuery(id+"F6.wireOp",EDGE,"E1691"),sQuery(id+"F6.wireOp",EDGE,"E1692"),sQuery(id+"F6.wireOp",EDGE,"E1693"),sQuery(id+"F6.wireOp",EDGE,"E1694"),sQuery(id+"F6.wireOp",EDGE,"E1695"),sQuery(id+"F6.wireOp",EDGE,"E1696"),sQuery(id+"F6.wireOp",EDGE,"E1697"),sQuery(id+"F6.wireOp",EDGE,"E1698"),sQuery(id+"F6.wireOp",EDGE,"E1699"),sQuery(id+"F6.wireOp",EDGE,"E1700"),sQuery(id+"F6.wireOp",EDGE,"E1701"),sQuery(id+"F6.wireOp",EDGE,"E1702"),sQuery(id+"F6.wireOp",EDGE,"E1703"),sQuery(id+"F6.wireOp",EDGE,"E1704"),sQuery(id+"F6.wireOp",EDGE,"E1705"),sQuery(id+"F6.wireOp",EDGE,"E1706"),sQuery(id+"F6.wireOp",EDGE,"E1707"),sQuery(id+"F6.wireOp",EDGE,"E1708"),sQuery(id+"F6.wireOp",EDGE,"E1709"),sQuery(id+"F6.wireOp",EDGE,"E1710"),sQuery(id+"F6.wireOp",EDGE,"E1711"),sQuery(id+"F6.wireOp",EDGE,"E1712"),sQuery(id+"F6.wireOp",EDGE,"E1713"),sQuery(id+"F6.wireOp",EDGE,"E1713"),sQuery(id+"F6.wireOp",EDGE,"E1714"),sQuery(id+"F6.wireOp",EDGE,"E1715"),sQuery(id+"F6.wireOp",EDGE,"E1716"),sQuery(id+"F6.wireOp",EDGE,"E1717"),sQuery(id+"F6.wireOp",EDGE,"E1718"),sQuery(id+"F6.wireOp",EDGE,"E1719"),sQuery(id+"F6.wireOp",EDGE,"E1720"),sQuery(id+"F6.wireOp",EDGE,"E1721"),sQuery(id+"F6.wireOp",EDGE,"E1722"),sQuery(id+"F6.wireOp",EDGE,"E1723"),sQuery(id+"F6.wireOp",EDGE,"E1724"),sQuery(id+"F6.wireOp",EDGE,"E1725"),sQuery(id+"F6.wireOp",EDGE,"E1726"),sQuery(id+"F6.wireOp",EDGE,"E1727"),sQuery(id+"F6.wireOp",EDGE,"E1728"),sQuery(id+"F6.wireOp",EDGE,"E1729"),sQuery(id+"F6.wireOp",EDGE,"E1730"),sQuery(id+"F6.wireOp",EDGE,"E1731"),sQuery(id+"F6.wireOp",EDGE,"E1732"),sQuery(id+"F6.wireOp",EDGE,"E1733"),sQuery(id+"F6.wireOp",EDGE,"E1734"),sQuery(id+"F6.wireOp",EDGE,"E1735"),sQuery(id+"F6.wireOp",EDGE,"E1736"),sQuery(id+"F6.wireOp",EDGE,"E1737"),sQuery(id+"F6.wireOp",EDGE,"E1737"),sQuery(id+"F6.wireOp",EDGE,"E1738"),sQuery(id+"F6.wireOp",EDGE,"E1739"),sQuery(id+"F6.wireOp",EDGE,"E1740"),sQuery(id+"F6.wireOp",EDGE,"E1741"),sQuery(id+"F6.wireOp",EDGE,"E1742"),sQuery(id+"F6.wireOp",EDGE,"E1743"),sQuery(id+"F6.wireOp",EDGE,"E1744"),sQuery(id+"F6.wireOp",EDGE,"E1745"),sQuery(id+"F6.wireOp",EDGE,"E1746"),sQuery(id+"F6.wireOp",EDGE,"E1747"),sQuery(id+"F6.wireOp",EDGE,"E1748"),sQuery(id+"F6.wireOp",EDGE,"E1749"),sQuery(id+"F6.wireOp",EDGE,"E1750"),sQuery(id+"F6.wireOp",EDGE,"E1751"),sQuery(id+"F6.wireOp",EDGE,"E1752"),sQuery(id+"F6.wireOp",EDGE,"E1752"),sQuery(id+"F6.wireOp",EDGE,"E1753"),sQuery(id+"F6.wireOp",EDGE,"E1754"),sQuery(id+"F6.wireOp",EDGE,"E1755"),sQuery(id+"F6.wireOp",EDGE,"E1756"),sQuery(id+"F6.wireOp",EDGE,"E1757"),sQuery(id+"F6.wireOp",EDGE,"E1758"),sQuery(id+"F6.wireOp",EDGE,"E1759"),sQuery(id+"F6.wireOp",EDGE,"E1760"),sQuery(id+"F6.wireOp",EDGE,"E1760"),sQuery(id+"F6.wireOp",EDGE,"E1760"),sQuery(id+"F6.wireOp",EDGE,"E1761"),sQuery(id+"F6.wireOp",EDGE,"E1762"),sQuery(id+"F6.wireOp",EDGE,"E1763"),sQuery(id+"F6.wireOp",EDGE,"E1763"),sQuery(id+"F6.wireOp",EDGE,"E1764"),sQuery(id+"F6.wireOp",EDGE,"E1765"),sQuery(id+"F6.wireOp",EDGE,"E1766"),sQuery(id+"F6.wireOp",EDGE,"E1767"),sQuery(id+"F6.wireOp",EDGE,"E1768"),sQuery(id+"F6.wireOp",EDGE,"E1769"),sQuery(id+"F6.wireOp",EDGE,"E1770"),sQuery(id+"F6.wireOp",EDGE,"E1771"),sQuery(id+"F6.wireOp",EDGE,"E1772"),sQuery(id+"F6.wireOp",EDGE,"E1773"),sQuery(id+"F6.wireOp",EDGE,"E1774"),sQuery(id+"F6.wireOp",EDGE,"E1775"),sQuery(id+"F6.wireOp",EDGE,"E1776"),sQuery(id+"F6.wireOp",EDGE,"E1777"),sQuery(id+"F6.wireOp",EDGE,"E1778"),sQuery(id+"F6.wireOp",EDGE,"E1779"),sQuery(id+"F6.wireOp",EDGE,"E1780"),sQuery(id+"F6.wireOp",EDGE,"E1781"),sQuery(id+"F6.wireOp",EDGE,"E1782"),sQuery(id+"F6.wireOp",EDGE,"E1783"),sQuery(id+"F6.wireOp",EDGE,"E1784"),sQuery(id+"F6.wireOp",EDGE,"E1785"),sQuery(id+"F6.wireOp",EDGE,"E1786"),sQuery(id+"F6.wireOp",EDGE,"E1786"),sQuery(id+"F6.wireOp",EDGE,"E1787"),sQuery(id+"F6.wireOp",EDGE,"E1788"),sQuery(id+"F6.wireOp",EDGE,"E1789"),sQuery(id+"F6.wireOp",EDGE,"E1790"),sQuery(id+"F6.wireOp",EDGE,"E1791"),sQuery(id+"F6.wireOp",EDGE,"E1792"),sQuery(id+"F6.wireOp",EDGE,"E1793"),sQuery(id+"F6.wireOp",EDGE,"E1794"),sQuery(id+"F6.wireOp",EDGE,"E1795"),sQuery(id+"F6.wireOp",EDGE,"E1796"),sQuery(id+"F6.wireOp",EDGE,"E1797"),sQuery(id+"F6.wireOp",EDGE,"E1798"),sQuery(id+"F6.wireOp",EDGE,"E1799"),sQuery(id+"F6.wireOp",EDGE,"E1800"),sQuery(id+"F6.wireOp",EDGE,"E1801"),sQuery(id+"F6.wireOp",EDGE,"E1802"),sQuery(id+"F6.wireOp",EDGE,"E1803"),sQuery(id+"F6.wireOp",EDGE,"E1804"),sQuery(id+"F6.wireOp",EDGE,"E1805"),sQuery(id+"F6.wireOp",EDGE,"E1806"),sQuery(id+"F6.wireOp",EDGE,"E1807"),sQuery(id+"F6.wireOp",EDGE,"E1808"),sQuery(id+"F6.wireOp",EDGE,"E1809"),sQuery(id+"F6.wireOp",EDGE,"E1810"),sQuery(id+"F6.wireOp",EDGE,"E1811"),sQuery(id+"F6.wireOp",EDGE,"E1812"),sQuery(id+"F6.wireOp",EDGE,"E1813"),sQuery(id+"F6.wireOp",EDGE,"E1814"),sQuery(id+"F6.wireOp",EDGE,"E1815"),sQuery(id+"F6.wireOp",EDGE,"E1816"),sQuery(id+"F6.wireOp",EDGE,"E1817"),sQuery(id+"F6.wireOp",EDGE,"E1818"),sQuery(id+"F6.wireOp",EDGE,"E1819"),sQuery(id+"F6.wireOp",EDGE,"E1820"),sQuery(id+"F6.wireOp",EDGE,"E1821"),sQuery(id+"F6.wireOp",EDGE,"E1822"),sQuery(id+"F6.wireOp",EDGE,"E1823"),sQuery(id+"F6.wireOp",EDGE,"E1824"),sQuery(id+"F6.wireOp",EDGE,"E1825"),sQuery(id+"F6.wireOp",EDGE,"E1826"),sQuery(id+"F6.wireOp",EDGE,"E1827"),sQuery(id+"F6.wireOp",EDGE,"E1827"),sQuery(id+"F6.wireOp",EDGE,"E1828"),sQuery(id+"F6.wireOp",EDGE,"E1829"),sQuery(id+"F6.wireOp",EDGE,"E1830"),sQuery(id+"F6.wireOp",EDGE,"E1831"),sQuery(id+"F6.wireOp",EDGE,"E1832"),sQuery(id+"F6.wireOp",EDGE,"E1833"),sQuery(id+"F6.wireOp",EDGE,"E1834"),sQuery(id+"F6.wireOp",EDGE,"E1835"),sQuery(id+"F6.wireOp",EDGE,"E1832"),sQuery(id+"F6.wireOp",EDGE,"E1836"),sQuery(id+"F6.wireOp",EDGE,"E1837"),sQuery(id+"F6.wireOp",EDGE,"E1838"),sQuery(id+"F6.wireOp",EDGE,"E1839"),sQuery(id+"F6.wireOp",EDGE,"E1840"),sQuery(id+"F6.wireOp",EDGE,"E1841"),sQuery(id+"F6.wireOp",EDGE,"E1842"),sQuery(id+"F6.wireOp",EDGE,"E1843"),sQuery(id+"F6.wireOp",EDGE,"E1844"),sQuery(id+"F6.wireOp",EDGE,"E1845"),sQuery(id+"F6.wireOp",EDGE,"E1846"),sQuery(id+"F6.wireOp",EDGE,"E1847"),sQuery(id+"F6.wireOp",EDGE,"E1848"),sQuery(id+"F6.wireOp",EDGE,"E1849"),sQuery(id+"F6.wireOp",EDGE,"E1849"),sQuery(id+"F6.wireOp",EDGE,"E1850"),sQuery(id+"F6.wireOp",EDGE,"E1851"),sQuery(id+"F6.wireOp",EDGE,"E1852"),sQuery(id+"F6.wireOp",EDGE,"E1853"),sQuery(id+"F6.wireOp",EDGE,"E1854"),sQuery(id+"F6.wireOp",EDGE,"E1855"),sQuery(id+"F6.wireOp",EDGE,"E1856"),sQuery(id+"F6.wireOp",EDGE,"E1857"),sQuery(id+"F6.wireOp",EDGE,"E1858"),sQuery(id+"F6.wireOp",EDGE,"E1859"),sQuery(id+"F6.wireOp",EDGE,"E1860"),sQuery(id+"F6.wireOp",EDGE,"E1861"),sQuery(id+"F6.wireOp",EDGE,"E1862"),sQuery(id+"F6.wireOp",EDGE,"E1863"),sQuery(id+"F6.wireOp",EDGE,"E1864"),sQuery(id+"F6.wireOp",EDGE,"E1865"),sQuery(id+"F6.wireOp",EDGE,"E1866"),sQuery(id+"F6.wireOp",EDGE,"E1867")])]});
            var Q31;
            Q31=makeQuery(id+"F47Eg7U8JpIE8te_31.opExtrude","SWEPT_BODY",BODY,{"disambiguationData":[OSD([sQuery(id+"FOPml0yl2Jk7fKW_31.wireOp",EDGE,"1ffc15d4-c48e-4b9d-92a7-b72b578dae79"),sQuery(id+"FOPml0yl2Jk7fKW_31.wireOp",EDGE,"ad39be35-8bdb-4f39-8e9a-6311a8525181"),sQuery(id+"FOPml0yl2Jk7fKW_31.wireOp",EDGE,"a6f33c1c-932a-4085-a5f9-4dbaf16e7884"),sQuery(id+"FOPml0yl2Jk7fKW_31.wireOp",EDGE,"cd7900b7-48b9-4f92-b521-418bae226b7d"),sQuery(id+"FOPml0yl2Jk7fKW_31.wireOp",EDGE,"c915e204-727c-411e-860e-a1f9e93911bb"),sQuery(id+"FOPml0yl2Jk7fKW_31.wireOp",EDGE,"4ced3cdc-0578-44de-a7ce-0da907bb0bef"),sQuery(id+"FOPml0yl2Jk7fKW_31.wireOp",EDGE,"5746aec4-d689-4993-9933-af9c142bb655"),sQuery(id+"FOPml0yl2Jk7fKW_31.wireOp",EDGE,"f9e92374-9637-4512-aca7-ee8afdb32fed"),sQuery(id+"FOPml0yl2Jk7fKW_31.wireOp",EDGE,"6504a159-6ed8-4ec0-94af-402a5b2847a5"),sQuery(id+"FOPml0yl2Jk7fKW_31.wireOp",EDGE,"9c54c825-4afe-4052-b19d-55528afa1698"),sQuery(id+"FOPml0yl2Jk7fKW_31.wireOp",EDGE,"0aa82e38-5608-45cd-a6d4-7631a19b48a0"),sQuery(id+"FOPml0yl2Jk7fKW_31.wireOp",EDGE,"76ab8036-d7f8-4269-857a-77f26ef356df"),sQuery(id+"FOPml0yl2Jk7fKW_31.wireOp",EDGE,"a0c319b9-5ca3-4068-8cfc-b6d7fe2654cc"),sQuery(id+"FOPml0yl2Jk7fKW_31.wireOp",EDGE,"55b39a78-16dd-4040-bae7-6506386dbae9"),sQuery(id+"FOPml0yl2Jk7fKW_31.wireOp",EDGE,"9da996ed-92f5-4809-a5ba-fe9e2bc68b73"),sQuery(id+"FOPml0yl2Jk7fKW_31.wireOp",EDGE,"ef53ea49-96aa-46e6-998b-d3753b462804"),sQuery(id+"FOPml0yl2Jk7fKW_31.wireOp",EDGE,"d493f435-48b4-4190-bb1b-71188deec44d"),sQuery(id+"FOPml0yl2Jk7fKW_31.wireOp",EDGE,"de70ec42-8fea-4c1b-8da6-51012c8eb1ab"),sQuery(id+"FOPml0yl2Jk7fKW_31.wireOp",EDGE,"596437c5-8ab7-4cda-b081-d1685abd7a97"),sQuery(id+"FOPml0yl2Jk7fKW_31.wireOp",EDGE,"2e27370a-8468-4ac4-99c2-4411b707b4ce"),sQuery(id+"FOPml0yl2Jk7fKW_31.wireOp",EDGE,"e8278412-4a93-438a-9ad0-6f6d11c2450f"),sQuery(id+"FOPml0yl2Jk7fKW_31.wireOp",EDGE,"98b26c45-7e6e-4b27-972e-7c12077b4f74"),sQuery(id+"FOPml0yl2Jk7fKW_31.wireOp",EDGE,"9807378e-0561-4621-a435-855dc513bfcd"),sQuery(id+"FOPml0yl2Jk7fKW_31.wireOp",EDGE,"ba743061-a39a-4450-a2a1-1ad205295dcd"),sQuery(id+"FOPml0yl2Jk7fKW_31.wireOp",EDGE,"fe7857e4-7a1c-474e-921c-f15a5b3a1584"),sQuery(id+"FOPml0yl2Jk7fKW_31.wireOp",EDGE,"27c15c78-c0b3-47ea-9503-54b3f2bcec46"),sQuery(id+"FOPml0yl2Jk7fKW_31.wireOp",EDGE,"7d7e020a-d9a1-4692-8bf0-7f23512b268e"),sQuery(id+"FOPml0yl2Jk7fKW_31.wireOp",EDGE,"bcd651b2-ab00-4629-bc1c-232a6e28e53a"),sQuery(id+"FOPml0yl2Jk7fKW_31.wireOp",EDGE,"b959c8a4-1a37-45a3-8483-546401fc96fd"),sQuery(id+"FOPml0yl2Jk7fKW_31.wireOp",EDGE,"d235e335-4de4-4bc2-95e1-577d0dbd05d3"),sQuery(id+"FOPml0yl2Jk7fKW_31.wireOp",EDGE,"adf16bc7-2801-4c15-9290-474d1de42776"),sQuery(id+"FOPml0yl2Jk7fKW_31.wireOp",EDGE,"c71ca856-40f6-4744-a371-dd398879a2d7"),sQuery(id+"FOPml0yl2Jk7fKW_31.wireOp",EDGE,"8e416b13-8c79-4a07-bcc6-57c6ae0d06d5"),sQuery(id+"FOPml0yl2Jk7fKW_31.wireOp",EDGE,"a47bc75b-4b8c-4763-9776-897ecc9f1efa"),sQuery(id+"FOPml0yl2Jk7fKW_31.wireOp",EDGE,"c4763773-3421-4c3e-be2c-f4d6c9353a63"),sQuery(id+"FOPml0yl2Jk7fKW_31.wireOp",EDGE,"7b923943-766a-4abc-9e52-d04260b94ac8"),sQuery(id+"FOPml0yl2Jk7fKW_31.wireOp",EDGE,"43981bcf-1e4d-458a-b32c-693e311ed16f"),sQuery(id+"FOPml0yl2Jk7fKW_31.wireOp",EDGE,"2d1f4642-35d1-46cc-96f6-f374277cd519"),sQuery(id+"FOPml0yl2Jk7fKW_31.wireOp",EDGE,"914c229c-0f28-489c-bdd6-f11aa1afd338"),sQuery(id+"FOPml0yl2Jk7fKW_31.wireOp",EDGE,"76cd540a-042a-48de-9781-6f0c5ba1e636"),sQuery(id+"FOPml0yl2Jk7fKW_31.wireOp",EDGE,"afeab47f-b85f-472b-acbe-8831487068c3"),sQuery(id+"FOPml0yl2Jk7fKW_31.wireOp",EDGE,"756042cb-593b-4936-a7c9-2ac46dec7f92"),sQuery(id+"FOPml0yl2Jk7fKW_31.wireOp",EDGE,"48b227a2-51de-4bfe-81a3-249e2f9cb7ff"),sQuery(id+"FOPml0yl2Jk7fKW_31.wireOp",EDGE,"feb77dee-7d78-48c8-a196-abd390595dc0"),sQuery(id+"FOPml0yl2Jk7fKW_31.wireOp",EDGE,"9a71b873-519b-4614-80c7-2f9481344b4a"),sQuery(id+"FOPml0yl2Jk7fKW_31.wireOp",EDGE,"cb6a77e7-ef57-4f30-bd32-8fab25075864"),sQuery(id+"FOPml0yl2Jk7fKW_31.wireOp",EDGE,"215da373-6f9d-4e75-8640-0223ce3b632f"),sQuery(id+"FOPml0yl2Jk7fKW_31.wireOp",EDGE,"77b45a9f-eda5-4b82-a6a8-ca5e0a229be8"),sQuery(id+"FOPml0yl2Jk7fKW_31.wireOp",EDGE,"c8bc7da8-4149-4c3f-921e-0b09faf79cd7"),sQuery(id+"FOPml0yl2Jk7fKW_31.wireOp",EDGE,"100ae932-6217-4c7d-a06a-e1135082bd9c"),sQuery(id+"FOPml0yl2Jk7fKW_31.wireOp",EDGE,"f27eacff-053b-47c8-bc5a-e0536d07af6b"),sQuery(id+"FOPml0yl2Jk7fKW_31.wireOp",EDGE,"5c813f66-0a85-4b3a-b358-972e74d37606"),sQuery(id+"FOPml0yl2Jk7fKW_31.wireOp",EDGE,"ced72682-0359-441f-8ece-f69c8555e961"),sQuery(id+"FOPml0yl2Jk7fKW_31.wireOp",EDGE,"3176f16f-3787-499a-9d1a-cb7f2ec2988c"),sQuery(id+"FOPml0yl2Jk7fKW_31.wireOp",EDGE,"823b0a33-3a02-40dc-a806-6ed3d7da72eb"),sQuery(id+"FOPml0yl2Jk7fKW_31.wireOp",EDGE,"c8c59ee1-ce54-43a9-80ca-97a61b0a4dc8"),sQuery(id+"FOPml0yl2Jk7fKW_31.wireOp",EDGE,"56e03eba-6e62-4b8a-8667-a5ba1e9e8114"),sQuery(id+"FOPml0yl2Jk7fKW_31.wireOp",EDGE,"f38751f5-73b3-4cb9-b925-f31fdf442ad2"),sQuery(id+"FOPml0yl2Jk7fKW_31.wireOp",EDGE,"b44972d3-5253-443c-b096-0e80e1777a9f"),sQuery(id+"FOPml0yl2Jk7fKW_31.wireOp",EDGE,"aa3074fa-ec49-421c-a7e7-a71c9a53bd53"),sQuery(id+"FOPml0yl2Jk7fKW_31.wireOp",EDGE,"2ea75ba5-77e4-48af-98d3-9ac20e955537"),sQuery(id+"FOPml0yl2Jk7fKW_31.wireOp",EDGE,"c1e76ad7-b23c-405d-99ef-346de3ae8824"),sQuery(id+"FOPml0yl2Jk7fKW_31.wireOp",EDGE,"e9f37f0b-8ac5-405e-8bd1-dcc411e2bff3")])]});
            var Q32;
            Q32=makeQuery(id+"F47Eg7U8JpIE8te_31.opExtrude","SWEPT_BODY",BODY,{"disambiguationData":[OSD([sQuery(id+"FOPml0yl2Jk7fKW_31.wireOp",EDGE,"07cab093-dd12-42d3-826b-e5d58eb6aec1"),sQuery(id+"FOPml0yl2Jk7fKW_31.wireOp",EDGE,"b0b5bfa7-5b4f-41ce-8995-14cfce3f0e89"),sQuery(id+"FOPml0yl2Jk7fKW_31.wireOp",EDGE,"dd71202b-0ceb-447d-86f6-88f02189aa7d"),sQuery(id+"FOPml0yl2Jk7fKW_31.wireOp",EDGE,"c11995c4-903c-4aff-bfbd-eb60fc9ca9ee"),sQuery(id+"FOPml0yl2Jk7fKW_31.wireOp",EDGE,"32372b01-6318-4fd2-8647-d333cb21971b"),sQuery(id+"FOPml0yl2Jk7fKW_31.wireOp",EDGE,"2bae6375-16a2-4c07-962b-145684e9d3a6"),sQuery(id+"FOPml0yl2Jk7fKW_31.wireOp",EDGE,"af74d9b4-75d6-4c04-b686-3fc191cf6bf0"),sQuery(id+"FOPml0yl2Jk7fKW_31.wireOp",EDGE,"f9c651ea-ba7a-4bfc-bd01-5066d59c16b1"),sQuery(id+"FOPml0yl2Jk7fKW_31.wireOp",EDGE,"55e8e85d-34f6-4ea1-a29a-e4472733e501"),sQuery(id+"FOPml0yl2Jk7fKW_31.wireOp",EDGE,"3d852b96-a38e-4c54-a140-f518bc59d833"),sQuery(id+"FOPml0yl2Jk7fKW_31.wireOp",EDGE,"18fb868c-b288-4c5f-815b-85ddfdadeb52"),sQuery(id+"FOPml0yl2Jk7fKW_31.wireOp",EDGE,"b6e32f82-2471-40eb-a38f-261cbfe56e22"),sQuery(id+"FOPml0yl2Jk7fKW_31.wireOp",EDGE,"170f6a31-27d3-4bb4-861c-8bd65428034f"),sQuery(id+"FOPml0yl2Jk7fKW_31.wireOp",EDGE,"3ff84119-7605-4b7c-a3ad-14d7b5ba059f"),sQuery(id+"FOPml0yl2Jk7fKW_31.wireOp",EDGE,"104ffd5b-64cc-45e9-b3fd-1357d0a33898"),sQuery(id+"FOPml0yl2Jk7fKW_31.wireOp",EDGE,"066388de-ab87-4a60-af84-6bb0eda2f2a7"),sQuery(id+"FOPml0yl2Jk7fKW_31.wireOp",EDGE,"f99e3440-ae8b-46b0-820a-2d11bbb516d3"),sQuery(id+"FOPml0yl2Jk7fKW_31.wireOp",EDGE,"52ed0560-989d-4b02-8d92-7515381b9b41"),sQuery(id+"FOPml0yl2Jk7fKW_31.wireOp",EDGE,"d667cf66-5e19-4797-974f-aeb61ed6258d"),sQuery(id+"FOPml0yl2Jk7fKW_31.wireOp",EDGE,"37166bcd-2e52-410e-b99d-17635686499a"),sQuery(id+"FOPml0yl2Jk7fKW_31.wireOp",EDGE,"c7e09916-1841-410b-a60f-d49af8642c81"),sQuery(id+"FOPml0yl2Jk7fKW_31.wireOp",EDGE,"6dc9d70c-430d-44cf-9aeb-1e3ef006969b"),sQuery(id+"FOPml0yl2Jk7fKW_31.wireOp",EDGE,"e18836b1-1225-43cc-8537-82df978c483f"),sQuery(id+"FOPml0yl2Jk7fKW_31.wireOp",EDGE,"abffaa2a-0189-44da-a867-8abc4b8d6f3a"),sQuery(id+"FOPml0yl2Jk7fKW_31.wireOp",EDGE,"770f0c3c-d5c2-41a9-af12-6bb8532cfb7b"),sQuery(id+"FOPml0yl2Jk7fKW_31.wireOp",EDGE,"cbfca17e-527c-41da-930b-84fa9c1590f3"),sQuery(id+"FOPml0yl2Jk7fKW_31.wireOp",EDGE,"ad753ff8-7aad-4605-aea6-f294bf31ccbc"),sQuery(id+"FOPml0yl2Jk7fKW_31.wireOp",EDGE,"f33354ed-4118-465e-b231-3ee2c9f3d727"),sQuery(id+"FOPml0yl2Jk7fKW_31.wireOp",EDGE,"6f639df3-95b3-4e28-96be-f1623a5ffd97"),sQuery(id+"FOPml0yl2Jk7fKW_31.wireOp",EDGE,"51cad2dd-3c2a-4a5c-888f-e59253febc5f"),sQuery(id+"FOPml0yl2Jk7fKW_31.wireOp",EDGE,"3965368c-a245-44b4-97a3-e229ebe8417a"),sQuery(id+"FOPml0yl2Jk7fKW_31.wireOp",EDGE,"4489a208-756e-40d5-a48d-79674dbec3bd"),sQuery(id+"FOPml0yl2Jk7fKW_31.wireOp",EDGE,"7967af68-d8e8-49c9-ad56-269a5ecd5f42"),sQuery(id+"FOPml0yl2Jk7fKW_31.wireOp",EDGE,"1db5ac79-2456-4195-aa6b-fe9d15488fa6"),sQuery(id+"FOPml0yl2Jk7fKW_31.wireOp",EDGE,"5443e977-3cda-4024-a6cc-0409c3df2a45"),sQuery(id+"FOPml0yl2Jk7fKW_31.wireOp",EDGE,"03125cff-eb55-4ed0-bf43-94fec56df8f1"),sQuery(id+"FOPml0yl2Jk7fKW_31.wireOp",EDGE,"1fe27f7a-18ca-46c5-8cb2-db27e0fc2a06"),sQuery(id+"FOPml0yl2Jk7fKW_31.wireOp",EDGE,"4444b30d-9fb6-4d4b-9f08-866c2dab6d23"),sQuery(id+"FOPml0yl2Jk7fKW_31.wireOp",EDGE,"49ce7ac5-f500-4405-a4f6-0320ca177caa"),sQuery(id+"FOPml0yl2Jk7fKW_31.wireOp",EDGE,"df2af310-712f-4568-8acf-d68e652cdc66"),sQuery(id+"FOPml0yl2Jk7fKW_31.wireOp",EDGE,"4484a0b6-1e97-48de-8311-38bb5e5e1357"),sQuery(id+"FOPml0yl2Jk7fKW_31.wireOp",EDGE,"06153d50-5374-4046-96f9-73adcd89a141"),sQuery(id+"FOPml0yl2Jk7fKW_31.wireOp",EDGE,"5044d765-28d2-43d1-ac7d-acdbf5879799"),sQuery(id+"FOPml0yl2Jk7fKW_31.wireOp",EDGE,"77f658ef-3c5b-4b81-8990-5745625b2c19"),sQuery(id+"FOPml0yl2Jk7fKW_31.wireOp",EDGE,"b6225248-d547-4298-988b-5aa7672e6da3"),sQuery(id+"FOPml0yl2Jk7fKW_31.wireOp",EDGE,"2779e6a1-9bf1-495b-a45e-93b8bbc99aa2"),sQuery(id+"FOPml0yl2Jk7fKW_31.wireOp",EDGE,"f706cf8f-3b8e-4b3e-8eb1-157468bec59f"),sQuery(id+"FOPml0yl2Jk7fKW_31.wireOp",EDGE,"d27a0cfa-2894-409c-a3e6-7a53c1911aac"),sQuery(id+"FOPml0yl2Jk7fKW_31.wireOp",EDGE,"f643125f-c261-4188-9404-4e283dad2cd3"),sQuery(id+"FOPml0yl2Jk7fKW_31.wireOp",EDGE,"8f15659a-5618-4a6b-a896-7d5864ec6707"),sQuery(id+"FOPml0yl2Jk7fKW_31.wireOp",EDGE,"40f2efe7-30dc-4f64-9ce8-984fa98c53cd"),sQuery(id+"FOPml0yl2Jk7fKW_31.wireOp",EDGE,"c389daaf-c79a-4644-b4ea-de581063aa8a"),sQuery(id+"FOPml0yl2Jk7fKW_31.wireOp",EDGE,"30d9b07a-53b5-4ebf-ba48-f9138a5b48b8"),sQuery(id+"FOPml0yl2Jk7fKW_31.wireOp",EDGE,"b5a0e53e-517c-4d45-99cd-6826a780c369"),sQuery(id+"FOPml0yl2Jk7fKW_31.wireOp",EDGE,"64520c2c-070b-47e6-ba52-80eacee6c2b3"),sQuery(id+"FOPml0yl2Jk7fKW_31.wireOp",EDGE,"47ad2d3b-d4d2-45e2-8973-c028ebfbca9d"),sQuery(id+"FOPml0yl2Jk7fKW_31.wireOp",EDGE,"06acdf9a-da05-4a20-8cd8-f4b8327d1cbf"),sQuery(id+"FOPml0yl2Jk7fKW_31.wireOp",EDGE,"14517a9c-8b0f-4710-b7a1-8660a198d358"),sQuery(id+"FOPml0yl2Jk7fKW_31.wireOp",EDGE,"3f8dbf8d-8a65-4bdf-af93-0040429aedbd"),sQuery(id+"FOPml0yl2Jk7fKW_31.wireOp",EDGE,"db169cbb-6e2c-445f-82ad-e3f36a50213b"),sQuery(id+"FOPml0yl2Jk7fKW_31.wireOp",EDGE,"a090d872-48aa-44c4-bd3d-38f54dc09004"),sQuery(id+"FOPml0yl2Jk7fKW_31.wireOp",EDGE,"88dcfd56-f292-448c-b6d1-0b8878992b7c"),sQuery(id+"FOPml0yl2Jk7fKW_31.wireOp",EDGE,"68452757-b08a-410d-941b-294effecdc32"),sQuery(id+"FOPml0yl2Jk7fKW_31.wireOp",EDGE,"28615c96-da83-4ce4-8567-a27c46b2dc63"),sQuery(id+"FOPml0yl2Jk7fKW_31.wireOp",EDGE,"7e225bd2-4fb0-4615-bcb7-fb265f801b95"),sQuery(id+"FOPml0yl2Jk7fKW_31.wireOp",EDGE,"536b5435-ed49-477c-9e18-1e00f24ad033"),sQuery(id+"FOPml0yl2Jk7fKW_31.wireOp",EDGE,"61a42ef3-f019-43e7-a5e8-2940e1e5efea"),sQuery(id+"FOPml0yl2Jk7fKW_31.wireOp",EDGE,"95ac03bb-7fc7-4b4d-acbb-991c92af0d0a"),sQuery(id+"FOPml0yl2Jk7fKW_31.wireOp",EDGE,"5aade96a-d11e-4fc7-ab06-94c628c1427f"),sQuery(id+"FOPml0yl2Jk7fKW_31.wireOp",EDGE,"2e769678-4454-41fb-933d-1bb54854dca2"),sQuery(id+"FOPml0yl2Jk7fKW_31.wireOp",EDGE,"c36a2c6f-c552-42c3-a586-0b04050a01cc"),sQuery(id+"FOPml0yl2Jk7fKW_31.wireOp",EDGE,"335dd668-d68b-49b1-9277-187dbc08377b"),sQuery(id+"FOPml0yl2Jk7fKW_31.wireOp",EDGE,"006e7f81-8c76-4a35-a943-7061cd43d9c5"),sQuery(id+"FOPml0yl2Jk7fKW_31.wireOp",EDGE,"9abdf55b-5e6b-4bd3-af04-a2bfb4a07eee"),sQuery(id+"FOPml0yl2Jk7fKW_31.wireOp",EDGE,"e53953d0-4a05-4919-89ad-8f6ef79b7361"),sQuery(id+"FOPml0yl2Jk7fKW_31.wireOp",EDGE,"3e88406a-1a6d-46f1-be93-68f28babb0bd"),sQuery(id+"FOPml0yl2Jk7fKW_31.wireOp",EDGE,"91e26c78-73d5-4315-a8b5-f420a0c42376"),sQuery(id+"FOPml0yl2Jk7fKW_31.wireOp",EDGE,"ab74857e-1455-4d7d-b1b4-4d03f960c2fc"),sQuery(id+"FOPml0yl2Jk7fKW_31.wireOp",EDGE,"a61aeefc-0abb-4e22-bf82-765b231e8f6b"),sQuery(id+"FOPml0yl2Jk7fKW_31.wireOp",EDGE,"3d7438c1-35f7-456f-b937-b9e73dd24b38"),sQuery(id+"FOPml0yl2Jk7fKW_31.wireOp",EDGE,"6d1153f2-7b69-4286-8c5f-554cf9f2adcd"),sQuery(id+"FOPml0yl2Jk7fKW_31.wireOp",EDGE,"af5c2901-1e2f-4246-b5ef-ccae2dd77f05"),sQuery(id+"FOPml0yl2Jk7fKW_31.wireOp",EDGE,"27a268ac-5449-48fc-acbe-b83c6fef4637"),sQuery(id+"FOPml0yl2Jk7fKW_31.wireOp",EDGE,"bfe51f0e-0cd1-4f3a-b7ab-f2a18ba22d42"),sQuery(id+"FOPml0yl2Jk7fKW_31.wireOp",EDGE,"966c3027-7ded-48b7-979c-ad3f55f5903d"),sQuery(id+"FOPml0yl2Jk7fKW_31.wireOp",EDGE,"9e80dd12-17df-4d6b-acb0-86b1ed9963f6"),sQuery(id+"FOPml0yl2Jk7fKW_31.wireOp",EDGE,"a50e4d2b-e87c-4655-b14b-9c11a8d5dc7b"),sQuery(id+"FOPml0yl2Jk7fKW_31.wireOp",EDGE,"2cc7393e-566a-491b-9fb9-9bf382267589"),sQuery(id+"FOPml0yl2Jk7fKW_31.wireOp",EDGE,"747de43c-a050-401c-8f69-154d70cb6777"),sQuery(id+"FOPml0yl2Jk7fKW_31.wireOp",EDGE,"247f6300-be28-46d9-b974-0d9f20feb396"),sQuery(id+"FOPml0yl2Jk7fKW_31.wireOp",EDGE,"c9ae6c1a-488d-4aac-9153-553311f2a7f3"),sQuery(id+"FOPml0yl2Jk7fKW_31.wireOp",EDGE,"b47b96cc-e86f-466e-8792-d0d70b965ac3"),sQuery(id+"FOPml0yl2Jk7fKW_31.wireOp",EDGE,"2ce67c51-a55a-4ec8-b1c7-b79dfe193feb"),sQuery(id+"FOPml0yl2Jk7fKW_31.wireOp",EDGE,"2070494c-c7e6-4e35-bf1f-c0a6041a3562"),sQuery(id+"FOPml0yl2Jk7fKW_31.wireOp",EDGE,"14f2d033-cead-4aca-b2da-2da579ad0257"),sQuery(id+"FOPml0yl2Jk7fKW_31.wireOp",EDGE,"35be7cf5-1903-49e2-8a9b-b0c9360c85bf"),sQuery(id+"FOPml0yl2Jk7fKW_31.wireOp",EDGE,"8764d209-61b0-4c42-addb-87d8d80455f5"),sQuery(id+"FOPml0yl2Jk7fKW_31.wireOp",EDGE,"b9f6ea56-478c-4cf0-baf6-132b954c7465"),sQuery(id+"FOPml0yl2Jk7fKW_31.wireOp",EDGE,"749f397b-ee23-41bb-808a-2bf4d39f65c0"),sQuery(id+"FOPml0yl2Jk7fKW_31.wireOp",EDGE,"7f3921a6-4bf3-48cb-8387-746dce681195"),sQuery(id+"FOPml0yl2Jk7fKW_31.wireOp",EDGE,"fb237c9d-e773-4d0e-979e-88d4384f2ee4"),sQuery(id+"FOPml0yl2Jk7fKW_31.wireOp",EDGE,"a1fd7c20-778c-48ef-8189-8ac2805e079e"),sQuery(id+"FOPml0yl2Jk7fKW_31.wireOp",EDGE,"d82dab23-d154-4423-a4f0-8b66d3084887"),sQuery(id+"FOPml0yl2Jk7fKW_31.wireOp",EDGE,"1ba84e47-1318-46a3-b6b3-5987cfbddaf3"),sQuery(id+"FOPml0yl2Jk7fKW_31.wireOp",EDGE,"48d5baf6-bc33-4775-ab6f-e4daad4a57e8"),sQuery(id+"FOPml0yl2Jk7fKW_31.wireOp",EDGE,"bbdca6bc-9190-4a09-bd2b-97c34e90ae9c"),sQuery(id+"FOPml0yl2Jk7fKW_31.wireOp",EDGE,"afc9e1d0-4b62-465f-a82d-e30427e66e39"),sQuery(id+"FOPml0yl2Jk7fKW_31.wireOp",EDGE,"d3db82ad-5cc1-4fe0-be5b-e1309f796547"),sQuery(id+"FOPml0yl2Jk7fKW_31.wireOp",EDGE,"3341af39-11b9-473e-89ca-2210c0dec69d"),sQuery(id+"FOPml0yl2Jk7fKW_31.wireOp",EDGE,"16975053-289d-4ac3-8437-0390c789bd20"),sQuery(id+"FOPml0yl2Jk7fKW_31.wireOp",EDGE,"2aea9c98-3088-47ef-b533-1cc323284c5b"),sQuery(id+"FOPml0yl2Jk7fKW_31.wireOp",EDGE,"5d134228-ca81-4058-877b-bbaa6e63b3b8"),sQuery(id+"FOPml0yl2Jk7fKW_31.wireOp",EDGE,"7c86e244-6830-475a-81b4-91786544a894"),sQuery(id+"FOPml0yl2Jk7fKW_31.wireOp",EDGE,"db93a9c2-4194-4750-a7be-d2cd1e092b56"),sQuery(id+"FOPml0yl2Jk7fKW_31.wireOp",EDGE,"bfe3e11c-784f-4678-84bb-0e0a7e290920"),sQuery(id+"FOPml0yl2Jk7fKW_31.wireOp",EDGE,"ee2017c1-dd7a-42e6-81c1-560f03a6c69b"),sQuery(id+"FOPml0yl2Jk7fKW_31.wireOp",EDGE,"0a6bc8a1-2c05-4767-b6f6-922a65ce2acd"),sQuery(id+"FOPml0yl2Jk7fKW_31.wireOp",EDGE,"00b0ae41-5b74-495f-ab8c-0e130e1110be"),sQuery(id+"FOPml0yl2Jk7fKW_31.wireOp",EDGE,"d19bb39d-5a8f-4319-89fe-1c5729e939b7"),sQuery(id+"FOPml0yl2Jk7fKW_31.wireOp",EDGE,"a398578d-7860-4b25-a167-738dcb2e0f20"),sQuery(id+"FOPml0yl2Jk7fKW_31.wireOp",EDGE,"f1910f14-1e00-492c-a1f1-209401c08070"),sQuery(id+"FOPml0yl2Jk7fKW_31.wireOp",EDGE,"4da3c23c-7d30-41ec-bcbe-43941e2147bc"),sQuery(id+"FOPml0yl2Jk7fKW_31.wireOp",EDGE,"0dc6ee6f-e097-42a3-9659-b66b2df8fce8"),sQuery(id+"FOPml0yl2Jk7fKW_31.wireOp",EDGE,"265d30c0-f28c-486e-ab70-b9985f7a9efd"),sQuery(id+"FOPml0yl2Jk7fKW_31.wireOp",EDGE,"20c3dacb-0fc4-4bfd-8f1a-994ac2b57cd0"),sQuery(id+"FOPml0yl2Jk7fKW_31.wireOp",EDGE,"8e73290e-86d2-47ff-907d-3b59f79c2aba"),sQuery(id+"FOPml0yl2Jk7fKW_31.wireOp",EDGE,"bc10b15b-6ad7-4832-8c2e-e52fa5747fb5"),sQuery(id+"FOPml0yl2Jk7fKW_31.wireOp",EDGE,"0a3fa546-cf77-47a9-b80b-9d5126565dd3"),sQuery(id+"FOPml0yl2Jk7fKW_31.wireOp",EDGE,"45d72839-c2b9-448d-b715-4a76e5c41668"),sQuery(id+"FOPml0yl2Jk7fKW_31.wireOp",EDGE,"b6669528-8370-4e05-80ad-581ecce8866d"),sQuery(id+"FOPml0yl2Jk7fKW_31.wireOp",EDGE,"e0571132-82e4-4ef9-bf43-bc705680965e"),sQuery(id+"FOPml0yl2Jk7fKW_31.wireOp",EDGE,"4f78e7ac-b9fb-4157-913b-d850ddd3d0a4"),sQuery(id+"FOPml0yl2Jk7fKW_31.wireOp",EDGE,"7991d77d-a32c-491d-865b-20275f031cd5"),sQuery(id+"FOPml0yl2Jk7fKW_31.wireOp",EDGE,"09b0feed-db65-4fe7-80e9-20cfcbf700f3"),sQuery(id+"FOPml0yl2Jk7fKW_31.wireOp",EDGE,"e6754594-c35a-4bb2-8235-2d577586b8a9"),sQuery(id+"FOPml0yl2Jk7fKW_31.wireOp",EDGE,"73dde994-9267-4ebb-a488-69316f6f38d8"),sQuery(id+"FOPml0yl2Jk7fKW_31.wireOp",EDGE,"f12aff35-a14c-48a4-8661-cfc823d79e1d"),sQuery(id+"FOPml0yl2Jk7fKW_31.wireOp",EDGE,"2f7c1a29-a236-4d38-95c0-2bb3bd886a3d"),sQuery(id+"FOPml0yl2Jk7fKW_31.wireOp",EDGE,"37fa503e-aa6d-40a6-8825-be6b5e084ae7"),sQuery(id+"FOPml0yl2Jk7fKW_31.wireOp",EDGE,"151e63da-59c5-4744-99b4-c607d2c7154a"),sQuery(id+"FOPml0yl2Jk7fKW_31.wireOp",EDGE,"94871318-1df8-4eb2-942b-3277bad9108a"),sQuery(id+"FOPml0yl2Jk7fKW_31.wireOp",EDGE,"f85caef6-f0f1-467d-9ba5-cca5361397c8"),sQuery(id+"FOPml0yl2Jk7fKW_31.wireOp",EDGE,"8d64b0f5-0cd6-4ea1-9821-2887fa870762"),sQuery(id+"FOPml0yl2Jk7fKW_31.wireOp",EDGE,"b0a631fa-68fe-42e5-8000-e0c8d53f55b0"),sQuery(id+"FOPml0yl2Jk7fKW_31.wireOp",EDGE,"6de85c98-21ef-41fa-b8ae-660c4da29c91"),sQuery(id+"FOPml0yl2Jk7fKW_31.wireOp",EDGE,"a782e28f-f040-44a7-9212-569a716607f4"),sQuery(id+"FOPml0yl2Jk7fKW_31.wireOp",EDGE,"b945f914-dd3e-46dd-951e-d0ce771b674a"),sQuery(id+"FOPml0yl2Jk7fKW_31.wireOp",EDGE,"709fee56-da18-4622-98ca-5a94ff774b82"),sQuery(id+"FOPml0yl2Jk7fKW_31.wireOp",EDGE,"619bcbb1-09f2-42ea-a9f2-ef3f28fdebb6"),sQuery(id+"FOPml0yl2Jk7fKW_31.wireOp",EDGE,"8e141f8a-1b5b-4aed-a4af-ee29278768d3"),sQuery(id+"FOPml0yl2Jk7fKW_31.wireOp",EDGE,"4244b88c-2251-4d39-a618-038c3c3a81f5"),sQuery(id+"FOPml0yl2Jk7fKW_31.wireOp",EDGE,"d9894beb-23b8-4346-9034-218e07a00b4d"),sQuery(id+"FOPml0yl2Jk7fKW_31.wireOp",EDGE,"7be5db43-15c0-4a66-bacf-002c184f96cc"),sQuery(id+"FOPml0yl2Jk7fKW_31.wireOp",EDGE,"c813d457-6cf0-411c-aa0a-b66d892dc7de"),sQuery(id+"FOPml0yl2Jk7fKW_31.wireOp",EDGE,"3fa8c262-0fce-46f4-88a6-69263d4b88f7"),sQuery(id+"FOPml0yl2Jk7fKW_31.wireOp",EDGE,"cc6fe043-e0cf-4ec1-b785-81c2aa7e5601"),sQuery(id+"FOPml0yl2Jk7fKW_31.wireOp",EDGE,"ce9fad71-14f0-4fd3-82d5-80fce325acb8"),sQuery(id+"FOPml0yl2Jk7fKW_31.wireOp",EDGE,"1f275fad-f1df-43d6-aceb-a7a3b5c1dbd3"),sQuery(id+"FOPml0yl2Jk7fKW_31.wireOp",EDGE,"35003d0d-a7fc-4aef-a17c-9d7e9f14a443"),sQuery(id+"FOPml0yl2Jk7fKW_31.wireOp",EDGE,"785f931a-7ecc-46e1-a620-0a3d5a908d79"),sQuery(id+"FOPml0yl2Jk7fKW_31.wireOp",EDGE,"5a24f98f-da9c-45c0-bab6-ab16bc493336"),sQuery(id+"FOPml0yl2Jk7fKW_31.wireOp",EDGE,"67369da4-4bbd-4007-80e3-cf84763fbfc2"),sQuery(id+"FOPml0yl2Jk7fKW_31.wireOp",EDGE,"2941fdf3-37bb-4c91-bc1b-8cb115d6c299"),sQuery(id+"FOPml0yl2Jk7fKW_31.wireOp",EDGE,"29a5619b-5cc3-452e-a78d-70568d3208d8")])]});
            transform(context, id + "F12", {"entities" : qUnion([Q0, Q1, Q2, Q3, Q4, Q5, Q6, Q7, Q8, Q9, Q10, Q11, Q12, Q13, Q14, Q15, Q16, Q17, Q18, Q19, Q20, Q21, Q22, Q23, Q24, Q25, Q26, Q27, Q28, Q29, Q30, Q31, Q32]), "transformType" : TransformType.COPY});
        }
    });
